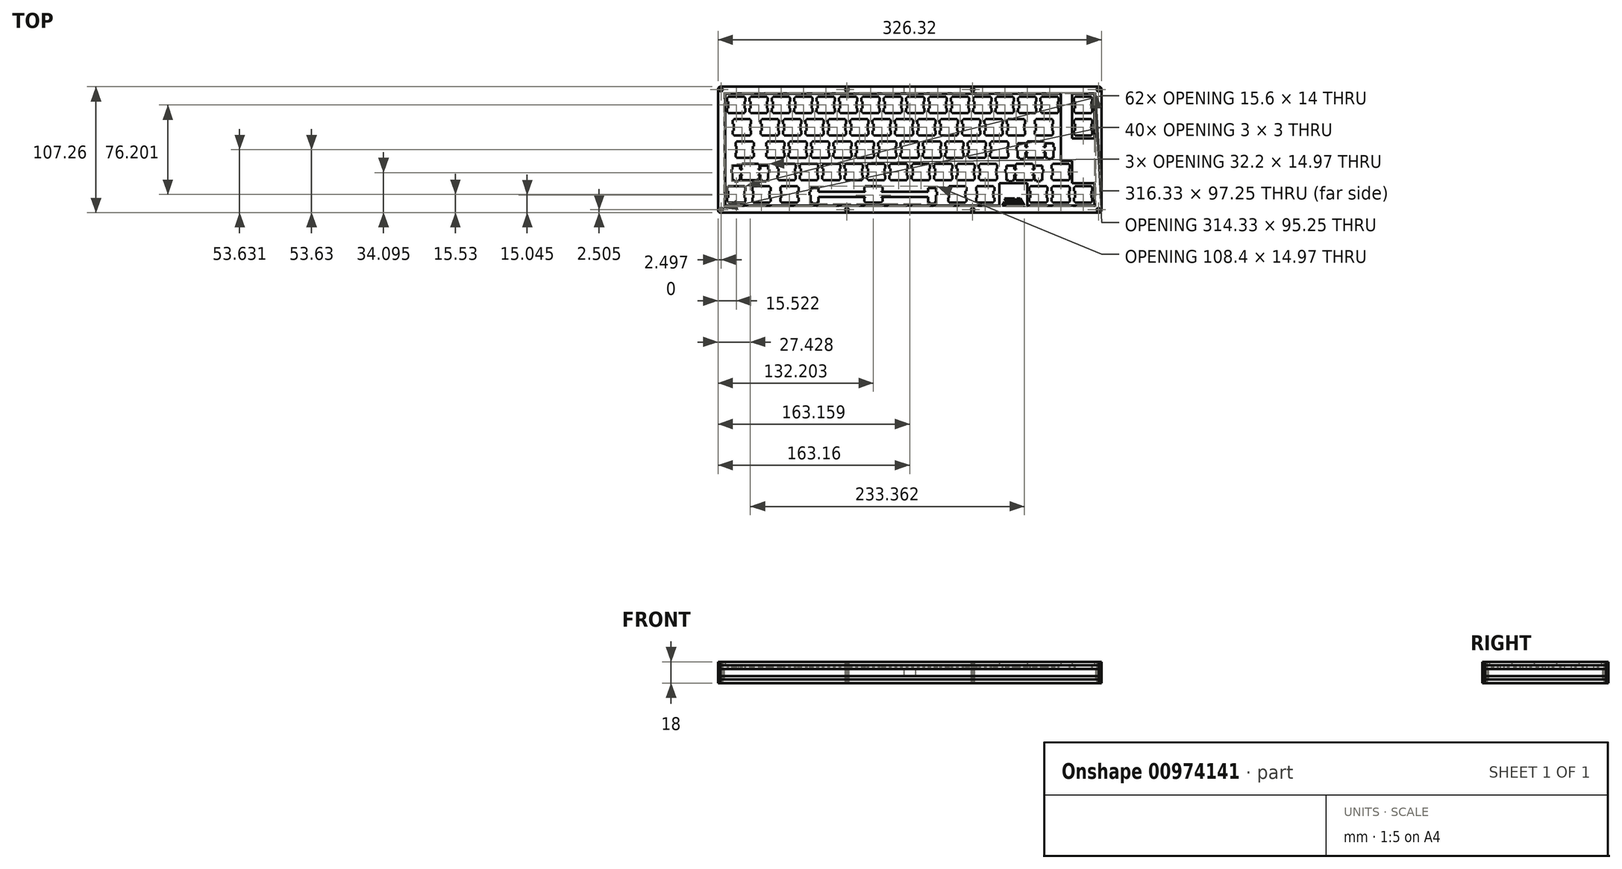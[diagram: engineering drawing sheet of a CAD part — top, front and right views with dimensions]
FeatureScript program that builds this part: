
annotation { "Feature Type Name" : "Feature", "Feature Type Description" : "" }
export const myFeature = defineFeature(function(context is Context, id is Id, definition is map)
    precondition{}
    {
        {
            assignVariable(context, id + "F0", {"name" : "Thickness", "anyValue" : 3});
        }
        {
            var Q0;
            Q0=qCreatedBy(makeId("Top.planeOp"),FACE);
            var sketch = newSketch(context, id + "F1", { "sketchPlane" : qUnion([Q0])});
            skLineSegment(sketch, "E0", {"start": v(161.16, 53.62) * mm, "end": v(161.32, 53.62) * mm});
            skLineSegment(sketch, "E1", {"start": v(161.32, 53.62) * mm, "end": v(161.48, 53.6) * mm});
            skLineSegment(sketch, "E2", {"start": v(161.48, 53.6) * mm, "end": v(161.63, 53.57) * mm});
            skLineSegment(sketch, "E3", {"start": v(161.63, 53.57) * mm, "end": v(161.78, 53.53) * mm});
            skLineSegment(sketch, "E4", {"start": v(161.78, 53.53) * mm, "end": v(161.93, 53.47) * mm});
            skLineSegment(sketch, "E5", {"start": v(161.93, 53.47) * mm, "end": v(162.07, 53.4) * mm});
            skLineSegment(sketch, "E6", {"start": v(162.07, 53.4) * mm, "end": v(162.2, 53.33) * mm});
            skLineSegment(sketch, "E7", {"start": v(162.2, 53.33) * mm, "end": v(162.34, 53.24) * mm});
            skLineSegment(sketch, "E8", {"start": v(162.34, 53.24) * mm, "end": v(162.46, 53.15) * mm});
            skLineSegment(sketch, "E9", {"start": v(162.46, 53.15) * mm, "end": v(162.58, 53.04) * mm});
            skLineSegment(sketch, "E10", {"start": v(162.58, 53.04) * mm, "end": v(162.68, 52.92) * mm});
            skLineSegment(sketch, "E11", {"start": v(162.68, 52.92) * mm, "end": v(162.78, 52.8) * mm});
            skLineSegment(sketch, "E12", {"start": v(162.78, 52.8) * mm, "end": v(162.87, 52.67) * mm});
            skLineSegment(sketch, "E13", {"start": v(162.87, 52.67) * mm, "end": v(162.94, 52.53) * mm});
            skLineSegment(sketch, "E14", {"start": v(162.94, 52.53) * mm, "end": v(163, 52.4) * mm});
            skLineSegment(sketch, "E15", {"start": v(163, 52.4) * mm, "end": v(163.06, 52.24) * mm});
            skLineSegment(sketch, "E16", {"start": v(163.06, 52.24) * mm, "end": v(163.1, 52.1) * mm});
            skLineSegment(sketch, "E17", {"start": v(163.1, 52.1) * mm, "end": v(163.14, 51.94) * mm});
            skLineSegment(sketch, "E18", {"start": v(163.14, 51.94) * mm, "end": v(163.16, 51.78) * mm});
            skLineSegment(sketch, "E19", {"start": v(163.16, 51.78) * mm, "end": v(163.16, 51.62) * mm});
            skLineSegment(sketch, "E20", {"start": v(163.16, 51.62) * mm, "end": v(163.16, -51.62) * mm});
            skLineSegment(sketch, "E21", {"start": v(163.16, -51.62) * mm, "end": v(163.16, -51.78) * mm});
            skLineSegment(sketch, "E22", {"start": v(163.16, -51.78) * mm, "end": v(163.14, -51.94) * mm});
            skLineSegment(sketch, "E23", {"start": v(163.14, -51.94) * mm, "end": v(163.1, -52.1) * mm});
            skLineSegment(sketch, "E24", {"start": v(163.1, -52.1) * mm, "end": v(163.06, -52.25) * mm});
            skLineSegment(sketch, "E25", {"start": v(163.06, -52.25) * mm, "end": v(163, -52.4) * mm});
            skLineSegment(sketch, "E26", {"start": v(163, -52.4) * mm, "end": v(162.94, -52.53) * mm});
            skLineSegment(sketch, "E27", {"start": v(162.94, -52.53) * mm, "end": v(162.87, -52.67) * mm});
            skLineSegment(sketch, "E28", {"start": v(162.87, -52.67) * mm, "end": v(162.78, -52.8) * mm});
            skLineSegment(sketch, "E29", {"start": v(162.78, -52.8) * mm, "end": v(162.68, -52.92) * mm});
            skLineSegment(sketch, "E30", {"start": v(162.68, -52.92) * mm, "end": v(162.58, -53.04) * mm});
            skLineSegment(sketch, "E31", {"start": v(162.58, -53.04) * mm, "end": v(162.46, -53.15) * mm});
            skLineSegment(sketch, "E32", {"start": v(162.46, -53.15) * mm, "end": v(162.34, -53.24) * mm});
            skLineSegment(sketch, "E33", {"start": v(162.34, -53.24) * mm, "end": v(162.2, -53.33) * mm});
            skLineSegment(sketch, "E34", {"start": v(162.2, -53.33) * mm, "end": v(162.07, -53.4) * mm});
            skLineSegment(sketch, "E35", {"start": v(162.07, -53.4) * mm, "end": v(161.93, -53.47) * mm});
            skLineSegment(sketch, "E36", {"start": v(161.93, -53.47) * mm, "end": v(161.78, -53.53) * mm});
            skLineSegment(sketch, "E37", {"start": v(161.78, -53.53) * mm, "end": v(161.63, -53.57) * mm});
            skLineSegment(sketch, "E38", {"start": v(161.63, -53.57) * mm, "end": v(161.48, -53.6) * mm});
            skLineSegment(sketch, "E39", {"start": v(161.48, -53.6) * mm, "end": v(161.32, -53.62) * mm});
            skLineSegment(sketch, "E40", {"start": v(161.32, -53.62) * mm, "end": v(161.16, -53.63) * mm});
            skLineSegment(sketch, "E41", {"start": v(161.16, -53.63) * mm, "end": v(-161.16, -53.63) * mm});
            skLineSegment(sketch, "E42", {"start": v(-161.16, -53.63) * mm, "end": v(-161.32, -53.62) * mm});
            skLineSegment(sketch, "E43", {"start": v(-161.32, -53.62) * mm, "end": v(-161.48, -53.6) * mm});
            skLineSegment(sketch, "E44", {"start": v(-161.48, -53.6) * mm, "end": v(-161.63, -53.57) * mm});
            skLineSegment(sketch, "E45", {"start": v(-161.63, -53.57) * mm, "end": v(-161.78, -53.53) * mm});
            skLineSegment(sketch, "E46", {"start": v(-161.78, -53.53) * mm, "end": v(-161.93, -53.47) * mm});
            skLineSegment(sketch, "E47", {"start": v(-161.93, -53.47) * mm, "end": v(-162.07, -53.4) * mm});
            skLineSegment(sketch, "E48", {"start": v(-162.07, -53.4) * mm, "end": v(-162.2, -53.33) * mm});
            skLineSegment(sketch, "E49", {"start": v(-162.2, -53.33) * mm, "end": v(-162.34, -53.24) * mm});
            skLineSegment(sketch, "E50", {"start": v(-162.34, -53.24) * mm, "end": v(-162.46, -53.15) * mm});
            skLineSegment(sketch, "E51", {"start": v(-162.46, -53.15) * mm, "end": v(-162.58, -53.04) * mm});
            skLineSegment(sketch, "E52", {"start": v(-162.58, -53.04) * mm, "end": v(-162.68, -52.92) * mm});
            skLineSegment(sketch, "E53", {"start": v(-162.68, -52.92) * mm, "end": v(-162.78, -52.8) * mm});
            skLineSegment(sketch, "E54", {"start": v(-162.78, -52.8) * mm, "end": v(-162.87, -52.67) * mm});
            skLineSegment(sketch, "E55", {"start": v(-162.87, -52.67) * mm, "end": v(-162.95, -52.53) * mm});
            skLineSegment(sketch, "E56", {"start": v(-162.95, -52.53) * mm, "end": v(-163.01, -52.4) * mm});
            skLineSegment(sketch, "E57", {"start": v(-163.01, -52.4) * mm, "end": v(-163.07, -52.25) * mm});
            skLineSegment(sketch, "E58", {"start": v(-163.07, -52.25) * mm, "end": v(-163.1, -52.1) * mm});
            skLineSegment(sketch, "E59", {"start": v(-163.1, -52.1) * mm, "end": v(-163.14, -51.94) * mm});
            skLineSegment(sketch, "E60", {"start": v(-163.14, -51.94) * mm, "end": v(-163.16, -51.78) * mm});
            skLineSegment(sketch, "E61", {"start": v(-163.16, -51.78) * mm, "end": v(-163.16, -51.63) * mm});
            skLineSegment(sketch, "E62", {"start": v(-163.16, -51.63) * mm, "end": v(-163.16, 51.62) * mm});
            skLineSegment(sketch, "E63", {"start": v(-163.16, 51.62) * mm, "end": v(-163.16, 51.78) * mm});
            skLineSegment(sketch, "E64", {"start": v(-163.16, 51.78) * mm, "end": v(-163.14, 51.94) * mm});
            skLineSegment(sketch, "E65", {"start": v(-163.14, 51.94) * mm, "end": v(-163.1, 52.1) * mm});
            skLineSegment(sketch, "E66", {"start": v(-163.1, 52.1) * mm, "end": v(-163.07, 52.24) * mm});
            skLineSegment(sketch, "E67", {"start": v(-163.07, 52.24) * mm, "end": v(-163.01, 52.4) * mm});
            skLineSegment(sketch, "E68", {"start": v(-163.01, 52.4) * mm, "end": v(-162.95, 52.53) * mm});
            skLineSegment(sketch, "E69", {"start": v(-162.95, 52.53) * mm, "end": v(-162.87, 52.67) * mm});
            skLineSegment(sketch, "E70", {"start": v(-162.87, 52.67) * mm, "end": v(-162.78, 52.8) * mm});
            skLineSegment(sketch, "E71", {"start": v(-162.78, 52.8) * mm, "end": v(-162.68, 52.92) * mm});
            skLineSegment(sketch, "E72", {"start": v(-162.68, 52.92) * mm, "end": v(-162.58, 53.04) * mm});
            skLineSegment(sketch, "E73", {"start": v(-162.58, 53.04) * mm, "end": v(-162.46, 53.15) * mm});
            skLineSegment(sketch, "E74", {"start": v(-162.46, 53.15) * mm, "end": v(-162.34, 53.24) * mm});
            skLineSegment(sketch, "E75", {"start": v(-162.34, 53.24) * mm, "end": v(-162.2, 53.33) * mm});
            skLineSegment(sketch, "E76", {"start": v(-162.2, 53.33) * mm, "end": v(-162.07, 53.4) * mm});
            skLineSegment(sketch, "E77", {"start": v(-162.07, 53.4) * mm, "end": v(-161.93, 53.47) * mm});
            skLineSegment(sketch, "E78", {"start": v(-161.93, 53.47) * mm, "end": v(-161.78, 53.53) * mm});
            skLineSegment(sketch, "E79", {"start": v(-161.78, 53.53) * mm, "end": v(-161.63, 53.57) * mm});
            skLineSegment(sketch, "E80", {"start": v(-161.63, 53.57) * mm, "end": v(-161.48, 53.6) * mm});
            skLineSegment(sketch, "E81", {"start": v(-161.48, 53.6) * mm, "end": v(-161.32, 53.62) * mm});
            skLineSegment(sketch, "E82", {"start": v(-161.32, 53.62) * mm, "end": v(-161.16, 53.63) * mm});
            skLineSegment(sketch, "E83", {"start": v(-161.16, 53.63) * mm, "end": v(161.16, 53.62) * mm});
            skLineSegment(sketch, "E84", {"start": v(160.2, -49.7) * mm, "end": v(159.78, -49.91) * mm});
            skLineSegment(sketch, "E85", {"start": v(159.78, -49.91) * mm, "end": v(159.45, -50.24) * mm});
            skLineSegment(sketch, "E86", {"start": v(159.45, -50.24) * mm, "end": v(159.24, -50.66) * mm});
            skLineSegment(sketch, "E87", {"start": v(159.24, -50.66) * mm, "end": v(159.16, -51.13) * mm});
            skLineSegment(sketch, "E88", {"start": v(159.16, -51.13) * mm, "end": v(159.24, -51.59) * mm});
            skLineSegment(sketch, "E89", {"start": v(159.24, -51.59) * mm, "end": v(159.45, -52) * mm});
            skLineSegment(sketch, "E90", {"start": v(159.45, -52) * mm, "end": v(159.78, -52.34) * mm});
            skLineSegment(sketch, "E91", {"start": v(159.78, -52.34) * mm, "end": v(160.2, -52.55) * mm});
            skLineSegment(sketch, "E92", {"start": v(160.2, -52.55) * mm, "end": v(160.66, -52.63) * mm});
            skLineSegment(sketch, "E93", {"start": v(160.66, -52.63) * mm, "end": v(161.13, -52.55) * mm});
            skLineSegment(sketch, "E94", {"start": v(161.13, -52.55) * mm, "end": v(161.54, -52.34) * mm});
            skLineSegment(sketch, "E95", {"start": v(161.54, -52.34) * mm, "end": v(161.88, -52) * mm});
            skLineSegment(sketch, "E96", {"start": v(161.88, -52) * mm, "end": v(162.09, -51.59) * mm});
            skLineSegment(sketch, "E97", {"start": v(162.09, -51.59) * mm, "end": v(162.16, -51.13) * mm});
            skLineSegment(sketch, "E98", {"start": v(162.16, -51.13) * mm, "end": v(162.09, -50.66) * mm});
            skLineSegment(sketch, "E99", {"start": v(162.09, -50.66) * mm, "end": v(161.88, -50.24) * mm});
            skLineSegment(sketch, "E100", {"start": v(161.88, -50.24) * mm, "end": v(161.54, -49.91) * mm});
            skLineSegment(sketch, "E101", {"start": v(161.54, -49.91) * mm, "end": v(161.13, -49.7) * mm});
            skLineSegment(sketch, "E102", {"start": v(161.13, -49.7) * mm, "end": v(160.66, -49.63) * mm});
            skLineSegment(sketch, "E103", {"start": v(160.66, -49.63) * mm, "end": v(160.2, -49.7) * mm});
            skLineSegment(sketch, "E104", {"start": v(53.1, -49.7) * mm, "end": v(52.67, -49.91) * mm});
            skLineSegment(sketch, "E105", {"start": v(52.67, -49.91) * mm, "end": v(52.34, -50.24) * mm});
            skLineSegment(sketch, "E106", {"start": v(52.34, -50.24) * mm, "end": v(52.13, -50.66) * mm});
            skLineSegment(sketch, "E107", {"start": v(52.13, -50.66) * mm, "end": v(52.05, -51.13) * mm});
            skLineSegment(sketch, "E108", {"start": v(52.05, -51.13) * mm, "end": v(52.13, -51.59) * mm});
            skLineSegment(sketch, "E109", {"start": v(52.13, -51.59) * mm, "end": v(52.34, -52) * mm});
            skLineSegment(sketch, "E110", {"start": v(52.34, -52) * mm, "end": v(52.67, -52.34) * mm});
            skLineSegment(sketch, "E111", {"start": v(52.67, -52.34) * mm, "end": v(53.1, -52.55) * mm});
            skLineSegment(sketch, "E112", {"start": v(53.1, -52.55) * mm, "end": v(53.55, -52.63) * mm});
            skLineSegment(sketch, "E113", {"start": v(53.55, -52.63) * mm, "end": v(54.02, -52.55) * mm});
            skLineSegment(sketch, "E114", {"start": v(54.02, -52.55) * mm, "end": v(54.44, -52.34) * mm});
            skLineSegment(sketch, "E115", {"start": v(54.44, -52.34) * mm, "end": v(54.77, -52) * mm});
            skLineSegment(sketch, "E116", {"start": v(54.77, -52) * mm, "end": v(54.98, -51.59) * mm});
            skLineSegment(sketch, "E117", {"start": v(54.98, -51.59) * mm, "end": v(55.05, -51.13) * mm});
            skLineSegment(sketch, "E118", {"start": v(55.05, -51.13) * mm, "end": v(54.98, -50.66) * mm});
            skLineSegment(sketch, "E119", {"start": v(54.98, -50.66) * mm, "end": v(54.77, -50.24) * mm});
            skLineSegment(sketch, "E120", {"start": v(54.77, -50.24) * mm, "end": v(54.44, -49.91) * mm});
            skLineSegment(sketch, "E121", {"start": v(54.44, -49.91) * mm, "end": v(54.02, -49.7) * mm});
            skLineSegment(sketch, "E122", {"start": v(54.02, -49.7) * mm, "end": v(53.55, -49.63) * mm});
            skLineSegment(sketch, "E123", {"start": v(53.55, -49.63) * mm, "end": v(53.1, -49.7) * mm});
            skLineSegment(sketch, "E124", {"start": v(-54.02, -49.7) * mm, "end": v(-54.44, -49.91) * mm});
            skLineSegment(sketch, "E125", {"start": v(-54.44, -49.91) * mm, "end": v(-54.77, -50.24) * mm});
            skLineSegment(sketch, "E126", {"start": v(-54.77, -50.24) * mm, "end": v(-54.98, -50.66) * mm});
            skLineSegment(sketch, "E127", {"start": v(-54.98, -50.66) * mm, "end": v(-55.06, -51.13) * mm});
            skLineSegment(sketch, "E128", {"start": v(-55.06, -51.13) * mm, "end": v(-54.98, -51.59) * mm});
            skLineSegment(sketch, "E129", {"start": v(-54.98, -51.59) * mm, "end": v(-54.77, -52) * mm});
            skLineSegment(sketch, "E130", {"start": v(-54.77, -52) * mm, "end": v(-54.44, -52.34) * mm});
            skLineSegment(sketch, "E131", {"start": v(-54.44, -52.34) * mm, "end": v(-54.02, -52.55) * mm});
            skLineSegment(sketch, "E132", {"start": v(-54.02, -52.55) * mm, "end": v(-53.55, -52.63) * mm});
            skLineSegment(sketch, "E133", {"start": v(-53.55, -52.63) * mm, "end": v(-53.1, -52.55) * mm});
            skLineSegment(sketch, "E134", {"start": v(-53.1, -52.55) * mm, "end": v(-52.67, -52.34) * mm});
            skLineSegment(sketch, "E135", {"start": v(-52.67, -52.34) * mm, "end": v(-52.34, -52) * mm});
            skLineSegment(sketch, "E136", {"start": v(-52.34, -52) * mm, "end": v(-52.13, -51.59) * mm});
            skLineSegment(sketch, "E137", {"start": v(-52.13, -51.59) * mm, "end": v(-52.06, -51.13) * mm});
            skLineSegment(sketch, "E138", {"start": v(-52.06, -51.13) * mm, "end": v(-52.13, -50.66) * mm});
            skLineSegment(sketch, "E139", {"start": v(-52.13, -50.66) * mm, "end": v(-52.34, -50.24) * mm});
            skLineSegment(sketch, "E140", {"start": v(-52.34, -50.24) * mm, "end": v(-52.67, -49.91) * mm});
            skLineSegment(sketch, "E141", {"start": v(-52.67, -49.91) * mm, "end": v(-53.1, -49.7) * mm});
            skLineSegment(sketch, "E142", {"start": v(-53.1, -49.7) * mm, "end": v(-53.55, -49.63) * mm});
            skLineSegment(sketch, "E143", {"start": v(-53.55, -49.63) * mm, "end": v(-54.02, -49.7) * mm});
            skLineSegment(sketch, "E144", {"start": v(-161.13, -49.7) * mm, "end": v(-161.54, -49.91) * mm});
            skLineSegment(sketch, "E145", {"start": v(-161.54, -49.91) * mm, "end": v(-161.88, -50.24) * mm});
            skLineSegment(sketch, "E146", {"start": v(-161.88, -50.24) * mm, "end": v(-162.1, -50.66) * mm});
            skLineSegment(sketch, "E147", {"start": v(-162.1, -50.66) * mm, "end": v(-162.16, -51.13) * mm});
            skLineSegment(sketch, "E148", {"start": v(-162.16, -51.13) * mm, "end": v(-162.1, -51.59) * mm});
            skLineSegment(sketch, "E149", {"start": v(-162.1, -51.59) * mm, "end": v(-161.88, -52) * mm});
            skLineSegment(sketch, "E150", {"start": v(-161.88, -52) * mm, "end": v(-161.54, -52.34) * mm});
            skLineSegment(sketch, "E151", {"start": v(-161.54, -52.34) * mm, "end": v(-161.13, -52.55) * mm});
            skLineSegment(sketch, "E152", {"start": v(-161.13, -52.55) * mm, "end": v(-160.66, -52.63) * mm});
            skLineSegment(sketch, "E153", {"start": v(-160.66, -52.63) * mm, "end": v(-160.2, -52.55) * mm});
            skLineSegment(sketch, "E154", {"start": v(-160.2, -52.55) * mm, "end": v(-159.78, -52.34) * mm});
            skLineSegment(sketch, "E155", {"start": v(-159.78, -52.34) * mm, "end": v(-159.45, -52) * mm});
            skLineSegment(sketch, "E156", {"start": v(-159.45, -52) * mm, "end": v(-159.24, -51.59) * mm});
            skLineSegment(sketch, "E157", {"start": v(-159.24, -51.59) * mm, "end": v(-159.16, -51.13) * mm});
            skLineSegment(sketch, "E158", {"start": v(-159.16, -51.13) * mm, "end": v(-159.24, -50.66) * mm});
            skLineSegment(sketch, "E159", {"start": v(-159.24, -50.66) * mm, "end": v(-159.45, -50.24) * mm});
            skLineSegment(sketch, "E160", {"start": v(-159.45, -50.24) * mm, "end": v(-159.78, -49.91) * mm});
            skLineSegment(sketch, "E161", {"start": v(-159.78, -49.91) * mm, "end": v(-160.2, -49.7) * mm});
            skLineSegment(sketch, "E162", {"start": v(-160.2, -49.7) * mm, "end": v(-160.66, -49.63) * mm});
            skLineSegment(sketch, "E163", {"start": v(-160.66, -49.63) * mm, "end": v(-161.13, -49.7) * mm});
            skLineSegment(sketch, "E164", {"start": v(-54.02, 52.55) * mm, "end": v(-54.44, 52.34) * mm});
            skLineSegment(sketch, "E165", {"start": v(-54.44, 52.34) * mm, "end": v(-54.77, 52) * mm});
            skLineSegment(sketch, "E166", {"start": v(-54.77, 52) * mm, "end": v(-54.98, 51.59) * mm});
            skLineSegment(sketch, "E167", {"start": v(-54.98, 51.59) * mm, "end": v(-55.06, 51.12) * mm});
            skLineSegment(sketch, "E168", {"start": v(-55.06, 51.12) * mm, "end": v(-54.98, 50.66) * mm});
            skLineSegment(sketch, "E169", {"start": v(-54.98, 50.66) * mm, "end": v(-54.77, 50.24) * mm});
            skLineSegment(sketch, "E170", {"start": v(-54.77, 50.24) * mm, "end": v(-54.44, 49.91) * mm});
            skLineSegment(sketch, "E171", {"start": v(-54.44, 49.91) * mm, "end": v(-54.02, 49.7) * mm});
            skLineSegment(sketch, "E172", {"start": v(-54.02, 49.7) * mm, "end": v(-53.55, 49.62) * mm});
            skLineSegment(sketch, "E173", {"start": v(-53.55, 49.62) * mm, "end": v(-53.1, 49.7) * mm});
            skLineSegment(sketch, "E174", {"start": v(-53.1, 49.7) * mm, "end": v(-52.67, 49.91) * mm});
            skLineSegment(sketch, "E175", {"start": v(-52.67, 49.91) * mm, "end": v(-52.34, 50.24) * mm});
            skLineSegment(sketch, "E176", {"start": v(-52.34, 50.24) * mm, "end": v(-52.13, 50.66) * mm});
            skLineSegment(sketch, "E177", {"start": v(-52.13, 50.66) * mm, "end": v(-52.06, 51.12) * mm});
            skLineSegment(sketch, "E178", {"start": v(-52.06, 51.12) * mm, "end": v(-52.13, 51.59) * mm});
            skLineSegment(sketch, "E179", {"start": v(-52.13, 51.59) * mm, "end": v(-52.34, 52) * mm});
            skLineSegment(sketch, "E180", {"start": v(-52.34, 52) * mm, "end": v(-52.67, 52.34) * mm});
            skLineSegment(sketch, "E181", {"start": v(-52.67, 52.34) * mm, "end": v(-53.1, 52.55) * mm});
            skLineSegment(sketch, "E182", {"start": v(-53.1, 52.55) * mm, "end": v(-53.55, 52.62) * mm});
            skLineSegment(sketch, "E183", {"start": v(-53.55, 52.62) * mm, "end": v(-54.02, 52.55) * mm});
            skLineSegment(sketch, "E184", {"start": v(53.1, 52.55) * mm, "end": v(52.67, 52.34) * mm});
            skLineSegment(sketch, "E185", {"start": v(52.67, 52.34) * mm, "end": v(52.34, 52) * mm});
            skLineSegment(sketch, "E186", {"start": v(52.34, 52) * mm, "end": v(52.13, 51.59) * mm});
            skLineSegment(sketch, "E187", {"start": v(52.13, 51.59) * mm, "end": v(52.05, 51.12) * mm});
            skLineSegment(sketch, "E188", {"start": v(52.05, 51.12) * mm, "end": v(52.13, 50.66) * mm});
            skLineSegment(sketch, "E189", {"start": v(52.13, 50.66) * mm, "end": v(52.34, 50.24) * mm});
            skLineSegment(sketch, "E190", {"start": v(52.34, 50.24) * mm, "end": v(52.67, 49.91) * mm});
            skLineSegment(sketch, "E191", {"start": v(52.67, 49.91) * mm, "end": v(53.1, 49.7) * mm});
            skLineSegment(sketch, "E192", {"start": v(53.1, 49.7) * mm, "end": v(53.55, 49.62) * mm});
            skLineSegment(sketch, "E193", {"start": v(53.55, 49.62) * mm, "end": v(54.02, 49.7) * mm});
            skLineSegment(sketch, "E194", {"start": v(54.02, 49.7) * mm, "end": v(54.44, 49.91) * mm});
            skLineSegment(sketch, "E195", {"start": v(54.44, 49.91) * mm, "end": v(54.77, 50.24) * mm});
            skLineSegment(sketch, "E196", {"start": v(54.77, 50.24) * mm, "end": v(54.98, 50.66) * mm});
            skLineSegment(sketch, "E197", {"start": v(54.98, 50.66) * mm, "end": v(55.05, 51.12) * mm});
            skLineSegment(sketch, "E198", {"start": v(55.05, 51.12) * mm, "end": v(54.98, 51.59) * mm});
            skLineSegment(sketch, "E199", {"start": v(54.98, 51.59) * mm, "end": v(54.77, 52) * mm});
            skLineSegment(sketch, "E200", {"start": v(54.77, 52) * mm, "end": v(54.44, 52.34) * mm});
            skLineSegment(sketch, "E201", {"start": v(54.44, 52.34) * mm, "end": v(54.02, 52.55) * mm});
            skLineSegment(sketch, "E202", {"start": v(54.02, 52.55) * mm, "end": v(53.55, 52.62) * mm});
            skLineSegment(sketch, "E203", {"start": v(53.55, 52.62) * mm, "end": v(53.1, 52.55) * mm});
            skLineSegment(sketch, "E204", {"start": v(160.2, 52.55) * mm, "end": v(159.78, 52.34) * mm});
            skLineSegment(sketch, "E205", {"start": v(159.78, 52.34) * mm, "end": v(159.45, 52) * mm});
            skLineSegment(sketch, "E206", {"start": v(159.45, 52) * mm, "end": v(159.24, 51.59) * mm});
            skLineSegment(sketch, "E207", {"start": v(159.24, 51.59) * mm, "end": v(159.16, 51.12) * mm});
            skLineSegment(sketch, "E208", {"start": v(159.16, 51.12) * mm, "end": v(159.24, 50.66) * mm});
            skLineSegment(sketch, "E209", {"start": v(159.24, 50.66) * mm, "end": v(159.45, 50.24) * mm});
            skLineSegment(sketch, "E210", {"start": v(159.45, 50.24) * mm, "end": v(159.78, 49.91) * mm});
            skLineSegment(sketch, "E211", {"start": v(159.78, 49.91) * mm, "end": v(160.2, 49.7) * mm});
            skLineSegment(sketch, "E212", {"start": v(160.2, 49.7) * mm, "end": v(160.66, 49.62) * mm});
            skLineSegment(sketch, "E213", {"start": v(160.66, 49.62) * mm, "end": v(161.13, 49.7) * mm});
            skLineSegment(sketch, "E214", {"start": v(161.13, 49.7) * mm, "end": v(161.54, 49.91) * mm});
            skLineSegment(sketch, "E215", {"start": v(161.54, 49.91) * mm, "end": v(161.88, 50.24) * mm});
            skLineSegment(sketch, "E216", {"start": v(161.88, 50.24) * mm, "end": v(162.09, 50.66) * mm});
            skLineSegment(sketch, "E217", {"start": v(162.09, 50.66) * mm, "end": v(162.16, 51.12) * mm});
            skLineSegment(sketch, "E218", {"start": v(162.16, 51.12) * mm, "end": v(162.09, 51.59) * mm});
            skLineSegment(sketch, "E219", {"start": v(162.09, 51.59) * mm, "end": v(161.88, 52) * mm});
            skLineSegment(sketch, "E220", {"start": v(161.88, 52) * mm, "end": v(161.54, 52.34) * mm});
            skLineSegment(sketch, "E221", {"start": v(161.54, 52.34) * mm, "end": v(161.13, 52.55) * mm});
            skLineSegment(sketch, "E222", {"start": v(161.13, 52.55) * mm, "end": v(160.66, 52.62) * mm});
            skLineSegment(sketch, "E223", {"start": v(160.66, 52.62) * mm, "end": v(160.2, 52.55) * mm});
            skLineSegment(sketch, "E224", {"start": v(-161.13, 52.55) * mm, "end": v(-161.54, 52.34) * mm});
            skLineSegment(sketch, "E225", {"start": v(-161.54, 52.34) * mm, "end": v(-161.88, 52) * mm});
            skLineSegment(sketch, "E226", {"start": v(-161.88, 52) * mm, "end": v(-162.1, 51.59) * mm});
            skLineSegment(sketch, "E227", {"start": v(-162.1, 51.59) * mm, "end": v(-162.16, 51.12) * mm});
            skLineSegment(sketch, "E228", {"start": v(-162.16, 51.12) * mm, "end": v(-162.1, 50.66) * mm});
            skLineSegment(sketch, "E229", {"start": v(-162.1, 50.66) * mm, "end": v(-161.88, 50.24) * mm});
            skLineSegment(sketch, "E230", {"start": v(-161.88, 50.24) * mm, "end": v(-161.54, 49.91) * mm});
            skLineSegment(sketch, "E231", {"start": v(-161.54, 49.91) * mm, "end": v(-161.13, 49.7) * mm});
            skLineSegment(sketch, "E232", {"start": v(-161.13, 49.7) * mm, "end": v(-160.66, 49.62) * mm});
            skLineSegment(sketch, "E233", {"start": v(-160.66, 49.62) * mm, "end": v(-160.2, 49.7) * mm});
            skLineSegment(sketch, "E234", {"start": v(-160.2, 49.7) * mm, "end": v(-159.78, 49.91) * mm});
            skLineSegment(sketch, "E235", {"start": v(-159.78, 49.91) * mm, "end": v(-159.45, 50.24) * mm});
            skLineSegment(sketch, "E236", {"start": v(-159.45, 50.24) * mm, "end": v(-159.24, 50.66) * mm});
            skLineSegment(sketch, "E237", {"start": v(-159.24, 50.66) * mm, "end": v(-159.16, 51.12) * mm});
            skLineSegment(sketch, "E238", {"start": v(-159.16, 51.12) * mm, "end": v(-159.24, 51.59) * mm});
            skLineSegment(sketch, "E239", {"start": v(-159.24, 51.59) * mm, "end": v(-159.45, 52) * mm});
            skLineSegment(sketch, "E240", {"start": v(-159.45, 52) * mm, "end": v(-159.78, 52.34) * mm});
            skLineSegment(sketch, "E241", {"start": v(-159.78, 52.34) * mm, "end": v(-160.2, 52.55) * mm});
            skLineSegment(sketch, "E242", {"start": v(-160.2, 52.55) * mm, "end": v(-160.66, 52.62) * mm});
            skLineSegment(sketch, "E243", {"start": v(-160.66, 52.62) * mm, "end": v(-161.13, 52.55) * mm});
            skSolve(sketch);
        }
        {
            var Q0;
            Q0=makeQuery(id+"F1.imprint","IMPRINT",FACE,{"disambiguationData":[TD([[makeQuery(id+"F1.imprint","IMPRINT",EDGE,{"derivedFrom":sQuery(id+"F1.wireOp",EDGE,"E0")}),-1.0]])]});
            extrude(context, id + "F2", {"entities" : qUnion([Q0]), "depth" : (getVariable(context, 'Thickness')) * mm, "offsetDistance" : 25 * mm});
        }
        {
            var Q0;
            Q0=makeQuery(id+"F2.opExtrude","CAP_FACE",FACE,{"disambiguationData":[OSD([sQuery(id+"F1.wireOp",EDGE,"E0"),sQuery(id+"F1.wireOp",EDGE,"E1"),sQuery(id+"F1.wireOp",EDGE,"E2"),sQuery(id+"F1.wireOp",EDGE,"E3"),sQuery(id+"F1.wireOp",EDGE,"E4"),sQuery(id+"F1.wireOp",EDGE,"E5"),sQuery(id+"F1.wireOp",EDGE,"E6"),sQuery(id+"F1.wireOp",EDGE,"E7"),sQuery(id+"F1.wireOp",EDGE,"E8"),sQuery(id+"F1.wireOp",EDGE,"E9"),sQuery(id+"F1.wireOp",EDGE,"E10"),sQuery(id+"F1.wireOp",EDGE,"E11"),sQuery(id+"F1.wireOp",EDGE,"E12"),sQuery(id+"F1.wireOp",EDGE,"E13"),sQuery(id+"F1.wireOp",EDGE,"E14"),sQuery(id+"F1.wireOp",EDGE,"E15"),sQuery(id+"F1.wireOp",EDGE,"E16"),sQuery(id+"F1.wireOp",EDGE,"E17"),sQuery(id+"F1.wireOp",EDGE,"E18"),sQuery(id+"F1.wireOp",EDGE,"E19"),sQuery(id+"F1.wireOp",EDGE,"E20"),sQuery(id+"F1.wireOp",EDGE,"E21"),sQuery(id+"F1.wireOp",EDGE,"E22"),sQuery(id+"F1.wireOp",EDGE,"E23"),sQuery(id+"F1.wireOp",EDGE,"E24"),sQuery(id+"F1.wireOp",EDGE,"E25"),sQuery(id+"F1.wireOp",EDGE,"E26"),sQuery(id+"F1.wireOp",EDGE,"E27"),sQuery(id+"F1.wireOp",EDGE,"E28"),sQuery(id+"F1.wireOp",EDGE,"E29"),sQuery(id+"F1.wireOp",EDGE,"E30"),sQuery(id+"F1.wireOp",EDGE,"E31"),sQuery(id+"F1.wireOp",EDGE,"E32"),sQuery(id+"F1.wireOp",EDGE,"E33"),sQuery(id+"F1.wireOp",EDGE,"E34"),sQuery(id+"F1.wireOp",EDGE,"E35"),sQuery(id+"F1.wireOp",EDGE,"E36"),sQuery(id+"F1.wireOp",EDGE,"E37"),sQuery(id+"F1.wireOp",EDGE,"E38"),sQuery(id+"F1.wireOp",EDGE,"E39"),sQuery(id+"F1.wireOp",EDGE,"E40"),sQuery(id+"F1.wireOp",EDGE,"E41"),sQuery(id+"F1.wireOp",EDGE,"E42"),sQuery(id+"F1.wireOp",EDGE,"E43"),sQuery(id+"F1.wireOp",EDGE,"E44"),sQuery(id+"F1.wireOp",EDGE,"E45"),sQuery(id+"F1.wireOp",EDGE,"E46"),sQuery(id+"F1.wireOp",EDGE,"E47"),sQuery(id+"F1.wireOp",EDGE,"E48"),sQuery(id+"F1.wireOp",EDGE,"E49"),sQuery(id+"F1.wireOp",EDGE,"E50"),sQuery(id+"F1.wireOp",EDGE,"E51"),sQuery(id+"F1.wireOp",EDGE,"E52"),sQuery(id+"F1.wireOp",EDGE,"E53"),sQuery(id+"F1.wireOp",EDGE,"E54"),sQuery(id+"F1.wireOp",EDGE,"E55"),sQuery(id+"F1.wireOp",EDGE,"E56"),sQuery(id+"F1.wireOp",EDGE,"E57"),sQuery(id+"F1.wireOp",EDGE,"E58"),sQuery(id+"F1.wireOp",EDGE,"E59"),sQuery(id+"F1.wireOp",EDGE,"E60"),sQuery(id+"F1.wireOp",EDGE,"E61"),sQuery(id+"F1.wireOp",EDGE,"E62"),sQuery(id+"F1.wireOp",EDGE,"E63"),sQuery(id+"F1.wireOp",EDGE,"E64"),sQuery(id+"F1.wireOp",EDGE,"E65"),sQuery(id+"F1.wireOp",EDGE,"E66"),sQuery(id+"F1.wireOp",EDGE,"E67"),sQuery(id+"F1.wireOp",EDGE,"E68"),sQuery(id+"F1.wireOp",EDGE,"E69"),sQuery(id+"F1.wireOp",EDGE,"E70"),sQuery(id+"F1.wireOp",EDGE,"E71"),sQuery(id+"F1.wireOp",EDGE,"E72"),sQuery(id+"F1.wireOp",EDGE,"E73"),sQuery(id+"F1.wireOp",EDGE,"E74"),sQuery(id+"F1.wireOp",EDGE,"E75"),sQuery(id+"F1.wireOp",EDGE,"E76"),sQuery(id+"F1.wireOp",EDGE,"E77"),sQuery(id+"F1.wireOp",EDGE,"E78"),sQuery(id+"F1.wireOp",EDGE,"E79"),sQuery(id+"F1.wireOp",EDGE,"E80"),sQuery(id+"F1.wireOp",EDGE,"E81"),sQuery(id+"F1.wireOp",EDGE,"E82"),sQuery(id+"F1.wireOp",EDGE,"E83"),sQuery(id+"F1.wireOp",EDGE,"E84"),sQuery(id+"F1.wireOp",EDGE,"E85"),sQuery(id+"F1.wireOp",EDGE,"E86"),sQuery(id+"F1.wireOp",EDGE,"E87"),sQuery(id+"F1.wireOp",EDGE,"E88"),sQuery(id+"F1.wireOp",EDGE,"E89"),sQuery(id+"F1.wireOp",EDGE,"E90"),sQuery(id+"F1.wireOp",EDGE,"E91"),sQuery(id+"F1.wireOp",EDGE,"E92"),sQuery(id+"F1.wireOp",EDGE,"E93"),sQuery(id+"F1.wireOp",EDGE,"E94"),sQuery(id+"F1.wireOp",EDGE,"E95"),sQuery(id+"F1.wireOp",EDGE,"E96"),sQuery(id+"F1.wireOp",EDGE,"E97"),sQuery(id+"F1.wireOp",EDGE,"E98"),sQuery(id+"F1.wireOp",EDGE,"E99"),sQuery(id+"F1.wireOp",EDGE,"E100"),sQuery(id+"F1.wireOp",EDGE,"E101"),sQuery(id+"F1.wireOp",EDGE,"E102"),sQuery(id+"F1.wireOp",EDGE,"E103"),sQuery(id+"F1.wireOp",EDGE,"E104"),sQuery(id+"F1.wireOp",EDGE,"E105"),sQuery(id+"F1.wireOp",EDGE,"E106"),sQuery(id+"F1.wireOp",EDGE,"E107"),sQuery(id+"F1.wireOp",EDGE,"E108"),sQuery(id+"F1.wireOp",EDGE,"E109"),sQuery(id+"F1.wireOp",EDGE,"E110"),sQuery(id+"F1.wireOp",EDGE,"E111"),sQuery(id+"F1.wireOp",EDGE,"E112"),sQuery(id+"F1.wireOp",EDGE,"E113"),sQuery(id+"F1.wireOp",EDGE,"E114"),sQuery(id+"F1.wireOp",EDGE,"E115"),sQuery(id+"F1.wireOp",EDGE,"E116"),sQuery(id+"F1.wireOp",EDGE,"E117"),sQuery(id+"F1.wireOp",EDGE,"E118"),sQuery(id+"F1.wireOp",EDGE,"E119"),sQuery(id+"F1.wireOp",EDGE,"E120"),sQuery(id+"F1.wireOp",EDGE,"E121"),sQuery(id+"F1.wireOp",EDGE,"E122"),sQuery(id+"F1.wireOp",EDGE,"E123"),sQuery(id+"F1.wireOp",EDGE,"E124"),sQuery(id+"F1.wireOp",EDGE,"E125"),sQuery(id+"F1.wireOp",EDGE,"E126"),sQuery(id+"F1.wireOp",EDGE,"E127"),sQuery(id+"F1.wireOp",EDGE,"E128"),sQuery(id+"F1.wireOp",EDGE,"E129"),sQuery(id+"F1.wireOp",EDGE,"E130"),sQuery(id+"F1.wireOp",EDGE,"E131"),sQuery(id+"F1.wireOp",EDGE,"E132"),sQuery(id+"F1.wireOp",EDGE,"E133"),sQuery(id+"F1.wireOp",EDGE,"E134"),sQuery(id+"F1.wireOp",EDGE,"E135"),sQuery(id+"F1.wireOp",EDGE,"E136"),sQuery(id+"F1.wireOp",EDGE,"E137"),sQuery(id+"F1.wireOp",EDGE,"E138"),sQuery(id+"F1.wireOp",EDGE,"E139"),sQuery(id+"F1.wireOp",EDGE,"E140"),sQuery(id+"F1.wireOp",EDGE,"E141"),sQuery(id+"F1.wireOp",EDGE,"E142"),sQuery(id+"F1.wireOp",EDGE,"E143"),sQuery(id+"F1.wireOp",EDGE,"E144"),sQuery(id+"F1.wireOp",EDGE,"E145"),sQuery(id+"F1.wireOp",EDGE,"E146"),sQuery(id+"F1.wireOp",EDGE,"E147"),sQuery(id+"F1.wireOp",EDGE,"E148"),sQuery(id+"F1.wireOp",EDGE,"E149"),sQuery(id+"F1.wireOp",EDGE,"E150"),sQuery(id+"F1.wireOp",EDGE,"E151"),sQuery(id+"F1.wireOp",EDGE,"E152"),sQuery(id+"F1.wireOp",EDGE,"E153"),sQuery(id+"F1.wireOp",EDGE,"E154"),sQuery(id+"F1.wireOp",EDGE,"E155"),sQuery(id+"F1.wireOp",EDGE,"E156"),sQuery(id+"F1.wireOp",EDGE,"E157"),sQuery(id+"F1.wireOp",EDGE,"E158"),sQuery(id+"F1.wireOp",EDGE,"E159"),sQuery(id+"F1.wireOp",EDGE,"E160"),sQuery(id+"F1.wireOp",EDGE,"E161"),sQuery(id+"F1.wireOp",EDGE,"E162"),sQuery(id+"F1.wireOp",EDGE,"E163"),sQuery(id+"F1.wireOp",EDGE,"E164"),sQuery(id+"F1.wireOp",EDGE,"E165"),sQuery(id+"F1.wireOp",EDGE,"E166"),sQuery(id+"F1.wireOp",EDGE,"E167"),sQuery(id+"F1.wireOp",EDGE,"E168"),sQuery(id+"F1.wireOp",EDGE,"E169"),sQuery(id+"F1.wireOp",EDGE,"E170"),sQuery(id+"F1.wireOp",EDGE,"E171"),sQuery(id+"F1.wireOp",EDGE,"E172"),sQuery(id+"F1.wireOp",EDGE,"E173"),sQuery(id+"F1.wireOp",EDGE,"E174"),sQuery(id+"F1.wireOp",EDGE,"E175"),sQuery(id+"F1.wireOp",EDGE,"E176"),sQuery(id+"F1.wireOp",EDGE,"E177"),sQuery(id+"F1.wireOp",EDGE,"E178"),sQuery(id+"F1.wireOp",EDGE,"E179"),sQuery(id+"F1.wireOp",EDGE,"E180"),sQuery(id+"F1.wireOp",EDGE,"E181"),sQuery(id+"F1.wireOp",EDGE,"E182"),sQuery(id+"F1.wireOp",EDGE,"E183"),sQuery(id+"F1.wireOp",EDGE,"E184"),sQuery(id+"F1.wireOp",EDGE,"E185"),sQuery(id+"F1.wireOp",EDGE,"E186"),sQuery(id+"F1.wireOp",EDGE,"E187"),sQuery(id+"F1.wireOp",EDGE,"E188"),sQuery(id+"F1.wireOp",EDGE,"E189"),sQuery(id+"F1.wireOp",EDGE,"E190"),sQuery(id+"F1.wireOp",EDGE,"E191"),sQuery(id+"F1.wireOp",EDGE,"E192"),sQuery(id+"F1.wireOp",EDGE,"E193"),sQuery(id+"F1.wireOp",EDGE,"E194"),sQuery(id+"F1.wireOp",EDGE,"E195"),sQuery(id+"F1.wireOp",EDGE,"E196"),sQuery(id+"F1.wireOp",EDGE,"E197"),sQuery(id+"F1.wireOp",EDGE,"E198"),sQuery(id+"F1.wireOp",EDGE,"E199"),sQuery(id+"F1.wireOp",EDGE,"E200"),sQuery(id+"F1.wireOp",EDGE,"E201"),sQuery(id+"F1.wireOp",EDGE,"E202"),sQuery(id+"F1.wireOp",EDGE,"E203"),sQuery(id+"F1.wireOp",EDGE,"E204"),sQuery(id+"F1.wireOp",EDGE,"E205"),sQuery(id+"F1.wireOp",EDGE,"E206"),sQuery(id+"F1.wireOp",EDGE,"E207"),sQuery(id+"F1.wireOp",EDGE,"E208"),sQuery(id+"F1.wireOp",EDGE,"E209"),sQuery(id+"F1.wireOp",EDGE,"E210"),sQuery(id+"F1.wireOp",EDGE,"E211"),sQuery(id+"F1.wireOp",EDGE,"E212"),sQuery(id+"F1.wireOp",EDGE,"E213"),sQuery(id+"F1.wireOp",EDGE,"E214"),sQuery(id+"F1.wireOp",EDGE,"E215"),sQuery(id+"F1.wireOp",EDGE,"E216"),sQuery(id+"F1.wireOp",EDGE,"E217"),sQuery(id+"F1.wireOp",EDGE,"E218"),sQuery(id+"F1.wireOp",EDGE,"E219"),sQuery(id+"F1.wireOp",EDGE,"E220"),sQuery(id+"F1.wireOp",EDGE,"E221"),sQuery(id+"F1.wireOp",EDGE,"E222"),sQuery(id+"F1.wireOp",EDGE,"E223"),sQuery(id+"F1.wireOp",EDGE,"E224"),sQuery(id+"F1.wireOp",EDGE,"E225"),sQuery(id+"F1.wireOp",EDGE,"E226"),sQuery(id+"F1.wireOp",EDGE,"E227"),sQuery(id+"F1.wireOp",EDGE,"E228"),sQuery(id+"F1.wireOp",EDGE,"E229"),sQuery(id+"F1.wireOp",EDGE,"E230"),sQuery(id+"F1.wireOp",EDGE,"E231"),sQuery(id+"F1.wireOp",EDGE,"E232"),sQuery(id+"F1.wireOp",EDGE,"E233"),sQuery(id+"F1.wireOp",EDGE,"E234"),sQuery(id+"F1.wireOp",EDGE,"E235"),sQuery(id+"F1.wireOp",EDGE,"E236"),sQuery(id+"F1.wireOp",EDGE,"E237"),sQuery(id+"F1.wireOp",EDGE,"E238"),sQuery(id+"F1.wireOp",EDGE,"E239"),sQuery(id+"F1.wireOp",EDGE,"E240"),sQuery(id+"F1.wireOp",EDGE,"E241"),sQuery(id+"F1.wireOp",EDGE,"E242"),sQuery(id+"F1.wireOp",EDGE,"E243")])],"isStart":false});
            var sketch = newSketch(context, id + "F3", { "sketchPlane" : qUnion([Q0])});
            skLineSegment(sketch, "E244", {"start": v(161.16, 53.62) * mm, "end": v(161.32, 53.62) * mm});
            skLineSegment(sketch, "E245", {"start": v(161.32, 53.62) * mm, "end": v(161.48, 53.6) * mm});
            skLineSegment(sketch, "E246", {"start": v(161.48, 53.6) * mm, "end": v(161.63, 53.57) * mm});
            skLineSegment(sketch, "E247", {"start": v(161.63, 53.57) * mm, "end": v(161.78, 53.53) * mm});
            skLineSegment(sketch, "E248", {"start": v(161.78, 53.53) * mm, "end": v(161.93, 53.47) * mm});
            skLineSegment(sketch, "E249", {"start": v(161.93, 53.47) * mm, "end": v(162.07, 53.4) * mm});
            skLineSegment(sketch, "E250", {"start": v(162.07, 53.4) * mm, "end": v(162.2, 53.33) * mm});
            skLineSegment(sketch, "E251", {"start": v(162.2, 53.33) * mm, "end": v(162.34, 53.24) * mm});
            skLineSegment(sketch, "E252", {"start": v(162.34, 53.24) * mm, "end": v(162.46, 53.15) * mm});
            skLineSegment(sketch, "E253", {"start": v(162.46, 53.15) * mm, "end": v(162.58, 53.04) * mm});
            skLineSegment(sketch, "E254", {"start": v(162.58, 53.04) * mm, "end": v(162.68, 52.92) * mm});
            skLineSegment(sketch, "E255", {"start": v(162.68, 52.92) * mm, "end": v(162.78, 52.8) * mm});
            skLineSegment(sketch, "E256", {"start": v(162.78, 52.8) * mm, "end": v(162.87, 52.67) * mm});
            skLineSegment(sketch, "E257", {"start": v(162.87, 52.67) * mm, "end": v(162.94, 52.53) * mm});
            skLineSegment(sketch, "E258", {"start": v(162.94, 52.53) * mm, "end": v(163, 52.4) * mm});
            skLineSegment(sketch, "E259", {"start": v(163, 52.4) * mm, "end": v(163.06, 52.24) * mm});
            skLineSegment(sketch, "E260", {"start": v(163.06, 52.24) * mm, "end": v(163.1, 52.1) * mm});
            skLineSegment(sketch, "E261", {"start": v(163.1, 52.1) * mm, "end": v(163.14, 51.94) * mm});
            skLineSegment(sketch, "E262", {"start": v(163.14, 51.94) * mm, "end": v(163.16, 51.78) * mm});
            skLineSegment(sketch, "E263", {"start": v(163.16, 51.78) * mm, "end": v(163.16, 51.62) * mm});
            skLineSegment(sketch, "E264", {"start": v(163.16, 51.62) * mm, "end": v(163.16, -51.62) * mm});
            skLineSegment(sketch, "E265", {"start": v(163.16, -51.62) * mm, "end": v(163.16, -51.78) * mm});
            skLineSegment(sketch, "E266", {"start": v(163.16, -51.78) * mm, "end": v(163.14, -51.94) * mm});
            skLineSegment(sketch, "E267", {"start": v(163.14, -51.94) * mm, "end": v(163.1, -52.1) * mm});
            skLineSegment(sketch, "E268", {"start": v(163.1, -52.1) * mm, "end": v(163.06, -52.25) * mm});
            skLineSegment(sketch, "E269", {"start": v(163.06, -52.25) * mm, "end": v(163, -52.4) * mm});
            skLineSegment(sketch, "E270", {"start": v(163, -52.4) * mm, "end": v(162.94, -52.53) * mm});
            skLineSegment(sketch, "E271", {"start": v(162.94, -52.53) * mm, "end": v(162.87, -52.67) * mm});
            skLineSegment(sketch, "E272", {"start": v(162.87, -52.67) * mm, "end": v(162.78, -52.8) * mm});
            skLineSegment(sketch, "E273", {"start": v(162.78, -52.8) * mm, "end": v(162.68, -52.92) * mm});
            skLineSegment(sketch, "E274", {"start": v(162.68, -52.92) * mm, "end": v(162.58, -53.04) * mm});
            skLineSegment(sketch, "E275", {"start": v(162.58, -53.04) * mm, "end": v(162.46, -53.15) * mm});
            skLineSegment(sketch, "E276", {"start": v(162.46, -53.15) * mm, "end": v(162.34, -53.24) * mm});
            skLineSegment(sketch, "E277", {"start": v(162.34, -53.24) * mm, "end": v(162.2, -53.33) * mm});
            skLineSegment(sketch, "E278", {"start": v(162.2, -53.33) * mm, "end": v(162.07, -53.4) * mm});
            skLineSegment(sketch, "E279", {"start": v(162.07, -53.4) * mm, "end": v(161.93, -53.47) * mm});
            skLineSegment(sketch, "E280", {"start": v(161.93, -53.47) * mm, "end": v(161.78, -53.53) * mm});
            skLineSegment(sketch, "E281", {"start": v(161.78, -53.53) * mm, "end": v(161.63, -53.57) * mm});
            skLineSegment(sketch, "E282", {"start": v(161.63, -53.57) * mm, "end": v(161.48, -53.6) * mm});
            skLineSegment(sketch, "E283", {"start": v(161.48, -53.6) * mm, "end": v(161.32, -53.62) * mm});
            skLineSegment(sketch, "E284", {"start": v(161.32, -53.62) * mm, "end": v(161.16, -53.63) * mm});
            skLineSegment(sketch, "E285", {"start": v(161.16, -53.63) * mm, "end": v(-161.16, -53.63) * mm});
            skLineSegment(sketch, "E286", {"start": v(-161.16, -53.63) * mm, "end": v(-161.32, -53.62) * mm});
            skLineSegment(sketch, "E287", {"start": v(-161.32, -53.62) * mm, "end": v(-161.48, -53.6) * mm});
            skLineSegment(sketch, "E288", {"start": v(-161.48, -53.6) * mm, "end": v(-161.63, -53.57) * mm});
            skLineSegment(sketch, "E289", {"start": v(-161.63, -53.57) * mm, "end": v(-161.78, -53.53) * mm});
            skLineSegment(sketch, "E290", {"start": v(-161.78, -53.53) * mm, "end": v(-161.93, -53.47) * mm});
            skLineSegment(sketch, "E291", {"start": v(-161.93, -53.47) * mm, "end": v(-162.07, -53.4) * mm});
            skLineSegment(sketch, "E292", {"start": v(-162.07, -53.4) * mm, "end": v(-162.2, -53.33) * mm});
            skLineSegment(sketch, "E293", {"start": v(-162.2, -53.33) * mm, "end": v(-162.34, -53.24) * mm});
            skLineSegment(sketch, "E294", {"start": v(-162.34, -53.24) * mm, "end": v(-162.46, -53.15) * mm});
            skLineSegment(sketch, "E295", {"start": v(-162.46, -53.15) * mm, "end": v(-162.58, -53.04) * mm});
            skLineSegment(sketch, "E296", {"start": v(-162.58, -53.04) * mm, "end": v(-162.68, -52.92) * mm});
            skLineSegment(sketch, "E297", {"start": v(-162.68, -52.92) * mm, "end": v(-162.78, -52.8) * mm});
            skLineSegment(sketch, "E298", {"start": v(-162.78, -52.8) * mm, "end": v(-162.87, -52.67) * mm});
            skLineSegment(sketch, "E299", {"start": v(-162.87, -52.67) * mm, "end": v(-162.95, -52.53) * mm});
            skLineSegment(sketch, "E300", {"start": v(-162.95, -52.53) * mm, "end": v(-163.01, -52.4) * mm});
            skLineSegment(sketch, "E301", {"start": v(-163.01, -52.4) * mm, "end": v(-163.07, -52.25) * mm});
            skLineSegment(sketch, "E302", {"start": v(-163.07, -52.25) * mm, "end": v(-163.1, -52.1) * mm});
            skLineSegment(sketch, "E303", {"start": v(-163.1, -52.1) * mm, "end": v(-163.14, -51.94) * mm});
            skLineSegment(sketch, "E304", {"start": v(-163.14, -51.94) * mm, "end": v(-163.16, -51.78) * mm});
            skLineSegment(sketch, "E305", {"start": v(-163.16, -51.78) * mm, "end": v(-163.16, -51.63) * mm});
            skLineSegment(sketch, "E306", {"start": v(-163.16, -51.63) * mm, "end": v(-163.16, 51.62) * mm});
            skLineSegment(sketch, "E307", {"start": v(-163.16, 51.62) * mm, "end": v(-163.16, 51.78) * mm});
            skLineSegment(sketch, "E308", {"start": v(-163.16, 51.78) * mm, "end": v(-163.14, 51.94) * mm});
            skLineSegment(sketch, "E309", {"start": v(-163.14, 51.94) * mm, "end": v(-163.1, 52.1) * mm});
            skLineSegment(sketch, "E310", {"start": v(-163.1, 52.1) * mm, "end": v(-163.07, 52.24) * mm});
            skLineSegment(sketch, "E311", {"start": v(-163.07, 52.24) * mm, "end": v(-163.01, 52.4) * mm});
            skLineSegment(sketch, "E312", {"start": v(-163.01, 52.4) * mm, "end": v(-162.95, 52.53) * mm});
            skLineSegment(sketch, "E313", {"start": v(-162.95, 52.53) * mm, "end": v(-162.87, 52.67) * mm});
            skLineSegment(sketch, "E314", {"start": v(-162.87, 52.67) * mm, "end": v(-162.78, 52.8) * mm});
            skLineSegment(sketch, "E315", {"start": v(-162.78, 52.8) * mm, "end": v(-162.68, 52.92) * mm});
            skLineSegment(sketch, "E316", {"start": v(-162.68, 52.92) * mm, "end": v(-162.58, 53.04) * mm});
            skLineSegment(sketch, "E317", {"start": v(-162.58, 53.04) * mm, "end": v(-162.46, 53.15) * mm});
            skLineSegment(sketch, "E318", {"start": v(-162.46, 53.15) * mm, "end": v(-162.34, 53.24) * mm});
            skLineSegment(sketch, "E319", {"start": v(-162.34, 53.24) * mm, "end": v(-162.2, 53.33) * mm});
            skLineSegment(sketch, "E320", {"start": v(-162.2, 53.33) * mm, "end": v(-162.07, 53.4) * mm});
            skLineSegment(sketch, "E321", {"start": v(-162.07, 53.4) * mm, "end": v(-161.93, 53.47) * mm});
            skLineSegment(sketch, "E322", {"start": v(-161.93, 53.47) * mm, "end": v(-161.78, 53.53) * mm});
            skLineSegment(sketch, "E323", {"start": v(-161.78, 53.53) * mm, "end": v(-161.63, 53.57) * mm});
            skLineSegment(sketch, "E324", {"start": v(-161.63, 53.57) * mm, "end": v(-161.48, 53.6) * mm});
            skLineSegment(sketch, "E325", {"start": v(-161.48, 53.6) * mm, "end": v(-161.32, 53.62) * mm});
            skLineSegment(sketch, "E326", {"start": v(-161.32, 53.62) * mm, "end": v(-161.16, 53.63) * mm});
            skLineSegment(sketch, "E327", {"start": v(-161.16, 53.63) * mm, "end": v(161.16, 53.62) * mm});
            skLineSegment(sketch, "E328", {"start": v(160.2, -49.7) * mm, "end": v(159.78, -49.91) * mm});
            skLineSegment(sketch, "E329", {"start": v(159.78, -49.91) * mm, "end": v(159.45, -50.24) * mm});
            skLineSegment(sketch, "E330", {"start": v(159.45, -50.24) * mm, "end": v(159.24, -50.66) * mm});
            skLineSegment(sketch, "E331", {"start": v(159.24, -50.66) * mm, "end": v(159.16, -51.13) * mm});
            skLineSegment(sketch, "E332", {"start": v(159.16, -51.13) * mm, "end": v(159.24, -51.59) * mm});
            skLineSegment(sketch, "E333", {"start": v(159.24, -51.59) * mm, "end": v(159.45, -52) * mm});
            skLineSegment(sketch, "E334", {"start": v(159.45, -52) * mm, "end": v(159.78, -52.34) * mm});
            skLineSegment(sketch, "E335", {"start": v(159.78, -52.34) * mm, "end": v(160.2, -52.55) * mm});
            skLineSegment(sketch, "E336", {"start": v(160.2, -52.55) * mm, "end": v(160.66, -52.63) * mm});
            skLineSegment(sketch, "E337", {"start": v(160.66, -52.63) * mm, "end": v(161.13, -52.55) * mm});
            skLineSegment(sketch, "E338", {"start": v(161.13, -52.55) * mm, "end": v(161.54, -52.34) * mm});
            skLineSegment(sketch, "E339", {"start": v(161.54, -52.34) * mm, "end": v(161.88, -52) * mm});
            skLineSegment(sketch, "E340", {"start": v(161.88, -52) * mm, "end": v(162.09, -51.59) * mm});
            skLineSegment(sketch, "E341", {"start": v(162.09, -51.59) * mm, "end": v(162.16, -51.13) * mm});
            skLineSegment(sketch, "E342", {"start": v(162.16, -51.13) * mm, "end": v(162.09, -50.66) * mm});
            skLineSegment(sketch, "E343", {"start": v(162.09, -50.66) * mm, "end": v(161.88, -50.24) * mm});
            skLineSegment(sketch, "E344", {"start": v(161.88, -50.24) * mm, "end": v(161.54, -49.91) * mm});
            skLineSegment(sketch, "E345", {"start": v(161.54, -49.91) * mm, "end": v(161.13, -49.7) * mm});
            skLineSegment(sketch, "E346", {"start": v(161.13, -49.7) * mm, "end": v(160.66, -49.63) * mm});
            skLineSegment(sketch, "E347", {"start": v(160.66, -49.63) * mm, "end": v(160.2, -49.7) * mm});
            skLineSegment(sketch, "E348", {"start": v(53.1, -49.7) * mm, "end": v(52.67, -49.91) * mm});
            skLineSegment(sketch, "E349", {"start": v(52.67, -49.91) * mm, "end": v(52.34, -50.24) * mm});
            skLineSegment(sketch, "E350", {"start": v(52.34, -50.24) * mm, "end": v(52.13, -50.66) * mm});
            skLineSegment(sketch, "E351", {"start": v(52.13, -50.66) * mm, "end": v(52.05, -51.13) * mm});
            skLineSegment(sketch, "E352", {"start": v(52.05, -51.13) * mm, "end": v(52.13, -51.59) * mm});
            skLineSegment(sketch, "E353", {"start": v(52.13, -51.59) * mm, "end": v(52.34, -52) * mm});
            skLineSegment(sketch, "E354", {"start": v(52.34, -52) * mm, "end": v(52.67, -52.34) * mm});
            skLineSegment(sketch, "E355", {"start": v(52.67, -52.34) * mm, "end": v(53.1, -52.55) * mm});
            skLineSegment(sketch, "E356", {"start": v(53.1, -52.55) * mm, "end": v(53.55, -52.63) * mm});
            skLineSegment(sketch, "E357", {"start": v(53.55, -52.63) * mm, "end": v(54.02, -52.55) * mm});
            skLineSegment(sketch, "E358", {"start": v(54.02, -52.55) * mm, "end": v(54.44, -52.34) * mm});
            skLineSegment(sketch, "E359", {"start": v(54.44, -52.34) * mm, "end": v(54.77, -52) * mm});
            skLineSegment(sketch, "E360", {"start": v(54.77, -52) * mm, "end": v(54.98, -51.59) * mm});
            skLineSegment(sketch, "E361", {"start": v(54.98, -51.59) * mm, "end": v(55.05, -51.13) * mm});
            skLineSegment(sketch, "E362", {"start": v(55.05, -51.13) * mm, "end": v(54.98, -50.66) * mm});
            skLineSegment(sketch, "E363", {"start": v(54.98, -50.66) * mm, "end": v(54.77, -50.24) * mm});
            skLineSegment(sketch, "E364", {"start": v(54.77, -50.24) * mm, "end": v(54.44, -49.91) * mm});
            skLineSegment(sketch, "E365", {"start": v(54.44, -49.91) * mm, "end": v(54.02, -49.7) * mm});
            skLineSegment(sketch, "E366", {"start": v(54.02, -49.7) * mm, "end": v(53.55, -49.63) * mm});
            skLineSegment(sketch, "E367", {"start": v(53.55, -49.63) * mm, "end": v(53.1, -49.7) * mm});
            skLineSegment(sketch, "E368", {"start": v(-54.02, -49.7) * mm, "end": v(-54.44, -49.91) * mm});
            skLineSegment(sketch, "E369", {"start": v(-54.44, -49.91) * mm, "end": v(-54.77, -50.24) * mm});
            skLineSegment(sketch, "E370", {"start": v(-54.77, -50.24) * mm, "end": v(-54.98, -50.66) * mm});
            skLineSegment(sketch, "E371", {"start": v(-54.98, -50.66) * mm, "end": v(-55.06, -51.13) * mm});
            skLineSegment(sketch, "E372", {"start": v(-55.06, -51.13) * mm, "end": v(-54.98, -51.59) * mm});
            skLineSegment(sketch, "E373", {"start": v(-54.98, -51.59) * mm, "end": v(-54.77, -52) * mm});
            skLineSegment(sketch, "E374", {"start": v(-54.77, -52) * mm, "end": v(-54.44, -52.34) * mm});
            skLineSegment(sketch, "E375", {"start": v(-54.44, -52.34) * mm, "end": v(-54.02, -52.55) * mm});
            skLineSegment(sketch, "E376", {"start": v(-54.02, -52.55) * mm, "end": v(-53.55, -52.63) * mm});
            skLineSegment(sketch, "E377", {"start": v(-53.55, -52.63) * mm, "end": v(-53.1, -52.55) * mm});
            skLineSegment(sketch, "E378", {"start": v(-53.1, -52.55) * mm, "end": v(-52.67, -52.34) * mm});
            skLineSegment(sketch, "E379", {"start": v(-52.67, -52.34) * mm, "end": v(-52.34, -52) * mm});
            skLineSegment(sketch, "E380", {"start": v(-52.34, -52) * mm, "end": v(-52.13, -51.59) * mm});
            skLineSegment(sketch, "E381", {"start": v(-52.13, -51.59) * mm, "end": v(-52.06, -51.13) * mm});
            skLineSegment(sketch, "E382", {"start": v(-52.06, -51.13) * mm, "end": v(-52.13, -50.66) * mm});
            skLineSegment(sketch, "E383", {"start": v(-52.13, -50.66) * mm, "end": v(-52.34, -50.24) * mm});
            skLineSegment(sketch, "E384", {"start": v(-52.34, -50.24) * mm, "end": v(-52.67, -49.91) * mm});
            skLineSegment(sketch, "E385", {"start": v(-52.67, -49.91) * mm, "end": v(-53.1, -49.7) * mm});
            skLineSegment(sketch, "E386", {"start": v(-53.1, -49.7) * mm, "end": v(-53.55, -49.63) * mm});
            skLineSegment(sketch, "E387", {"start": v(-53.55, -49.63) * mm, "end": v(-54.02, -49.7) * mm});
            skLineSegment(sketch, "E388", {"start": v(-161.13, -49.7) * mm, "end": v(-161.54, -49.91) * mm});
            skLineSegment(sketch, "E389", {"start": v(-161.54, -49.91) * mm, "end": v(-161.88, -50.24) * mm});
            skLineSegment(sketch, "E390", {"start": v(-161.88, -50.24) * mm, "end": v(-162.1, -50.66) * mm});
            skLineSegment(sketch, "E391", {"start": v(-162.1, -50.66) * mm, "end": v(-162.16, -51.13) * mm});
            skLineSegment(sketch, "E392", {"start": v(-162.16, -51.13) * mm, "end": v(-162.1, -51.59) * mm});
            skLineSegment(sketch, "E393", {"start": v(-162.1, -51.59) * mm, "end": v(-161.88, -52) * mm});
            skLineSegment(sketch, "E394", {"start": v(-161.88, -52) * mm, "end": v(-161.54, -52.34) * mm});
            skLineSegment(sketch, "E395", {"start": v(-161.54, -52.34) * mm, "end": v(-161.13, -52.55) * mm});
            skLineSegment(sketch, "E396", {"start": v(-161.13, -52.55) * mm, "end": v(-160.66, -52.63) * mm});
            skLineSegment(sketch, "E397", {"start": v(-160.66, -52.63) * mm, "end": v(-160.2, -52.55) * mm});
            skLineSegment(sketch, "E398", {"start": v(-160.2, -52.55) * mm, "end": v(-159.78, -52.34) * mm});
            skLineSegment(sketch, "E399", {"start": v(-159.78, -52.34) * mm, "end": v(-159.45, -52) * mm});
            skLineSegment(sketch, "E400", {"start": v(-159.45, -52) * mm, "end": v(-159.24, -51.59) * mm});
            skLineSegment(sketch, "E401", {"start": v(-159.24, -51.59) * mm, "end": v(-159.16, -51.13) * mm});
            skLineSegment(sketch, "E402", {"start": v(-159.16, -51.13) * mm, "end": v(-159.24, -50.66) * mm});
            skLineSegment(sketch, "E403", {"start": v(-159.24, -50.66) * mm, "end": v(-159.45, -50.24) * mm});
            skLineSegment(sketch, "E404", {"start": v(-159.45, -50.24) * mm, "end": v(-159.78, -49.91) * mm});
            skLineSegment(sketch, "E405", {"start": v(-159.78, -49.91) * mm, "end": v(-160.2, -49.7) * mm});
            skLineSegment(sketch, "E406", {"start": v(-160.2, -49.7) * mm, "end": v(-160.66, -49.63) * mm});
            skLineSegment(sketch, "E407", {"start": v(-160.66, -49.63) * mm, "end": v(-161.13, -49.7) * mm});
            skLineSegment(sketch, "E408", {"start": v(-158.16, 48.62) * mm, "end": v(158.16, 48.62) * mm});
            skLineSegment(sketch, "E409", {"start": v(158.16, 48.62) * mm, "end": v(158.16, -48.62) * mm});
            skLineSegment(sketch, "E410", {"start": v(158.16, -48.62) * mm, "end": v(-158.16, -48.62) * mm});
            skLineSegment(sketch, "E411", {"start": v(-158.16, -48.62) * mm, "end": v(-158.16, 48.62) * mm});
            skLineSegment(sketch, "E412", {"start": v(-54.02, 52.55) * mm, "end": v(-54.44, 52.34) * mm});
            skLineSegment(sketch, "E413", {"start": v(-54.44, 52.34) * mm, "end": v(-54.77, 52) * mm});
            skLineSegment(sketch, "E414", {"start": v(-54.77, 52) * mm, "end": v(-54.98, 51.59) * mm});
            skLineSegment(sketch, "E415", {"start": v(-54.98, 51.59) * mm, "end": v(-55.06, 51.12) * mm});
            skLineSegment(sketch, "E416", {"start": v(-55.06, 51.12) * mm, "end": v(-54.98, 50.66) * mm});
            skLineSegment(sketch, "E417", {"start": v(-54.98, 50.66) * mm, "end": v(-54.77, 50.24) * mm});
            skLineSegment(sketch, "E418", {"start": v(-54.77, 50.24) * mm, "end": v(-54.44, 49.91) * mm});
            skLineSegment(sketch, "E419", {"start": v(-54.44, 49.91) * mm, "end": v(-54.02, 49.7) * mm});
            skLineSegment(sketch, "E420", {"start": v(-54.02, 49.7) * mm, "end": v(-53.55, 49.62) * mm});
            skLineSegment(sketch, "E421", {"start": v(-53.55, 49.62) * mm, "end": v(-53.1, 49.7) * mm});
            skLineSegment(sketch, "E422", {"start": v(-53.1, 49.7) * mm, "end": v(-52.67, 49.91) * mm});
            skLineSegment(sketch, "E423", {"start": v(-52.67, 49.91) * mm, "end": v(-52.34, 50.24) * mm});
            skLineSegment(sketch, "E424", {"start": v(-52.34, 50.24) * mm, "end": v(-52.13, 50.66) * mm});
            skLineSegment(sketch, "E425", {"start": v(-52.13, 50.66) * mm, "end": v(-52.06, 51.12) * mm});
            skLineSegment(sketch, "E426", {"start": v(-52.06, 51.12) * mm, "end": v(-52.13, 51.59) * mm});
            skLineSegment(sketch, "E427", {"start": v(-52.13, 51.59) * mm, "end": v(-52.34, 52) * mm});
            skLineSegment(sketch, "E428", {"start": v(-52.34, 52) * mm, "end": v(-52.67, 52.34) * mm});
            skLineSegment(sketch, "E429", {"start": v(-52.67, 52.34) * mm, "end": v(-53.1, 52.55) * mm});
            skLineSegment(sketch, "E430", {"start": v(-53.1, 52.55) * mm, "end": v(-53.55, 52.62) * mm});
            skLineSegment(sketch, "E431", {"start": v(-53.55, 52.62) * mm, "end": v(-54.02, 52.55) * mm});
            skLineSegment(sketch, "E432", {"start": v(53.1, 52.55) * mm, "end": v(52.67, 52.34) * mm});
            skLineSegment(sketch, "E433", {"start": v(52.67, 52.34) * mm, "end": v(52.34, 52) * mm});
            skLineSegment(sketch, "E434", {"start": v(52.34, 52) * mm, "end": v(52.13, 51.59) * mm});
            skLineSegment(sketch, "E435", {"start": v(52.13, 51.59) * mm, "end": v(52.05, 51.12) * mm});
            skLineSegment(sketch, "E436", {"start": v(52.05, 51.12) * mm, "end": v(52.13, 50.66) * mm});
            skLineSegment(sketch, "E437", {"start": v(52.13, 50.66) * mm, "end": v(52.34, 50.24) * mm});
            skLineSegment(sketch, "E438", {"start": v(52.34, 50.24) * mm, "end": v(52.67, 49.91) * mm});
            skLineSegment(sketch, "E439", {"start": v(52.67, 49.91) * mm, "end": v(53.1, 49.7) * mm});
            skLineSegment(sketch, "E440", {"start": v(53.1, 49.7) * mm, "end": v(53.55, 49.62) * mm});
            skLineSegment(sketch, "E441", {"start": v(53.55, 49.62) * mm, "end": v(54.02, 49.7) * mm});
            skLineSegment(sketch, "E442", {"start": v(54.02, 49.7) * mm, "end": v(54.44, 49.91) * mm});
            skLineSegment(sketch, "E443", {"start": v(54.44, 49.91) * mm, "end": v(54.77, 50.24) * mm});
            skLineSegment(sketch, "E444", {"start": v(54.77, 50.24) * mm, "end": v(54.98, 50.66) * mm});
            skLineSegment(sketch, "E445", {"start": v(54.98, 50.66) * mm, "end": v(55.05, 51.12) * mm});
            skLineSegment(sketch, "E446", {"start": v(55.05, 51.12) * mm, "end": v(54.98, 51.59) * mm});
            skLineSegment(sketch, "E447", {"start": v(54.98, 51.59) * mm, "end": v(54.77, 52) * mm});
            skLineSegment(sketch, "E448", {"start": v(54.77, 52) * mm, "end": v(54.44, 52.34) * mm});
            skLineSegment(sketch, "E449", {"start": v(54.44, 52.34) * mm, "end": v(54.02, 52.55) * mm});
            skLineSegment(sketch, "E450", {"start": v(54.02, 52.55) * mm, "end": v(53.55, 52.62) * mm});
            skLineSegment(sketch, "E451", {"start": v(53.55, 52.62) * mm, "end": v(53.1, 52.55) * mm});
            skLineSegment(sketch, "E452", {"start": v(160.2, 52.55) * mm, "end": v(159.78, 52.34) * mm});
            skLineSegment(sketch, "E453", {"start": v(159.78, 52.34) * mm, "end": v(159.45, 52) * mm});
            skLineSegment(sketch, "E454", {"start": v(159.45, 52) * mm, "end": v(159.24, 51.59) * mm});
            skLineSegment(sketch, "E455", {"start": v(159.24, 51.59) * mm, "end": v(159.16, 51.12) * mm});
            skLineSegment(sketch, "E456", {"start": v(159.16, 51.12) * mm, "end": v(159.24, 50.66) * mm});
            skLineSegment(sketch, "E457", {"start": v(159.24, 50.66) * mm, "end": v(159.45, 50.24) * mm});
            skLineSegment(sketch, "E458", {"start": v(159.45, 50.24) * mm, "end": v(159.78, 49.91) * mm});
            skLineSegment(sketch, "E459", {"start": v(159.78, 49.91) * mm, "end": v(160.2, 49.7) * mm});
            skLineSegment(sketch, "E460", {"start": v(160.2, 49.7) * mm, "end": v(160.66, 49.62) * mm});
            skLineSegment(sketch, "E461", {"start": v(160.66, 49.62) * mm, "end": v(161.13, 49.7) * mm});
            skLineSegment(sketch, "E462", {"start": v(161.13, 49.7) * mm, "end": v(161.54, 49.91) * mm});
            skLineSegment(sketch, "E463", {"start": v(161.54, 49.91) * mm, "end": v(161.88, 50.24) * mm});
            skLineSegment(sketch, "E464", {"start": v(161.88, 50.24) * mm, "end": v(162.09, 50.66) * mm});
            skLineSegment(sketch, "E465", {"start": v(162.09, 50.66) * mm, "end": v(162.16, 51.12) * mm});
            skLineSegment(sketch, "E466", {"start": v(162.16, 51.12) * mm, "end": v(162.09, 51.59) * mm});
            skLineSegment(sketch, "E467", {"start": v(162.09, 51.59) * mm, "end": v(161.88, 52) * mm});
            skLineSegment(sketch, "E468", {"start": v(161.88, 52) * mm, "end": v(161.54, 52.34) * mm});
            skLineSegment(sketch, "E469", {"start": v(161.54, 52.34) * mm, "end": v(161.13, 52.55) * mm});
            skLineSegment(sketch, "E470", {"start": v(161.13, 52.55) * mm, "end": v(160.66, 52.62) * mm});
            skLineSegment(sketch, "E471", {"start": v(160.66, 52.62) * mm, "end": v(160.2, 52.55) * mm});
            skLineSegment(sketch, "E472", {"start": v(-161.13, 52.55) * mm, "end": v(-161.54, 52.34) * mm});
            skLineSegment(sketch, "E473", {"start": v(-161.54, 52.34) * mm, "end": v(-161.88, 52) * mm});
            skLineSegment(sketch, "E474", {"start": v(-161.88, 52) * mm, "end": v(-162.1, 51.59) * mm});
            skLineSegment(sketch, "E475", {"start": v(-162.1, 51.59) * mm, "end": v(-162.16, 51.12) * mm});
            skLineSegment(sketch, "E476", {"start": v(-162.16, 51.12) * mm, "end": v(-162.1, 50.66) * mm});
            skLineSegment(sketch, "E477", {"start": v(-162.1, 50.66) * mm, "end": v(-161.88, 50.24) * mm});
            skLineSegment(sketch, "E478", {"start": v(-161.88, 50.24) * mm, "end": v(-161.54, 49.91) * mm});
            skLineSegment(sketch, "E479", {"start": v(-161.54, 49.91) * mm, "end": v(-161.13, 49.7) * mm});
            skLineSegment(sketch, "E480", {"start": v(-161.13, 49.7) * mm, "end": v(-160.66, 49.62) * mm});
            skLineSegment(sketch, "E481", {"start": v(-160.66, 49.62) * mm, "end": v(-160.2, 49.7) * mm});
            skLineSegment(sketch, "E482", {"start": v(-160.2, 49.7) * mm, "end": v(-159.78, 49.91) * mm});
            skLineSegment(sketch, "E483", {"start": v(-159.78, 49.91) * mm, "end": v(-159.45, 50.24) * mm});
            skLineSegment(sketch, "E484", {"start": v(-159.45, 50.24) * mm, "end": v(-159.24, 50.66) * mm});
            skLineSegment(sketch, "E485", {"start": v(-159.24, 50.66) * mm, "end": v(-159.16, 51.12) * mm});
            skLineSegment(sketch, "E486", {"start": v(-159.16, 51.12) * mm, "end": v(-159.24, 51.59) * mm});
            skLineSegment(sketch, "E487", {"start": v(-159.24, 51.59) * mm, "end": v(-159.45, 52) * mm});
            skLineSegment(sketch, "E488", {"start": v(-159.45, 52) * mm, "end": v(-159.78, 52.34) * mm});
            skLineSegment(sketch, "E489", {"start": v(-159.78, 52.34) * mm, "end": v(-160.2, 52.55) * mm});
            skLineSegment(sketch, "E490", {"start": v(-160.2, 52.55) * mm, "end": v(-160.66, 52.62) * mm});
            skLineSegment(sketch, "E491", {"start": v(-160.66, 52.62) * mm, "end": v(-161.13, 52.55) * mm});
            skSolve(sketch);
        }
        {
            var Q0;
            Q0 = qSketchRegion(id + "F3", true);
            extrude(context, id + "F4", {"entities" : qUnion([Q0]), "depth" : (getVariable(context, 'Thickness')) * mm, "offsetDistance" : 25 * mm});
        }
        {
            var Q0;
            Q0=makeQuery(id+"F4.opExtrude","CAP_FACE",FACE,{"disambiguationData":[OSD([sQuery(id+"F3.wireOp",EDGE,"E244"),sQuery(id+"F3.wireOp",EDGE,"E245"),sQuery(id+"F3.wireOp",EDGE,"E246"),sQuery(id+"F3.wireOp",EDGE,"E247"),sQuery(id+"F3.wireOp",EDGE,"E248"),sQuery(id+"F3.wireOp",EDGE,"E249"),sQuery(id+"F3.wireOp",EDGE,"E250"),sQuery(id+"F3.wireOp",EDGE,"E251"),sQuery(id+"F3.wireOp",EDGE,"E252"),sQuery(id+"F3.wireOp",EDGE,"E253"),sQuery(id+"F3.wireOp",EDGE,"E254"),sQuery(id+"F3.wireOp",EDGE,"E255"),sQuery(id+"F3.wireOp",EDGE,"E256"),sQuery(id+"F3.wireOp",EDGE,"E257"),sQuery(id+"F3.wireOp",EDGE,"E258"),sQuery(id+"F3.wireOp",EDGE,"E259"),sQuery(id+"F3.wireOp",EDGE,"E260"),sQuery(id+"F3.wireOp",EDGE,"E261"),sQuery(id+"F3.wireOp",EDGE,"E262"),sQuery(id+"F3.wireOp",EDGE,"E263"),sQuery(id+"F3.wireOp",EDGE,"E264"),sQuery(id+"F3.wireOp",EDGE,"E265"),sQuery(id+"F3.wireOp",EDGE,"E266"),sQuery(id+"F3.wireOp",EDGE,"E267"),sQuery(id+"F3.wireOp",EDGE,"E268"),sQuery(id+"F3.wireOp",EDGE,"E269"),sQuery(id+"F3.wireOp",EDGE,"E270"),sQuery(id+"F3.wireOp",EDGE,"E271"),sQuery(id+"F3.wireOp",EDGE,"E272"),sQuery(id+"F3.wireOp",EDGE,"E273"),sQuery(id+"F3.wireOp",EDGE,"E274"),sQuery(id+"F3.wireOp",EDGE,"E275"),sQuery(id+"F3.wireOp",EDGE,"E276"),sQuery(id+"F3.wireOp",EDGE,"E277"),sQuery(id+"F3.wireOp",EDGE,"E278"),sQuery(id+"F3.wireOp",EDGE,"E279"),sQuery(id+"F3.wireOp",EDGE,"E280"),sQuery(id+"F3.wireOp",EDGE,"E281"),sQuery(id+"F3.wireOp",EDGE,"E282"),sQuery(id+"F3.wireOp",EDGE,"E283"),sQuery(id+"F3.wireOp",EDGE,"E284"),sQuery(id+"F3.wireOp",EDGE,"E285"),sQuery(id+"F3.wireOp",EDGE,"E286"),sQuery(id+"F3.wireOp",EDGE,"E287"),sQuery(id+"F3.wireOp",EDGE,"E288"),sQuery(id+"F3.wireOp",EDGE,"E289"),sQuery(id+"F3.wireOp",EDGE,"E290"),sQuery(id+"F3.wireOp",EDGE,"E291"),sQuery(id+"F3.wireOp",EDGE,"E292"),sQuery(id+"F3.wireOp",EDGE,"E293"),sQuery(id+"F3.wireOp",EDGE,"E294"),sQuery(id+"F3.wireOp",EDGE,"E295"),sQuery(id+"F3.wireOp",EDGE,"E296"),sQuery(id+"F3.wireOp",EDGE,"E297"),sQuery(id+"F3.wireOp",EDGE,"E298"),sQuery(id+"F3.wireOp",EDGE,"E299"),sQuery(id+"F3.wireOp",EDGE,"E300"),sQuery(id+"F3.wireOp",EDGE,"E301"),sQuery(id+"F3.wireOp",EDGE,"E302"),sQuery(id+"F3.wireOp",EDGE,"E303"),sQuery(id+"F3.wireOp",EDGE,"E304"),sQuery(id+"F3.wireOp",EDGE,"E305"),sQuery(id+"F3.wireOp",EDGE,"E306"),sQuery(id+"F3.wireOp",EDGE,"E307"),sQuery(id+"F3.wireOp",EDGE,"E308"),sQuery(id+"F3.wireOp",EDGE,"E309"),sQuery(id+"F3.wireOp",EDGE,"E310"),sQuery(id+"F3.wireOp",EDGE,"E311"),sQuery(id+"F3.wireOp",EDGE,"E312"),sQuery(id+"F3.wireOp",EDGE,"E313"),sQuery(id+"F3.wireOp",EDGE,"E314"),sQuery(id+"F3.wireOp",EDGE,"E315"),sQuery(id+"F3.wireOp",EDGE,"E316"),sQuery(id+"F3.wireOp",EDGE,"E317"),sQuery(id+"F3.wireOp",EDGE,"E318"),sQuery(id+"F3.wireOp",EDGE,"E319"),sQuery(id+"F3.wireOp",EDGE,"E320"),sQuery(id+"F3.wireOp",EDGE,"E321"),sQuery(id+"F3.wireOp",EDGE,"E322"),sQuery(id+"F3.wireOp",EDGE,"E323"),sQuery(id+"F3.wireOp",EDGE,"E324"),sQuery(id+"F3.wireOp",EDGE,"E325"),sQuery(id+"F3.wireOp",EDGE,"E326"),sQuery(id+"F3.wireOp",EDGE,"E327"),sQuery(id+"F3.wireOp",EDGE,"E328"),sQuery(id+"F3.wireOp",EDGE,"E329"),sQuery(id+"F3.wireOp",EDGE,"E330"),sQuery(id+"F3.wireOp",EDGE,"E331"),sQuery(id+"F3.wireOp",EDGE,"E332"),sQuery(id+"F3.wireOp",EDGE,"E333"),sQuery(id+"F3.wireOp",EDGE,"E334"),sQuery(id+"F3.wireOp",EDGE,"E335"),sQuery(id+"F3.wireOp",EDGE,"E336"),sQuery(id+"F3.wireOp",EDGE,"E337"),sQuery(id+"F3.wireOp",EDGE,"E338"),sQuery(id+"F3.wireOp",EDGE,"E339"),sQuery(id+"F3.wireOp",EDGE,"E340"),sQuery(id+"F3.wireOp",EDGE,"E341"),sQuery(id+"F3.wireOp",EDGE,"E342"),sQuery(id+"F3.wireOp",EDGE,"E343"),sQuery(id+"F3.wireOp",EDGE,"E344"),sQuery(id+"F3.wireOp",EDGE,"E345"),sQuery(id+"F3.wireOp",EDGE,"E346"),sQuery(id+"F3.wireOp",EDGE,"E347"),sQuery(id+"F3.wireOp",EDGE,"E348"),sQuery(id+"F3.wireOp",EDGE,"E349"),sQuery(id+"F3.wireOp",EDGE,"E350"),sQuery(id+"F3.wireOp",EDGE,"E351"),sQuery(id+"F3.wireOp",EDGE,"E352"),sQuery(id+"F3.wireOp",EDGE,"E353"),sQuery(id+"F3.wireOp",EDGE,"E354"),sQuery(id+"F3.wireOp",EDGE,"E355"),sQuery(id+"F3.wireOp",EDGE,"E356"),sQuery(id+"F3.wireOp",EDGE,"E357"),sQuery(id+"F3.wireOp",EDGE,"E358"),sQuery(id+"F3.wireOp",EDGE,"E359"),sQuery(id+"F3.wireOp",EDGE,"E360"),sQuery(id+"F3.wireOp",EDGE,"E361"),sQuery(id+"F3.wireOp",EDGE,"E362"),sQuery(id+"F3.wireOp",EDGE,"E363"),sQuery(id+"F3.wireOp",EDGE,"E364"),sQuery(id+"F3.wireOp",EDGE,"E365"),sQuery(id+"F3.wireOp",EDGE,"E366"),sQuery(id+"F3.wireOp",EDGE,"E367"),sQuery(id+"F3.wireOp",EDGE,"E368"),sQuery(id+"F3.wireOp",EDGE,"E369"),sQuery(id+"F3.wireOp",EDGE,"E370"),sQuery(id+"F3.wireOp",EDGE,"E371"),sQuery(id+"F3.wireOp",EDGE,"E372"),sQuery(id+"F3.wireOp",EDGE,"E373"),sQuery(id+"F3.wireOp",EDGE,"E374"),sQuery(id+"F3.wireOp",EDGE,"E375"),sQuery(id+"F3.wireOp",EDGE,"E376"),sQuery(id+"F3.wireOp",EDGE,"E377"),sQuery(id+"F3.wireOp",EDGE,"E378"),sQuery(id+"F3.wireOp",EDGE,"E379"),sQuery(id+"F3.wireOp",EDGE,"E380"),sQuery(id+"F3.wireOp",EDGE,"E381"),sQuery(id+"F3.wireOp",EDGE,"E382"),sQuery(id+"F3.wireOp",EDGE,"E383"),sQuery(id+"F3.wireOp",EDGE,"E384"),sQuery(id+"F3.wireOp",EDGE,"E385"),sQuery(id+"F3.wireOp",EDGE,"E386"),sQuery(id+"F3.wireOp",EDGE,"E387"),sQuery(id+"F3.wireOp",EDGE,"E388"),sQuery(id+"F3.wireOp",EDGE,"E389"),sQuery(id+"F3.wireOp",EDGE,"E390"),sQuery(id+"F3.wireOp",EDGE,"E391"),sQuery(id+"F3.wireOp",EDGE,"E392"),sQuery(id+"F3.wireOp",EDGE,"E393"),sQuery(id+"F3.wireOp",EDGE,"E394"),sQuery(id+"F3.wireOp",EDGE,"E395"),sQuery(id+"F3.wireOp",EDGE,"E396"),sQuery(id+"F3.wireOp",EDGE,"E397"),sQuery(id+"F3.wireOp",EDGE,"E398"),sQuery(id+"F3.wireOp",EDGE,"E399"),sQuery(id+"F3.wireOp",EDGE,"E400"),sQuery(id+"F3.wireOp",EDGE,"E401"),sQuery(id+"F3.wireOp",EDGE,"E402"),sQuery(id+"F3.wireOp",EDGE,"E403"),sQuery(id+"F3.wireOp",EDGE,"E404"),sQuery(id+"F3.wireOp",EDGE,"E405"),sQuery(id+"F3.wireOp",EDGE,"E406"),sQuery(id+"F3.wireOp",EDGE,"E407"),sQuery(id+"F3.wireOp",EDGE,"E408"),sQuery(id+"F3.wireOp",EDGE,"E409"),sQuery(id+"F3.wireOp",EDGE,"E410"),sQuery(id+"F3.wireOp",EDGE,"E411"),sQuery(id+"F3.wireOp",EDGE,"E412"),sQuery(id+"F3.wireOp",EDGE,"E413"),sQuery(id+"F3.wireOp",EDGE,"E414"),sQuery(id+"F3.wireOp",EDGE,"E415"),sQuery(id+"F3.wireOp",EDGE,"E416"),sQuery(id+"F3.wireOp",EDGE,"E417"),sQuery(id+"F3.wireOp",EDGE,"E418"),sQuery(id+"F3.wireOp",EDGE,"E419"),sQuery(id+"F3.wireOp",EDGE,"E420"),sQuery(id+"F3.wireOp",EDGE,"E421"),sQuery(id+"F3.wireOp",EDGE,"E422"),sQuery(id+"F3.wireOp",EDGE,"E423"),sQuery(id+"F3.wireOp",EDGE,"E424"),sQuery(id+"F3.wireOp",EDGE,"E425"),sQuery(id+"F3.wireOp",EDGE,"E426"),sQuery(id+"F3.wireOp",EDGE,"E427"),sQuery(id+"F3.wireOp",EDGE,"E428"),sQuery(id+"F3.wireOp",EDGE,"E429"),sQuery(id+"F3.wireOp",EDGE,"E430"),sQuery(id+"F3.wireOp",EDGE,"E431"),sQuery(id+"F3.wireOp",EDGE,"E432"),sQuery(id+"F3.wireOp",EDGE,"E433"),sQuery(id+"F3.wireOp",EDGE,"E434"),sQuery(id+"F3.wireOp",EDGE,"E435"),sQuery(id+"F3.wireOp",EDGE,"E436"),sQuery(id+"F3.wireOp",EDGE,"E437"),sQuery(id+"F3.wireOp",EDGE,"E438"),sQuery(id+"F3.wireOp",EDGE,"E439"),sQuery(id+"F3.wireOp",EDGE,"E440"),sQuery(id+"F3.wireOp",EDGE,"E441"),sQuery(id+"F3.wireOp",EDGE,"E442"),sQuery(id+"F3.wireOp",EDGE,"E443"),sQuery(id+"F3.wireOp",EDGE,"E444"),sQuery(id+"F3.wireOp",EDGE,"E445"),sQuery(id+"F3.wireOp",EDGE,"E446"),sQuery(id+"F3.wireOp",EDGE,"E447"),sQuery(id+"F3.wireOp",EDGE,"E448"),sQuery(id+"F3.wireOp",EDGE,"E449"),sQuery(id+"F3.wireOp",EDGE,"E450"),sQuery(id+"F3.wireOp",EDGE,"E451"),sQuery(id+"F3.wireOp",EDGE,"E452"),sQuery(id+"F3.wireOp",EDGE,"E453"),sQuery(id+"F3.wireOp",EDGE,"E454"),sQuery(id+"F3.wireOp",EDGE,"E455"),sQuery(id+"F3.wireOp",EDGE,"E456"),sQuery(id+"F3.wireOp",EDGE,"E457"),sQuery(id+"F3.wireOp",EDGE,"E458"),sQuery(id+"F3.wireOp",EDGE,"E459"),sQuery(id+"F3.wireOp",EDGE,"E460"),sQuery(id+"F3.wireOp",EDGE,"E461"),sQuery(id+"F3.wireOp",EDGE,"E462"),sQuery(id+"F3.wireOp",EDGE,"E463"),sQuery(id+"F3.wireOp",EDGE,"E464"),sQuery(id+"F3.wireOp",EDGE,"E465"),sQuery(id+"F3.wireOp",EDGE,"E466"),sQuery(id+"F3.wireOp",EDGE,"E467"),sQuery(id+"F3.wireOp",EDGE,"E468"),sQuery(id+"F3.wireOp",EDGE,"E469"),sQuery(id+"F3.wireOp",EDGE,"E470"),sQuery(id+"F3.wireOp",EDGE,"E471"),sQuery(id+"F3.wireOp",EDGE,"E472"),sQuery(id+"F3.wireOp",EDGE,"E473"),sQuery(id+"F3.wireOp",EDGE,"E474"),sQuery(id+"F3.wireOp",EDGE,"E475"),sQuery(id+"F3.wireOp",EDGE,"E476"),sQuery(id+"F3.wireOp",EDGE,"E477"),sQuery(id+"F3.wireOp",EDGE,"E478"),sQuery(id+"F3.wireOp",EDGE,"E479"),sQuery(id+"F3.wireOp",EDGE,"E480"),sQuery(id+"F3.wireOp",EDGE,"E481"),sQuery(id+"F3.wireOp",EDGE,"E482"),sQuery(id+"F3.wireOp",EDGE,"E483"),sQuery(id+"F3.wireOp",EDGE,"E484"),sQuery(id+"F3.wireOp",EDGE,"E485"),sQuery(id+"F3.wireOp",EDGE,"E486"),sQuery(id+"F3.wireOp",EDGE,"E487"),sQuery(id+"F3.wireOp",EDGE,"E488"),sQuery(id+"F3.wireOp",EDGE,"E489"),sQuery(id+"F3.wireOp",EDGE,"E490"),sQuery(id+"F3.wireOp",EDGE,"E491")])],"isStart":false});
            var sketch = newSketch(context, id + "F5", { "sketchPlane" : qUnion([Q0])});
            skLineSegment(sketch, "E492", {"start": v(-5, 53.63) * mm, "end": v(-5, 48.62) * mm});
            skLineSegment(sketch, "E493", {"start": v(-5, 48.62) * mm, "end": v(-158.16, 48.62) * mm});
            skLineSegment(sketch, "E494", {"start": v(-158.16, 48.62) * mm, "end": v(-158.16, -48.62) * mm});
            skLineSegment(sketch, "E495", {"start": v(-158.16, -48.62) * mm, "end": v(158.16, -48.62) * mm});
            skLineSegment(sketch, "E496", {"start": v(158.16, -48.62) * mm, "end": v(158.16, 48.62) * mm});
            skLineSegment(sketch, "E497", {"start": v(158.16, 48.62) * mm, "end": v(5, 48.62) * mm});
            skLineSegment(sketch, "E498", {"start": v(5, 48.62) * mm, "end": v(5, 53.62) * mm});
            skLineSegment(sketch, "E499", {"start": v(5, 53.62) * mm, "end": v(161.16, 53.62) * mm});
            skLineSegment(sketch, "E500", {"start": v(161.16, 53.62) * mm, "end": v(161.32, 53.62) * mm});
            skLineSegment(sketch, "E501", {"start": v(161.32, 53.62) * mm, "end": v(161.48, 53.6) * mm});
            skLineSegment(sketch, "E502", {"start": v(161.48, 53.6) * mm, "end": v(161.63, 53.57) * mm});
            skLineSegment(sketch, "E503", {"start": v(161.63, 53.57) * mm, "end": v(161.78, 53.53) * mm});
            skLineSegment(sketch, "E504", {"start": v(161.78, 53.53) * mm, "end": v(161.93, 53.47) * mm});
            skLineSegment(sketch, "E505", {"start": v(161.93, 53.47) * mm, "end": v(162.07, 53.4) * mm});
            skLineSegment(sketch, "E506", {"start": v(162.07, 53.4) * mm, "end": v(162.2, 53.33) * mm});
            skLineSegment(sketch, "E507", {"start": v(162.2, 53.33) * mm, "end": v(162.34, 53.24) * mm});
            skLineSegment(sketch, "E508", {"start": v(162.34, 53.24) * mm, "end": v(162.46, 53.15) * mm});
            skLineSegment(sketch, "E509", {"start": v(162.46, 53.15) * mm, "end": v(162.58, 53.04) * mm});
            skLineSegment(sketch, "E510", {"start": v(162.58, 53.04) * mm, "end": v(162.68, 52.92) * mm});
            skLineSegment(sketch, "E511", {"start": v(162.68, 52.92) * mm, "end": v(162.78, 52.8) * mm});
            skLineSegment(sketch, "E512", {"start": v(162.78, 52.8) * mm, "end": v(162.87, 52.67) * mm});
            skLineSegment(sketch, "E513", {"start": v(162.87, 52.67) * mm, "end": v(162.94, 52.53) * mm});
            skLineSegment(sketch, "E514", {"start": v(162.94, 52.53) * mm, "end": v(163, 52.4) * mm});
            skLineSegment(sketch, "E515", {"start": v(163, 52.4) * mm, "end": v(163.06, 52.24) * mm});
            skLineSegment(sketch, "E516", {"start": v(163.06, 52.24) * mm, "end": v(163.1, 52.1) * mm});
            skLineSegment(sketch, "E517", {"start": v(163.1, 52.1) * mm, "end": v(163.14, 51.94) * mm});
            skLineSegment(sketch, "E518", {"start": v(163.14, 51.94) * mm, "end": v(163.16, 51.78) * mm});
            skLineSegment(sketch, "E519", {"start": v(163.16, 51.78) * mm, "end": v(163.16, 51.62) * mm});
            skLineSegment(sketch, "E520", {"start": v(163.16, 51.62) * mm, "end": v(163.16, -51.62) * mm});
            skLineSegment(sketch, "E521", {"start": v(163.16, -51.62) * mm, "end": v(163.16, -51.78) * mm});
            skLineSegment(sketch, "E522", {"start": v(163.16, -51.78) * mm, "end": v(163.14, -51.94) * mm});
            skLineSegment(sketch, "E523", {"start": v(163.14, -51.94) * mm, "end": v(163.1, -52.1) * mm});
            skLineSegment(sketch, "E524", {"start": v(163.1, -52.1) * mm, "end": v(163.06, -52.25) * mm});
            skLineSegment(sketch, "E525", {"start": v(163.06, -52.25) * mm, "end": v(163, -52.4) * mm});
            skLineSegment(sketch, "E526", {"start": v(163, -52.4) * mm, "end": v(162.94, -52.53) * mm});
            skLineSegment(sketch, "E527", {"start": v(162.94, -52.53) * mm, "end": v(162.87, -52.67) * mm});
            skLineSegment(sketch, "E528", {"start": v(162.87, -52.67) * mm, "end": v(162.78, -52.8) * mm});
            skLineSegment(sketch, "E529", {"start": v(162.78, -52.8) * mm, "end": v(162.68, -52.92) * mm});
            skLineSegment(sketch, "E530", {"start": v(162.68, -52.92) * mm, "end": v(162.58, -53.04) * mm});
            skLineSegment(sketch, "E531", {"start": v(162.58, -53.04) * mm, "end": v(162.46, -53.15) * mm});
            skLineSegment(sketch, "E532", {"start": v(162.46, -53.15) * mm, "end": v(162.34, -53.24) * mm});
            skLineSegment(sketch, "E533", {"start": v(162.34, -53.24) * mm, "end": v(162.2, -53.33) * mm});
            skLineSegment(sketch, "E534", {"start": v(162.2, -53.33) * mm, "end": v(162.07, -53.4) * mm});
            skLineSegment(sketch, "E535", {"start": v(162.07, -53.4) * mm, "end": v(161.93, -53.47) * mm});
            skLineSegment(sketch, "E536", {"start": v(161.93, -53.47) * mm, "end": v(161.78, -53.53) * mm});
            skLineSegment(sketch, "E537", {"start": v(161.78, -53.53) * mm, "end": v(161.63, -53.57) * mm});
            skLineSegment(sketch, "E538", {"start": v(161.63, -53.57) * mm, "end": v(161.48, -53.6) * mm});
            skLineSegment(sketch, "E539", {"start": v(161.48, -53.6) * mm, "end": v(161.32, -53.62) * mm});
            skLineSegment(sketch, "E540", {"start": v(161.32, -53.62) * mm, "end": v(161.16, -53.63) * mm});
            skLineSegment(sketch, "E541", {"start": v(161.16, -53.63) * mm, "end": v(-161.16, -53.63) * mm});
            skLineSegment(sketch, "E542", {"start": v(-161.16, -53.63) * mm, "end": v(-161.32, -53.62) * mm});
            skLineSegment(sketch, "E543", {"start": v(-161.32, -53.62) * mm, "end": v(-161.48, -53.6) * mm});
            skLineSegment(sketch, "E544", {"start": v(-161.48, -53.6) * mm, "end": v(-161.63, -53.57) * mm});
            skLineSegment(sketch, "E545", {"start": v(-161.63, -53.57) * mm, "end": v(-161.78, -53.53) * mm});
            skLineSegment(sketch, "E546", {"start": v(-161.78, -53.53) * mm, "end": v(-161.93, -53.47) * mm});
            skLineSegment(sketch, "E547", {"start": v(-161.93, -53.47) * mm, "end": v(-162.07, -53.4) * mm});
            skLineSegment(sketch, "E548", {"start": v(-162.07, -53.4) * mm, "end": v(-162.2, -53.33) * mm});
            skLineSegment(sketch, "E549", {"start": v(-162.2, -53.33) * mm, "end": v(-162.34, -53.24) * mm});
            skLineSegment(sketch, "E550", {"start": v(-162.34, -53.24) * mm, "end": v(-162.46, -53.15) * mm});
            skLineSegment(sketch, "E551", {"start": v(-162.46, -53.15) * mm, "end": v(-162.58, -53.04) * mm});
            skLineSegment(sketch, "E552", {"start": v(-162.58, -53.04) * mm, "end": v(-162.68, -52.92) * mm});
            skLineSegment(sketch, "E553", {"start": v(-162.68, -52.92) * mm, "end": v(-162.78, -52.8) * mm});
            skLineSegment(sketch, "E554", {"start": v(-162.78, -52.8) * mm, "end": v(-162.87, -52.67) * mm});
            skLineSegment(sketch, "E555", {"start": v(-162.87, -52.67) * mm, "end": v(-162.95, -52.53) * mm});
            skLineSegment(sketch, "E556", {"start": v(-162.95, -52.53) * mm, "end": v(-163.01, -52.4) * mm});
            skLineSegment(sketch, "E557", {"start": v(-163.01, -52.4) * mm, "end": v(-163.07, -52.25) * mm});
            skLineSegment(sketch, "E558", {"start": v(-163.07, -52.25) * mm, "end": v(-163.1, -52.1) * mm});
            skLineSegment(sketch, "E559", {"start": v(-163.1, -52.1) * mm, "end": v(-163.14, -51.94) * mm});
            skLineSegment(sketch, "E560", {"start": v(-163.14, -51.94) * mm, "end": v(-163.16, -51.78) * mm});
            skLineSegment(sketch, "E561", {"start": v(-163.16, -51.78) * mm, "end": v(-163.16, -51.63) * mm});
            skLineSegment(sketch, "E562", {"start": v(-163.16, -51.63) * mm, "end": v(-163.16, 51.62) * mm});
            skLineSegment(sketch, "E563", {"start": v(-163.16, 51.62) * mm, "end": v(-163.16, 51.78) * mm});
            skLineSegment(sketch, "E564", {"start": v(-163.16, 51.78) * mm, "end": v(-163.14, 51.94) * mm});
            skLineSegment(sketch, "E565", {"start": v(-163.14, 51.94) * mm, "end": v(-163.1, 52.1) * mm});
            skLineSegment(sketch, "E566", {"start": v(-163.1, 52.1) * mm, "end": v(-163.07, 52.24) * mm});
            skLineSegment(sketch, "E567", {"start": v(-163.07, 52.24) * mm, "end": v(-163.01, 52.4) * mm});
            skLineSegment(sketch, "E568", {"start": v(-163.01, 52.4) * mm, "end": v(-162.95, 52.53) * mm});
            skLineSegment(sketch, "E569", {"start": v(-162.95, 52.53) * mm, "end": v(-162.87, 52.67) * mm});
            skLineSegment(sketch, "E570", {"start": v(-162.87, 52.67) * mm, "end": v(-162.78, 52.8) * mm});
            skLineSegment(sketch, "E571", {"start": v(-162.78, 52.8) * mm, "end": v(-162.68, 52.92) * mm});
            skLineSegment(sketch, "E572", {"start": v(-162.68, 52.92) * mm, "end": v(-162.58, 53.04) * mm});
            skLineSegment(sketch, "E573", {"start": v(-162.58, 53.04) * mm, "end": v(-162.46, 53.15) * mm});
            skLineSegment(sketch, "E574", {"start": v(-162.46, 53.15) * mm, "end": v(-162.34, 53.24) * mm});
            skLineSegment(sketch, "E575", {"start": v(-162.34, 53.24) * mm, "end": v(-162.2, 53.33) * mm});
            skLineSegment(sketch, "E576", {"start": v(-162.2, 53.33) * mm, "end": v(-162.07, 53.4) * mm});
            skLineSegment(sketch, "E577", {"start": v(-162.07, 53.4) * mm, "end": v(-161.93, 53.47) * mm});
            skLineSegment(sketch, "E578", {"start": v(-161.93, 53.47) * mm, "end": v(-161.78, 53.53) * mm});
            skLineSegment(sketch, "E579", {"start": v(-161.78, 53.53) * mm, "end": v(-161.63, 53.57) * mm});
            skLineSegment(sketch, "E580", {"start": v(-161.63, 53.57) * mm, "end": v(-161.48, 53.6) * mm});
            skLineSegment(sketch, "E581", {"start": v(-161.48, 53.6) * mm, "end": v(-161.32, 53.62) * mm});
            skLineSegment(sketch, "E582", {"start": v(-161.32, 53.62) * mm, "end": v(-161.16, 53.63) * mm});
            skLineSegment(sketch, "E583", {"start": v(-161.16, 53.63) * mm, "end": v(-5, 53.63) * mm});
            skLineSegment(sketch, "E584", {"start": v(160.2, -49.7) * mm, "end": v(159.78, -49.91) * mm});
            skLineSegment(sketch, "E585", {"start": v(159.78, -49.91) * mm, "end": v(159.45, -50.24) * mm});
            skLineSegment(sketch, "E586", {"start": v(159.45, -50.24) * mm, "end": v(159.24, -50.66) * mm});
            skLineSegment(sketch, "E587", {"start": v(159.24, -50.66) * mm, "end": v(159.16, -51.13) * mm});
            skLineSegment(sketch, "E588", {"start": v(159.16, -51.13) * mm, "end": v(159.24, -51.59) * mm});
            skLineSegment(sketch, "E589", {"start": v(159.24, -51.59) * mm, "end": v(159.45, -52) * mm});
            skLineSegment(sketch, "E590", {"start": v(159.45, -52) * mm, "end": v(159.78, -52.34) * mm});
            skLineSegment(sketch, "E591", {"start": v(159.78, -52.34) * mm, "end": v(160.2, -52.55) * mm});
            skLineSegment(sketch, "E592", {"start": v(160.2, -52.55) * mm, "end": v(160.66, -52.63) * mm});
            skLineSegment(sketch, "E593", {"start": v(160.66, -52.63) * mm, "end": v(161.13, -52.55) * mm});
            skLineSegment(sketch, "E594", {"start": v(161.13, -52.55) * mm, "end": v(161.54, -52.34) * mm});
            skLineSegment(sketch, "E595", {"start": v(161.54, -52.34) * mm, "end": v(161.88, -52) * mm});
            skLineSegment(sketch, "E596", {"start": v(161.88, -52) * mm, "end": v(162.09, -51.59) * mm});
            skLineSegment(sketch, "E597", {"start": v(162.09, -51.59) * mm, "end": v(162.16, -51.13) * mm});
            skLineSegment(sketch, "E598", {"start": v(162.16, -51.13) * mm, "end": v(162.09, -50.66) * mm});
            skLineSegment(sketch, "E599", {"start": v(162.09, -50.66) * mm, "end": v(161.88, -50.24) * mm});
            skLineSegment(sketch, "E600", {"start": v(161.88, -50.24) * mm, "end": v(161.54, -49.91) * mm});
            skLineSegment(sketch, "E601", {"start": v(161.54, -49.91) * mm, "end": v(161.13, -49.7) * mm});
            skLineSegment(sketch, "E602", {"start": v(161.13, -49.7) * mm, "end": v(160.66, -49.63) * mm});
            skLineSegment(sketch, "E603", {"start": v(160.66, -49.63) * mm, "end": v(160.2, -49.7) * mm});
            skLineSegment(sketch, "E604", {"start": v(53.1, -49.7) * mm, "end": v(52.67, -49.91) * mm});
            skLineSegment(sketch, "E605", {"start": v(52.67, -49.91) * mm, "end": v(52.34, -50.24) * mm});
            skLineSegment(sketch, "E606", {"start": v(52.34, -50.24) * mm, "end": v(52.13, -50.66) * mm});
            skLineSegment(sketch, "E607", {"start": v(52.13, -50.66) * mm, "end": v(52.05, -51.13) * mm});
            skLineSegment(sketch, "E608", {"start": v(52.05, -51.13) * mm, "end": v(52.13, -51.59) * mm});
            skLineSegment(sketch, "E609", {"start": v(52.13, -51.59) * mm, "end": v(52.34, -52) * mm});
            skLineSegment(sketch, "E610", {"start": v(52.34, -52) * mm, "end": v(52.67, -52.34) * mm});
            skLineSegment(sketch, "E611", {"start": v(52.67, -52.34) * mm, "end": v(53.1, -52.55) * mm});
            skLineSegment(sketch, "E612", {"start": v(53.1, -52.55) * mm, "end": v(53.55, -52.63) * mm});
            skLineSegment(sketch, "E613", {"start": v(53.55, -52.63) * mm, "end": v(54.02, -52.55) * mm});
            skLineSegment(sketch, "E614", {"start": v(54.02, -52.55) * mm, "end": v(54.44, -52.34) * mm});
            skLineSegment(sketch, "E615", {"start": v(54.44, -52.34) * mm, "end": v(54.77, -52) * mm});
            skLineSegment(sketch, "E616", {"start": v(54.77, -52) * mm, "end": v(54.98, -51.59) * mm});
            skLineSegment(sketch, "E617", {"start": v(54.98, -51.59) * mm, "end": v(55.05, -51.13) * mm});
            skLineSegment(sketch, "E618", {"start": v(55.05, -51.13) * mm, "end": v(54.98, -50.66) * mm});
            skLineSegment(sketch, "E619", {"start": v(54.98, -50.66) * mm, "end": v(54.77, -50.24) * mm});
            skLineSegment(sketch, "E620", {"start": v(54.77, -50.24) * mm, "end": v(54.44, -49.91) * mm});
            skLineSegment(sketch, "E621", {"start": v(54.44, -49.91) * mm, "end": v(54.02, -49.7) * mm});
            skLineSegment(sketch, "E622", {"start": v(54.02, -49.7) * mm, "end": v(53.55, -49.63) * mm});
            skLineSegment(sketch, "E623", {"start": v(53.55, -49.63) * mm, "end": v(53.1, -49.7) * mm});
            skLineSegment(sketch, "E624", {"start": v(-54.02, -49.7) * mm, "end": v(-54.44, -49.91) * mm});
            skLineSegment(sketch, "E625", {"start": v(-54.44, -49.91) * mm, "end": v(-54.77, -50.24) * mm});
            skLineSegment(sketch, "E626", {"start": v(-54.77, -50.24) * mm, "end": v(-54.98, -50.66) * mm});
            skLineSegment(sketch, "E627", {"start": v(-54.98, -50.66) * mm, "end": v(-55.06, -51.13) * mm});
            skLineSegment(sketch, "E628", {"start": v(-55.06, -51.13) * mm, "end": v(-54.98, -51.59) * mm});
            skLineSegment(sketch, "E629", {"start": v(-54.98, -51.59) * mm, "end": v(-54.77, -52) * mm});
            skLineSegment(sketch, "E630", {"start": v(-54.77, -52) * mm, "end": v(-54.44, -52.34) * mm});
            skLineSegment(sketch, "E631", {"start": v(-54.44, -52.34) * mm, "end": v(-54.02, -52.55) * mm});
            skLineSegment(sketch, "E632", {"start": v(-54.02, -52.55) * mm, "end": v(-53.55, -52.63) * mm});
            skLineSegment(sketch, "E633", {"start": v(-53.55, -52.63) * mm, "end": v(-53.1, -52.55) * mm});
            skLineSegment(sketch, "E634", {"start": v(-53.1, -52.55) * mm, "end": v(-52.67, -52.34) * mm});
            skLineSegment(sketch, "E635", {"start": v(-52.67, -52.34) * mm, "end": v(-52.34, -52) * mm});
            skLineSegment(sketch, "E636", {"start": v(-52.34, -52) * mm, "end": v(-52.13, -51.59) * mm});
            skLineSegment(sketch, "E637", {"start": v(-52.13, -51.59) * mm, "end": v(-52.06, -51.13) * mm});
            skLineSegment(sketch, "E638", {"start": v(-52.06, -51.13) * mm, "end": v(-52.13, -50.66) * mm});
            skLineSegment(sketch, "E639", {"start": v(-52.13, -50.66) * mm, "end": v(-52.34, -50.24) * mm});
            skLineSegment(sketch, "E640", {"start": v(-52.34, -50.24) * mm, "end": v(-52.67, -49.91) * mm});
            skLineSegment(sketch, "E641", {"start": v(-52.67, -49.91) * mm, "end": v(-53.1, -49.7) * mm});
            skLineSegment(sketch, "E642", {"start": v(-53.1, -49.7) * mm, "end": v(-53.55, -49.63) * mm});
            skLineSegment(sketch, "E643", {"start": v(-53.55, -49.63) * mm, "end": v(-54.02, -49.7) * mm});
            skLineSegment(sketch, "E644", {"start": v(-161.13, -49.7) * mm, "end": v(-161.54, -49.91) * mm});
            skLineSegment(sketch, "E645", {"start": v(-161.54, -49.91) * mm, "end": v(-161.88, -50.24) * mm});
            skLineSegment(sketch, "E646", {"start": v(-161.88, -50.24) * mm, "end": v(-162.1, -50.66) * mm});
            skLineSegment(sketch, "E647", {"start": v(-162.1, -50.66) * mm, "end": v(-162.16, -51.13) * mm});
            skLineSegment(sketch, "E648", {"start": v(-162.16, -51.13) * mm, "end": v(-162.1, -51.59) * mm});
            skLineSegment(sketch, "E649", {"start": v(-162.1, -51.59) * mm, "end": v(-161.88, -52) * mm});
            skLineSegment(sketch, "E650", {"start": v(-161.88, -52) * mm, "end": v(-161.54, -52.34) * mm});
            skLineSegment(sketch, "E651", {"start": v(-161.54, -52.34) * mm, "end": v(-161.13, -52.55) * mm});
            skLineSegment(sketch, "E652", {"start": v(-161.13, -52.55) * mm, "end": v(-160.66, -52.63) * mm});
            skLineSegment(sketch, "E653", {"start": v(-160.66, -52.63) * mm, "end": v(-160.2, -52.55) * mm});
            skLineSegment(sketch, "E654", {"start": v(-160.2, -52.55) * mm, "end": v(-159.78, -52.34) * mm});
            skLineSegment(sketch, "E655", {"start": v(-159.78, -52.34) * mm, "end": v(-159.45, -52) * mm});
            skLineSegment(sketch, "E656", {"start": v(-159.45, -52) * mm, "end": v(-159.24, -51.59) * mm});
            skLineSegment(sketch, "E657", {"start": v(-159.24, -51.59) * mm, "end": v(-159.16, -51.13) * mm});
            skLineSegment(sketch, "E658", {"start": v(-159.16, -51.13) * mm, "end": v(-159.24, -50.66) * mm});
            skLineSegment(sketch, "E659", {"start": v(-159.24, -50.66) * mm, "end": v(-159.45, -50.24) * mm});
            skLineSegment(sketch, "E660", {"start": v(-159.45, -50.24) * mm, "end": v(-159.78, -49.91) * mm});
            skLineSegment(sketch, "E661", {"start": v(-159.78, -49.91) * mm, "end": v(-160.2, -49.7) * mm});
            skLineSegment(sketch, "E662", {"start": v(-160.2, -49.7) * mm, "end": v(-160.66, -49.63) * mm});
            skLineSegment(sketch, "E663", {"start": v(-160.66, -49.63) * mm, "end": v(-161.13, -49.7) * mm});
            skLineSegment(sketch, "E664", {"start": v(-54.02, 52.55) * mm, "end": v(-54.44, 52.34) * mm});
            skLineSegment(sketch, "E665", {"start": v(-54.44, 52.34) * mm, "end": v(-54.77, 52) * mm});
            skLineSegment(sketch, "E666", {"start": v(-54.77, 52) * mm, "end": v(-54.98, 51.59) * mm});
            skLineSegment(sketch, "E667", {"start": v(-54.98, 51.59) * mm, "end": v(-55.06, 51.12) * mm});
            skLineSegment(sketch, "E668", {"start": v(-55.06, 51.12) * mm, "end": v(-54.98, 50.66) * mm});
            skLineSegment(sketch, "E669", {"start": v(-54.98, 50.66) * mm, "end": v(-54.77, 50.24) * mm});
            skLineSegment(sketch, "E670", {"start": v(-54.77, 50.24) * mm, "end": v(-54.44, 49.91) * mm});
            skLineSegment(sketch, "E671", {"start": v(-54.44, 49.91) * mm, "end": v(-54.02, 49.7) * mm});
            skLineSegment(sketch, "E672", {"start": v(-54.02, 49.7) * mm, "end": v(-53.55, 49.62) * mm});
            skLineSegment(sketch, "E673", {"start": v(-53.55, 49.62) * mm, "end": v(-53.1, 49.7) * mm});
            skLineSegment(sketch, "E674", {"start": v(-53.1, 49.7) * mm, "end": v(-52.67, 49.91) * mm});
            skLineSegment(sketch, "E675", {"start": v(-52.67, 49.91) * mm, "end": v(-52.34, 50.24) * mm});
            skLineSegment(sketch, "E676", {"start": v(-52.34, 50.24) * mm, "end": v(-52.13, 50.66) * mm});
            skLineSegment(sketch, "E677", {"start": v(-52.13, 50.66) * mm, "end": v(-52.06, 51.12) * mm});
            skLineSegment(sketch, "E678", {"start": v(-52.06, 51.12) * mm, "end": v(-52.13, 51.59) * mm});
            skLineSegment(sketch, "E679", {"start": v(-52.13, 51.59) * mm, "end": v(-52.34, 52) * mm});
            skLineSegment(sketch, "E680", {"start": v(-52.34, 52) * mm, "end": v(-52.67, 52.34) * mm});
            skLineSegment(sketch, "E681", {"start": v(-52.67, 52.34) * mm, "end": v(-53.1, 52.55) * mm});
            skLineSegment(sketch, "E682", {"start": v(-53.1, 52.55) * mm, "end": v(-53.55, 52.62) * mm});
            skLineSegment(sketch, "E683", {"start": v(-53.55, 52.62) * mm, "end": v(-54.02, 52.55) * mm});
            skLineSegment(sketch, "E684", {"start": v(53.1, 52.55) * mm, "end": v(52.67, 52.34) * mm});
            skLineSegment(sketch, "E685", {"start": v(52.67, 52.34) * mm, "end": v(52.34, 52) * mm});
            skLineSegment(sketch, "E686", {"start": v(52.34, 52) * mm, "end": v(52.13, 51.59) * mm});
            skLineSegment(sketch, "E687", {"start": v(52.13, 51.59) * mm, "end": v(52.05, 51.12) * mm});
            skLineSegment(sketch, "E688", {"start": v(52.05, 51.12) * mm, "end": v(52.13, 50.66) * mm});
            skLineSegment(sketch, "E689", {"start": v(52.13, 50.66) * mm, "end": v(52.34, 50.24) * mm});
            skLineSegment(sketch, "E690", {"start": v(52.34, 50.24) * mm, "end": v(52.67, 49.91) * mm});
            skLineSegment(sketch, "E691", {"start": v(52.67, 49.91) * mm, "end": v(53.1, 49.7) * mm});
            skLineSegment(sketch, "E692", {"start": v(53.1, 49.7) * mm, "end": v(53.55, 49.62) * mm});
            skLineSegment(sketch, "E693", {"start": v(53.55, 49.62) * mm, "end": v(54.02, 49.7) * mm});
            skLineSegment(sketch, "E694", {"start": v(54.02, 49.7) * mm, "end": v(54.44, 49.91) * mm});
            skLineSegment(sketch, "E695", {"start": v(54.44, 49.91) * mm, "end": v(54.77, 50.24) * mm});
            skLineSegment(sketch, "E696", {"start": v(54.77, 50.24) * mm, "end": v(54.98, 50.66) * mm});
            skLineSegment(sketch, "E697", {"start": v(54.98, 50.66) * mm, "end": v(55.05, 51.12) * mm});
            skLineSegment(sketch, "E698", {"start": v(55.05, 51.12) * mm, "end": v(54.98, 51.59) * mm});
            skLineSegment(sketch, "E699", {"start": v(54.98, 51.59) * mm, "end": v(54.77, 52) * mm});
            skLineSegment(sketch, "E700", {"start": v(54.77, 52) * mm, "end": v(54.44, 52.34) * mm});
            skLineSegment(sketch, "E701", {"start": v(54.44, 52.34) * mm, "end": v(54.02, 52.55) * mm});
            skLineSegment(sketch, "E702", {"start": v(54.02, 52.55) * mm, "end": v(53.55, 52.62) * mm});
            skLineSegment(sketch, "E703", {"start": v(53.55, 52.62) * mm, "end": v(53.1, 52.55) * mm});
            skLineSegment(sketch, "E704", {"start": v(160.2, 52.55) * mm, "end": v(159.78, 52.34) * mm});
            skLineSegment(sketch, "E705", {"start": v(159.78, 52.34) * mm, "end": v(159.45, 52) * mm});
            skLineSegment(sketch, "E706", {"start": v(159.45, 52) * mm, "end": v(159.24, 51.59) * mm});
            skLineSegment(sketch, "E707", {"start": v(159.24, 51.59) * mm, "end": v(159.16, 51.12) * mm});
            skLineSegment(sketch, "E708", {"start": v(159.16, 51.12) * mm, "end": v(159.24, 50.66) * mm});
            skLineSegment(sketch, "E709", {"start": v(159.24, 50.66) * mm, "end": v(159.45, 50.24) * mm});
            skLineSegment(sketch, "E710", {"start": v(159.45, 50.24) * mm, "end": v(159.78, 49.91) * mm});
            skLineSegment(sketch, "E711", {"start": v(159.78, 49.91) * mm, "end": v(160.2, 49.7) * mm});
            skLineSegment(sketch, "E712", {"start": v(160.2, 49.7) * mm, "end": v(160.66, 49.62) * mm});
            skLineSegment(sketch, "E713", {"start": v(160.66, 49.62) * mm, "end": v(161.13, 49.7) * mm});
            skLineSegment(sketch, "E714", {"start": v(161.13, 49.7) * mm, "end": v(161.54, 49.91) * mm});
            skLineSegment(sketch, "E715", {"start": v(161.54, 49.91) * mm, "end": v(161.88, 50.24) * mm});
            skLineSegment(sketch, "E716", {"start": v(161.88, 50.24) * mm, "end": v(162.09, 50.66) * mm});
            skLineSegment(sketch, "E717", {"start": v(162.09, 50.66) * mm, "end": v(162.16, 51.12) * mm});
            skLineSegment(sketch, "E718", {"start": v(162.16, 51.12) * mm, "end": v(162.09, 51.59) * mm});
            skLineSegment(sketch, "E719", {"start": v(162.09, 51.59) * mm, "end": v(161.88, 52) * mm});
            skLineSegment(sketch, "E720", {"start": v(161.88, 52) * mm, "end": v(161.54, 52.34) * mm});
            skLineSegment(sketch, "E721", {"start": v(161.54, 52.34) * mm, "end": v(161.13, 52.55) * mm});
            skLineSegment(sketch, "E722", {"start": v(161.13, 52.55) * mm, "end": v(160.66, 52.62) * mm});
            skLineSegment(sketch, "E723", {"start": v(160.66, 52.62) * mm, "end": v(160.2, 52.55) * mm});
            skLineSegment(sketch, "E724", {"start": v(-161.13, 52.55) * mm, "end": v(-161.54, 52.34) * mm});
            skLineSegment(sketch, "E725", {"start": v(-161.54, 52.34) * mm, "end": v(-161.88, 52) * mm});
            skLineSegment(sketch, "E726", {"start": v(-161.88, 52) * mm, "end": v(-162.1, 51.59) * mm});
            skLineSegment(sketch, "E727", {"start": v(-162.1, 51.59) * mm, "end": v(-162.16, 51.12) * mm});
            skLineSegment(sketch, "E728", {"start": v(-162.16, 51.12) * mm, "end": v(-162.1, 50.66) * mm});
            skLineSegment(sketch, "E729", {"start": v(-162.1, 50.66) * mm, "end": v(-161.88, 50.24) * mm});
            skLineSegment(sketch, "E730", {"start": v(-161.88, 50.24) * mm, "end": v(-161.54, 49.91) * mm});
            skLineSegment(sketch, "E731", {"start": v(-161.54, 49.91) * mm, "end": v(-161.13, 49.7) * mm});
            skLineSegment(sketch, "E732", {"start": v(-161.13, 49.7) * mm, "end": v(-160.66, 49.62) * mm});
            skLineSegment(sketch, "E733", {"start": v(-160.66, 49.62) * mm, "end": v(-160.2, 49.7) * mm});
            skLineSegment(sketch, "E734", {"start": v(-160.2, 49.7) * mm, "end": v(-159.78, 49.91) * mm});
            skLineSegment(sketch, "E735", {"start": v(-159.78, 49.91) * mm, "end": v(-159.45, 50.24) * mm});
            skLineSegment(sketch, "E736", {"start": v(-159.45, 50.24) * mm, "end": v(-159.24, 50.66) * mm});
            skLineSegment(sketch, "E737", {"start": v(-159.24, 50.66) * mm, "end": v(-159.16, 51.12) * mm});
            skLineSegment(sketch, "E738", {"start": v(-159.16, 51.12) * mm, "end": v(-159.24, 51.59) * mm});
            skLineSegment(sketch, "E739", {"start": v(-159.24, 51.59) * mm, "end": v(-159.45, 52) * mm});
            skLineSegment(sketch, "E740", {"start": v(-159.45, 52) * mm, "end": v(-159.78, 52.34) * mm});
            skLineSegment(sketch, "E741", {"start": v(-159.78, 52.34) * mm, "end": v(-160.2, 52.55) * mm});
            skLineSegment(sketch, "E742", {"start": v(-160.2, 52.55) * mm, "end": v(-160.66, 52.62) * mm});
            skLineSegment(sketch, "E743", {"start": v(-160.66, 52.62) * mm, "end": v(-161.13, 52.55) * mm});
            skSolve(sketch);
        }
        {
            var Q0;
            Q0 = qSketchRegion(id + "F5", true);
            extrude(context, id + "F6", {"entities" : qUnion([Q0]), "depth" : 6 * mm, "offsetDistance" : 25 * mm});
        }
        {
            var Q0;
            Q0=makeQuery(id+"F6.opExtrude","CAP_FACE",FACE,{"disambiguationData":[OSD([sQuery(id+"F5.wireOp",EDGE,"E492"),sQuery(id+"F5.wireOp",EDGE,"E493"),sQuery(id+"F5.wireOp",EDGE,"E494"),sQuery(id+"F5.wireOp",EDGE,"E495"),sQuery(id+"F5.wireOp",EDGE,"E496"),sQuery(id+"F5.wireOp",EDGE,"E497"),sQuery(id+"F5.wireOp",EDGE,"E498"),sQuery(id+"F5.wireOp",EDGE,"E499"),sQuery(id+"F5.wireOp",EDGE,"E500"),sQuery(id+"F5.wireOp",EDGE,"E501"),sQuery(id+"F5.wireOp",EDGE,"E502"),sQuery(id+"F5.wireOp",EDGE,"E503"),sQuery(id+"F5.wireOp",EDGE,"E504"),sQuery(id+"F5.wireOp",EDGE,"E505"),sQuery(id+"F5.wireOp",EDGE,"E506"),sQuery(id+"F5.wireOp",EDGE,"E507"),sQuery(id+"F5.wireOp",EDGE,"E508"),sQuery(id+"F5.wireOp",EDGE,"E509"),sQuery(id+"F5.wireOp",EDGE,"E510"),sQuery(id+"F5.wireOp",EDGE,"E511"),sQuery(id+"F5.wireOp",EDGE,"E512"),sQuery(id+"F5.wireOp",EDGE,"E513"),sQuery(id+"F5.wireOp",EDGE,"E514"),sQuery(id+"F5.wireOp",EDGE,"E515"),sQuery(id+"F5.wireOp",EDGE,"E516"),sQuery(id+"F5.wireOp",EDGE,"E517"),sQuery(id+"F5.wireOp",EDGE,"E518"),sQuery(id+"F5.wireOp",EDGE,"E519"),sQuery(id+"F5.wireOp",EDGE,"E520"),sQuery(id+"F5.wireOp",EDGE,"E521"),sQuery(id+"F5.wireOp",EDGE,"E522"),sQuery(id+"F5.wireOp",EDGE,"E523"),sQuery(id+"F5.wireOp",EDGE,"E524"),sQuery(id+"F5.wireOp",EDGE,"E525"),sQuery(id+"F5.wireOp",EDGE,"E526"),sQuery(id+"F5.wireOp",EDGE,"E527"),sQuery(id+"F5.wireOp",EDGE,"E528"),sQuery(id+"F5.wireOp",EDGE,"E529"),sQuery(id+"F5.wireOp",EDGE,"E530"),sQuery(id+"F5.wireOp",EDGE,"E531"),sQuery(id+"F5.wireOp",EDGE,"E532"),sQuery(id+"F5.wireOp",EDGE,"E533"),sQuery(id+"F5.wireOp",EDGE,"E534"),sQuery(id+"F5.wireOp",EDGE,"E535"),sQuery(id+"F5.wireOp",EDGE,"E536"),sQuery(id+"F5.wireOp",EDGE,"E537"),sQuery(id+"F5.wireOp",EDGE,"E538"),sQuery(id+"F5.wireOp",EDGE,"E539"),sQuery(id+"F5.wireOp",EDGE,"E540"),sQuery(id+"F5.wireOp",EDGE,"E541"),sQuery(id+"F5.wireOp",EDGE,"E542"),sQuery(id+"F5.wireOp",EDGE,"E543"),sQuery(id+"F5.wireOp",EDGE,"E544"),sQuery(id+"F5.wireOp",EDGE,"E545"),sQuery(id+"F5.wireOp",EDGE,"E546"),sQuery(id+"F5.wireOp",EDGE,"E547"),sQuery(id+"F5.wireOp",EDGE,"E548"),sQuery(id+"F5.wireOp",EDGE,"E549"),sQuery(id+"F5.wireOp",EDGE,"E550"),sQuery(id+"F5.wireOp",EDGE,"E551"),sQuery(id+"F5.wireOp",EDGE,"E552"),sQuery(id+"F5.wireOp",EDGE,"E553"),sQuery(id+"F5.wireOp",EDGE,"E554"),sQuery(id+"F5.wireOp",EDGE,"E555"),sQuery(id+"F5.wireOp",EDGE,"E556"),sQuery(id+"F5.wireOp",EDGE,"E557"),sQuery(id+"F5.wireOp",EDGE,"E558"),sQuery(id+"F5.wireOp",EDGE,"E559"),sQuery(id+"F5.wireOp",EDGE,"E560"),sQuery(id+"F5.wireOp",EDGE,"E561"),sQuery(id+"F5.wireOp",EDGE,"E562"),sQuery(id+"F5.wireOp",EDGE,"E563"),sQuery(id+"F5.wireOp",EDGE,"E564"),sQuery(id+"F5.wireOp",EDGE,"E565"),sQuery(id+"F5.wireOp",EDGE,"E566"),sQuery(id+"F5.wireOp",EDGE,"E567"),sQuery(id+"F5.wireOp",EDGE,"E568"),sQuery(id+"F5.wireOp",EDGE,"E569"),sQuery(id+"F5.wireOp",EDGE,"E570"),sQuery(id+"F5.wireOp",EDGE,"E571"),sQuery(id+"F5.wireOp",EDGE,"E572"),sQuery(id+"F5.wireOp",EDGE,"E573"),sQuery(id+"F5.wireOp",EDGE,"E574"),sQuery(id+"F5.wireOp",EDGE,"E575"),sQuery(id+"F5.wireOp",EDGE,"E576"),sQuery(id+"F5.wireOp",EDGE,"E577"),sQuery(id+"F5.wireOp",EDGE,"E578"),sQuery(id+"F5.wireOp",EDGE,"E579"),sQuery(id+"F5.wireOp",EDGE,"E580"),sQuery(id+"F5.wireOp",EDGE,"E581"),sQuery(id+"F5.wireOp",EDGE,"E582"),sQuery(id+"F5.wireOp",EDGE,"E583"),sQuery(id+"F5.wireOp",EDGE,"E584"),sQuery(id+"F5.wireOp",EDGE,"E585"),sQuery(id+"F5.wireOp",EDGE,"E586"),sQuery(id+"F5.wireOp",EDGE,"E587"),sQuery(id+"F5.wireOp",EDGE,"E588"),sQuery(id+"F5.wireOp",EDGE,"E589"),sQuery(id+"F5.wireOp",EDGE,"E590"),sQuery(id+"F5.wireOp",EDGE,"E591"),sQuery(id+"F5.wireOp",EDGE,"E592"),sQuery(id+"F5.wireOp",EDGE,"E593"),sQuery(id+"F5.wireOp",EDGE,"E594"),sQuery(id+"F5.wireOp",EDGE,"E595"),sQuery(id+"F5.wireOp",EDGE,"E596"),sQuery(id+"F5.wireOp",EDGE,"E597"),sQuery(id+"F5.wireOp",EDGE,"E598"),sQuery(id+"F5.wireOp",EDGE,"E599"),sQuery(id+"F5.wireOp",EDGE,"E600"),sQuery(id+"F5.wireOp",EDGE,"E601"),sQuery(id+"F5.wireOp",EDGE,"E602"),sQuery(id+"F5.wireOp",EDGE,"E603"),sQuery(id+"F5.wireOp",EDGE,"E604"),sQuery(id+"F5.wireOp",EDGE,"E605"),sQuery(id+"F5.wireOp",EDGE,"E606"),sQuery(id+"F5.wireOp",EDGE,"E607"),sQuery(id+"F5.wireOp",EDGE,"E608"),sQuery(id+"F5.wireOp",EDGE,"E609"),sQuery(id+"F5.wireOp",EDGE,"E610"),sQuery(id+"F5.wireOp",EDGE,"E611"),sQuery(id+"F5.wireOp",EDGE,"E612"),sQuery(id+"F5.wireOp",EDGE,"E613"),sQuery(id+"F5.wireOp",EDGE,"E614"),sQuery(id+"F5.wireOp",EDGE,"E615"),sQuery(id+"F5.wireOp",EDGE,"E616"),sQuery(id+"F5.wireOp",EDGE,"E617"),sQuery(id+"F5.wireOp",EDGE,"E618"),sQuery(id+"F5.wireOp",EDGE,"E619"),sQuery(id+"F5.wireOp",EDGE,"E620"),sQuery(id+"F5.wireOp",EDGE,"E621"),sQuery(id+"F5.wireOp",EDGE,"E622"),sQuery(id+"F5.wireOp",EDGE,"E623"),sQuery(id+"F5.wireOp",EDGE,"E624"),sQuery(id+"F5.wireOp",EDGE,"E625"),sQuery(id+"F5.wireOp",EDGE,"E626"),sQuery(id+"F5.wireOp",EDGE,"E627"),sQuery(id+"F5.wireOp",EDGE,"E628"),sQuery(id+"F5.wireOp",EDGE,"E629"),sQuery(id+"F5.wireOp",EDGE,"E630"),sQuery(id+"F5.wireOp",EDGE,"E631"),sQuery(id+"F5.wireOp",EDGE,"E632"),sQuery(id+"F5.wireOp",EDGE,"E633"),sQuery(id+"F5.wireOp",EDGE,"E634"),sQuery(id+"F5.wireOp",EDGE,"E635"),sQuery(id+"F5.wireOp",EDGE,"E636"),sQuery(id+"F5.wireOp",EDGE,"E637"),sQuery(id+"F5.wireOp",EDGE,"E638"),sQuery(id+"F5.wireOp",EDGE,"E639"),sQuery(id+"F5.wireOp",EDGE,"E640"),sQuery(id+"F5.wireOp",EDGE,"E641"),sQuery(id+"F5.wireOp",EDGE,"E642"),sQuery(id+"F5.wireOp",EDGE,"E643"),sQuery(id+"F5.wireOp",EDGE,"E644"),sQuery(id+"F5.wireOp",EDGE,"E645"),sQuery(id+"F5.wireOp",EDGE,"E646"),sQuery(id+"F5.wireOp",EDGE,"E647"),sQuery(id+"F5.wireOp",EDGE,"E648"),sQuery(id+"F5.wireOp",EDGE,"E649"),sQuery(id+"F5.wireOp",EDGE,"E650"),sQuery(id+"F5.wireOp",EDGE,"E651"),sQuery(id+"F5.wireOp",EDGE,"E652"),sQuery(id+"F5.wireOp",EDGE,"E653"),sQuery(id+"F5.wireOp",EDGE,"E654"),sQuery(id+"F5.wireOp",EDGE,"E655"),sQuery(id+"F5.wireOp",EDGE,"E656"),sQuery(id+"F5.wireOp",EDGE,"E657"),sQuery(id+"F5.wireOp",EDGE,"E658"),sQuery(id+"F5.wireOp",EDGE,"E659"),sQuery(id+"F5.wireOp",EDGE,"E660"),sQuery(id+"F5.wireOp",EDGE,"E661"),sQuery(id+"F5.wireOp",EDGE,"E662"),sQuery(id+"F5.wireOp",EDGE,"E663"),sQuery(id+"F5.wireOp",EDGE,"E664"),sQuery(id+"F5.wireOp",EDGE,"E665"),sQuery(id+"F5.wireOp",EDGE,"E666"),sQuery(id+"F5.wireOp",EDGE,"E667"),sQuery(id+"F5.wireOp",EDGE,"E668"),sQuery(id+"F5.wireOp",EDGE,"E669"),sQuery(id+"F5.wireOp",EDGE,"E670"),sQuery(id+"F5.wireOp",EDGE,"E671"),sQuery(id+"F5.wireOp",EDGE,"E672"),sQuery(id+"F5.wireOp",EDGE,"E673"),sQuery(id+"F5.wireOp",EDGE,"E674"),sQuery(id+"F5.wireOp",EDGE,"E675"),sQuery(id+"F5.wireOp",EDGE,"E676"),sQuery(id+"F5.wireOp",EDGE,"E677"),sQuery(id+"F5.wireOp",EDGE,"E678"),sQuery(id+"F5.wireOp",EDGE,"E679"),sQuery(id+"F5.wireOp",EDGE,"E680"),sQuery(id+"F5.wireOp",EDGE,"E681"),sQuery(id+"F5.wireOp",EDGE,"E682"),sQuery(id+"F5.wireOp",EDGE,"E683"),sQuery(id+"F5.wireOp",EDGE,"E684"),sQuery(id+"F5.wireOp",EDGE,"E685"),sQuery(id+"F5.wireOp",EDGE,"E686"),sQuery(id+"F5.wireOp",EDGE,"E687"),sQuery(id+"F5.wireOp",EDGE,"E688"),sQuery(id+"F5.wireOp",EDGE,"E689"),sQuery(id+"F5.wireOp",EDGE,"E690"),sQuery(id+"F5.wireOp",EDGE,"E691"),sQuery(id+"F5.wireOp",EDGE,"E692"),sQuery(id+"F5.wireOp",EDGE,"E693"),sQuery(id+"F5.wireOp",EDGE,"E694"),sQuery(id+"F5.wireOp",EDGE,"E695"),sQuery(id+"F5.wireOp",EDGE,"E696"),sQuery(id+"F5.wireOp",EDGE,"E697"),sQuery(id+"F5.wireOp",EDGE,"E698"),sQuery(id+"F5.wireOp",EDGE,"E699"),sQuery(id+"F5.wireOp",EDGE,"E700"),sQuery(id+"F5.wireOp",EDGE,"E701"),sQuery(id+"F5.wireOp",EDGE,"E702"),sQuery(id+"F5.wireOp",EDGE,"E703"),sQuery(id+"F5.wireOp",EDGE,"E704"),sQuery(id+"F5.wireOp",EDGE,"E705"),sQuery(id+"F5.wireOp",EDGE,"E706"),sQuery(id+"F5.wireOp",EDGE,"E707"),sQuery(id+"F5.wireOp",EDGE,"E708"),sQuery(id+"F5.wireOp",EDGE,"E709"),sQuery(id+"F5.wireOp",EDGE,"E710"),sQuery(id+"F5.wireOp",EDGE,"E711"),sQuery(id+"F5.wireOp",EDGE,"E712"),sQuery(id+"F5.wireOp",EDGE,"E713"),sQuery(id+"F5.wireOp",EDGE,"E714"),sQuery(id+"F5.wireOp",EDGE,"E715"),sQuery(id+"F5.wireOp",EDGE,"E716"),sQuery(id+"F5.wireOp",EDGE,"E717"),sQuery(id+"F5.wireOp",EDGE,"E718"),sQuery(id+"F5.wireOp",EDGE,"E719"),sQuery(id+"F5.wireOp",EDGE,"E720"),sQuery(id+"F5.wireOp",EDGE,"E721"),sQuery(id+"F5.wireOp",EDGE,"E722"),sQuery(id+"F5.wireOp",EDGE,"E723"),sQuery(id+"F5.wireOp",EDGE,"E724"),sQuery(id+"F5.wireOp",EDGE,"E725"),sQuery(id+"F5.wireOp",EDGE,"E726"),sQuery(id+"F5.wireOp",EDGE,"E727"),sQuery(id+"F5.wireOp",EDGE,"E728"),sQuery(id+"F5.wireOp",EDGE,"E729"),sQuery(id+"F5.wireOp",EDGE,"E730"),sQuery(id+"F5.wireOp",EDGE,"E731"),sQuery(id+"F5.wireOp",EDGE,"E732"),sQuery(id+"F5.wireOp",EDGE,"E733"),sQuery(id+"F5.wireOp",EDGE,"E734"),sQuery(id+"F5.wireOp",EDGE,"E735"),sQuery(id+"F5.wireOp",EDGE,"E736"),sQuery(id+"F5.wireOp",EDGE,"E737"),sQuery(id+"F5.wireOp",EDGE,"E738"),sQuery(id+"F5.wireOp",EDGE,"E739"),sQuery(id+"F5.wireOp",EDGE,"E740"),sQuery(id+"F5.wireOp",EDGE,"E741"),sQuery(id+"F5.wireOp",EDGE,"E742"),sQuery(id+"F5.wireOp",EDGE,"E743")])],"isStart":false});
            var sketch = newSketch(context, id + "F7", { "sketchPlane" : qUnion([Q0])});
            skLineSegment(sketch, "E744", {"start": v(161.16, 53.62) * mm, "end": v(161.32, 53.62) * mm});
            skLineSegment(sketch, "E745", {"start": v(161.32, 53.62) * mm, "end": v(161.48, 53.6) * mm});
            skLineSegment(sketch, "E746", {"start": v(161.48, 53.6) * mm, "end": v(161.63, 53.57) * mm});
            skLineSegment(sketch, "E747", {"start": v(161.63, 53.57) * mm, "end": v(161.78, 53.53) * mm});
            skLineSegment(sketch, "E748", {"start": v(161.78, 53.53) * mm, "end": v(161.93, 53.47) * mm});
            skLineSegment(sketch, "E749", {"start": v(161.93, 53.47) * mm, "end": v(162.07, 53.4) * mm});
            skLineSegment(sketch, "E750", {"start": v(162.07, 53.4) * mm, "end": v(162.2, 53.33) * mm});
            skLineSegment(sketch, "E751", {"start": v(162.2, 53.33) * mm, "end": v(162.34, 53.24) * mm});
            skLineSegment(sketch, "E752", {"start": v(162.34, 53.24) * mm, "end": v(162.46, 53.15) * mm});
            skLineSegment(sketch, "E753", {"start": v(162.46, 53.15) * mm, "end": v(162.58, 53.04) * mm});
            skLineSegment(sketch, "E754", {"start": v(162.58, 53.04) * mm, "end": v(162.68, 52.92) * mm});
            skLineSegment(sketch, "E755", {"start": v(162.68, 52.92) * mm, "end": v(162.78, 52.8) * mm});
            skLineSegment(sketch, "E756", {"start": v(162.78, 52.8) * mm, "end": v(162.87, 52.67) * mm});
            skLineSegment(sketch, "E757", {"start": v(162.87, 52.67) * mm, "end": v(162.94, 52.53) * mm});
            skLineSegment(sketch, "E758", {"start": v(162.94, 52.53) * mm, "end": v(163, 52.4) * mm});
            skLineSegment(sketch, "E759", {"start": v(163, 52.4) * mm, "end": v(163.06, 52.24) * mm});
            skLineSegment(sketch, "E760", {"start": v(163.06, 52.24) * mm, "end": v(163.1, 52.1) * mm});
            skLineSegment(sketch, "E761", {"start": v(163.1, 52.1) * mm, "end": v(163.14, 51.94) * mm});
            skLineSegment(sketch, "E762", {"start": v(163.14, 51.94) * mm, "end": v(163.16, 51.78) * mm});
            skLineSegment(sketch, "E763", {"start": v(163.16, 51.78) * mm, "end": v(163.16, 51.62) * mm});
            skLineSegment(sketch, "E764", {"start": v(163.16, 51.62) * mm, "end": v(163.16, -51.62) * mm});
            skLineSegment(sketch, "E765", {"start": v(163.16, -51.62) * mm, "end": v(163.16, -51.78) * mm});
            skLineSegment(sketch, "E766", {"start": v(163.16, -51.78) * mm, "end": v(163.14, -51.94) * mm});
            skLineSegment(sketch, "E767", {"start": v(163.14, -51.94) * mm, "end": v(163.1, -52.1) * mm});
            skLineSegment(sketch, "E768", {"start": v(163.1, -52.1) * mm, "end": v(163.06, -52.25) * mm});
            skLineSegment(sketch, "E769", {"start": v(163.06, -52.25) * mm, "end": v(163, -52.4) * mm});
            skLineSegment(sketch, "E770", {"start": v(163, -52.4) * mm, "end": v(162.94, -52.53) * mm});
            skLineSegment(sketch, "E771", {"start": v(162.94, -52.53) * mm, "end": v(162.87, -52.67) * mm});
            skLineSegment(sketch, "E772", {"start": v(162.87, -52.67) * mm, "end": v(162.78, -52.8) * mm});
            skLineSegment(sketch, "E773", {"start": v(162.78, -52.8) * mm, "end": v(162.68, -52.92) * mm});
            skLineSegment(sketch, "E774", {"start": v(162.68, -52.92) * mm, "end": v(162.58, -53.04) * mm});
            skLineSegment(sketch, "E775", {"start": v(162.58, -53.04) * mm, "end": v(162.46, -53.15) * mm});
            skLineSegment(sketch, "E776", {"start": v(162.46, -53.15) * mm, "end": v(162.34, -53.24) * mm});
            skLineSegment(sketch, "E777", {"start": v(162.34, -53.24) * mm, "end": v(162.2, -53.33) * mm});
            skLineSegment(sketch, "E778", {"start": v(162.2, -53.33) * mm, "end": v(162.07, -53.4) * mm});
            skLineSegment(sketch, "E779", {"start": v(162.07, -53.4) * mm, "end": v(161.93, -53.47) * mm});
            skLineSegment(sketch, "E780", {"start": v(161.93, -53.47) * mm, "end": v(161.78, -53.53) * mm});
            skLineSegment(sketch, "E781", {"start": v(161.78, -53.53) * mm, "end": v(161.63, -53.57) * mm});
            skLineSegment(sketch, "E782", {"start": v(161.63, -53.57) * mm, "end": v(161.48, -53.6) * mm});
            skLineSegment(sketch, "E783", {"start": v(161.48, -53.6) * mm, "end": v(161.32, -53.62) * mm});
            skLineSegment(sketch, "E784", {"start": v(161.32, -53.62) * mm, "end": v(161.16, -53.63) * mm});
            skLineSegment(sketch, "E785", {"start": v(161.16, -53.63) * mm, "end": v(-161.16, -53.63) * mm});
            skLineSegment(sketch, "E786", {"start": v(-161.16, -53.63) * mm, "end": v(-161.32, -53.62) * mm});
            skLineSegment(sketch, "E787", {"start": v(-161.32, -53.62) * mm, "end": v(-161.48, -53.6) * mm});
            skLineSegment(sketch, "E788", {"start": v(-161.48, -53.6) * mm, "end": v(-161.63, -53.57) * mm});
            skLineSegment(sketch, "E789", {"start": v(-161.63, -53.57) * mm, "end": v(-161.78, -53.53) * mm});
            skLineSegment(sketch, "E790", {"start": v(-161.78, -53.53) * mm, "end": v(-161.93, -53.47) * mm});
            skLineSegment(sketch, "E791", {"start": v(-161.93, -53.47) * mm, "end": v(-162.07, -53.4) * mm});
            skLineSegment(sketch, "E792", {"start": v(-162.07, -53.4) * mm, "end": v(-162.2, -53.33) * mm});
            skLineSegment(sketch, "E793", {"start": v(-162.2, -53.33) * mm, "end": v(-162.34, -53.24) * mm});
            skLineSegment(sketch, "E794", {"start": v(-162.34, -53.24) * mm, "end": v(-162.46, -53.15) * mm});
            skLineSegment(sketch, "E795", {"start": v(-162.46, -53.15) * mm, "end": v(-162.58, -53.04) * mm});
            skLineSegment(sketch, "E796", {"start": v(-162.58, -53.04) * mm, "end": v(-162.68, -52.92) * mm});
            skLineSegment(sketch, "E797", {"start": v(-162.68, -52.92) * mm, "end": v(-162.78, -52.8) * mm});
            skLineSegment(sketch, "E798", {"start": v(-162.78, -52.8) * mm, "end": v(-162.87, -52.67) * mm});
            skLineSegment(sketch, "E799", {"start": v(-162.87, -52.67) * mm, "end": v(-162.95, -52.53) * mm});
            skLineSegment(sketch, "E800", {"start": v(-162.95, -52.53) * mm, "end": v(-163.01, -52.4) * mm});
            skLineSegment(sketch, "E801", {"start": v(-163.01, -52.4) * mm, "end": v(-163.07, -52.25) * mm});
            skLineSegment(sketch, "E802", {"start": v(-163.07, -52.25) * mm, "end": v(-163.1, -52.1) * mm});
            skLineSegment(sketch, "E803", {"start": v(-163.1, -52.1) * mm, "end": v(-163.14, -51.94) * mm});
            skLineSegment(sketch, "E804", {"start": v(-163.14, -51.94) * mm, "end": v(-163.16, -51.78) * mm});
            skLineSegment(sketch, "E805", {"start": v(-163.16, -51.78) * mm, "end": v(-163.16, -51.63) * mm});
            skLineSegment(sketch, "E806", {"start": v(-163.16, -51.63) * mm, "end": v(-163.16, 51.62) * mm});
            skLineSegment(sketch, "E807", {"start": v(-163.16, 51.62) * mm, "end": v(-163.16, 51.78) * mm});
            skLineSegment(sketch, "E808", {"start": v(-163.16, 51.78) * mm, "end": v(-163.14, 51.94) * mm});
            skLineSegment(sketch, "E809", {"start": v(-163.14, 51.94) * mm, "end": v(-163.1, 52.1) * mm});
            skLineSegment(sketch, "E810", {"start": v(-163.1, 52.1) * mm, "end": v(-163.07, 52.24) * mm});
            skLineSegment(sketch, "E811", {"start": v(-163.07, 52.24) * mm, "end": v(-163.01, 52.4) * mm});
            skLineSegment(sketch, "E812", {"start": v(-163.01, 52.4) * mm, "end": v(-162.95, 52.53) * mm});
            skLineSegment(sketch, "E813", {"start": v(-162.95, 52.53) * mm, "end": v(-162.87, 52.67) * mm});
            skLineSegment(sketch, "E814", {"start": v(-162.87, 52.67) * mm, "end": v(-162.78, 52.8) * mm});
            skLineSegment(sketch, "E815", {"start": v(-162.78, 52.8) * mm, "end": v(-162.68, 52.92) * mm});
            skLineSegment(sketch, "E816", {"start": v(-162.68, 52.92) * mm, "end": v(-162.58, 53.04) * mm});
            skLineSegment(sketch, "E817", {"start": v(-162.58, 53.04) * mm, "end": v(-162.46, 53.15) * mm});
            skLineSegment(sketch, "E818", {"start": v(-162.46, 53.15) * mm, "end": v(-162.34, 53.24) * mm});
            skLineSegment(sketch, "E819", {"start": v(-162.34, 53.24) * mm, "end": v(-162.2, 53.33) * mm});
            skLineSegment(sketch, "E820", {"start": v(-162.2, 53.33) * mm, "end": v(-162.07, 53.4) * mm});
            skLineSegment(sketch, "E821", {"start": v(-162.07, 53.4) * mm, "end": v(-161.93, 53.47) * mm});
            skLineSegment(sketch, "E822", {"start": v(-161.93, 53.47) * mm, "end": v(-161.78, 53.53) * mm});
            skLineSegment(sketch, "E823", {"start": v(-161.78, 53.53) * mm, "end": v(-161.63, 53.57) * mm});
            skLineSegment(sketch, "E824", {"start": v(-161.63, 53.57) * mm, "end": v(-161.48, 53.6) * mm});
            skLineSegment(sketch, "E825", {"start": v(-161.48, 53.6) * mm, "end": v(-161.32, 53.62) * mm});
            skLineSegment(sketch, "E826", {"start": v(-161.32, 53.62) * mm, "end": v(-161.16, 53.63) * mm});
            skLineSegment(sketch, "E827", {"start": v(-161.16, 53.63) * mm, "end": v(161.16, 53.62) * mm});
            skLineSegment(sketch, "E828", {"start": v(160.2, -49.7) * mm, "end": v(159.78, -49.91) * mm});
            skLineSegment(sketch, "E829", {"start": v(159.78, -49.91) * mm, "end": v(159.45, -50.24) * mm});
            skLineSegment(sketch, "E830", {"start": v(159.45, -50.24) * mm, "end": v(159.24, -50.66) * mm});
            skLineSegment(sketch, "E831", {"start": v(159.24, -50.66) * mm, "end": v(159.16, -51.13) * mm});
            skLineSegment(sketch, "E832", {"start": v(159.16, -51.13) * mm, "end": v(159.24, -51.59) * mm});
            skLineSegment(sketch, "E833", {"start": v(159.24, -51.59) * mm, "end": v(159.45, -52) * mm});
            skLineSegment(sketch, "E834", {"start": v(159.45, -52) * mm, "end": v(159.78, -52.34) * mm});
            skLineSegment(sketch, "E835", {"start": v(159.78, -52.34) * mm, "end": v(160.2, -52.55) * mm});
            skLineSegment(sketch, "E836", {"start": v(160.2, -52.55) * mm, "end": v(160.66, -52.63) * mm});
            skLineSegment(sketch, "E837", {"start": v(160.66, -52.63) * mm, "end": v(161.13, -52.55) * mm});
            skLineSegment(sketch, "E838", {"start": v(161.13, -52.55) * mm, "end": v(161.54, -52.34) * mm});
            skLineSegment(sketch, "E839", {"start": v(161.54, -52.34) * mm, "end": v(161.88, -52) * mm});
            skLineSegment(sketch, "E840", {"start": v(161.88, -52) * mm, "end": v(162.09, -51.59) * mm});
            skLineSegment(sketch, "E841", {"start": v(162.09, -51.59) * mm, "end": v(162.16, -51.13) * mm});
            skLineSegment(sketch, "E842", {"start": v(162.16, -51.13) * mm, "end": v(162.09, -50.66) * mm});
            skLineSegment(sketch, "E843", {"start": v(162.09, -50.66) * mm, "end": v(161.88, -50.24) * mm});
            skLineSegment(sketch, "E844", {"start": v(161.88, -50.24) * mm, "end": v(161.54, -49.91) * mm});
            skLineSegment(sketch, "E845", {"start": v(161.54, -49.91) * mm, "end": v(161.13, -49.7) * mm});
            skLineSegment(sketch, "E846", {"start": v(161.13, -49.7) * mm, "end": v(160.66, -49.63) * mm});
            skLineSegment(sketch, "E847", {"start": v(160.66, -49.63) * mm, "end": v(160.2, -49.7) * mm});
            skLineSegment(sketch, "E848", {"start": v(53.1, -49.7) * mm, "end": v(52.67, -49.91) * mm});
            skLineSegment(sketch, "E849", {"start": v(52.67, -49.91) * mm, "end": v(52.34, -50.24) * mm});
            skLineSegment(sketch, "E850", {"start": v(52.34, -50.24) * mm, "end": v(52.13, -50.66) * mm});
            skLineSegment(sketch, "E851", {"start": v(52.13, -50.66) * mm, "end": v(52.05, -51.13) * mm});
            skLineSegment(sketch, "E852", {"start": v(52.05, -51.13) * mm, "end": v(52.13, -51.59) * mm});
            skLineSegment(sketch, "E853", {"start": v(52.13, -51.59) * mm, "end": v(52.34, -52) * mm});
            skLineSegment(sketch, "E854", {"start": v(52.34, -52) * mm, "end": v(52.67, -52.34) * mm});
            skLineSegment(sketch, "E855", {"start": v(52.67, -52.34) * mm, "end": v(53.1, -52.55) * mm});
            skLineSegment(sketch, "E856", {"start": v(53.1, -52.55) * mm, "end": v(53.55, -52.63) * mm});
            skLineSegment(sketch, "E857", {"start": v(53.55, -52.63) * mm, "end": v(54.02, -52.55) * mm});
            skLineSegment(sketch, "E858", {"start": v(54.02, -52.55) * mm, "end": v(54.44, -52.34) * mm});
            skLineSegment(sketch, "E859", {"start": v(54.44, -52.34) * mm, "end": v(54.77, -52) * mm});
            skLineSegment(sketch, "E860", {"start": v(54.77, -52) * mm, "end": v(54.98, -51.59) * mm});
            skLineSegment(sketch, "E861", {"start": v(54.98, -51.59) * mm, "end": v(55.05, -51.13) * mm});
            skLineSegment(sketch, "E862", {"start": v(55.05, -51.13) * mm, "end": v(54.98, -50.66) * mm});
            skLineSegment(sketch, "E863", {"start": v(54.98, -50.66) * mm, "end": v(54.77, -50.24) * mm});
            skLineSegment(sketch, "E864", {"start": v(54.77, -50.24) * mm, "end": v(54.44, -49.91) * mm});
            skLineSegment(sketch, "E865", {"start": v(54.44, -49.91) * mm, "end": v(54.02, -49.7) * mm});
            skLineSegment(sketch, "E866", {"start": v(54.02, -49.7) * mm, "end": v(53.55, -49.63) * mm});
            skLineSegment(sketch, "E867", {"start": v(53.55, -49.63) * mm, "end": v(53.1, -49.7) * mm});
            skLineSegment(sketch, "E868", {"start": v(-54.02, -49.7) * mm, "end": v(-54.44, -49.91) * mm});
            skLineSegment(sketch, "E869", {"start": v(-54.44, -49.91) * mm, "end": v(-54.77, -50.24) * mm});
            skLineSegment(sketch, "E870", {"start": v(-54.77, -50.24) * mm, "end": v(-54.98, -50.66) * mm});
            skLineSegment(sketch, "E871", {"start": v(-54.98, -50.66) * mm, "end": v(-55.06, -51.13) * mm});
            skLineSegment(sketch, "E872", {"start": v(-55.06, -51.13) * mm, "end": v(-54.98, -51.59) * mm});
            skLineSegment(sketch, "E873", {"start": v(-54.98, -51.59) * mm, "end": v(-54.77, -52) * mm});
            skLineSegment(sketch, "E874", {"start": v(-54.77, -52) * mm, "end": v(-54.44, -52.34) * mm});
            skLineSegment(sketch, "E875", {"start": v(-54.44, -52.34) * mm, "end": v(-54.02, -52.55) * mm});
            skLineSegment(sketch, "E876", {"start": v(-54.02, -52.55) * mm, "end": v(-53.55, -52.63) * mm});
            skLineSegment(sketch, "E877", {"start": v(-53.55, -52.63) * mm, "end": v(-53.1, -52.55) * mm});
            skLineSegment(sketch, "E878", {"start": v(-53.1, -52.55) * mm, "end": v(-52.67, -52.34) * mm});
            skLineSegment(sketch, "E879", {"start": v(-52.67, -52.34) * mm, "end": v(-52.34, -52) * mm});
            skLineSegment(sketch, "E880", {"start": v(-52.34, -52) * mm, "end": v(-52.13, -51.59) * mm});
            skLineSegment(sketch, "E881", {"start": v(-52.13, -51.59) * mm, "end": v(-52.06, -51.13) * mm});
            skLineSegment(sketch, "E882", {"start": v(-52.06, -51.13) * mm, "end": v(-52.13, -50.66) * mm});
            skLineSegment(sketch, "E883", {"start": v(-52.13, -50.66) * mm, "end": v(-52.34, -50.24) * mm});
            skLineSegment(sketch, "E884", {"start": v(-52.34, -50.24) * mm, "end": v(-52.67, -49.91) * mm});
            skLineSegment(sketch, "E885", {"start": v(-52.67, -49.91) * mm, "end": v(-53.1, -49.7) * mm});
            skLineSegment(sketch, "E886", {"start": v(-53.1, -49.7) * mm, "end": v(-53.55, -49.63) * mm});
            skLineSegment(sketch, "E887", {"start": v(-53.55, -49.63) * mm, "end": v(-54.02, -49.7) * mm});
            skLineSegment(sketch, "E888", {"start": v(-161.13, -49.7) * mm, "end": v(-161.54, -49.91) * mm});
            skLineSegment(sketch, "E889", {"start": v(-161.54, -49.91) * mm, "end": v(-161.88, -50.24) * mm});
            skLineSegment(sketch, "E890", {"start": v(-161.88, -50.24) * mm, "end": v(-162.1, -50.66) * mm});
            skLineSegment(sketch, "E891", {"start": v(-162.1, -50.66) * mm, "end": v(-162.16, -51.13) * mm});
            skLineSegment(sketch, "E892", {"start": v(-162.16, -51.13) * mm, "end": v(-162.1, -51.59) * mm});
            skLineSegment(sketch, "E893", {"start": v(-162.1, -51.59) * mm, "end": v(-161.88, -52) * mm});
            skLineSegment(sketch, "E894", {"start": v(-161.88, -52) * mm, "end": v(-161.54, -52.34) * mm});
            skLineSegment(sketch, "E895", {"start": v(-161.54, -52.34) * mm, "end": v(-161.13, -52.55) * mm});
            skLineSegment(sketch, "E896", {"start": v(-161.13, -52.55) * mm, "end": v(-160.66, -52.63) * mm});
            skLineSegment(sketch, "E897", {"start": v(-160.66, -52.63) * mm, "end": v(-160.2, -52.55) * mm});
            skLineSegment(sketch, "E898", {"start": v(-160.2, -52.55) * mm, "end": v(-159.78, -52.34) * mm});
            skLineSegment(sketch, "E899", {"start": v(-159.78, -52.34) * mm, "end": v(-159.45, -52) * mm});
            skLineSegment(sketch, "E900", {"start": v(-159.45, -52) * mm, "end": v(-159.24, -51.59) * mm});
            skLineSegment(sketch, "E901", {"start": v(-159.24, -51.59) * mm, "end": v(-159.16, -51.13) * mm});
            skLineSegment(sketch, "E902", {"start": v(-159.16, -51.13) * mm, "end": v(-159.24, -50.66) * mm});
            skLineSegment(sketch, "E903", {"start": v(-159.24, -50.66) * mm, "end": v(-159.45, -50.24) * mm});
            skLineSegment(sketch, "E904", {"start": v(-159.45, -50.24) * mm, "end": v(-159.78, -49.91) * mm});
            skLineSegment(sketch, "E905", {"start": v(-159.78, -49.91) * mm, "end": v(-160.2, -49.7) * mm});
            skLineSegment(sketch, "E906", {"start": v(-160.2, -49.7) * mm, "end": v(-160.66, -49.63) * mm});
            skLineSegment(sketch, "E907", {"start": v(-160.66, -49.63) * mm, "end": v(-161.13, -49.7) * mm});
            skLineSegment(sketch, "E908", {"start": v(-37.96, -31.1) * mm, "end": v(-37.96, -32.1) * mm});
            skLineSegment(sketch, "E909", {"start": v(-37.96, -32.1) * mm, "end": v(-38.76, -32.1) * mm});
            skLineSegment(sketch, "E910", {"start": v(-38.76, -32.1) * mm, "end": v(-38.76, -35.2) * mm});
            skLineSegment(sketch, "E911", {"start": v(-38.76, -35.2) * mm, "end": v(-37.96, -35.2) * mm});
            skLineSegment(sketch, "E912", {"start": v(-37.96, -35.2) * mm, "end": v(-37.96, -35.8) * mm});
            skLineSegment(sketch, "E913", {"start": v(-37.96, -35.8) * mm, "end": v(-77.58, -35.8) * mm});
            skLineSegment(sketch, "E914", {"start": v(-77.58, -35.8) * mm, "end": v(-77.58, -32.57) * mm});
            skLineSegment(sketch, "E915", {"start": v(-77.58, -32.57) * mm, "end": v(-84.33, -32.57) * mm});
            skLineSegment(sketch, "E916", {"start": v(-84.33, -32.57) * mm, "end": v(-84.33, -35.8) * mm});
            skLineSegment(sketch, "E917", {"start": v(-84.33, -35.8) * mm, "end": v(-85.16, -35.8) * mm});
            skLineSegment(sketch, "E918", {"start": v(-85.16, -35.8) * mm, "end": v(-85.16, -38.6) * mm});
            skLineSegment(sketch, "E919", {"start": v(-85.16, -38.6) * mm, "end": v(-84.33, -38.6) * mm});
            skLineSegment(sketch, "E920", {"start": v(-84.33, -38.6) * mm, "end": v(-84.33, -44.87) * mm});
            skLineSegment(sketch, "E921", {"start": v(-84.33, -44.87) * mm, "end": v(-82.6, -44.87) * mm});
            skLineSegment(sketch, "E922", {"start": v(-82.6, -44.87) * mm, "end": v(-82.6, -46.07) * mm});
            skLineSegment(sketch, "E923", {"start": v(-82.6, -46.07) * mm, "end": v(-79.3, -46.07) * mm});
            skLineSegment(sketch, "E924", {"start": v(-79.3, -46.07) * mm, "end": v(-79.3, -44.87) * mm});
            skLineSegment(sketch, "E925", {"start": v(-79.3, -44.87) * mm, "end": v(-77.58, -44.87) * mm});
            skLineSegment(sketch, "E926", {"start": v(-77.58, -44.87) * mm, "end": v(-77.58, -40.4) * mm});
            skLineSegment(sketch, "E927", {"start": v(-77.58, -40.4) * mm, "end": v(-37.96, -40.4) * mm});
            skLineSegment(sketch, "E928", {"start": v(-37.96, -40.4) * mm, "end": v(-37.96, -41) * mm});
            skLineSegment(sketch, "E929", {"start": v(-37.96, -41) * mm, "end": v(-38.76, -41) * mm});
            skLineSegment(sketch, "E930", {"start": v(-38.76, -41) * mm, "end": v(-38.76, -44.1) * mm});
            skLineSegment(sketch, "E931", {"start": v(-38.76, -44.1) * mm, "end": v(-37.96, -44.1) * mm});
            skLineSegment(sketch, "E932", {"start": v(-37.96, -44.1) * mm, "end": v(-37.96, -45.1) * mm});
            skLineSegment(sketch, "E933", {"start": v(-37.96, -45.1) * mm, "end": v(-23.96, -45.1) * mm});
            skLineSegment(sketch, "E934", {"start": v(-23.96, -45.1) * mm, "end": v(-23.96, -44.1) * mm});
            skLineSegment(sketch, "E935", {"start": v(-23.96, -44.1) * mm, "end": v(-23.16, -44.1) * mm});
            skLineSegment(sketch, "E936", {"start": v(-23.16, -44.1) * mm, "end": v(-23.16, -41) * mm});
            skLineSegment(sketch, "E937", {"start": v(-23.16, -41) * mm, "end": v(-23.96, -41) * mm});
            skLineSegment(sketch, "E938", {"start": v(-23.96, -41) * mm, "end": v(-23.96, -40.4) * mm});
            skLineSegment(sketch, "E939", {"start": v(-23.96, -40.4) * mm, "end": v(15.67, -40.4) * mm});
            skLineSegment(sketch, "E940", {"start": v(15.67, -40.4) * mm, "end": v(15.67, -44.87) * mm});
            skLineSegment(sketch, "E941", {"start": v(15.67, -44.87) * mm, "end": v(17.4, -44.87) * mm});
            skLineSegment(sketch, "E942", {"start": v(17.4, -44.87) * mm, "end": v(17.4, -46.07) * mm});
            skLineSegment(sketch, "E943", {"start": v(17.4, -46.07) * mm, "end": v(20.7, -46.07) * mm});
            skLineSegment(sketch, "E944", {"start": v(20.7, -46.07) * mm, "end": v(20.7, -44.87) * mm});
            skLineSegment(sketch, "E945", {"start": v(20.7, -44.87) * mm, "end": v(22.42, -44.87) * mm});
            skLineSegment(sketch, "E946", {"start": v(22.42, -44.87) * mm, "end": v(22.42, -38.6) * mm});
            skLineSegment(sketch, "E947", {"start": v(22.42, -38.6) * mm, "end": v(23.24, -38.6) * mm});
            skLineSegment(sketch, "E948", {"start": v(23.24, -38.6) * mm, "end": v(23.24, -35.8) * mm});
            skLineSegment(sketch, "E949", {"start": v(23.24, -35.8) * mm, "end": v(22.42, -35.8) * mm});
            skLineSegment(sketch, "E950", {"start": v(22.42, -35.8) * mm, "end": v(22.42, -32.57) * mm});
            skLineSegment(sketch, "E951", {"start": v(22.42, -32.57) * mm, "end": v(15.67, -32.57) * mm});
            skLineSegment(sketch, "E952", {"start": v(15.67, -32.57) * mm, "end": v(15.67, -35.8) * mm});
            skLineSegment(sketch, "E953", {"start": v(15.67, -35.8) * mm, "end": v(-23.96, -35.8) * mm});
            skLineSegment(sketch, "E954", {"start": v(-23.96, -35.8) * mm, "end": v(-23.96, -35.2) * mm});
            skLineSegment(sketch, "E955", {"start": v(-23.96, -35.2) * mm, "end": v(-23.16, -35.2) * mm});
            skLineSegment(sketch, "E956", {"start": v(-23.16, -35.2) * mm, "end": v(-23.16, -32.1) * mm});
            skLineSegment(sketch, "E957", {"start": v(-23.16, -32.1) * mm, "end": v(-23.96, -32.1) * mm});
            skLineSegment(sketch, "E958", {"start": v(-23.96, -32.1) * mm, "end": v(-23.96, -31.1) * mm});
            skLineSegment(sketch, "E959", {"start": v(-23.96, -31.1) * mm, "end": v(-37.96, -31.1) * mm});
            skLineSegment(sketch, "E960", {"start": v(-154.64, -31.1) * mm, "end": v(-154.64, -32.1) * mm});
            skLineSegment(sketch, "E961", {"start": v(-154.64, -32.1) * mm, "end": v(-155.44, -32.1) * mm});
            skLineSegment(sketch, "E962", {"start": v(-155.44, -32.1) * mm, "end": v(-155.44, -35.2) * mm});
            skLineSegment(sketch, "E963", {"start": v(-155.44, -35.2) * mm, "end": v(-154.64, -35.2) * mm});
            skLineSegment(sketch, "E964", {"start": v(-154.64, -35.2) * mm, "end": v(-154.64, -41) * mm});
            skLineSegment(sketch, "E965", {"start": v(-154.64, -41) * mm, "end": v(-155.44, -41) * mm});
            skLineSegment(sketch, "E966", {"start": v(-155.44, -41) * mm, "end": v(-155.44, -44.1) * mm});
            skLineSegment(sketch, "E967", {"start": v(-155.44, -44.1) * mm, "end": v(-154.64, -44.1) * mm});
            skLineSegment(sketch, "E968", {"start": v(-154.64, -44.1) * mm, "end": v(-154.64, -45.1) * mm});
            skLineSegment(sketch, "E969", {"start": v(-154.64, -45.1) * mm, "end": v(-140.64, -45.1) * mm});
            skLineSegment(sketch, "E970", {"start": v(-140.64, -45.1) * mm, "end": v(-140.64, -44.1) * mm});
            skLineSegment(sketch, "E971", {"start": v(-140.64, -44.1) * mm, "end": v(-139.84, -44.1) * mm});
            skLineSegment(sketch, "E972", {"start": v(-139.84, -44.1) * mm, "end": v(-139.84, -41) * mm});
            skLineSegment(sketch, "E973", {"start": v(-139.84, -41) * mm, "end": v(-140.64, -41) * mm});
            skLineSegment(sketch, "E974", {"start": v(-140.64, -41) * mm, "end": v(-140.64, -35.2) * mm});
            skLineSegment(sketch, "E975", {"start": v(-140.64, -35.2) * mm, "end": v(-139.84, -35.2) * mm});
            skLineSegment(sketch, "E976", {"start": v(-139.84, -35.2) * mm, "end": v(-139.84, -32.1) * mm});
            skLineSegment(sketch, "E977", {"start": v(-139.84, -32.1) * mm, "end": v(-140.64, -32.1) * mm});
            skLineSegment(sketch, "E978", {"start": v(-140.64, -32.1) * mm, "end": v(-140.64, -31.1) * mm});
            skLineSegment(sketch, "E979", {"start": v(-140.64, -31.1) * mm, "end": v(-154.64, -31.1) * mm});
            skLineSegment(sketch, "E980", {"start": v(-133.2, -31.1) * mm, "end": v(-133.2, -32.1) * mm});
            skLineSegment(sketch, "E981", {"start": v(-133.2, -32.1) * mm, "end": v(-134, -32.1) * mm});
            skLineSegment(sketch, "E982", {"start": v(-134, -32.1) * mm, "end": v(-134, -35.2) * mm});
            skLineSegment(sketch, "E983", {"start": v(-134, -35.2) * mm, "end": v(-133.2, -35.2) * mm});
            skLineSegment(sketch, "E984", {"start": v(-133.2, -35.2) * mm, "end": v(-133.2, -41) * mm});
            skLineSegment(sketch, "E985", {"start": v(-133.2, -41) * mm, "end": v(-134, -41) * mm});
            skLineSegment(sketch, "E986", {"start": v(-134, -41) * mm, "end": v(-134, -44.1) * mm});
            skLineSegment(sketch, "E987", {"start": v(-134, -44.1) * mm, "end": v(-133.2, -44.1) * mm});
            skLineSegment(sketch, "E988", {"start": v(-133.2, -44.1) * mm, "end": v(-133.2, -45.1) * mm});
            skLineSegment(sketch, "E989", {"start": v(-133.2, -45.1) * mm, "end": v(-119.2, -45.1) * mm});
            skLineSegment(sketch, "E990", {"start": v(-119.2, -45.1) * mm, "end": v(-119.2, -44.1) * mm});
            skLineSegment(sketch, "E991", {"start": v(-119.2, -44.1) * mm, "end": v(-118.4, -44.1) * mm});
            skLineSegment(sketch, "E992", {"start": v(-118.4, -44.1) * mm, "end": v(-118.4, -41) * mm});
            skLineSegment(sketch, "E993", {"start": v(-118.4, -41) * mm, "end": v(-119.2, -41) * mm});
            skLineSegment(sketch, "E994", {"start": v(-119.2, -41) * mm, "end": v(-119.2, -35.2) * mm});
            skLineSegment(sketch, "E995", {"start": v(-119.2, -35.2) * mm, "end": v(-118.4, -35.2) * mm});
            skLineSegment(sketch, "E996", {"start": v(-118.4, -35.2) * mm, "end": v(-118.4, -32.1) * mm});
            skLineSegment(sketch, "E997", {"start": v(-118.4, -32.1) * mm, "end": v(-119.2, -32.1) * mm});
            skLineSegment(sketch, "E998", {"start": v(-119.2, -32.1) * mm, "end": v(-119.2, -31.1) * mm});
            skLineSegment(sketch, "E999", {"start": v(-119.2, -31.1) * mm, "end": v(-133.2, -31.1) * mm});
            skLineSegment(sketch, "E1000", {"start": v(-109.4, -31.1) * mm, "end": v(-109.4, -32.1) * mm});
            skLineSegment(sketch, "E1001", {"start": v(-109.4, -32.1) * mm, "end": v(-110.2, -32.1) * mm});
            skLineSegment(sketch, "E1002", {"start": v(-110.2, -32.1) * mm, "end": v(-110.2, -35.2) * mm});
            skLineSegment(sketch, "E1003", {"start": v(-110.2, -35.2) * mm, "end": v(-109.4, -35.2) * mm});
            skLineSegment(sketch, "E1004", {"start": v(-109.4, -35.2) * mm, "end": v(-109.4, -41) * mm});
            skLineSegment(sketch, "E1005", {"start": v(-109.4, -41) * mm, "end": v(-110.2, -41) * mm});
            skLineSegment(sketch, "E1006", {"start": v(-110.2, -41) * mm, "end": v(-110.2, -44.1) * mm});
            skLineSegment(sketch, "E1007", {"start": v(-110.2, -44.1) * mm, "end": v(-109.4, -44.1) * mm});
            skLineSegment(sketch, "E1008", {"start": v(-109.4, -44.1) * mm, "end": v(-109.4, -45.1) * mm});
            skLineSegment(sketch, "E1009", {"start": v(-109.4, -45.1) * mm, "end": v(-95.4, -45.1) * mm});
            skLineSegment(sketch, "E1010", {"start": v(-95.4, -45.1) * mm, "end": v(-95.4, -44.1) * mm});
            skLineSegment(sketch, "E1011", {"start": v(-95.4, -44.1) * mm, "end": v(-94.6, -44.1) * mm});
            skLineSegment(sketch, "E1012", {"start": v(-94.6, -44.1) * mm, "end": v(-94.6, -41) * mm});
            skLineSegment(sketch, "E1013", {"start": v(-94.6, -41) * mm, "end": v(-95.4, -41) * mm});
            skLineSegment(sketch, "E1014", {"start": v(-95.4, -41) * mm, "end": v(-95.4, -35.2) * mm});
            skLineSegment(sketch, "E1015", {"start": v(-95.4, -35.2) * mm, "end": v(-94.6, -35.2) * mm});
            skLineSegment(sketch, "E1016", {"start": v(-94.6, -35.2) * mm, "end": v(-94.6, -32.1) * mm});
            skLineSegment(sketch, "E1017", {"start": v(-94.6, -32.1) * mm, "end": v(-95.4, -32.1) * mm});
            skLineSegment(sketch, "E1018", {"start": v(-95.4, -32.1) * mm, "end": v(-95.4, -31.1) * mm});
            skLineSegment(sketch, "E1019", {"start": v(-95.4, -31.1) * mm, "end": v(-109.4, -31.1) * mm});
            skLineSegment(sketch, "E1020", {"start": v(33.48, -31.1) * mm, "end": v(33.48, -32.1) * mm});
            skLineSegment(sketch, "E1021", {"start": v(33.48, -32.1) * mm, "end": v(32.68, -32.1) * mm});
            skLineSegment(sketch, "E1022", {"start": v(32.68, -32.1) * mm, "end": v(32.68, -35.2) * mm});
            skLineSegment(sketch, "E1023", {"start": v(32.68, -35.2) * mm, "end": v(33.48, -35.2) * mm});
            skLineSegment(sketch, "E1024", {"start": v(33.48, -35.2) * mm, "end": v(33.48, -41) * mm});
            skLineSegment(sketch, "E1025", {"start": v(33.48, -41) * mm, "end": v(32.68, -41) * mm});
            skLineSegment(sketch, "E1026", {"start": v(32.68, -41) * mm, "end": v(32.68, -44.1) * mm});
            skLineSegment(sketch, "E1027", {"start": v(32.68, -44.1) * mm, "end": v(33.48, -44.1) * mm});
            skLineSegment(sketch, "E1028", {"start": v(33.48, -44.1) * mm, "end": v(33.48, -45.1) * mm});
            skLineSegment(sketch, "E1029", {"start": v(33.48, -45.1) * mm, "end": v(47.48, -45.1) * mm});
            skLineSegment(sketch, "E1030", {"start": v(47.48, -45.1) * mm, "end": v(47.48, -44.1) * mm});
            skLineSegment(sketch, "E1031", {"start": v(47.48, -44.1) * mm, "end": v(48.28, -44.1) * mm});
            skLineSegment(sketch, "E1032", {"start": v(48.28, -44.1) * mm, "end": v(48.28, -41) * mm});
            skLineSegment(sketch, "E1033", {"start": v(48.28, -41) * mm, "end": v(47.48, -41) * mm});
            skLineSegment(sketch, "E1034", {"start": v(47.48, -41) * mm, "end": v(47.48, -35.2) * mm});
            skLineSegment(sketch, "E1035", {"start": v(47.48, -35.2) * mm, "end": v(48.28, -35.2) * mm});
            skLineSegment(sketch, "E1036", {"start": v(48.28, -35.2) * mm, "end": v(48.28, -32.1) * mm});
            skLineSegment(sketch, "E1037", {"start": v(48.28, -32.1) * mm, "end": v(47.48, -32.1) * mm});
            skLineSegment(sketch, "E1038", {"start": v(47.48, -32.1) * mm, "end": v(47.48, -31.1) * mm});
            skLineSegment(sketch, "E1039", {"start": v(47.48, -31.1) * mm, "end": v(33.48, -31.1) * mm});
            skLineSegment(sketch, "E1040", {"start": v(57.3, -31.1) * mm, "end": v(57.3, -32.1) * mm});
            skLineSegment(sketch, "E1041", {"start": v(57.3, -32.1) * mm, "end": v(56.5, -32.1) * mm});
            skLineSegment(sketch, "E1042", {"start": v(56.5, -32.1) * mm, "end": v(56.5, -35.2) * mm});
            skLineSegment(sketch, "E1043", {"start": v(56.5, -35.2) * mm, "end": v(57.3, -35.2) * mm});
            skLineSegment(sketch, "E1044", {"start": v(57.3, -35.2) * mm, "end": v(57.3, -41) * mm});
            skLineSegment(sketch, "E1045", {"start": v(57.3, -41) * mm, "end": v(56.5, -41) * mm});
            skLineSegment(sketch, "E1046", {"start": v(56.5, -41) * mm, "end": v(56.5, -44.1) * mm});
            skLineSegment(sketch, "E1047", {"start": v(56.5, -44.1) * mm, "end": v(57.3, -44.1) * mm});
            skLineSegment(sketch, "E1048", {"start": v(57.3, -44.1) * mm, "end": v(57.3, -45.1) * mm});
            skLineSegment(sketch, "E1049", {"start": v(57.3, -45.1) * mm, "end": v(71.3, -45.1) * mm});
            skLineSegment(sketch, "E1050", {"start": v(71.3, -45.1) * mm, "end": v(71.3, -44.1) * mm});
            skLineSegment(sketch, "E1051", {"start": v(71.3, -44.1) * mm, "end": v(72.1, -44.1) * mm});
            skLineSegment(sketch, "E1052", {"start": v(72.1, -44.1) * mm, "end": v(72.1, -41) * mm});
            skLineSegment(sketch, "E1053", {"start": v(72.1, -41) * mm, "end": v(71.3, -41) * mm});
            skLineSegment(sketch, "E1054", {"start": v(71.3, -41) * mm, "end": v(71.3, -35.2) * mm});
            skLineSegment(sketch, "E1055", {"start": v(71.3, -35.2) * mm, "end": v(72.1, -35.2) * mm});
            skLineSegment(sketch, "E1056", {"start": v(72.1, -35.2) * mm, "end": v(72.1, -32.1) * mm});
            skLineSegment(sketch, "E1057", {"start": v(72.1, -32.1) * mm, "end": v(71.3, -32.1) * mm});
            skLineSegment(sketch, "E1058", {"start": v(71.3, -32.1) * mm, "end": v(71.3, -31.1) * mm});
            skLineSegment(sketch, "E1059", {"start": v(71.3, -31.1) * mm, "end": v(57.3, -31.1) * mm});
            skLineSegment(sketch, "E1060", {"start": v(102.54, -31.1) * mm, "end": v(102.54, -32.1) * mm});
            skLineSegment(sketch, "E1061", {"start": v(102.54, -32.1) * mm, "end": v(101.74, -32.1) * mm});
            skLineSegment(sketch, "E1062", {"start": v(101.74, -32.1) * mm, "end": v(101.74, -35.2) * mm});
            skLineSegment(sketch, "E1063", {"start": v(101.74, -35.2) * mm, "end": v(102.54, -35.2) * mm});
            skLineSegment(sketch, "E1064", {"start": v(102.54, -35.2) * mm, "end": v(102.54, -41) * mm});
            skLineSegment(sketch, "E1065", {"start": v(102.54, -41) * mm, "end": v(101.74, -41) * mm});
            skLineSegment(sketch, "E1066", {"start": v(101.74, -41) * mm, "end": v(101.74, -44.1) * mm});
            skLineSegment(sketch, "E1067", {"start": v(101.74, -44.1) * mm, "end": v(102.54, -44.1) * mm});
            skLineSegment(sketch, "E1068", {"start": v(102.54, -44.1) * mm, "end": v(102.54, -45.1) * mm});
            skLineSegment(sketch, "E1069", {"start": v(102.54, -45.1) * mm, "end": v(116.54, -45.1) * mm});
            skLineSegment(sketch, "E1070", {"start": v(116.54, -45.1) * mm, "end": v(116.54, -44.1) * mm});
            skLineSegment(sketch, "E1071", {"start": v(116.54, -44.1) * mm, "end": v(117.34, -44.1) * mm});
            skLineSegment(sketch, "E1072", {"start": v(117.34, -44.1) * mm, "end": v(117.34, -41) * mm});
            skLineSegment(sketch, "E1073", {"start": v(117.34, -41) * mm, "end": v(116.54, -41) * mm});
            skLineSegment(sketch, "E1074", {"start": v(116.54, -41) * mm, "end": v(116.54, -35.2) * mm});
            skLineSegment(sketch, "E1075", {"start": v(116.54, -35.2) * mm, "end": v(117.34, -35.2) * mm});
            skLineSegment(sketch, "E1076", {"start": v(117.34, -35.2) * mm, "end": v(117.34, -32.1) * mm});
            skLineSegment(sketch, "E1077", {"start": v(117.34, -32.1) * mm, "end": v(116.54, -32.1) * mm});
            skLineSegment(sketch, "E1078", {"start": v(116.54, -32.1) * mm, "end": v(116.54, -31.1) * mm});
            skLineSegment(sketch, "E1079", {"start": v(116.54, -31.1) * mm, "end": v(102.54, -31.1) * mm});
            skLineSegment(sketch, "E1080", {"start": v(121.59, -31.1) * mm, "end": v(121.59, -32.1) * mm});
            skLineSegment(sketch, "E1081", {"start": v(121.59, -32.1) * mm, "end": v(120.79, -32.1) * mm});
            skLineSegment(sketch, "E1082", {"start": v(120.79, -32.1) * mm, "end": v(120.79, -35.2) * mm});
            skLineSegment(sketch, "E1083", {"start": v(120.79, -35.2) * mm, "end": v(121.59, -35.2) * mm});
            skLineSegment(sketch, "E1084", {"start": v(121.59, -35.2) * mm, "end": v(121.59, -41) * mm});
            skLineSegment(sketch, "E1085", {"start": v(121.59, -41) * mm, "end": v(120.79, -41) * mm});
            skLineSegment(sketch, "E1086", {"start": v(120.79, -41) * mm, "end": v(120.79, -44.1) * mm});
            skLineSegment(sketch, "E1087", {"start": v(120.79, -44.1) * mm, "end": v(121.59, -44.1) * mm});
            skLineSegment(sketch, "E1088", {"start": v(121.59, -44.1) * mm, "end": v(121.59, -45.1) * mm});
            skLineSegment(sketch, "E1089", {"start": v(121.59, -45.1) * mm, "end": v(135.59, -45.1) * mm});
            skLineSegment(sketch, "E1090", {"start": v(135.59, -45.1) * mm, "end": v(135.59, -44.1) * mm});
            skLineSegment(sketch, "E1091", {"start": v(135.59, -44.1) * mm, "end": v(136.39, -44.1) * mm});
            skLineSegment(sketch, "E1092", {"start": v(136.39, -44.1) * mm, "end": v(136.39, -41) * mm});
            skLineSegment(sketch, "E1093", {"start": v(136.39, -41) * mm, "end": v(135.59, -41) * mm});
            skLineSegment(sketch, "E1094", {"start": v(135.59, -41) * mm, "end": v(135.59, -35.2) * mm});
            skLineSegment(sketch, "E1095", {"start": v(135.59, -35.2) * mm, "end": v(136.39, -35.2) * mm});
            skLineSegment(sketch, "E1096", {"start": v(136.39, -35.2) * mm, "end": v(136.39, -32.1) * mm});
            skLineSegment(sketch, "E1097", {"start": v(136.39, -32.1) * mm, "end": v(135.59, -32.1) * mm});
            skLineSegment(sketch, "E1098", {"start": v(135.59, -32.1) * mm, "end": v(135.59, -31.1) * mm});
            skLineSegment(sketch, "E1099", {"start": v(135.59, -31.1) * mm, "end": v(121.59, -31.1) * mm});
            skLineSegment(sketch, "E1100", {"start": v(140.64, -31.1) * mm, "end": v(140.64, -32.1) * mm});
            skLineSegment(sketch, "E1101", {"start": v(140.64, -32.1) * mm, "end": v(139.84, -32.1) * mm});
            skLineSegment(sketch, "E1102", {"start": v(139.84, -32.1) * mm, "end": v(139.84, -35.2) * mm});
            skLineSegment(sketch, "E1103", {"start": v(139.84, -35.2) * mm, "end": v(140.64, -35.2) * mm});
            skLineSegment(sketch, "E1104", {"start": v(140.64, -35.2) * mm, "end": v(140.64, -41) * mm});
            skLineSegment(sketch, "E1105", {"start": v(140.64, -41) * mm, "end": v(139.84, -41) * mm});
            skLineSegment(sketch, "E1106", {"start": v(139.84, -41) * mm, "end": v(139.84, -44.1) * mm});
            skLineSegment(sketch, "E1107", {"start": v(139.84, -44.1) * mm, "end": v(140.64, -44.1) * mm});
            skLineSegment(sketch, "E1108", {"start": v(140.64, -44.1) * mm, "end": v(140.64, -45.1) * mm});
            skLineSegment(sketch, "E1109", {"start": v(140.64, -45.1) * mm, "end": v(154.64, -45.1) * mm});
            skLineSegment(sketch, "E1110", {"start": v(154.64, -45.1) * mm, "end": v(154.64, -44.1) * mm});
            skLineSegment(sketch, "E1111", {"start": v(154.64, -44.1) * mm, "end": v(155.44, -44.1) * mm});
            skLineSegment(sketch, "E1112", {"start": v(155.44, -44.1) * mm, "end": v(155.44, -41) * mm});
            skLineSegment(sketch, "E1113", {"start": v(155.44, -41) * mm, "end": v(154.64, -41) * mm});
            skLineSegment(sketch, "E1114", {"start": v(154.64, -41) * mm, "end": v(154.64, -35.2) * mm});
            skLineSegment(sketch, "E1115", {"start": v(154.64, -35.2) * mm, "end": v(155.44, -35.2) * mm});
            skLineSegment(sketch, "E1116", {"start": v(155.44, -35.2) * mm, "end": v(155.44, -32.1) * mm});
            skLineSegment(sketch, "E1117", {"start": v(155.44, -32.1) * mm, "end": v(154.64, -32.1) * mm});
            skLineSegment(sketch, "E1118", {"start": v(154.64, -32.1) * mm, "end": v(154.64, -31.1) * mm});
            skLineSegment(sketch, "E1119", {"start": v(154.64, -31.1) * mm, "end": v(140.64, -31.1) * mm});
            skLineSegment(sketch, "E1120", {"start": v(-142.73, -12.05) * mm, "end": v(-142.73, -13.05) * mm});
            skLineSegment(sketch, "E1121", {"start": v(-142.73, -13.05) * mm, "end": v(-143.53, -13.05) * mm});
            skLineSegment(sketch, "E1122", {"start": v(-143.53, -13.05) * mm, "end": v(-143.53, -16.15) * mm});
            skLineSegment(sketch, "E1123", {"start": v(-143.53, -16.15) * mm, "end": v(-142.73, -16.15) * mm});
            skLineSegment(sketch, "E1124", {"start": v(-142.73, -16.15) * mm, "end": v(-142.73, -16.75) * mm});
            skLineSegment(sketch, "E1125", {"start": v(-142.73, -16.75) * mm, "end": v(-144.26, -16.75) * mm});
            skLineSegment(sketch, "E1126", {"start": v(-144.26, -16.75) * mm, "end": v(-144.26, -13.52) * mm});
            skLineSegment(sketch, "E1127", {"start": v(-144.26, -13.52) * mm, "end": v(-151, -13.52) * mm});
            skLineSegment(sketch, "E1128", {"start": v(-151, -13.52) * mm, "end": v(-151, -16.75) * mm});
            skLineSegment(sketch, "E1129", {"start": v(-151, -16.75) * mm, "end": v(-151.83, -16.75) * mm});
            skLineSegment(sketch, "E1130", {"start": v(-151.83, -16.75) * mm, "end": v(-151.83, -19.55) * mm});
            skLineSegment(sketch, "E1131", {"start": v(-151.83, -19.55) * mm, "end": v(-151, -19.55) * mm});
            skLineSegment(sketch, "E1132", {"start": v(-151, -19.55) * mm, "end": v(-151, -25.82) * mm});
            skLineSegment(sketch, "E1133", {"start": v(-151, -25.82) * mm, "end": v(-149.28, -25.82) * mm});
            skLineSegment(sketch, "E1134", {"start": v(-149.28, -25.82) * mm, "end": v(-149.28, -27.02) * mm});
            skLineSegment(sketch, "E1135", {"start": v(-149.28, -27.02) * mm, "end": v(-145.98, -27.02) * mm});
            skLineSegment(sketch, "E1136", {"start": v(-145.98, -27.02) * mm, "end": v(-145.98, -25.82) * mm});
            skLineSegment(sketch, "E1137", {"start": v(-145.98, -25.82) * mm, "end": v(-144.26, -25.82) * mm});
            skLineSegment(sketch, "E1138", {"start": v(-144.26, -25.82) * mm, "end": v(-144.26, -21.35) * mm});
            skLineSegment(sketch, "E1139", {"start": v(-144.26, -21.35) * mm, "end": v(-142.73, -21.35) * mm});
            skLineSegment(sketch, "E1140", {"start": v(-142.73, -21.35) * mm, "end": v(-142.73, -21.95) * mm});
            skLineSegment(sketch, "E1141", {"start": v(-142.73, -21.95) * mm, "end": v(-143.53, -21.95) * mm});
            skLineSegment(sketch, "E1142", {"start": v(-143.53, -21.95) * mm, "end": v(-143.53, -25.05) * mm});
            skLineSegment(sketch, "E1143", {"start": v(-143.53, -25.05) * mm, "end": v(-142.73, -25.05) * mm});
            skLineSegment(sketch, "E1144", {"start": v(-142.73, -25.05) * mm, "end": v(-142.73, -26.05) * mm});
            skLineSegment(sketch, "E1145", {"start": v(-142.73, -26.05) * mm, "end": v(-128.73, -26.05) * mm});
            skLineSegment(sketch, "E1146", {"start": v(-128.73, -26.05) * mm, "end": v(-128.73, -25.05) * mm});
            skLineSegment(sketch, "E1147", {"start": v(-128.73, -25.05) * mm, "end": v(-127.93, -25.05) * mm});
            skLineSegment(sketch, "E1148", {"start": v(-127.93, -25.05) * mm, "end": v(-127.93, -21.95) * mm});
            skLineSegment(sketch, "E1149", {"start": v(-127.93, -21.95) * mm, "end": v(-128.73, -21.95) * mm});
            skLineSegment(sketch, "E1150", {"start": v(-128.73, -21.95) * mm, "end": v(-128.73, -21.35) * mm});
            skLineSegment(sketch, "E1151", {"start": v(-128.73, -21.35) * mm, "end": v(-127.2, -21.35) * mm});
            skLineSegment(sketch, "E1152", {"start": v(-127.2, -21.35) * mm, "end": v(-127.2, -25.82) * mm});
            skLineSegment(sketch, "E1153", {"start": v(-127.2, -25.82) * mm, "end": v(-125.48, -25.82) * mm});
            skLineSegment(sketch, "E1154", {"start": v(-125.48, -25.82) * mm, "end": v(-125.48, -27.02) * mm});
            skLineSegment(sketch, "E1155", {"start": v(-125.48, -27.02) * mm, "end": v(-122.18, -27.02) * mm});
            skLineSegment(sketch, "E1156", {"start": v(-122.18, -27.02) * mm, "end": v(-122.18, -25.82) * mm});
            skLineSegment(sketch, "E1157", {"start": v(-122.18, -25.82) * mm, "end": v(-120.46, -25.82) * mm});
            skLineSegment(sketch, "E1158", {"start": v(-120.46, -25.82) * mm, "end": v(-120.46, -19.55) * mm});
            skLineSegment(sketch, "E1159", {"start": v(-120.46, -19.55) * mm, "end": v(-119.63, -19.55) * mm});
            skLineSegment(sketch, "E1160", {"start": v(-119.63, -19.55) * mm, "end": v(-119.63, -16.75) * mm});
            skLineSegment(sketch, "E1161", {"start": v(-119.63, -16.75) * mm, "end": v(-120.46, -16.75) * mm});
            skLineSegment(sketch, "E1162", {"start": v(-120.46, -16.75) * mm, "end": v(-120.46, -13.52) * mm});
            skLineSegment(sketch, "E1163", {"start": v(-120.46, -13.52) * mm, "end": v(-127.2, -13.52) * mm});
            skLineSegment(sketch, "E1164", {"start": v(-127.2, -13.52) * mm, "end": v(-127.2, -16.75) * mm});
            skLineSegment(sketch, "E1165", {"start": v(-127.2, -16.75) * mm, "end": v(-128.73, -16.75) * mm});
            skLineSegment(sketch, "E1166", {"start": v(-128.73, -16.75) * mm, "end": v(-128.73, -16.15) * mm});
            skLineSegment(sketch, "E1167", {"start": v(-128.73, -16.15) * mm, "end": v(-127.93, -16.15) * mm});
            skLineSegment(sketch, "E1168", {"start": v(-127.93, -16.15) * mm, "end": v(-127.93, -13.05) * mm});
            skLineSegment(sketch, "E1169", {"start": v(-127.93, -13.05) * mm, "end": v(-128.73, -13.05) * mm});
            skLineSegment(sketch, "E1170", {"start": v(-128.73, -13.05) * mm, "end": v(-128.73, -12.05) * mm});
            skLineSegment(sketch, "E1171", {"start": v(-128.73, -12.05) * mm, "end": v(-142.73, -12.05) * mm});
            skLineSegment(sketch, "E1172", {"start": v(90.63, -12.05) * mm, "end": v(90.63, -13.05) * mm});
            skLineSegment(sketch, "E1173", {"start": v(90.63, -13.05) * mm, "end": v(89.83, -13.05) * mm});
            skLineSegment(sketch, "E1174", {"start": v(89.83, -13.05) * mm, "end": v(89.83, -16.15) * mm});
            skLineSegment(sketch, "E1175", {"start": v(89.83, -16.15) * mm, "end": v(90.63, -16.15) * mm});
            skLineSegment(sketch, "E1176", {"start": v(90.63, -16.15) * mm, "end": v(90.63, -16.75) * mm});
            skLineSegment(sketch, "E1177", {"start": v(90.63, -16.75) * mm, "end": v(89.1, -16.75) * mm});
            skLineSegment(sketch, "E1178", {"start": v(89.1, -16.75) * mm, "end": v(89.1, -13.52) * mm});
            skLineSegment(sketch, "E1179", {"start": v(89.1, -13.52) * mm, "end": v(82.36, -13.52) * mm});
            skLineSegment(sketch, "E1180", {"start": v(82.36, -13.52) * mm, "end": v(82.36, -16.75) * mm});
            skLineSegment(sketch, "E1181", {"start": v(82.36, -16.75) * mm, "end": v(81.53, -16.75) * mm});
            skLineSegment(sketch, "E1182", {"start": v(81.53, -16.75) * mm, "end": v(81.53, -19.55) * mm});
            skLineSegment(sketch, "E1183", {"start": v(81.53, -19.55) * mm, "end": v(82.36, -19.55) * mm});
            skLineSegment(sketch, "E1184", {"start": v(82.36, -19.55) * mm, "end": v(82.36, -25.82) * mm});
            skLineSegment(sketch, "E1185", {"start": v(82.36, -25.82) * mm, "end": v(84.08, -25.82) * mm});
            skLineSegment(sketch, "E1186", {"start": v(84.08, -25.82) * mm, "end": v(84.08, -27.02) * mm});
            skLineSegment(sketch, "E1187", {"start": v(84.08, -27.02) * mm, "end": v(87.38, -27.02) * mm});
            skLineSegment(sketch, "E1188", {"start": v(87.38, -27.02) * mm, "end": v(87.38, -25.82) * mm});
            skLineSegment(sketch, "E1189", {"start": v(87.38, -25.82) * mm, "end": v(89.1, -25.82) * mm});
            skLineSegment(sketch, "E1190", {"start": v(89.1, -25.82) * mm, "end": v(89.1, -21.35) * mm});
            skLineSegment(sketch, "E1191", {"start": v(89.1, -21.35) * mm, "end": v(90.63, -21.35) * mm});
            skLineSegment(sketch, "E1192", {"start": v(90.63, -21.35) * mm, "end": v(90.63, -21.95) * mm});
            skLineSegment(sketch, "E1193", {"start": v(90.63, -21.95) * mm, "end": v(89.83, -21.95) * mm});
            skLineSegment(sketch, "E1194", {"start": v(89.83, -21.95) * mm, "end": v(89.83, -25.05) * mm});
            skLineSegment(sketch, "E1195", {"start": v(89.83, -25.05) * mm, "end": v(90.63, -25.05) * mm});
            skLineSegment(sketch, "E1196", {"start": v(90.63, -25.05) * mm, "end": v(90.63, -26.05) * mm});
            skLineSegment(sketch, "E1197", {"start": v(90.63, -26.05) * mm, "end": v(104.63, -26.05) * mm});
            skLineSegment(sketch, "E1198", {"start": v(104.63, -26.05) * mm, "end": v(104.63, -25.05) * mm});
            skLineSegment(sketch, "E1199", {"start": v(104.63, -25.05) * mm, "end": v(105.43, -25.05) * mm});
            skLineSegment(sketch, "E1200", {"start": v(105.43, -25.05) * mm, "end": v(105.43, -21.95) * mm});
            skLineSegment(sketch, "E1201", {"start": v(105.43, -21.95) * mm, "end": v(104.63, -21.95) * mm});
            skLineSegment(sketch, "E1202", {"start": v(104.63, -21.95) * mm, "end": v(104.63, -21.35) * mm});
            skLineSegment(sketch, "E1203", {"start": v(104.63, -21.35) * mm, "end": v(106.16, -21.35) * mm});
            skLineSegment(sketch, "E1204", {"start": v(106.16, -21.35) * mm, "end": v(106.16, -25.82) * mm});
            skLineSegment(sketch, "E1205", {"start": v(106.16, -25.82) * mm, "end": v(107.88, -25.82) * mm});
            skLineSegment(sketch, "E1206", {"start": v(107.88, -25.82) * mm, "end": v(107.88, -27.02) * mm});
            skLineSegment(sketch, "E1207", {"start": v(107.88, -27.02) * mm, "end": v(111.18, -27.02) * mm});
            skLineSegment(sketch, "E1208", {"start": v(111.18, -27.02) * mm, "end": v(111.18, -25.82) * mm});
            skLineSegment(sketch, "E1209", {"start": v(111.18, -25.82) * mm, "end": v(112.9, -25.82) * mm});
            skLineSegment(sketch, "E1210", {"start": v(112.9, -25.82) * mm, "end": v(112.9, -19.55) * mm});
            skLineSegment(sketch, "E1211", {"start": v(112.9, -19.55) * mm, "end": v(113.73, -19.55) * mm});
            skLineSegment(sketch, "E1212", {"start": v(113.73, -19.55) * mm, "end": v(113.73, -16.75) * mm});
            skLineSegment(sketch, "E1213", {"start": v(113.73, -16.75) * mm, "end": v(112.9, -16.75) * mm});
            skLineSegment(sketch, "E1214", {"start": v(112.9, -16.75) * mm, "end": v(112.9, -13.52) * mm});
            skLineSegment(sketch, "E1215", {"start": v(112.9, -13.52) * mm, "end": v(106.16, -13.52) * mm});
            skLineSegment(sketch, "E1216", {"start": v(106.16, -13.52) * mm, "end": v(106.16, -16.75) * mm});
            skLineSegment(sketch, "E1217", {"start": v(106.16, -16.75) * mm, "end": v(104.63, -16.75) * mm});
            skLineSegment(sketch, "E1218", {"start": v(104.63, -16.75) * mm, "end": v(104.63, -16.15) * mm});
            skLineSegment(sketch, "E1219", {"start": v(104.63, -16.15) * mm, "end": v(105.43, -16.15) * mm});
            skLineSegment(sketch, "E1220", {"start": v(105.43, -16.15) * mm, "end": v(105.43, -13.05) * mm});
            skLineSegment(sketch, "E1221", {"start": v(105.43, -13.05) * mm, "end": v(104.63, -13.05) * mm});
            skLineSegment(sketch, "E1222", {"start": v(104.63, -13.05) * mm, "end": v(104.63, -12.05) * mm});
            skLineSegment(sketch, "E1223", {"start": v(104.63, -12.05) * mm, "end": v(90.63, -12.05) * mm});
            skLineSegment(sketch, "E1224", {"start": v(-111.78, -12.05) * mm, "end": v(-111.78, -13.05) * mm});
            skLineSegment(sketch, "E1225", {"start": v(-111.78, -13.05) * mm, "end": v(-112.58, -13.05) * mm});
            skLineSegment(sketch, "E1226", {"start": v(-112.58, -13.05) * mm, "end": v(-112.58, -16.15) * mm});
            skLineSegment(sketch, "E1227", {"start": v(-112.58, -16.15) * mm, "end": v(-111.78, -16.15) * mm});
            skLineSegment(sketch, "E1228", {"start": v(-111.78, -16.15) * mm, "end": v(-111.78, -21.95) * mm});
            skLineSegment(sketch, "E1229", {"start": v(-111.78, -21.95) * mm, "end": v(-112.58, -21.95) * mm});
            skLineSegment(sketch, "E1230", {"start": v(-112.58, -21.95) * mm, "end": v(-112.58, -25.05) * mm});
            skLineSegment(sketch, "E1231", {"start": v(-112.58, -25.05) * mm, "end": v(-111.78, -25.05) * mm});
            skLineSegment(sketch, "E1232", {"start": v(-111.78, -25.05) * mm, "end": v(-111.78, -26.05) * mm});
            skLineSegment(sketch, "E1233", {"start": v(-111.78, -26.05) * mm, "end": v(-97.78, -26.05) * mm});
            skLineSegment(sketch, "E1234", {"start": v(-97.78, -26.05) * mm, "end": v(-97.78, -25.05) * mm});
            skLineSegment(sketch, "E1235", {"start": v(-97.78, -25.05) * mm, "end": v(-96.97, -25.05) * mm});
            skLineSegment(sketch, "E1236", {"start": v(-96.97, -25.05) * mm, "end": v(-96.97, -21.95) * mm});
            skLineSegment(sketch, "E1237", {"start": v(-96.97, -21.95) * mm, "end": v(-97.78, -21.95) * mm});
            skLineSegment(sketch, "E1238", {"start": v(-97.78, -21.95) * mm, "end": v(-97.78, -16.15) * mm});
            skLineSegment(sketch, "E1239", {"start": v(-97.78, -16.15) * mm, "end": v(-96.97, -16.15) * mm});
            skLineSegment(sketch, "E1240", {"start": v(-96.97, -16.15) * mm, "end": v(-96.97, -13.05) * mm});
            skLineSegment(sketch, "E1241", {"start": v(-96.97, -13.05) * mm, "end": v(-97.78, -13.05) * mm});
            skLineSegment(sketch, "E1242", {"start": v(-97.78, -13.05) * mm, "end": v(-97.78, -12.05) * mm});
            skLineSegment(sketch, "E1243", {"start": v(-97.78, -12.05) * mm, "end": v(-111.78, -12.05) * mm});
            skLineSegment(sketch, "E1244", {"start": v(-92.73, -12.05) * mm, "end": v(-92.73, -13.05) * mm});
            skLineSegment(sketch, "E1245", {"start": v(-92.73, -13.05) * mm, "end": v(-93.53, -13.05) * mm});
            skLineSegment(sketch, "E1246", {"start": v(-93.53, -13.05) * mm, "end": v(-93.53, -16.15) * mm});
            skLineSegment(sketch, "E1247", {"start": v(-93.53, -16.15) * mm, "end": v(-92.73, -16.15) * mm});
            skLineSegment(sketch, "E1248", {"start": v(-92.73, -16.15) * mm, "end": v(-92.73, -21.95) * mm});
            skLineSegment(sketch, "E1249", {"start": v(-92.73, -21.95) * mm, "end": v(-93.53, -21.95) * mm});
            skLineSegment(sketch, "E1250", {"start": v(-93.53, -21.95) * mm, "end": v(-93.53, -25.05) * mm});
            skLineSegment(sketch, "E1251", {"start": v(-93.53, -25.05) * mm, "end": v(-92.73, -25.05) * mm});
            skLineSegment(sketch, "E1252", {"start": v(-92.73, -25.05) * mm, "end": v(-92.73, -26.05) * mm});
            skLineSegment(sketch, "E1253", {"start": v(-92.73, -26.05) * mm, "end": v(-78.73, -26.05) * mm});
            skLineSegment(sketch, "E1254", {"start": v(-78.73, -26.05) * mm, "end": v(-78.73, -25.05) * mm});
            skLineSegment(sketch, "E1255", {"start": v(-78.73, -25.05) * mm, "end": v(-77.92, -25.05) * mm});
            skLineSegment(sketch, "E1256", {"start": v(-77.92, -25.05) * mm, "end": v(-77.92, -21.95) * mm});
            skLineSegment(sketch, "E1257", {"start": v(-77.92, -21.95) * mm, "end": v(-78.73, -21.95) * mm});
            skLineSegment(sketch, "E1258", {"start": v(-78.73, -21.95) * mm, "end": v(-78.73, -16.15) * mm});
            skLineSegment(sketch, "E1259", {"start": v(-78.73, -16.15) * mm, "end": v(-77.92, -16.15) * mm});
            skLineSegment(sketch, "E1260", {"start": v(-77.92, -16.15) * mm, "end": v(-77.92, -13.05) * mm});
            skLineSegment(sketch, "E1261", {"start": v(-77.92, -13.05) * mm, "end": v(-78.73, -13.05) * mm});
            skLineSegment(sketch, "E1262", {"start": v(-78.73, -13.05) * mm, "end": v(-78.73, -12.05) * mm});
            skLineSegment(sketch, "E1263", {"start": v(-78.73, -12.05) * mm, "end": v(-92.73, -12.05) * mm});
            skLineSegment(sketch, "E1264", {"start": v(-73.68, -12.05) * mm, "end": v(-73.68, -13.05) * mm});
            skLineSegment(sketch, "E1265", {"start": v(-73.68, -13.05) * mm, "end": v(-74.48, -13.05) * mm});
            skLineSegment(sketch, "E1266", {"start": v(-74.48, -13.05) * mm, "end": v(-74.48, -16.15) * mm});
            skLineSegment(sketch, "E1267", {"start": v(-74.48, -16.15) * mm, "end": v(-73.68, -16.15) * mm});
            skLineSegment(sketch, "E1268", {"start": v(-73.68, -16.15) * mm, "end": v(-73.68, -21.95) * mm});
            skLineSegment(sketch, "E1269", {"start": v(-73.68, -21.95) * mm, "end": v(-74.48, -21.95) * mm});
            skLineSegment(sketch, "E1270", {"start": v(-74.48, -21.95) * mm, "end": v(-74.48, -25.05) * mm});
            skLineSegment(sketch, "E1271", {"start": v(-74.48, -25.05) * mm, "end": v(-73.68, -25.05) * mm});
            skLineSegment(sketch, "E1272", {"start": v(-73.68, -25.05) * mm, "end": v(-73.68, -26.05) * mm});
            skLineSegment(sketch, "E1273", {"start": v(-73.68, -26.05) * mm, "end": v(-59.68, -26.05) * mm});
            skLineSegment(sketch, "E1274", {"start": v(-59.68, -26.05) * mm, "end": v(-59.68, -25.05) * mm});
            skLineSegment(sketch, "E1275", {"start": v(-59.68, -25.05) * mm, "end": v(-58.88, -25.05) * mm});
            skLineSegment(sketch, "E1276", {"start": v(-58.88, -25.05) * mm, "end": v(-58.88, -21.95) * mm});
            skLineSegment(sketch, "E1277", {"start": v(-58.88, -21.95) * mm, "end": v(-59.68, -21.95) * mm});
            skLineSegment(sketch, "E1278", {"start": v(-59.68, -21.95) * mm, "end": v(-59.68, -16.15) * mm});
            skLineSegment(sketch, "E1279", {"start": v(-59.68, -16.15) * mm, "end": v(-58.88, -16.15) * mm});
            skLineSegment(sketch, "E1280", {"start": v(-58.88, -16.15) * mm, "end": v(-58.88, -13.05) * mm});
            skLineSegment(sketch, "E1281", {"start": v(-58.88, -13.05) * mm, "end": v(-59.68, -13.05) * mm});
            skLineSegment(sketch, "E1282", {"start": v(-59.68, -13.05) * mm, "end": v(-59.68, -12.05) * mm});
            skLineSegment(sketch, "E1283", {"start": v(-59.68, -12.05) * mm, "end": v(-73.68, -12.05) * mm});
            skLineSegment(sketch, "E1284", {"start": v(-54.63, -12.05) * mm, "end": v(-54.63, -13.05) * mm});
            skLineSegment(sketch, "E1285", {"start": v(-54.63, -13.05) * mm, "end": v(-55.43, -13.05) * mm});
            skLineSegment(sketch, "E1286", {"start": v(-55.43, -13.05) * mm, "end": v(-55.43, -16.15) * mm});
            skLineSegment(sketch, "E1287", {"start": v(-55.43, -16.15) * mm, "end": v(-54.63, -16.15) * mm});
            skLineSegment(sketch, "E1288", {"start": v(-54.63, -16.15) * mm, "end": v(-54.63, -21.95) * mm});
            skLineSegment(sketch, "E1289", {"start": v(-54.63, -21.95) * mm, "end": v(-55.43, -21.95) * mm});
            skLineSegment(sketch, "E1290", {"start": v(-55.43, -21.95) * mm, "end": v(-55.43, -25.05) * mm});
            skLineSegment(sketch, "E1291", {"start": v(-55.43, -25.05) * mm, "end": v(-54.63, -25.05) * mm});
            skLineSegment(sketch, "E1292", {"start": v(-54.63, -25.05) * mm, "end": v(-54.63, -26.05) * mm});
            skLineSegment(sketch, "E1293", {"start": v(-54.63, -26.05) * mm, "end": v(-40.63, -26.05) * mm});
            skLineSegment(sketch, "E1294", {"start": v(-40.63, -26.05) * mm, "end": v(-40.63, -25.05) * mm});
            skLineSegment(sketch, "E1295", {"start": v(-40.63, -25.05) * mm, "end": v(-39.83, -25.05) * mm});
            skLineSegment(sketch, "E1296", {"start": v(-39.83, -25.05) * mm, "end": v(-39.83, -21.95) * mm});
            skLineSegment(sketch, "E1297", {"start": v(-39.83, -21.95) * mm, "end": v(-40.63, -21.95) * mm});
            skLineSegment(sketch, "E1298", {"start": v(-40.63, -21.95) * mm, "end": v(-40.63, -16.15) * mm});
            skLineSegment(sketch, "E1299", {"start": v(-40.63, -16.15) * mm, "end": v(-39.83, -16.15) * mm});
            skLineSegment(sketch, "E1300", {"start": v(-39.83, -16.15) * mm, "end": v(-39.83, -13.05) * mm});
            skLineSegment(sketch, "E1301", {"start": v(-39.83, -13.05) * mm, "end": v(-40.63, -13.05) * mm});
            skLineSegment(sketch, "E1302", {"start": v(-40.63, -13.05) * mm, "end": v(-40.63, -12.05) * mm});
            skLineSegment(sketch, "E1303", {"start": v(-40.63, -12.05) * mm, "end": v(-54.63, -12.05) * mm});
            skLineSegment(sketch, "E1304", {"start": v(-35.58, -12.05) * mm, "end": v(-35.58, -13.05) * mm});
            skLineSegment(sketch, "E1305", {"start": v(-35.58, -13.05) * mm, "end": v(-36.38, -13.05) * mm});
            skLineSegment(sketch, "E1306", {"start": v(-36.38, -13.05) * mm, "end": v(-36.38, -16.15) * mm});
            skLineSegment(sketch, "E1307", {"start": v(-36.38, -16.15) * mm, "end": v(-35.58, -16.15) * mm});
            skLineSegment(sketch, "E1308", {"start": v(-35.58, -16.15) * mm, "end": v(-35.58, -21.95) * mm});
            skLineSegment(sketch, "E1309", {"start": v(-35.58, -21.95) * mm, "end": v(-36.38, -21.95) * mm});
            skLineSegment(sketch, "E1310", {"start": v(-36.38, -21.95) * mm, "end": v(-36.38, -25.05) * mm});
            skLineSegment(sketch, "E1311", {"start": v(-36.38, -25.05) * mm, "end": v(-35.58, -25.05) * mm});
            skLineSegment(sketch, "E1312", {"start": v(-35.58, -25.05) * mm, "end": v(-35.58, -26.05) * mm});
            skLineSegment(sketch, "E1313", {"start": v(-35.58, -26.05) * mm, "end": v(-21.58, -26.05) * mm});
            skLineSegment(sketch, "E1314", {"start": v(-21.58, -26.05) * mm, "end": v(-21.58, -25.05) * mm});
            skLineSegment(sketch, "E1315", {"start": v(-21.58, -25.05) * mm, "end": v(-20.78, -25.05) * mm});
            skLineSegment(sketch, "E1316", {"start": v(-20.78, -25.05) * mm, "end": v(-20.78, -21.95) * mm});
            skLineSegment(sketch, "E1317", {"start": v(-20.78, -21.95) * mm, "end": v(-21.58, -21.95) * mm});
            skLineSegment(sketch, "E1318", {"start": v(-21.58, -21.95) * mm, "end": v(-21.58, -16.15) * mm});
            skLineSegment(sketch, "E1319", {"start": v(-21.58, -16.15) * mm, "end": v(-20.78, -16.15) * mm});
            skLineSegment(sketch, "E1320", {"start": v(-20.78, -16.15) * mm, "end": v(-20.78, -13.05) * mm});
            skLineSegment(sketch, "E1321", {"start": v(-20.78, -13.05) * mm, "end": v(-21.58, -13.05) * mm});
            skLineSegment(sketch, "E1322", {"start": v(-21.58, -13.05) * mm, "end": v(-21.58, -12.05) * mm});
            skLineSegment(sketch, "E1323", {"start": v(-21.58, -12.05) * mm, "end": v(-35.58, -12.05) * mm});
            skLineSegment(sketch, "E1324", {"start": v(-16.53, -12.05) * mm, "end": v(-16.53, -13.05) * mm});
            skLineSegment(sketch, "E1325", {"start": v(-16.53, -13.05) * mm, "end": v(-17.33, -13.05) * mm});
            skLineSegment(sketch, "E1326", {"start": v(-17.33, -13.05) * mm, "end": v(-17.33, -16.15) * mm});
            skLineSegment(sketch, "E1327", {"start": v(-17.33, -16.15) * mm, "end": v(-16.53, -16.15) * mm});
            skLineSegment(sketch, "E1328", {"start": v(-16.53, -16.15) * mm, "end": v(-16.53, -21.95) * mm});
            skLineSegment(sketch, "E1329", {"start": v(-16.53, -21.95) * mm, "end": v(-17.33, -21.95) * mm});
            skLineSegment(sketch, "E1330", {"start": v(-17.33, -21.95) * mm, "end": v(-17.33, -25.05) * mm});
            skLineSegment(sketch, "E1331", {"start": v(-17.33, -25.05) * mm, "end": v(-16.53, -25.05) * mm});
            skLineSegment(sketch, "E1332", {"start": v(-16.53, -25.05) * mm, "end": v(-16.53, -26.05) * mm});
            skLineSegment(sketch, "E1333", {"start": v(-16.53, -26.05) * mm, "end": v(-2.53, -26.05) * mm});
            skLineSegment(sketch, "E1334", {"start": v(-2.53, -26.05) * mm, "end": v(-2.53, -25.05) * mm});
            skLineSegment(sketch, "E1335", {"start": v(-2.53, -25.05) * mm, "end": v(-1.73, -25.05) * mm});
            skLineSegment(sketch, "E1336", {"start": v(-1.73, -25.05) * mm, "end": v(-1.73, -21.95) * mm});
            skLineSegment(sketch, "E1337", {"start": v(-1.73, -21.95) * mm, "end": v(-2.53, -21.95) * mm});
            skLineSegment(sketch, "E1338", {"start": v(-2.53, -21.95) * mm, "end": v(-2.53, -16.15) * mm});
            skLineSegment(sketch, "E1339", {"start": v(-2.53, -16.15) * mm, "end": v(-1.73, -16.15) * mm});
            skLineSegment(sketch, "E1340", {"start": v(-1.73, -16.15) * mm, "end": v(-1.73, -13.05) * mm});
            skLineSegment(sketch, "E1341", {"start": v(-1.73, -13.05) * mm, "end": v(-2.53, -13.05) * mm});
            skLineSegment(sketch, "E1342", {"start": v(-2.53, -13.05) * mm, "end": v(-2.53, -12.05) * mm});
            skLineSegment(sketch, "E1343", {"start": v(-2.53, -12.05) * mm, "end": v(-16.53, -12.05) * mm});
            skLineSegment(sketch, "E1344", {"start": v(2.52, -12.05) * mm, "end": v(2.52, -13.05) * mm});
            skLineSegment(sketch, "E1345", {"start": v(2.52, -13.05) * mm, "end": v(1.72, -13.05) * mm});
            skLineSegment(sketch, "E1346", {"start": v(1.72, -13.05) * mm, "end": v(1.72, -16.15) * mm});
            skLineSegment(sketch, "E1347", {"start": v(1.72, -16.15) * mm, "end": v(2.52, -16.15) * mm});
            skLineSegment(sketch, "E1348", {"start": v(2.52, -16.15) * mm, "end": v(2.52, -21.95) * mm});
            skLineSegment(sketch, "E1349", {"start": v(2.52, -21.95) * mm, "end": v(1.72, -21.95) * mm});
            skLineSegment(sketch, "E1350", {"start": v(1.72, -21.95) * mm, "end": v(1.72, -25.05) * mm});
            skLineSegment(sketch, "E1351", {"start": v(1.72, -25.05) * mm, "end": v(2.52, -25.05) * mm});
            skLineSegment(sketch, "E1352", {"start": v(2.52, -25.05) * mm, "end": v(2.52, -26.05) * mm});
            skLineSegment(sketch, "E1353", {"start": v(2.52, -26.05) * mm, "end": v(16.52, -26.05) * mm});
            skLineSegment(sketch, "E1354", {"start": v(16.52, -26.05) * mm, "end": v(16.52, -25.05) * mm});
            skLineSegment(sketch, "E1355", {"start": v(16.52, -25.05) * mm, "end": v(17.32, -25.05) * mm});
            skLineSegment(sketch, "E1356", {"start": v(17.32, -25.05) * mm, "end": v(17.32, -21.95) * mm});
            skLineSegment(sketch, "E1357", {"start": v(17.32, -21.95) * mm, "end": v(16.52, -21.95) * mm});
            skLineSegment(sketch, "E1358", {"start": v(16.52, -21.95) * mm, "end": v(16.52, -16.15) * mm});
            skLineSegment(sketch, "E1359", {"start": v(16.52, -16.15) * mm, "end": v(17.32, -16.15) * mm});
            skLineSegment(sketch, "E1360", {"start": v(17.32, -16.15) * mm, "end": v(17.32, -13.05) * mm});
            skLineSegment(sketch, "E1361", {"start": v(17.32, -13.05) * mm, "end": v(16.52, -13.05) * mm});
            skLineSegment(sketch, "E1362", {"start": v(16.52, -13.05) * mm, "end": v(16.52, -12.05) * mm});
            skLineSegment(sketch, "E1363", {"start": v(16.52, -12.05) * mm, "end": v(2.52, -12.05) * mm});
            skLineSegment(sketch, "E1364", {"start": v(21.57, -12.05) * mm, "end": v(21.57, -13.05) * mm});
            skLineSegment(sketch, "E1365", {"start": v(21.57, -13.05) * mm, "end": v(20.77, -13.05) * mm});
            skLineSegment(sketch, "E1366", {"start": v(20.77, -13.05) * mm, "end": v(20.77, -16.15) * mm});
            skLineSegment(sketch, "E1367", {"start": v(20.77, -16.15) * mm, "end": v(21.57, -16.15) * mm});
            skLineSegment(sketch, "E1368", {"start": v(21.57, -16.15) * mm, "end": v(21.57, -21.95) * mm});
            skLineSegment(sketch, "E1369", {"start": v(21.57, -21.95) * mm, "end": v(20.77, -21.95) * mm});
            skLineSegment(sketch, "E1370", {"start": v(20.77, -21.95) * mm, "end": v(20.77, -25.05) * mm});
            skLineSegment(sketch, "E1371", {"start": v(20.77, -25.05) * mm, "end": v(21.57, -25.05) * mm});
            skLineSegment(sketch, "E1372", {"start": v(21.57, -25.05) * mm, "end": v(21.57, -26.05) * mm});
            skLineSegment(sketch, "E1373", {"start": v(21.57, -26.05) * mm, "end": v(35.57, -26.05) * mm});
            skLineSegment(sketch, "E1374", {"start": v(35.57, -26.05) * mm, "end": v(35.57, -25.05) * mm});
            skLineSegment(sketch, "E1375", {"start": v(35.57, -25.05) * mm, "end": v(36.37, -25.05) * mm});
            skLineSegment(sketch, "E1376", {"start": v(36.37, -25.05) * mm, "end": v(36.37, -21.95) * mm});
            skLineSegment(sketch, "E1377", {"start": v(36.37, -21.95) * mm, "end": v(35.57, -21.95) * mm});
            skLineSegment(sketch, "E1378", {"start": v(35.57, -21.95) * mm, "end": v(35.57, -16.15) * mm});
            skLineSegment(sketch, "E1379", {"start": v(35.57, -16.15) * mm, "end": v(36.37, -16.15) * mm});
            skLineSegment(sketch, "E1380", {"start": v(36.37, -16.15) * mm, "end": v(36.37, -13.05) * mm});
            skLineSegment(sketch, "E1381", {"start": v(36.37, -13.05) * mm, "end": v(35.57, -13.05) * mm});
            skLineSegment(sketch, "E1382", {"start": v(35.57, -13.05) * mm, "end": v(35.57, -12.05) * mm});
            skLineSegment(sketch, "E1383", {"start": v(35.57, -12.05) * mm, "end": v(21.57, -12.05) * mm});
            skLineSegment(sketch, "E1384", {"start": v(40.62, -12.05) * mm, "end": v(40.62, -13.05) * mm});
            skLineSegment(sketch, "E1385", {"start": v(40.62, -13.05) * mm, "end": v(39.82, -13.05) * mm});
            skLineSegment(sketch, "E1386", {"start": v(39.82, -13.05) * mm, "end": v(39.82, -16.15) * mm});
            skLineSegment(sketch, "E1387", {"start": v(39.82, -16.15) * mm, "end": v(40.62, -16.15) * mm});
            skLineSegment(sketch, "E1388", {"start": v(40.62, -16.15) * mm, "end": v(40.62, -21.95) * mm});
            skLineSegment(sketch, "E1389", {"start": v(40.62, -21.95) * mm, "end": v(39.82, -21.95) * mm});
            skLineSegment(sketch, "E1390", {"start": v(39.82, -21.95) * mm, "end": v(39.82, -25.05) * mm});
            skLineSegment(sketch, "E1391", {"start": v(39.82, -25.05) * mm, "end": v(40.62, -25.05) * mm});
            skLineSegment(sketch, "E1392", {"start": v(40.62, -25.05) * mm, "end": v(40.62, -26.05) * mm});
            skLineSegment(sketch, "E1393", {"start": v(40.62, -26.05) * mm, "end": v(54.62, -26.05) * mm});
            skLineSegment(sketch, "E1394", {"start": v(54.62, -26.05) * mm, "end": v(54.62, -25.05) * mm});
            skLineSegment(sketch, "E1395", {"start": v(54.62, -25.05) * mm, "end": v(55.42, -25.05) * mm});
            skLineSegment(sketch, "E1396", {"start": v(55.42, -25.05) * mm, "end": v(55.42, -21.95) * mm});
            skLineSegment(sketch, "E1397", {"start": v(55.42, -21.95) * mm, "end": v(54.62, -21.95) * mm});
            skLineSegment(sketch, "E1398", {"start": v(54.62, -21.95) * mm, "end": v(54.62, -16.15) * mm});
            skLineSegment(sketch, "E1399", {"start": v(54.62, -16.15) * mm, "end": v(55.42, -16.15) * mm});
            skLineSegment(sketch, "E1400", {"start": v(55.42, -16.15) * mm, "end": v(55.42, -13.05) * mm});
            skLineSegment(sketch, "E1401", {"start": v(55.42, -13.05) * mm, "end": v(54.62, -13.05) * mm});
            skLineSegment(sketch, "E1402", {"start": v(54.62, -13.05) * mm, "end": v(54.62, -12.05) * mm});
            skLineSegment(sketch, "E1403", {"start": v(54.62, -12.05) * mm, "end": v(40.62, -12.05) * mm});
            skLineSegment(sketch, "E1404", {"start": v(59.67, -12.05) * mm, "end": v(59.67, -13.05) * mm});
            skLineSegment(sketch, "E1405", {"start": v(59.67, -13.05) * mm, "end": v(58.87, -13.05) * mm});
            skLineSegment(sketch, "E1406", {"start": v(58.87, -13.05) * mm, "end": v(58.87, -16.15) * mm});
            skLineSegment(sketch, "E1407", {"start": v(58.87, -16.15) * mm, "end": v(59.67, -16.15) * mm});
            skLineSegment(sketch, "E1408", {"start": v(59.67, -16.15) * mm, "end": v(59.67, -21.95) * mm});
            skLineSegment(sketch, "E1409", {"start": v(59.67, -21.95) * mm, "end": v(58.87, -21.95) * mm});
            skLineSegment(sketch, "E1410", {"start": v(58.87, -21.95) * mm, "end": v(58.87, -25.05) * mm});
            skLineSegment(sketch, "E1411", {"start": v(58.87, -25.05) * mm, "end": v(59.67, -25.05) * mm});
            skLineSegment(sketch, "E1412", {"start": v(59.67, -25.05) * mm, "end": v(59.67, -26.05) * mm});
            skLineSegment(sketch, "E1413", {"start": v(59.67, -26.05) * mm, "end": v(73.67, -26.05) * mm});
            skLineSegment(sketch, "E1414", {"start": v(73.67, -26.05) * mm, "end": v(73.67, -25.05) * mm});
            skLineSegment(sketch, "E1415", {"start": v(73.67, -25.05) * mm, "end": v(74.47, -25.05) * mm});
            skLineSegment(sketch, "E1416", {"start": v(74.47, -25.05) * mm, "end": v(74.47, -21.95) * mm});
            skLineSegment(sketch, "E1417", {"start": v(74.47, -21.95) * mm, "end": v(73.67, -21.95) * mm});
            skLineSegment(sketch, "E1418", {"start": v(73.67, -21.95) * mm, "end": v(73.67, -16.15) * mm});
            skLineSegment(sketch, "E1419", {"start": v(73.67, -16.15) * mm, "end": v(74.47, -16.15) * mm});
            skLineSegment(sketch, "E1420", {"start": v(74.47, -16.15) * mm, "end": v(74.47, -13.05) * mm});
            skLineSegment(sketch, "E1421", {"start": v(74.47, -13.05) * mm, "end": v(73.67, -13.05) * mm});
            skLineSegment(sketch, "E1422", {"start": v(73.67, -13.05) * mm, "end": v(73.67, -12.05) * mm});
            skLineSegment(sketch, "E1423", {"start": v(73.67, -12.05) * mm, "end": v(59.67, -12.05) * mm});
            skLineSegment(sketch, "E1424", {"start": v(121.59, -12.05) * mm, "end": v(121.59, -13.05) * mm});
            skLineSegment(sketch, "E1425", {"start": v(121.59, -13.05) * mm, "end": v(120.79, -13.05) * mm});
            skLineSegment(sketch, "E1426", {"start": v(120.79, -13.05) * mm, "end": v(120.79, -16.15) * mm});
            skLineSegment(sketch, "E1427", {"start": v(120.79, -16.15) * mm, "end": v(121.59, -16.15) * mm});
            skLineSegment(sketch, "E1428", {"start": v(121.59, -16.15) * mm, "end": v(121.59, -21.95) * mm});
            skLineSegment(sketch, "E1429", {"start": v(121.59, -21.95) * mm, "end": v(120.79, -21.95) * mm});
            skLineSegment(sketch, "E1430", {"start": v(120.79, -21.95) * mm, "end": v(120.79, -25.05) * mm});
            skLineSegment(sketch, "E1431", {"start": v(120.79, -25.05) * mm, "end": v(121.59, -25.05) * mm});
            skLineSegment(sketch, "E1432", {"start": v(121.59, -25.05) * mm, "end": v(121.59, -26.05) * mm});
            skLineSegment(sketch, "E1433", {"start": v(121.59, -26.05) * mm, "end": v(135.59, -26.05) * mm});
            skLineSegment(sketch, "E1434", {"start": v(135.59, -26.05) * mm, "end": v(135.59, -25.05) * mm});
            skLineSegment(sketch, "E1435", {"start": v(135.59, -25.05) * mm, "end": v(136.39, -25.05) * mm});
            skLineSegment(sketch, "E1436", {"start": v(136.39, -25.05) * mm, "end": v(136.39, -21.95) * mm});
            skLineSegment(sketch, "E1437", {"start": v(136.39, -21.95) * mm, "end": v(135.59, -21.95) * mm});
            skLineSegment(sketch, "E1438", {"start": v(135.59, -21.95) * mm, "end": v(135.59, -16.15) * mm});
            skLineSegment(sketch, "E1439", {"start": v(135.59, -16.15) * mm, "end": v(136.39, -16.15) * mm});
            skLineSegment(sketch, "E1440", {"start": v(136.39, -16.15) * mm, "end": v(136.39, -13.05) * mm});
            skLineSegment(sketch, "E1441", {"start": v(136.39, -13.05) * mm, "end": v(135.59, -13.05) * mm});
            skLineSegment(sketch, "E1442", {"start": v(135.59, -13.05) * mm, "end": v(135.59, -12.05) * mm});
            skLineSegment(sketch, "E1443", {"start": v(135.59, -12.05) * mm, "end": v(121.59, -12.05) * mm});
            skLineSegment(sketch, "E1444", {"start": v(100.16, 7) * mm, "end": v(100.16, 6) * mm});
            skLineSegment(sketch, "E1445", {"start": v(100.16, 6) * mm, "end": v(99.36, 6) * mm});
            skLineSegment(sketch, "E1446", {"start": v(99.36, 6) * mm, "end": v(99.36, 2.9) * mm});
            skLineSegment(sketch, "E1447", {"start": v(99.36, 2.9) * mm, "end": v(100.16, 2.9) * mm});
            skLineSegment(sketch, "E1448", {"start": v(100.16, 2.9) * mm, "end": v(100.16, 2.3) * mm});
            skLineSegment(sketch, "E1449", {"start": v(100.16, 2.3) * mm, "end": v(98.63, 2.3) * mm});
            skLineSegment(sketch, "E1450", {"start": v(98.63, 2.3) * mm, "end": v(98.63, 5.53) * mm});
            skLineSegment(sketch, "E1451", {"start": v(98.63, 5.53) * mm, "end": v(91.88, 5.53) * mm});
            skLineSegment(sketch, "E1452", {"start": v(91.88, 5.53) * mm, "end": v(91.88, 2.3) * mm});
            skLineSegment(sketch, "E1453", {"start": v(91.88, 2.3) * mm, "end": v(91.06, 2.3) * mm});
            skLineSegment(sketch, "E1454", {"start": v(91.06, 2.3) * mm, "end": v(91.06, -0.5) * mm});
            skLineSegment(sketch, "E1455", {"start": v(91.06, -0.5) * mm, "end": v(91.88, -0.5) * mm});
            skLineSegment(sketch, "E1456", {"start": v(91.88, -0.5) * mm, "end": v(91.88, -6.77) * mm});
            skLineSegment(sketch, "E1457", {"start": v(91.88, -6.77) * mm, "end": v(93.6, -6.77) * mm});
            skLineSegment(sketch, "E1458", {"start": v(93.6, -6.77) * mm, "end": v(93.6, -7.97) * mm});
            skLineSegment(sketch, "E1459", {"start": v(93.6, -7.97) * mm, "end": v(96.9, -7.97) * mm});
            skLineSegment(sketch, "E1460", {"start": v(96.9, -7.97) * mm, "end": v(96.9, -6.77) * mm});
            skLineSegment(sketch, "E1461", {"start": v(96.9, -6.77) * mm, "end": v(98.63, -6.77) * mm});
            skLineSegment(sketch, "E1462", {"start": v(98.63, -6.77) * mm, "end": v(98.63, -2.3) * mm});
            skLineSegment(sketch, "E1463", {"start": v(98.63, -2.3) * mm, "end": v(100.16, -2.3) * mm});
            skLineSegment(sketch, "E1464", {"start": v(100.16, -2.3) * mm, "end": v(100.16, -2.9) * mm});
            skLineSegment(sketch, "E1465", {"start": v(100.16, -2.9) * mm, "end": v(99.36, -2.9) * mm});
            skLineSegment(sketch, "E1466", {"start": v(99.36, -2.9) * mm, "end": v(99.36, -6) * mm});
            skLineSegment(sketch, "E1467", {"start": v(99.36, -6) * mm, "end": v(100.16, -6) * mm});
            skLineSegment(sketch, "E1468", {"start": v(100.16, -6) * mm, "end": v(100.16, -7) * mm});
            skLineSegment(sketch, "E1469", {"start": v(100.16, -7) * mm, "end": v(114.16, -7) * mm});
            skLineSegment(sketch, "E1470", {"start": v(114.16, -7) * mm, "end": v(114.16, -6) * mm});
            skLineSegment(sketch, "E1471", {"start": v(114.16, -6) * mm, "end": v(114.95, -6) * mm});
            skLineSegment(sketch, "E1472", {"start": v(114.95, -6) * mm, "end": v(114.95, -2.9) * mm});
            skLineSegment(sketch, "E1473", {"start": v(114.95, -2.9) * mm, "end": v(114.16, -2.9) * mm});
            skLineSegment(sketch, "E1474", {"start": v(114.16, -2.9) * mm, "end": v(114.16, -2.3) * mm});
            skLineSegment(sketch, "E1475", {"start": v(114.16, -2.3) * mm, "end": v(115.68, -2.3) * mm});
            skLineSegment(sketch, "E1476", {"start": v(115.68, -2.3) * mm, "end": v(115.68, -6.77) * mm});
            skLineSegment(sketch, "E1477", {"start": v(115.68, -6.77) * mm, "end": v(117.4, -6.77) * mm});
            skLineSegment(sketch, "E1478", {"start": v(117.4, -6.77) * mm, "end": v(117.4, -7.97) * mm});
            skLineSegment(sketch, "E1479", {"start": v(117.4, -7.97) * mm, "end": v(120.7, -7.97) * mm});
            skLineSegment(sketch, "E1480", {"start": v(120.7, -7.97) * mm, "end": v(120.7, -6.77) * mm});
            skLineSegment(sketch, "E1481", {"start": v(120.7, -6.77) * mm, "end": v(122.43, -6.77) * mm});
            skLineSegment(sketch, "E1482", {"start": v(122.43, -6.77) * mm, "end": v(122.43, -0.5) * mm});
            skLineSegment(sketch, "E1483", {"start": v(122.43, -0.5) * mm, "end": v(123.26, -0.5) * mm});
            skLineSegment(sketch, "E1484", {"start": v(123.26, -0.5) * mm, "end": v(123.26, 2.3) * mm});
            skLineSegment(sketch, "E1485", {"start": v(123.26, 2.3) * mm, "end": v(122.43, 2.3) * mm});
            skLineSegment(sketch, "E1486", {"start": v(122.43, 2.3) * mm, "end": v(122.43, 5.53) * mm});
            skLineSegment(sketch, "E1487", {"start": v(122.43, 5.53) * mm, "end": v(115.68, 5.53) * mm});
            skLineSegment(sketch, "E1488", {"start": v(115.68, 5.53) * mm, "end": v(115.68, 2.3) * mm});
            skLineSegment(sketch, "E1489", {"start": v(115.68, 2.3) * mm, "end": v(114.16, 2.3) * mm});
            skLineSegment(sketch, "E1490", {"start": v(114.16, 2.3) * mm, "end": v(114.16, 2.9) * mm});
            skLineSegment(sketch, "E1491", {"start": v(114.16, 2.9) * mm, "end": v(114.95, 2.9) * mm});
            skLineSegment(sketch, "E1492", {"start": v(114.95, 2.9) * mm, "end": v(114.95, 6) * mm});
            skLineSegment(sketch, "E1493", {"start": v(114.95, 6) * mm, "end": v(114.16, 6) * mm});
            skLineSegment(sketch, "E1494", {"start": v(114.16, 6) * mm, "end": v(114.16, 7) * mm});
            skLineSegment(sketch, "E1495", {"start": v(114.16, 7) * mm, "end": v(100.16, 7) * mm});
            skLineSegment(sketch, "E1496", {"start": v(-147.5, 7) * mm, "end": v(-147.5, 6) * mm});
            skLineSegment(sketch, "E1497", {"start": v(-147.5, 6) * mm, "end": v(-148.3, 6) * mm});
            skLineSegment(sketch, "E1498", {"start": v(-148.3, 6) * mm, "end": v(-148.3, 2.9) * mm});
            skLineSegment(sketch, "E1499", {"start": v(-148.3, 2.9) * mm, "end": v(-147.5, 2.9) * mm});
            skLineSegment(sketch, "E1500", {"start": v(-147.5, 2.9) * mm, "end": v(-147.5, -2.9) * mm});
            skLineSegment(sketch, "E1501", {"start": v(-147.5, -2.9) * mm, "end": v(-148.3, -2.9) * mm});
            skLineSegment(sketch, "E1502", {"start": v(-148.3, -2.9) * mm, "end": v(-148.3, -6) * mm});
            skLineSegment(sketch, "E1503", {"start": v(-148.3, -6) * mm, "end": v(-147.5, -6) * mm});
            skLineSegment(sketch, "E1504", {"start": v(-147.5, -6) * mm, "end": v(-147.5, -7) * mm});
            skLineSegment(sketch, "E1505", {"start": v(-147.5, -7) * mm, "end": v(-133.5, -7) * mm});
            skLineSegment(sketch, "E1506", {"start": v(-133.5, -7) * mm, "end": v(-133.5, -6) * mm});
            skLineSegment(sketch, "E1507", {"start": v(-133.5, -6) * mm, "end": v(-132.7, -6) * mm});
            skLineSegment(sketch, "E1508", {"start": v(-132.7, -6) * mm, "end": v(-132.7, -2.9) * mm});
            skLineSegment(sketch, "E1509", {"start": v(-132.7, -2.9) * mm, "end": v(-133.5, -2.9) * mm});
            skLineSegment(sketch, "E1510", {"start": v(-133.5, -2.9) * mm, "end": v(-133.5, 2.9) * mm});
            skLineSegment(sketch, "E1511", {"start": v(-133.5, 2.9) * mm, "end": v(-132.7, 2.9) * mm});
            skLineSegment(sketch, "E1512", {"start": v(-132.7, 2.9) * mm, "end": v(-132.7, 6) * mm});
            skLineSegment(sketch, "E1513", {"start": v(-132.7, 6) * mm, "end": v(-133.5, 6) * mm});
            skLineSegment(sketch, "E1514", {"start": v(-133.5, 6) * mm, "end": v(-133.5, 7) * mm});
            skLineSegment(sketch, "E1515", {"start": v(-133.5, 7) * mm, "end": v(-147.5, 7) * mm});
            skLineSegment(sketch, "E1516", {"start": v(-121.3, 7) * mm, "end": v(-121.3, 6) * mm});
            skLineSegment(sketch, "E1517", {"start": v(-121.3, 6) * mm, "end": v(-122.1, 6) * mm});
            skLineSegment(sketch, "E1518", {"start": v(-122.1, 6) * mm, "end": v(-122.1, 2.9) * mm});
            skLineSegment(sketch, "E1519", {"start": v(-122.1, 2.9) * mm, "end": v(-121.3, 2.9) * mm});
            skLineSegment(sketch, "E1520", {"start": v(-121.3, 2.9) * mm, "end": v(-121.3, -2.9) * mm});
            skLineSegment(sketch, "E1521", {"start": v(-121.3, -2.9) * mm, "end": v(-122.1, -2.9) * mm});
            skLineSegment(sketch, "E1522", {"start": v(-122.1, -2.9) * mm, "end": v(-122.1, -6) * mm});
            skLineSegment(sketch, "E1523", {"start": v(-122.1, -6) * mm, "end": v(-121.3, -6) * mm});
            skLineSegment(sketch, "E1524", {"start": v(-121.3, -6) * mm, "end": v(-121.3, -7) * mm});
            skLineSegment(sketch, "E1525", {"start": v(-121.3, -7) * mm, "end": v(-107.3, -7) * mm});
            skLineSegment(sketch, "E1526", {"start": v(-107.3, -7) * mm, "end": v(-107.3, -6) * mm});
            skLineSegment(sketch, "E1527", {"start": v(-107.3, -6) * mm, "end": v(-106.5, -6) * mm});
            skLineSegment(sketch, "E1528", {"start": v(-106.5, -6) * mm, "end": v(-106.5, -2.9) * mm});
            skLineSegment(sketch, "E1529", {"start": v(-106.5, -2.9) * mm, "end": v(-107.3, -2.9) * mm});
            skLineSegment(sketch, "E1530", {"start": v(-107.3, -2.9) * mm, "end": v(-107.3, 2.9) * mm});
            skLineSegment(sketch, "E1531", {"start": v(-107.3, 2.9) * mm, "end": v(-106.5, 2.9) * mm});
            skLineSegment(sketch, "E1532", {"start": v(-106.5, 2.9) * mm, "end": v(-106.5, 6) * mm});
            skLineSegment(sketch, "E1533", {"start": v(-106.5, 6) * mm, "end": v(-107.3, 6) * mm});
            skLineSegment(sketch, "E1534", {"start": v(-107.3, 6) * mm, "end": v(-107.3, 7) * mm});
            skLineSegment(sketch, "E1535", {"start": v(-107.3, 7) * mm, "end": v(-121.3, 7) * mm});
            skLineSegment(sketch, "E1536", {"start": v(-102.25, 7) * mm, "end": v(-102.25, 6) * mm});
            skLineSegment(sketch, "E1537", {"start": v(-102.25, 6) * mm, "end": v(-103.05, 6) * mm});
            skLineSegment(sketch, "E1538", {"start": v(-103.05, 6) * mm, "end": v(-103.05, 2.9) * mm});
            skLineSegment(sketch, "E1539", {"start": v(-103.05, 2.9) * mm, "end": v(-102.25, 2.9) * mm});
            skLineSegment(sketch, "E1540", {"start": v(-102.25, 2.9) * mm, "end": v(-102.25, -2.9) * mm});
            skLineSegment(sketch, "E1541", {"start": v(-102.25, -2.9) * mm, "end": v(-103.05, -2.9) * mm});
            skLineSegment(sketch, "E1542", {"start": v(-103.05, -2.9) * mm, "end": v(-103.05, -6) * mm});
            skLineSegment(sketch, "E1543", {"start": v(-103.05, -6) * mm, "end": v(-102.25, -6) * mm});
            skLineSegment(sketch, "E1544", {"start": v(-102.25, -6) * mm, "end": v(-102.25, -7) * mm});
            skLineSegment(sketch, "E1545", {"start": v(-102.25, -7) * mm, "end": v(-88.25, -7) * mm});
            skLineSegment(sketch, "E1546", {"start": v(-88.25, -7) * mm, "end": v(-88.25, -6) * mm});
            skLineSegment(sketch, "E1547", {"start": v(-88.25, -6) * mm, "end": v(-87.45, -6) * mm});
            skLineSegment(sketch, "E1548", {"start": v(-87.45, -6) * mm, "end": v(-87.45, -2.9) * mm});
            skLineSegment(sketch, "E1549", {"start": v(-87.45, -2.9) * mm, "end": v(-88.25, -2.9) * mm});
            skLineSegment(sketch, "E1550", {"start": v(-88.25, -2.9) * mm, "end": v(-88.25, 2.9) * mm});
            skLineSegment(sketch, "E1551", {"start": v(-88.25, 2.9) * mm, "end": v(-87.45, 2.9) * mm});
            skLineSegment(sketch, "E1552", {"start": v(-87.45, 2.9) * mm, "end": v(-87.45, 6) * mm});
            skLineSegment(sketch, "E1553", {"start": v(-87.45, 6) * mm, "end": v(-88.25, 6) * mm});
            skLineSegment(sketch, "E1554", {"start": v(-88.25, 6) * mm, "end": v(-88.25, 7) * mm});
            skLineSegment(sketch, "E1555", {"start": v(-88.25, 7) * mm, "end": v(-102.25, 7) * mm});
            skLineSegment(sketch, "E1556", {"start": v(-83.2, 7) * mm, "end": v(-83.2, 6) * mm});
            skLineSegment(sketch, "E1557", {"start": v(-83.2, 6) * mm, "end": v(-84, 6) * mm});
            skLineSegment(sketch, "E1558", {"start": v(-84, 6) * mm, "end": v(-84, 2.9) * mm});
            skLineSegment(sketch, "E1559", {"start": v(-84, 2.9) * mm, "end": v(-83.2, 2.9) * mm});
            skLineSegment(sketch, "E1560", {"start": v(-83.2, 2.9) * mm, "end": v(-83.2, -2.9) * mm});
            skLineSegment(sketch, "E1561", {"start": v(-83.2, -2.9) * mm, "end": v(-84, -2.9) * mm});
            skLineSegment(sketch, "E1562", {"start": v(-84, -2.9) * mm, "end": v(-84, -6) * mm});
            skLineSegment(sketch, "E1563", {"start": v(-84, -6) * mm, "end": v(-83.2, -6) * mm});
            skLineSegment(sketch, "E1564", {"start": v(-83.2, -6) * mm, "end": v(-83.2, -7) * mm});
            skLineSegment(sketch, "E1565", {"start": v(-83.2, -7) * mm, "end": v(-69.2, -7) * mm});
            skLineSegment(sketch, "E1566", {"start": v(-69.2, -7) * mm, "end": v(-69.2, -6) * mm});
            skLineSegment(sketch, "E1567", {"start": v(-69.2, -6) * mm, "end": v(-68.4, -6) * mm});
            skLineSegment(sketch, "E1568", {"start": v(-68.4, -6) * mm, "end": v(-68.4, -2.9) * mm});
            skLineSegment(sketch, "E1569", {"start": v(-68.4, -2.9) * mm, "end": v(-69.2, -2.9) * mm});
            skLineSegment(sketch, "E1570", {"start": v(-69.2, -2.9) * mm, "end": v(-69.2, 2.9) * mm});
            skLineSegment(sketch, "E1571", {"start": v(-69.2, 2.9) * mm, "end": v(-68.4, 2.9) * mm});
            skLineSegment(sketch, "E1572", {"start": v(-68.4, 2.9) * mm, "end": v(-68.4, 6) * mm});
            skLineSegment(sketch, "E1573", {"start": v(-68.4, 6) * mm, "end": v(-69.2, 6) * mm});
            skLineSegment(sketch, "E1574", {"start": v(-69.2, 6) * mm, "end": v(-69.2, 7) * mm});
            skLineSegment(sketch, "E1575", {"start": v(-69.2, 7) * mm, "end": v(-83.2, 7) * mm});
            skLineSegment(sketch, "E1576", {"start": v(-64.15, 7) * mm, "end": v(-64.15, 6) * mm});
            skLineSegment(sketch, "E1577", {"start": v(-64.15, 6) * mm, "end": v(-64.95, 6) * mm});
            skLineSegment(sketch, "E1578", {"start": v(-64.95, 6) * mm, "end": v(-64.95, 2.9) * mm});
            skLineSegment(sketch, "E1579", {"start": v(-64.95, 2.9) * mm, "end": v(-64.15, 2.9) * mm});
            skLineSegment(sketch, "E1580", {"start": v(-64.15, 2.9) * mm, "end": v(-64.15, -2.9) * mm});
            skLineSegment(sketch, "E1581", {"start": v(-64.15, -2.9) * mm, "end": v(-64.95, -2.9) * mm});
            skLineSegment(sketch, "E1582", {"start": v(-64.95, -2.9) * mm, "end": v(-64.95, -6) * mm});
            skLineSegment(sketch, "E1583", {"start": v(-64.95, -6) * mm, "end": v(-64.15, -6) * mm});
            skLineSegment(sketch, "E1584", {"start": v(-64.15, -6) * mm, "end": v(-64.15, -7) * mm});
            skLineSegment(sketch, "E1585", {"start": v(-64.15, -7) * mm, "end": v(-50.15, -7) * mm});
            skLineSegment(sketch, "E1586", {"start": v(-50.15, -7) * mm, "end": v(-50.15, -6) * mm});
            skLineSegment(sketch, "E1587", {"start": v(-50.15, -6) * mm, "end": v(-49.35, -6) * mm});
            skLineSegment(sketch, "E1588", {"start": v(-49.35, -6) * mm, "end": v(-49.35, -2.9) * mm});
            skLineSegment(sketch, "E1589", {"start": v(-49.35, -2.9) * mm, "end": v(-50.15, -2.9) * mm});
            skLineSegment(sketch, "E1590", {"start": v(-50.15, -2.9) * mm, "end": v(-50.15, 2.9) * mm});
            skLineSegment(sketch, "E1591", {"start": v(-50.15, 2.9) * mm, "end": v(-49.35, 2.9) * mm});
            skLineSegment(sketch, "E1592", {"start": v(-49.35, 2.9) * mm, "end": v(-49.35, 6) * mm});
            skLineSegment(sketch, "E1593", {"start": v(-49.35, 6) * mm, "end": v(-50.15, 6) * mm});
            skLineSegment(sketch, "E1594", {"start": v(-50.15, 6) * mm, "end": v(-50.15, 7) * mm});
            skLineSegment(sketch, "E1595", {"start": v(-50.15, 7) * mm, "end": v(-64.15, 7) * mm});
            skLineSegment(sketch, "E1596", {"start": v(-45.1, 7) * mm, "end": v(-45.1, 6) * mm});
            skLineSegment(sketch, "E1597", {"start": v(-45.1, 6) * mm, "end": v(-45.9, 6) * mm});
            skLineSegment(sketch, "E1598", {"start": v(-45.9, 6) * mm, "end": v(-45.9, 2.9) * mm});
            skLineSegment(sketch, "E1599", {"start": v(-45.9, 2.9) * mm, "end": v(-45.1, 2.9) * mm});
            skLineSegment(sketch, "E1600", {"start": v(-45.1, 2.9) * mm, "end": v(-45.1, -2.9) * mm});
            skLineSegment(sketch, "E1601", {"start": v(-45.1, -2.9) * mm, "end": v(-45.9, -2.9) * mm});
            skLineSegment(sketch, "E1602", {"start": v(-45.9, -2.9) * mm, "end": v(-45.9, -6) * mm});
            skLineSegment(sketch, "E1603", {"start": v(-45.9, -6) * mm, "end": v(-45.1, -6) * mm});
            skLineSegment(sketch, "E1604", {"start": v(-45.1, -6) * mm, "end": v(-45.1, -7) * mm});
            skLineSegment(sketch, "E1605", {"start": v(-45.1, -7) * mm, "end": v(-31.1, -7) * mm});
            skLineSegment(sketch, "E1606", {"start": v(-31.1, -7) * mm, "end": v(-31.1, -6) * mm});
            skLineSegment(sketch, "E1607", {"start": v(-31.1, -6) * mm, "end": v(-30.3, -6) * mm});
            skLineSegment(sketch, "E1608", {"start": v(-30.3, -6) * mm, "end": v(-30.3, -2.9) * mm});
            skLineSegment(sketch, "E1609", {"start": v(-30.3, -2.9) * mm, "end": v(-31.1, -2.9) * mm});
            skLineSegment(sketch, "E1610", {"start": v(-31.1, -2.9) * mm, "end": v(-31.1, 2.9) * mm});
            skLineSegment(sketch, "E1611", {"start": v(-31.1, 2.9) * mm, "end": v(-30.3, 2.9) * mm});
            skLineSegment(sketch, "E1612", {"start": v(-30.3, 2.9) * mm, "end": v(-30.3, 6) * mm});
            skLineSegment(sketch, "E1613", {"start": v(-30.3, 6) * mm, "end": v(-31.1, 6) * mm});
            skLineSegment(sketch, "E1614", {"start": v(-31.1, 6) * mm, "end": v(-31.1, 7) * mm});
            skLineSegment(sketch, "E1615", {"start": v(-31.1, 7) * mm, "end": v(-45.1, 7) * mm});
            skLineSegment(sketch, "E1616", {"start": v(-26.05, 7) * mm, "end": v(-26.05, 6) * mm});
            skLineSegment(sketch, "E1617", {"start": v(-26.05, 6) * mm, "end": v(-26.85, 6) * mm});
            skLineSegment(sketch, "E1618", {"start": v(-26.85, 6) * mm, "end": v(-26.85, 2.9) * mm});
            skLineSegment(sketch, "E1619", {"start": v(-26.85, 2.9) * mm, "end": v(-26.05, 2.9) * mm});
            skLineSegment(sketch, "E1620", {"start": v(-26.05, 2.9) * mm, "end": v(-26.05, -2.9) * mm});
            skLineSegment(sketch, "E1621", {"start": v(-26.05, -2.9) * mm, "end": v(-26.85, -2.9) * mm});
            skLineSegment(sketch, "E1622", {"start": v(-26.85, -2.9) * mm, "end": v(-26.85, -6) * mm});
            skLineSegment(sketch, "E1623", {"start": v(-26.85, -6) * mm, "end": v(-26.05, -6) * mm});
            skLineSegment(sketch, "E1624", {"start": v(-26.05, -6) * mm, "end": v(-26.05, -7) * mm});
            skLineSegment(sketch, "E1625", {"start": v(-26.05, -7) * mm, "end": v(-12.05, -7) * mm});
            skLineSegment(sketch, "E1626", {"start": v(-12.05, -7) * mm, "end": v(-12.05, -6) * mm});
            skLineSegment(sketch, "E1627", {"start": v(-12.05, -6) * mm, "end": v(-11.25, -6) * mm});
            skLineSegment(sketch, "E1628", {"start": v(-11.25, -6) * mm, "end": v(-11.25, -2.9) * mm});
            skLineSegment(sketch, "E1629", {"start": v(-11.25, -2.9) * mm, "end": v(-12.05, -2.9) * mm});
            skLineSegment(sketch, "E1630", {"start": v(-12.05, -2.9) * mm, "end": v(-12.05, 2.9) * mm});
            skLineSegment(sketch, "E1631", {"start": v(-12.05, 2.9) * mm, "end": v(-11.25, 2.9) * mm});
            skLineSegment(sketch, "E1632", {"start": v(-11.25, 2.9) * mm, "end": v(-11.25, 6) * mm});
            skLineSegment(sketch, "E1633", {"start": v(-11.25, 6) * mm, "end": v(-12.05, 6) * mm});
            skLineSegment(sketch, "E1634", {"start": v(-12.05, 6) * mm, "end": v(-12.05, 7) * mm});
            skLineSegment(sketch, "E1635", {"start": v(-12.05, 7) * mm, "end": v(-26.05, 7) * mm});
            skLineSegment(sketch, "E1636", {"start": v(-7, 7) * mm, "end": v(-7, 6) * mm});
            skLineSegment(sketch, "E1637", {"start": v(-7, 6) * mm, "end": v(-7.8, 6) * mm});
            skLineSegment(sketch, "E1638", {"start": v(-7.8, 6) * mm, "end": v(-7.8, 2.9) * mm});
            skLineSegment(sketch, "E1639", {"start": v(-7.8, 2.9) * mm, "end": v(-7, 2.9) * mm});
            skLineSegment(sketch, "E1640", {"start": v(-7, 2.9) * mm, "end": v(-7, -2.9) * mm});
            skLineSegment(sketch, "E1641", {"start": v(-7, -2.9) * mm, "end": v(-7.8, -2.9) * mm});
            skLineSegment(sketch, "E1642", {"start": v(-7.8, -2.9) * mm, "end": v(-7.8, -6) * mm});
            skLineSegment(sketch, "E1643", {"start": v(-7.8, -6) * mm, "end": v(-7, -6) * mm});
            skLineSegment(sketch, "E1644", {"start": v(-7, -6) * mm, "end": v(-7, -7) * mm});
            skLineSegment(sketch, "E1645", {"start": v(-7, -7) * mm, "end": v(7, -7) * mm});
            skLineSegment(sketch, "E1646", {"start": v(7, -7) * mm, "end": v(7, -6) * mm});
            skLineSegment(sketch, "E1647", {"start": v(7, -6) * mm, "end": v(7.8, -6) * mm});
            skLineSegment(sketch, "E1648", {"start": v(7.8, -6) * mm, "end": v(7.8, -2.9) * mm});
            skLineSegment(sketch, "E1649", {"start": v(7.8, -2.9) * mm, "end": v(7, -2.9) * mm});
            skLineSegment(sketch, "E1650", {"start": v(7, -2.9) * mm, "end": v(7, 2.9) * mm});
            skLineSegment(sketch, "E1651", {"start": v(7, 2.9) * mm, "end": v(7.8, 2.9) * mm});
            skLineSegment(sketch, "E1652", {"start": v(7.8, 2.9) * mm, "end": v(7.8, 6) * mm});
            skLineSegment(sketch, "E1653", {"start": v(7.8, 6) * mm, "end": v(7, 6) * mm});
            skLineSegment(sketch, "E1654", {"start": v(7, 6) * mm, "end": v(7, 7) * mm});
            skLineSegment(sketch, "E1655", {"start": v(7, 7) * mm, "end": v(-7, 7) * mm});
            skLineSegment(sketch, "E1656", {"start": v(12.05, 7) * mm, "end": v(12.05, 6) * mm});
            skLineSegment(sketch, "E1657", {"start": v(12.05, 6) * mm, "end": v(11.25, 6) * mm});
            skLineSegment(sketch, "E1658", {"start": v(11.25, 6) * mm, "end": v(11.25, 2.9) * mm});
            skLineSegment(sketch, "E1659", {"start": v(11.25, 2.9) * mm, "end": v(12.05, 2.9) * mm});
            skLineSegment(sketch, "E1660", {"start": v(12.05, 2.9) * mm, "end": v(12.05, -2.9) * mm});
            skLineSegment(sketch, "E1661", {"start": v(12.05, -2.9) * mm, "end": v(11.25, -2.9) * mm});
            skLineSegment(sketch, "E1662", {"start": v(11.25, -2.9) * mm, "end": v(11.25, -6) * mm});
            skLineSegment(sketch, "E1663", {"start": v(11.25, -6) * mm, "end": v(12.05, -6) * mm});
            skLineSegment(sketch, "E1664", {"start": v(12.05, -6) * mm, "end": v(12.05, -7) * mm});
            skLineSegment(sketch, "E1665", {"start": v(12.05, -7) * mm, "end": v(26.05, -7) * mm});
            skLineSegment(sketch, "E1666", {"start": v(26.05, -7) * mm, "end": v(26.05, -6) * mm});
            skLineSegment(sketch, "E1667", {"start": v(26.05, -6) * mm, "end": v(26.85, -6) * mm});
            skLineSegment(sketch, "E1668", {"start": v(26.85, -6) * mm, "end": v(26.85, -2.9) * mm});
            skLineSegment(sketch, "E1669", {"start": v(26.85, -2.9) * mm, "end": v(26.05, -2.9) * mm});
            skLineSegment(sketch, "E1670", {"start": v(26.05, -2.9) * mm, "end": v(26.05, 2.9) * mm});
            skLineSegment(sketch, "E1671", {"start": v(26.05, 2.9) * mm, "end": v(26.85, 2.9) * mm});
            skLineSegment(sketch, "E1672", {"start": v(26.85, 2.9) * mm, "end": v(26.85, 6) * mm});
            skLineSegment(sketch, "E1673", {"start": v(26.85, 6) * mm, "end": v(26.05, 6) * mm});
            skLineSegment(sketch, "E1674", {"start": v(26.05, 6) * mm, "end": v(26.05, 7) * mm});
            skLineSegment(sketch, "E1675", {"start": v(26.05, 7) * mm, "end": v(12.05, 7) * mm});
            skLineSegment(sketch, "E1676", {"start": v(31.1, 7) * mm, "end": v(31.1, 6) * mm});
            skLineSegment(sketch, "E1677", {"start": v(31.1, 6) * mm, "end": v(30.3, 6) * mm});
            skLineSegment(sketch, "E1678", {"start": v(30.3, 6) * mm, "end": v(30.3, 2.9) * mm});
            skLineSegment(sketch, "E1679", {"start": v(30.3, 2.9) * mm, "end": v(31.1, 2.9) * mm});
            skLineSegment(sketch, "E1680", {"start": v(31.1, 2.9) * mm, "end": v(31.1, -2.9) * mm});
            skLineSegment(sketch, "E1681", {"start": v(31.1, -2.9) * mm, "end": v(30.3, -2.9) * mm});
            skLineSegment(sketch, "E1682", {"start": v(30.3, -2.9) * mm, "end": v(30.3, -6) * mm});
            skLineSegment(sketch, "E1683", {"start": v(30.3, -6) * mm, "end": v(31.1, -6) * mm});
            skLineSegment(sketch, "E1684", {"start": v(31.1, -6) * mm, "end": v(31.1, -7) * mm});
            skLineSegment(sketch, "E1685", {"start": v(31.1, -7) * mm, "end": v(45.1, -7) * mm});
            skLineSegment(sketch, "E1686", {"start": v(45.1, -7) * mm, "end": v(45.1, -6) * mm});
            skLineSegment(sketch, "E1687", {"start": v(45.1, -6) * mm, "end": v(45.9, -6) * mm});
            skLineSegment(sketch, "E1688", {"start": v(45.9, -6) * mm, "end": v(45.9, -2.9) * mm});
            skLineSegment(sketch, "E1689", {"start": v(45.9, -2.9) * mm, "end": v(45.1, -2.9) * mm});
            skLineSegment(sketch, "E1690", {"start": v(45.1, -2.9) * mm, "end": v(45.1, 2.9) * mm});
            skLineSegment(sketch, "E1691", {"start": v(45.1, 2.9) * mm, "end": v(45.9, 2.9) * mm});
            skLineSegment(sketch, "E1692", {"start": v(45.9, 2.9) * mm, "end": v(45.9, 6) * mm});
            skLineSegment(sketch, "E1693", {"start": v(45.9, 6) * mm, "end": v(45.1, 6) * mm});
            skLineSegment(sketch, "E1694", {"start": v(45.1, 6) * mm, "end": v(45.1, 7) * mm});
            skLineSegment(sketch, "E1695", {"start": v(45.1, 7) * mm, "end": v(31.1, 7) * mm});
            skLineSegment(sketch, "E1696", {"start": v(50.15, 7) * mm, "end": v(50.15, 6) * mm});
            skLineSegment(sketch, "E1697", {"start": v(50.15, 6) * mm, "end": v(49.35, 6) * mm});
            skLineSegment(sketch, "E1698", {"start": v(49.35, 6) * mm, "end": v(49.35, 2.9) * mm});
            skLineSegment(sketch, "E1699", {"start": v(49.35, 2.9) * mm, "end": v(50.15, 2.9) * mm});
            skLineSegment(sketch, "E1700", {"start": v(50.15, 2.9) * mm, "end": v(50.15, -2.9) * mm});
            skLineSegment(sketch, "E1701", {"start": v(50.15, -2.9) * mm, "end": v(49.35, -2.9) * mm});
            skLineSegment(sketch, "E1702", {"start": v(49.35, -2.9) * mm, "end": v(49.35, -6) * mm});
            skLineSegment(sketch, "E1703", {"start": v(49.35, -6) * mm, "end": v(50.15, -6) * mm});
            skLineSegment(sketch, "E1704", {"start": v(50.15, -6) * mm, "end": v(50.15, -7) * mm});
            skLineSegment(sketch, "E1705", {"start": v(50.15, -7) * mm, "end": v(64.15, -7) * mm});
            skLineSegment(sketch, "E1706", {"start": v(64.15, -7) * mm, "end": v(64.15, -6) * mm});
            skLineSegment(sketch, "E1707", {"start": v(64.15, -6) * mm, "end": v(64.95, -6) * mm});
            skLineSegment(sketch, "E1708", {"start": v(64.95, -6) * mm, "end": v(64.95, -2.9) * mm});
            skLineSegment(sketch, "E1709", {"start": v(64.95, -2.9) * mm, "end": v(64.15, -2.9) * mm});
            skLineSegment(sketch, "E1710", {"start": v(64.15, -2.9) * mm, "end": v(64.15, 2.9) * mm});
            skLineSegment(sketch, "E1711", {"start": v(64.15, 2.9) * mm, "end": v(64.95, 2.9) * mm});
            skLineSegment(sketch, "E1712", {"start": v(64.95, 2.9) * mm, "end": v(64.95, 6) * mm});
            skLineSegment(sketch, "E1713", {"start": v(64.95, 6) * mm, "end": v(64.15, 6) * mm});
            skLineSegment(sketch, "E1714", {"start": v(64.15, 6) * mm, "end": v(64.15, 7) * mm});
            skLineSegment(sketch, "E1715", {"start": v(64.15, 7) * mm, "end": v(50.15, 7) * mm});
            skLineSegment(sketch, "E1716", {"start": v(69.2, 7) * mm, "end": v(69.2, 6) * mm});
            skLineSegment(sketch, "E1717", {"start": v(69.2, 6) * mm, "end": v(68.4, 6) * mm});
            skLineSegment(sketch, "E1718", {"start": v(68.4, 6) * mm, "end": v(68.4, 2.9) * mm});
            skLineSegment(sketch, "E1719", {"start": v(68.4, 2.9) * mm, "end": v(69.2, 2.9) * mm});
            skLineSegment(sketch, "E1720", {"start": v(69.2, 2.9) * mm, "end": v(69.2, -2.9) * mm});
            skLineSegment(sketch, "E1721", {"start": v(69.2, -2.9) * mm, "end": v(68.4, -2.9) * mm});
            skLineSegment(sketch, "E1722", {"start": v(68.4, -2.9) * mm, "end": v(68.4, -6) * mm});
            skLineSegment(sketch, "E1723", {"start": v(68.4, -6) * mm, "end": v(69.2, -6) * mm});
            skLineSegment(sketch, "E1724", {"start": v(69.2, -6) * mm, "end": v(69.2, -7) * mm});
            skLineSegment(sketch, "E1725", {"start": v(69.2, -7) * mm, "end": v(83.2, -7) * mm});
            skLineSegment(sketch, "E1726", {"start": v(83.2, -7) * mm, "end": v(83.2, -6) * mm});
            skLineSegment(sketch, "E1727", {"start": v(83.2, -6) * mm, "end": v(84, -6) * mm});
            skLineSegment(sketch, "E1728", {"start": v(84, -6) * mm, "end": v(84, -2.9) * mm});
            skLineSegment(sketch, "E1729", {"start": v(84, -2.9) * mm, "end": v(83.2, -2.9) * mm});
            skLineSegment(sketch, "E1730", {"start": v(83.2, -2.9) * mm, "end": v(83.2, 2.9) * mm});
            skLineSegment(sketch, "E1731", {"start": v(83.2, 2.9) * mm, "end": v(84, 2.9) * mm});
            skLineSegment(sketch, "E1732", {"start": v(84, 2.9) * mm, "end": v(84, 6) * mm});
            skLineSegment(sketch, "E1733", {"start": v(84, 6) * mm, "end": v(83.2, 6) * mm});
            skLineSegment(sketch, "E1734", {"start": v(83.2, 6) * mm, "end": v(83.2, 7) * mm});
            skLineSegment(sketch, "E1735", {"start": v(83.2, 7) * mm, "end": v(69.2, 7) * mm});
            skLineSegment(sketch, "E1736", {"start": v(-149.88, 26.05) * mm, "end": v(-149.88, 25.05) * mm});
            skLineSegment(sketch, "E1737", {"start": v(-149.88, 25.05) * mm, "end": v(-150.68, 25.05) * mm});
            skLineSegment(sketch, "E1738", {"start": v(-150.68, 25.05) * mm, "end": v(-150.68, 21.95) * mm});
            skLineSegment(sketch, "E1739", {"start": v(-150.68, 21.95) * mm, "end": v(-149.88, 21.95) * mm});
            skLineSegment(sketch, "E1740", {"start": v(-149.88, 21.95) * mm, "end": v(-149.88, 16.15) * mm});
            skLineSegment(sketch, "E1741", {"start": v(-149.88, 16.15) * mm, "end": v(-150.68, 16.15) * mm});
            skLineSegment(sketch, "E1742", {"start": v(-150.68, 16.15) * mm, "end": v(-150.68, 13.05) * mm});
            skLineSegment(sketch, "E1743", {"start": v(-150.68, 13.05) * mm, "end": v(-149.88, 13.05) * mm});
            skLineSegment(sketch, "E1744", {"start": v(-149.88, 13.05) * mm, "end": v(-149.88, 12.05) * mm});
            skLineSegment(sketch, "E1745", {"start": v(-149.88, 12.05) * mm, "end": v(-135.88, 12.05) * mm});
            skLineSegment(sketch, "E1746", {"start": v(-135.88, 12.05) * mm, "end": v(-135.88, 13.05) * mm});
            skLineSegment(sketch, "E1747", {"start": v(-135.88, 13.05) * mm, "end": v(-135.08, 13.05) * mm});
            skLineSegment(sketch, "E1748", {"start": v(-135.08, 13.05) * mm, "end": v(-135.08, 16.15) * mm});
            skLineSegment(sketch, "E1749", {"start": v(-135.08, 16.15) * mm, "end": v(-135.88, 16.15) * mm});
            skLineSegment(sketch, "E1750", {"start": v(-135.88, 16.15) * mm, "end": v(-135.88, 21.95) * mm});
            skLineSegment(sketch, "E1751", {"start": v(-135.88, 21.95) * mm, "end": v(-135.08, 21.95) * mm});
            skLineSegment(sketch, "E1752", {"start": v(-135.08, 21.95) * mm, "end": v(-135.08, 25.05) * mm});
            skLineSegment(sketch, "E1753", {"start": v(-135.08, 25.05) * mm, "end": v(-135.88, 25.05) * mm});
            skLineSegment(sketch, "E1754", {"start": v(-135.88, 25.05) * mm, "end": v(-135.88, 26.05) * mm});
            skLineSegment(sketch, "E1755", {"start": v(-135.88, 26.05) * mm, "end": v(-149.88, 26.05) * mm});
            skLineSegment(sketch, "E1756", {"start": v(-126.06, 26.05) * mm, "end": v(-126.06, 25.05) * mm});
            skLineSegment(sketch, "E1757", {"start": v(-126.06, 25.05) * mm, "end": v(-126.86, 25.05) * mm});
            skLineSegment(sketch, "E1758", {"start": v(-126.86, 25.05) * mm, "end": v(-126.86, 21.95) * mm});
            skLineSegment(sketch, "E1759", {"start": v(-126.86, 21.95) * mm, "end": v(-126.06, 21.95) * mm});
            skLineSegment(sketch, "E1760", {"start": v(-126.06, 21.95) * mm, "end": v(-126.06, 16.15) * mm});
            skLineSegment(sketch, "E1761", {"start": v(-126.06, 16.15) * mm, "end": v(-126.86, 16.15) * mm});
            skLineSegment(sketch, "E1762", {"start": v(-126.86, 16.15) * mm, "end": v(-126.86, 13.05) * mm});
            skLineSegment(sketch, "E1763", {"start": v(-126.86, 13.05) * mm, "end": v(-126.06, 13.05) * mm});
            skLineSegment(sketch, "E1764", {"start": v(-126.06, 13.05) * mm, "end": v(-126.06, 12.05) * mm});
            skLineSegment(sketch, "E1765", {"start": v(-126.06, 12.05) * mm, "end": v(-112.06, 12.05) * mm});
            skLineSegment(sketch, "E1766", {"start": v(-112.06, 12.05) * mm, "end": v(-112.06, 13.05) * mm});
            skLineSegment(sketch, "E1767", {"start": v(-112.06, 13.05) * mm, "end": v(-111.26, 13.05) * mm});
            skLineSegment(sketch, "E1768", {"start": v(-111.26, 13.05) * mm, "end": v(-111.26, 16.15) * mm});
            skLineSegment(sketch, "E1769", {"start": v(-111.26, 16.15) * mm, "end": v(-112.06, 16.15) * mm});
            skLineSegment(sketch, "E1770", {"start": v(-112.06, 16.15) * mm, "end": v(-112.06, 21.95) * mm});
            skLineSegment(sketch, "E1771", {"start": v(-112.06, 21.95) * mm, "end": v(-111.26, 21.95) * mm});
            skLineSegment(sketch, "E1772", {"start": v(-111.26, 21.95) * mm, "end": v(-111.26, 25.05) * mm});
            skLineSegment(sketch, "E1773", {"start": v(-111.26, 25.05) * mm, "end": v(-112.06, 25.05) * mm});
            skLineSegment(sketch, "E1774", {"start": v(-112.06, 25.05) * mm, "end": v(-112.06, 26.05) * mm});
            skLineSegment(sketch, "E1775", {"start": v(-112.06, 26.05) * mm, "end": v(-126.06, 26.05) * mm});
            skLineSegment(sketch, "E1776", {"start": v(-107.01, 26.05) * mm, "end": v(-107.01, 25.05) * mm});
            skLineSegment(sketch, "E1777", {"start": v(-107.01, 25.05) * mm, "end": v(-107.81, 25.05) * mm});
            skLineSegment(sketch, "E1778", {"start": v(-107.81, 25.05) * mm, "end": v(-107.81, 21.95) * mm});
            skLineSegment(sketch, "E1779", {"start": v(-107.81, 21.95) * mm, "end": v(-107.01, 21.95) * mm});
            skLineSegment(sketch, "E1780", {"start": v(-107.01, 21.95) * mm, "end": v(-107.01, 16.15) * mm});
            skLineSegment(sketch, "E1781", {"start": v(-107.01, 16.15) * mm, "end": v(-107.81, 16.15) * mm});
            skLineSegment(sketch, "E1782", {"start": v(-107.81, 16.15) * mm, "end": v(-107.81, 13.05) * mm});
            skLineSegment(sketch, "E1783", {"start": v(-107.81, 13.05) * mm, "end": v(-107.01, 13.05) * mm});
            skLineSegment(sketch, "E1784", {"start": v(-107.01, 13.05) * mm, "end": v(-107.01, 12.05) * mm});
            skLineSegment(sketch, "E1785", {"start": v(-107.01, 12.05) * mm, "end": v(-93.01, 12.05) * mm});
            skLineSegment(sketch, "E1786", {"start": v(-93.01, 12.05) * mm, "end": v(-93.01, 13.05) * mm});
            skLineSegment(sketch, "E1787", {"start": v(-93.01, 13.05) * mm, "end": v(-92.21, 13.05) * mm});
            skLineSegment(sketch, "E1788", {"start": v(-92.21, 13.05) * mm, "end": v(-92.21, 16.15) * mm});
            skLineSegment(sketch, "E1789", {"start": v(-92.21, 16.15) * mm, "end": v(-93.01, 16.15) * mm});
            skLineSegment(sketch, "E1790", {"start": v(-93.01, 16.15) * mm, "end": v(-93.01, 21.95) * mm});
            skLineSegment(sketch, "E1791", {"start": v(-93.01, 21.95) * mm, "end": v(-92.21, 21.95) * mm});
            skLineSegment(sketch, "E1792", {"start": v(-92.21, 21.95) * mm, "end": v(-92.21, 25.05) * mm});
            skLineSegment(sketch, "E1793", {"start": v(-92.21, 25.05) * mm, "end": v(-93.01, 25.05) * mm});
            skLineSegment(sketch, "E1794", {"start": v(-93.01, 25.05) * mm, "end": v(-93.01, 26.05) * mm});
            skLineSegment(sketch, "E1795", {"start": v(-93.01, 26.05) * mm, "end": v(-107.01, 26.05) * mm});
            skLineSegment(sketch, "E1796", {"start": v(-87.96, 26.05) * mm, "end": v(-87.96, 25.05) * mm});
            skLineSegment(sketch, "E1797", {"start": v(-87.96, 25.05) * mm, "end": v(-88.76, 25.05) * mm});
            skLineSegment(sketch, "E1798", {"start": v(-88.76, 25.05) * mm, "end": v(-88.76, 21.95) * mm});
            skLineSegment(sketch, "E1799", {"start": v(-88.76, 21.95) * mm, "end": v(-87.96, 21.95) * mm});
            skLineSegment(sketch, "E1800", {"start": v(-87.96, 21.95) * mm, "end": v(-87.96, 16.15) * mm});
            skLineSegment(sketch, "E1801", {"start": v(-87.96, 16.15) * mm, "end": v(-88.76, 16.15) * mm});
            skLineSegment(sketch, "E1802", {"start": v(-88.76, 16.15) * mm, "end": v(-88.76, 13.05) * mm});
            skLineSegment(sketch, "E1803", {"start": v(-88.76, 13.05) * mm, "end": v(-87.96, 13.05) * mm});
            skLineSegment(sketch, "E1804", {"start": v(-87.96, 13.05) * mm, "end": v(-87.96, 12.05) * mm});
            skLineSegment(sketch, "E1805", {"start": v(-87.96, 12.05) * mm, "end": v(-73.96, 12.05) * mm});
            skLineSegment(sketch, "E1806", {"start": v(-73.96, 12.05) * mm, "end": v(-73.96, 13.05) * mm});
            skLineSegment(sketch, "E1807", {"start": v(-73.96, 13.05) * mm, "end": v(-73.16, 13.05) * mm});
            skLineSegment(sketch, "E1808", {"start": v(-73.16, 13.05) * mm, "end": v(-73.16, 16.15) * mm});
            skLineSegment(sketch, "E1809", {"start": v(-73.16, 16.15) * mm, "end": v(-73.96, 16.15) * mm});
            skLineSegment(sketch, "E1810", {"start": v(-73.96, 16.15) * mm, "end": v(-73.96, 21.95) * mm});
            skLineSegment(sketch, "E1811", {"start": v(-73.96, 21.95) * mm, "end": v(-73.16, 21.95) * mm});
            skLineSegment(sketch, "E1812", {"start": v(-73.16, 21.95) * mm, "end": v(-73.16, 25.05) * mm});
            skLineSegment(sketch, "E1813", {"start": v(-73.16, 25.05) * mm, "end": v(-73.96, 25.05) * mm});
            skLineSegment(sketch, "E1814", {"start": v(-73.96, 25.05) * mm, "end": v(-73.96, 26.05) * mm});
            skLineSegment(sketch, "E1815", {"start": v(-73.96, 26.05) * mm, "end": v(-87.96, 26.05) * mm});
            skLineSegment(sketch, "E1816", {"start": v(-68.91, 26.05) * mm, "end": v(-68.91, 25.05) * mm});
            skLineSegment(sketch, "E1817", {"start": v(-68.91, 25.05) * mm, "end": v(-69.71, 25.05) * mm});
            skLineSegment(sketch, "E1818", {"start": v(-69.71, 25.05) * mm, "end": v(-69.71, 21.95) * mm});
            skLineSegment(sketch, "E1819", {"start": v(-69.71, 21.95) * mm, "end": v(-68.91, 21.95) * mm});
            skLineSegment(sketch, "E1820", {"start": v(-68.91, 21.95) * mm, "end": v(-68.91, 16.15) * mm});
            skLineSegment(sketch, "E1821", {"start": v(-68.91, 16.15) * mm, "end": v(-69.71, 16.15) * mm});
            skLineSegment(sketch, "E1822", {"start": v(-69.71, 16.15) * mm, "end": v(-69.71, 13.05) * mm});
            skLineSegment(sketch, "E1823", {"start": v(-69.71, 13.05) * mm, "end": v(-68.91, 13.05) * mm});
            skLineSegment(sketch, "E1824", {"start": v(-68.91, 13.05) * mm, "end": v(-68.91, 12.05) * mm});
            skLineSegment(sketch, "E1825", {"start": v(-68.91, 12.05) * mm, "end": v(-54.91, 12.05) * mm});
            skLineSegment(sketch, "E1826", {"start": v(-54.91, 12.05) * mm, "end": v(-54.91, 13.05) * mm});
            skLineSegment(sketch, "E1827", {"start": v(-54.91, 13.05) * mm, "end": v(-54.11, 13.05) * mm});
            skLineSegment(sketch, "E1828", {"start": v(-54.11, 13.05) * mm, "end": v(-54.11, 16.15) * mm});
            skLineSegment(sketch, "E1829", {"start": v(-54.11, 16.15) * mm, "end": v(-54.91, 16.15) * mm});
            skLineSegment(sketch, "E1830", {"start": v(-54.91, 16.15) * mm, "end": v(-54.91, 21.95) * mm});
            skLineSegment(sketch, "E1831", {"start": v(-54.91, 21.95) * mm, "end": v(-54.11, 21.95) * mm});
            skLineSegment(sketch, "E1832", {"start": v(-54.11, 21.95) * mm, "end": v(-54.11, 25.05) * mm});
            skLineSegment(sketch, "E1833", {"start": v(-54.11, 25.05) * mm, "end": v(-54.91, 25.05) * mm});
            skLineSegment(sketch, "E1834", {"start": v(-54.91, 25.05) * mm, "end": v(-54.91, 26.05) * mm});
            skLineSegment(sketch, "E1835", {"start": v(-54.91, 26.05) * mm, "end": v(-68.91, 26.05) * mm});
            skLineSegment(sketch, "E1836", {"start": v(-49.86, 26.05) * mm, "end": v(-49.86, 25.05) * mm});
            skLineSegment(sketch, "E1837", {"start": v(-49.86, 25.05) * mm, "end": v(-50.66, 25.05) * mm});
            skLineSegment(sketch, "E1838", {"start": v(-50.66, 25.05) * mm, "end": v(-50.66, 21.95) * mm});
            skLineSegment(sketch, "E1839", {"start": v(-50.66, 21.95) * mm, "end": v(-49.86, 21.95) * mm});
            skLineSegment(sketch, "E1840", {"start": v(-49.86, 21.95) * mm, "end": v(-49.86, 16.15) * mm});
            skLineSegment(sketch, "E1841", {"start": v(-49.86, 16.15) * mm, "end": v(-50.66, 16.15) * mm});
            skLineSegment(sketch, "E1842", {"start": v(-50.66, 16.15) * mm, "end": v(-50.66, 13.05) * mm});
            skLineSegment(sketch, "E1843", {"start": v(-50.66, 13.05) * mm, "end": v(-49.86, 13.05) * mm});
            skLineSegment(sketch, "E1844", {"start": v(-49.86, 13.05) * mm, "end": v(-49.86, 12.05) * mm});
            skLineSegment(sketch, "E1845", {"start": v(-49.86, 12.05) * mm, "end": v(-35.86, 12.05) * mm});
            skLineSegment(sketch, "E1846", {"start": v(-35.86, 12.05) * mm, "end": v(-35.86, 13.05) * mm});
            skLineSegment(sketch, "E1847", {"start": v(-35.86, 13.05) * mm, "end": v(-35.06, 13.05) * mm});
            skLineSegment(sketch, "E1848", {"start": v(-35.06, 13.05) * mm, "end": v(-35.06, 16.15) * mm});
            skLineSegment(sketch, "E1849", {"start": v(-35.06, 16.15) * mm, "end": v(-35.86, 16.15) * mm});
            skLineSegment(sketch, "E1850", {"start": v(-35.86, 16.15) * mm, "end": v(-35.86, 21.95) * mm});
            skLineSegment(sketch, "E1851", {"start": v(-35.86, 21.95) * mm, "end": v(-35.06, 21.95) * mm});
            skLineSegment(sketch, "E1852", {"start": v(-35.06, 21.95) * mm, "end": v(-35.06, 25.05) * mm});
            skLineSegment(sketch, "E1853", {"start": v(-35.06, 25.05) * mm, "end": v(-35.86, 25.05) * mm});
            skLineSegment(sketch, "E1854", {"start": v(-35.86, 25.05) * mm, "end": v(-35.86, 26.05) * mm});
            skLineSegment(sketch, "E1855", {"start": v(-35.86, 26.05) * mm, "end": v(-49.86, 26.05) * mm});
            skLineSegment(sketch, "E1856", {"start": v(-30.81, 26.05) * mm, "end": v(-30.81, 25.05) * mm});
            skLineSegment(sketch, "E1857", {"start": v(-30.81, 25.05) * mm, "end": v(-31.61, 25.05) * mm});
            skLineSegment(sketch, "E1858", {"start": v(-31.61, 25.05) * mm, "end": v(-31.61, 21.95) * mm});
            skLineSegment(sketch, "E1859", {"start": v(-31.61, 21.95) * mm, "end": v(-30.81, 21.95) * mm});
            skLineSegment(sketch, "E1860", {"start": v(-30.81, 21.95) * mm, "end": v(-30.81, 16.15) * mm});
            skLineSegment(sketch, "E1861", {"start": v(-30.81, 16.15) * mm, "end": v(-31.61, 16.15) * mm});
            skLineSegment(sketch, "E1862", {"start": v(-31.61, 16.15) * mm, "end": v(-31.61, 13.05) * mm});
            skLineSegment(sketch, "E1863", {"start": v(-31.61, 13.05) * mm, "end": v(-30.81, 13.05) * mm});
            skLineSegment(sketch, "E1864", {"start": v(-30.81, 13.05) * mm, "end": v(-30.81, 12.05) * mm});
            skLineSegment(sketch, "E1865", {"start": v(-30.81, 12.05) * mm, "end": v(-16.81, 12.05) * mm});
            skLineSegment(sketch, "E1866", {"start": v(-16.81, 12.05) * mm, "end": v(-16.81, 13.05) * mm});
            skLineSegment(sketch, "E1867", {"start": v(-16.81, 13.05) * mm, "end": v(-16.01, 13.05) * mm});
            skLineSegment(sketch, "E1868", {"start": v(-16.01, 13.05) * mm, "end": v(-16.01, 16.15) * mm});
            skLineSegment(sketch, "E1869", {"start": v(-16.01, 16.15) * mm, "end": v(-16.81, 16.15) * mm});
            skLineSegment(sketch, "E1870", {"start": v(-16.81, 16.15) * mm, "end": v(-16.81, 21.95) * mm});
            skLineSegment(sketch, "E1871", {"start": v(-16.81, 21.95) * mm, "end": v(-16.01, 21.95) * mm});
            skLineSegment(sketch, "E1872", {"start": v(-16.01, 21.95) * mm, "end": v(-16.01, 25.05) * mm});
            skLineSegment(sketch, "E1873", {"start": v(-16.01, 25.05) * mm, "end": v(-16.81, 25.05) * mm});
            skLineSegment(sketch, "E1874", {"start": v(-16.81, 25.05) * mm, "end": v(-16.81, 26.05) * mm});
            skLineSegment(sketch, "E1875", {"start": v(-16.81, 26.05) * mm, "end": v(-30.81, 26.05) * mm});
            skLineSegment(sketch, "E1876", {"start": v(-11.76, 26.05) * mm, "end": v(-11.76, 25.05) * mm});
            skLineSegment(sketch, "E1877", {"start": v(-11.76, 25.05) * mm, "end": v(-12.56, 25.05) * mm});
            skLineSegment(sketch, "E1878", {"start": v(-12.56, 25.05) * mm, "end": v(-12.56, 21.95) * mm});
            skLineSegment(sketch, "E1879", {"start": v(-12.56, 21.95) * mm, "end": v(-11.76, 21.95) * mm});
            skLineSegment(sketch, "E1880", {"start": v(-11.76, 21.95) * mm, "end": v(-11.76, 16.15) * mm});
            skLineSegment(sketch, "E1881", {"start": v(-11.76, 16.15) * mm, "end": v(-12.56, 16.15) * mm});
            skLineSegment(sketch, "E1882", {"start": v(-12.56, 16.15) * mm, "end": v(-12.56, 13.05) * mm});
            skLineSegment(sketch, "E1883", {"start": v(-12.56, 13.05) * mm, "end": v(-11.76, 13.05) * mm});
            skLineSegment(sketch, "E1884", {"start": v(-11.76, 13.05) * mm, "end": v(-11.76, 12.05) * mm});
            skLineSegment(sketch, "E1885", {"start": v(-11.76, 12.05) * mm, "end": v(2.24, 12.05) * mm});
            skLineSegment(sketch, "E1886", {"start": v(2.24, 12.05) * mm, "end": v(2.24, 13.05) * mm});
            skLineSegment(sketch, "E1887", {"start": v(2.24, 13.05) * mm, "end": v(3.04, 13.05) * mm});
            skLineSegment(sketch, "E1888", {"start": v(3.04, 13.05) * mm, "end": v(3.04, 16.15) * mm});
            skLineSegment(sketch, "E1889", {"start": v(3.04, 16.15) * mm, "end": v(2.24, 16.15) * mm});
            skLineSegment(sketch, "E1890", {"start": v(2.24, 16.15) * mm, "end": v(2.24, 21.95) * mm});
            skLineSegment(sketch, "E1891", {"start": v(2.24, 21.95) * mm, "end": v(3.04, 21.95) * mm});
            skLineSegment(sketch, "E1892", {"start": v(3.04, 21.95) * mm, "end": v(3.04, 25.05) * mm});
            skLineSegment(sketch, "E1893", {"start": v(3.04, 25.05) * mm, "end": v(2.24, 25.05) * mm});
            skLineSegment(sketch, "E1894", {"start": v(2.24, 25.05) * mm, "end": v(2.24, 26.05) * mm});
            skLineSegment(sketch, "E1895", {"start": v(2.24, 26.05) * mm, "end": v(-11.76, 26.05) * mm});
            skLineSegment(sketch, "E1896", {"start": v(7.29, 26.05) * mm, "end": v(7.29, 25.05) * mm});
            skLineSegment(sketch, "E1897", {"start": v(7.29, 25.05) * mm, "end": v(6.49, 25.05) * mm});
            skLineSegment(sketch, "E1898", {"start": v(6.49, 25.05) * mm, "end": v(6.49, 21.95) * mm});
            skLineSegment(sketch, "E1899", {"start": v(6.49, 21.95) * mm, "end": v(7.29, 21.95) * mm});
            skLineSegment(sketch, "E1900", {"start": v(7.29, 21.95) * mm, "end": v(7.29, 16.15) * mm});
            skLineSegment(sketch, "E1901", {"start": v(7.29, 16.15) * mm, "end": v(6.49, 16.15) * mm});
            skLineSegment(sketch, "E1902", {"start": v(6.49, 16.15) * mm, "end": v(6.49, 13.05) * mm});
            skLineSegment(sketch, "E1903", {"start": v(6.49, 13.05) * mm, "end": v(7.29, 13.05) * mm});
            skLineSegment(sketch, "E1904", {"start": v(7.29, 13.05) * mm, "end": v(7.29, 12.05) * mm});
            skLineSegment(sketch, "E1905", {"start": v(7.29, 12.05) * mm, "end": v(21.29, 12.05) * mm});
            skLineSegment(sketch, "E1906", {"start": v(21.29, 12.05) * mm, "end": v(21.29, 13.05) * mm});
            skLineSegment(sketch, "E1907", {"start": v(21.29, 13.05) * mm, "end": v(22.09, 13.05) * mm});
            skLineSegment(sketch, "E1908", {"start": v(22.09, 13.05) * mm, "end": v(22.09, 16.15) * mm});
            skLineSegment(sketch, "E1909", {"start": v(22.09, 16.15) * mm, "end": v(21.29, 16.15) * mm});
            skLineSegment(sketch, "E1910", {"start": v(21.29, 16.15) * mm, "end": v(21.29, 21.95) * mm});
            skLineSegment(sketch, "E1911", {"start": v(21.29, 21.95) * mm, "end": v(22.09, 21.95) * mm});
            skLineSegment(sketch, "E1912", {"start": v(22.09, 21.95) * mm, "end": v(22.09, 25.05) * mm});
            skLineSegment(sketch, "E1913", {"start": v(22.09, 25.05) * mm, "end": v(21.29, 25.05) * mm});
            skLineSegment(sketch, "E1914", {"start": v(21.29, 25.05) * mm, "end": v(21.29, 26.05) * mm});
            skLineSegment(sketch, "E1915", {"start": v(21.29, 26.05) * mm, "end": v(7.29, 26.05) * mm});
            skLineSegment(sketch, "E1916", {"start": v(26.34, 26.05) * mm, "end": v(26.34, 25.05) * mm});
            skLineSegment(sketch, "E1917", {"start": v(26.34, 25.05) * mm, "end": v(25.54, 25.05) * mm});
            skLineSegment(sketch, "E1918", {"start": v(25.54, 25.05) * mm, "end": v(25.54, 21.95) * mm});
            skLineSegment(sketch, "E1919", {"start": v(25.54, 21.95) * mm, "end": v(26.34, 21.95) * mm});
            skLineSegment(sketch, "E1920", {"start": v(26.34, 21.95) * mm, "end": v(26.34, 16.15) * mm});
            skLineSegment(sketch, "E1921", {"start": v(26.34, 16.15) * mm, "end": v(25.54, 16.15) * mm});
            skLineSegment(sketch, "E1922", {"start": v(25.54, 16.15) * mm, "end": v(25.54, 13.05) * mm});
            skLineSegment(sketch, "E1923", {"start": v(25.54, 13.05) * mm, "end": v(26.34, 13.05) * mm});
            skLineSegment(sketch, "E1924", {"start": v(26.34, 13.05) * mm, "end": v(26.34, 12.05) * mm});
            skLineSegment(sketch, "E1925", {"start": v(26.34, 12.05) * mm, "end": v(40.34, 12.05) * mm});
            skLineSegment(sketch, "E1926", {"start": v(40.34, 12.05) * mm, "end": v(40.34, 13.05) * mm});
            skLineSegment(sketch, "E1927", {"start": v(40.34, 13.05) * mm, "end": v(41.14, 13.05) * mm});
            skLineSegment(sketch, "E1928", {"start": v(41.14, 13.05) * mm, "end": v(41.14, 16.15) * mm});
            skLineSegment(sketch, "E1929", {"start": v(41.14, 16.15) * mm, "end": v(40.34, 16.15) * mm});
            skLineSegment(sketch, "E1930", {"start": v(40.34, 16.15) * mm, "end": v(40.34, 21.95) * mm});
            skLineSegment(sketch, "E1931", {"start": v(40.34, 21.95) * mm, "end": v(41.14, 21.95) * mm});
            skLineSegment(sketch, "E1932", {"start": v(41.14, 21.95) * mm, "end": v(41.14, 25.05) * mm});
            skLineSegment(sketch, "E1933", {"start": v(41.14, 25.05) * mm, "end": v(40.34, 25.05) * mm});
            skLineSegment(sketch, "E1934", {"start": v(40.34, 25.05) * mm, "end": v(40.34, 26.05) * mm});
            skLineSegment(sketch, "E1935", {"start": v(40.34, 26.05) * mm, "end": v(26.34, 26.05) * mm});
            skLineSegment(sketch, "E1936", {"start": v(45.39, 26.05) * mm, "end": v(45.39, 25.05) * mm});
            skLineSegment(sketch, "E1937", {"start": v(45.39, 25.05) * mm, "end": v(44.59, 25.05) * mm});
            skLineSegment(sketch, "E1938", {"start": v(44.59, 25.05) * mm, "end": v(44.59, 21.95) * mm});
            skLineSegment(sketch, "E1939", {"start": v(44.59, 21.95) * mm, "end": v(45.39, 21.95) * mm});
            skLineSegment(sketch, "E1940", {"start": v(45.39, 21.95) * mm, "end": v(45.39, 16.15) * mm});
            skLineSegment(sketch, "E1941", {"start": v(45.39, 16.15) * mm, "end": v(44.59, 16.15) * mm});
            skLineSegment(sketch, "E1942", {"start": v(44.59, 16.15) * mm, "end": v(44.59, 13.05) * mm});
            skLineSegment(sketch, "E1943", {"start": v(44.59, 13.05) * mm, "end": v(45.39, 13.05) * mm});
            skLineSegment(sketch, "E1944", {"start": v(45.39, 13.05) * mm, "end": v(45.39, 12.05) * mm});
            skLineSegment(sketch, "E1945", {"start": v(45.39, 12.05) * mm, "end": v(59.39, 12.05) * mm});
            skLineSegment(sketch, "E1946", {"start": v(59.39, 12.05) * mm, "end": v(59.39, 13.05) * mm});
            skLineSegment(sketch, "E1947", {"start": v(59.39, 13.05) * mm, "end": v(60.19, 13.05) * mm});
            skLineSegment(sketch, "E1948", {"start": v(60.19, 13.05) * mm, "end": v(60.19, 16.15) * mm});
            skLineSegment(sketch, "E1949", {"start": v(60.19, 16.15) * mm, "end": v(59.39, 16.15) * mm});
            skLineSegment(sketch, "E1950", {"start": v(59.39, 16.15) * mm, "end": v(59.39, 21.95) * mm});
            skLineSegment(sketch, "E1951", {"start": v(59.39, 21.95) * mm, "end": v(60.19, 21.95) * mm});
            skLineSegment(sketch, "E1952", {"start": v(60.19, 21.95) * mm, "end": v(60.19, 25.05) * mm});
            skLineSegment(sketch, "E1953", {"start": v(60.19, 25.05) * mm, "end": v(59.39, 25.05) * mm});
            skLineSegment(sketch, "E1954", {"start": v(59.39, 25.05) * mm, "end": v(59.39, 26.05) * mm});
            skLineSegment(sketch, "E1955", {"start": v(59.39, 26.05) * mm, "end": v(45.39, 26.05) * mm});
            skLineSegment(sketch, "E1956", {"start": v(64.44, 26.05) * mm, "end": v(64.44, 25.05) * mm});
            skLineSegment(sketch, "E1957", {"start": v(64.44, 25.05) * mm, "end": v(63.64, 25.05) * mm});
            skLineSegment(sketch, "E1958", {"start": v(63.64, 25.05) * mm, "end": v(63.64, 21.95) * mm});
            skLineSegment(sketch, "E1959", {"start": v(63.64, 21.95) * mm, "end": v(64.44, 21.95) * mm});
            skLineSegment(sketch, "E1960", {"start": v(64.44, 21.95) * mm, "end": v(64.44, 16.15) * mm});
            skLineSegment(sketch, "E1961", {"start": v(64.44, 16.15) * mm, "end": v(63.64, 16.15) * mm});
            skLineSegment(sketch, "E1962", {"start": v(63.64, 16.15) * mm, "end": v(63.64, 13.05) * mm});
            skLineSegment(sketch, "E1963", {"start": v(63.64, 13.05) * mm, "end": v(64.44, 13.05) * mm});
            skLineSegment(sketch, "E1964", {"start": v(64.44, 13.05) * mm, "end": v(64.44, 12.05) * mm});
            skLineSegment(sketch, "E1965", {"start": v(64.44, 12.05) * mm, "end": v(78.44, 12.05) * mm});
            skLineSegment(sketch, "E1966", {"start": v(78.44, 12.05) * mm, "end": v(78.44, 13.05) * mm});
            skLineSegment(sketch, "E1967", {"start": v(78.44, 13.05) * mm, "end": v(79.24, 13.05) * mm});
            skLineSegment(sketch, "E1968", {"start": v(79.24, 13.05) * mm, "end": v(79.24, 16.15) * mm});
            skLineSegment(sketch, "E1969", {"start": v(79.24, 16.15) * mm, "end": v(78.44, 16.15) * mm});
            skLineSegment(sketch, "E1970", {"start": v(78.44, 16.15) * mm, "end": v(78.44, 21.95) * mm});
            skLineSegment(sketch, "E1971", {"start": v(78.44, 21.95) * mm, "end": v(79.24, 21.95) * mm});
            skLineSegment(sketch, "E1972", {"start": v(79.24, 21.95) * mm, "end": v(79.24, 25.05) * mm});
            skLineSegment(sketch, "E1973", {"start": v(79.24, 25.05) * mm, "end": v(78.44, 25.05) * mm});
            skLineSegment(sketch, "E1974", {"start": v(78.44, 25.05) * mm, "end": v(78.44, 26.05) * mm});
            skLineSegment(sketch, "E1975", {"start": v(78.44, 26.05) * mm, "end": v(64.44, 26.05) * mm});
            skLineSegment(sketch, "E1976", {"start": v(83.49, 26.05) * mm, "end": v(83.49, 25.05) * mm});
            skLineSegment(sketch, "E1977", {"start": v(83.49, 25.05) * mm, "end": v(82.69, 25.05) * mm});
            skLineSegment(sketch, "E1978", {"start": v(82.69, 25.05) * mm, "end": v(82.69, 21.95) * mm});
            skLineSegment(sketch, "E1979", {"start": v(82.69, 21.95) * mm, "end": v(83.49, 21.95) * mm});
            skLineSegment(sketch, "E1980", {"start": v(83.49, 21.95) * mm, "end": v(83.49, 16.15) * mm});
            skLineSegment(sketch, "E1981", {"start": v(83.49, 16.15) * mm, "end": v(82.69, 16.15) * mm});
            skLineSegment(sketch, "E1982", {"start": v(82.69, 16.15) * mm, "end": v(82.69, 13.05) * mm});
            skLineSegment(sketch, "E1983", {"start": v(82.69, 13.05) * mm, "end": v(83.49, 13.05) * mm});
            skLineSegment(sketch, "E1984", {"start": v(83.49, 13.05) * mm, "end": v(83.49, 12.05) * mm});
            skLineSegment(sketch, "E1985", {"start": v(83.49, 12.05) * mm, "end": v(97.49, 12.05) * mm});
            skLineSegment(sketch, "E1986", {"start": v(97.49, 12.05) * mm, "end": v(97.49, 13.05) * mm});
            skLineSegment(sketch, "E1987", {"start": v(97.49, 13.05) * mm, "end": v(98.29, 13.05) * mm});
            skLineSegment(sketch, "E1988", {"start": v(98.29, 13.05) * mm, "end": v(98.29, 16.15) * mm});
            skLineSegment(sketch, "E1989", {"start": v(98.29, 16.15) * mm, "end": v(97.49, 16.15) * mm});
            skLineSegment(sketch, "E1990", {"start": v(97.49, 16.15) * mm, "end": v(97.49, 21.95) * mm});
            skLineSegment(sketch, "E1991", {"start": v(97.49, 21.95) * mm, "end": v(98.29, 21.95) * mm});
            skLineSegment(sketch, "E1992", {"start": v(98.29, 21.95) * mm, "end": v(98.29, 25.05) * mm});
            skLineSegment(sketch, "E1993", {"start": v(98.29, 25.05) * mm, "end": v(97.49, 25.05) * mm});
            skLineSegment(sketch, "E1994", {"start": v(97.49, 25.05) * mm, "end": v(97.49, 26.05) * mm});
            skLineSegment(sketch, "E1995", {"start": v(97.49, 26.05) * mm, "end": v(83.49, 26.05) * mm});
            skLineSegment(sketch, "E1996", {"start": v(107.3, 26.05) * mm, "end": v(107.3, 25.05) * mm});
            skLineSegment(sketch, "E1997", {"start": v(107.3, 25.05) * mm, "end": v(106.5, 25.05) * mm});
            skLineSegment(sketch, "E1998", {"start": v(106.5, 25.05) * mm, "end": v(106.5, 21.95) * mm});
            skLineSegment(sketch, "E1999", {"start": v(106.5, 21.95) * mm, "end": v(107.3, 21.95) * mm});
            skLineSegment(sketch, "E2000", {"start": v(107.3, 21.95) * mm, "end": v(107.3, 16.15) * mm});
            skLineSegment(sketch, "E2001", {"start": v(107.3, 16.15) * mm, "end": v(106.5, 16.15) * mm});
            skLineSegment(sketch, "E2002", {"start": v(106.5, 16.15) * mm, "end": v(106.5, 13.05) * mm});
            skLineSegment(sketch, "E2003", {"start": v(106.5, 13.05) * mm, "end": v(107.3, 13.05) * mm});
            skLineSegment(sketch, "E2004", {"start": v(107.3, 13.05) * mm, "end": v(107.3, 12.05) * mm});
            skLineSegment(sketch, "E2005", {"start": v(107.3, 12.05) * mm, "end": v(121.3, 12.05) * mm});
            skLineSegment(sketch, "E2006", {"start": v(121.3, 12.05) * mm, "end": v(121.3, 13.05) * mm});
            skLineSegment(sketch, "E2007", {"start": v(121.3, 13.05) * mm, "end": v(122.1, 13.05) * mm});
            skLineSegment(sketch, "E2008", {"start": v(122.1, 13.05) * mm, "end": v(122.1, 16.15) * mm});
            skLineSegment(sketch, "E2009", {"start": v(122.1, 16.15) * mm, "end": v(121.3, 16.15) * mm});
            skLineSegment(sketch, "E2010", {"start": v(121.3, 16.15) * mm, "end": v(121.3, 21.95) * mm});
            skLineSegment(sketch, "E2011", {"start": v(121.3, 21.95) * mm, "end": v(122.1, 21.95) * mm});
            skLineSegment(sketch, "E2012", {"start": v(122.1, 21.95) * mm, "end": v(122.1, 25.05) * mm});
            skLineSegment(sketch, "E2013", {"start": v(122.1, 25.05) * mm, "end": v(121.3, 25.05) * mm});
            skLineSegment(sketch, "E2014", {"start": v(121.3, 25.05) * mm, "end": v(121.3, 26.05) * mm});
            skLineSegment(sketch, "E2015", {"start": v(121.3, 26.05) * mm, "end": v(107.3, 26.05) * mm});
            skLineSegment(sketch, "E2016", {"start": v(140.64, 26.05) * mm, "end": v(140.64, 25.05) * mm});
            skLineSegment(sketch, "E2017", {"start": v(140.64, 25.05) * mm, "end": v(139.84, 25.05) * mm});
            skLineSegment(sketch, "E2018", {"start": v(139.84, 25.05) * mm, "end": v(139.84, 21.95) * mm});
            skLineSegment(sketch, "E2019", {"start": v(139.84, 21.95) * mm, "end": v(140.64, 21.95) * mm});
            skLineSegment(sketch, "E2020", {"start": v(140.64, 21.95) * mm, "end": v(140.64, 16.15) * mm});
            skLineSegment(sketch, "E2021", {"start": v(140.64, 16.15) * mm, "end": v(139.84, 16.15) * mm});
            skLineSegment(sketch, "E2022", {"start": v(139.84, 16.15) * mm, "end": v(139.84, 13.05) * mm});
            skLineSegment(sketch, "E2023", {"start": v(139.84, 13.05) * mm, "end": v(140.64, 13.05) * mm});
            skLineSegment(sketch, "E2024", {"start": v(140.64, 13.05) * mm, "end": v(140.64, 12.05) * mm});
            skLineSegment(sketch, "E2025", {"start": v(140.64, 12.05) * mm, "end": v(154.64, 12.05) * mm});
            skLineSegment(sketch, "E2026", {"start": v(154.64, 12.05) * mm, "end": v(154.64, 13.05) * mm});
            skLineSegment(sketch, "E2027", {"start": v(154.64, 13.05) * mm, "end": v(155.44, 13.05) * mm});
            skLineSegment(sketch, "E2028", {"start": v(155.44, 13.05) * mm, "end": v(155.44, 16.15) * mm});
            skLineSegment(sketch, "E2029", {"start": v(155.44, 16.15) * mm, "end": v(154.64, 16.15) * mm});
            skLineSegment(sketch, "E2030", {"start": v(154.64, 16.15) * mm, "end": v(154.64, 21.95) * mm});
            skLineSegment(sketch, "E2031", {"start": v(154.64, 21.95) * mm, "end": v(155.44, 21.95) * mm});
            skLineSegment(sketch, "E2032", {"start": v(155.44, 21.95) * mm, "end": v(155.44, 25.05) * mm});
            skLineSegment(sketch, "E2033", {"start": v(155.44, 25.05) * mm, "end": v(154.64, 25.05) * mm});
            skLineSegment(sketch, "E2034", {"start": v(154.64, 25.05) * mm, "end": v(154.64, 26.05) * mm});
            skLineSegment(sketch, "E2035", {"start": v(154.64, 26.05) * mm, "end": v(140.64, 26.05) * mm});
            skLineSegment(sketch, "E2036", {"start": v(-154.64, 45.1) * mm, "end": v(-154.64, 44.1) * mm});
            skLineSegment(sketch, "E2037", {"start": v(-154.64, 44.1) * mm, "end": v(-155.44, 44.1) * mm});
            skLineSegment(sketch, "E2038", {"start": v(-155.44, 44.1) * mm, "end": v(-155.44, 41) * mm});
            skLineSegment(sketch, "E2039", {"start": v(-155.44, 41) * mm, "end": v(-154.64, 41) * mm});
            skLineSegment(sketch, "E2040", {"start": v(-154.64, 41) * mm, "end": v(-154.64, 35.2) * mm});
            skLineSegment(sketch, "E2041", {"start": v(-154.64, 35.2) * mm, "end": v(-155.44, 35.2) * mm});
            skLineSegment(sketch, "E2042", {"start": v(-155.44, 35.2) * mm, "end": v(-155.44, 32.1) * mm});
            skLineSegment(sketch, "E2043", {"start": v(-155.44, 32.1) * mm, "end": v(-154.64, 32.1) * mm});
            skLineSegment(sketch, "E2044", {"start": v(-154.64, 32.1) * mm, "end": v(-154.64, 31.1) * mm});
            skLineSegment(sketch, "E2045", {"start": v(-154.64, 31.1) * mm, "end": v(-140.64, 31.1) * mm});
            skLineSegment(sketch, "E2046", {"start": v(-140.64, 31.1) * mm, "end": v(-140.64, 32.1) * mm});
            skLineSegment(sketch, "E2047", {"start": v(-140.64, 32.1) * mm, "end": v(-139.84, 32.1) * mm});
            skLineSegment(sketch, "E2048", {"start": v(-139.84, 32.1) * mm, "end": v(-139.84, 35.2) * mm});
            skLineSegment(sketch, "E2049", {"start": v(-139.84, 35.2) * mm, "end": v(-140.64, 35.2) * mm});
            skLineSegment(sketch, "E2050", {"start": v(-140.64, 35.2) * mm, "end": v(-140.64, 41) * mm});
            skLineSegment(sketch, "E2051", {"start": v(-140.64, 41) * mm, "end": v(-139.84, 41) * mm});
            skLineSegment(sketch, "E2052", {"start": v(-139.84, 41) * mm, "end": v(-139.84, 44.1) * mm});
            skLineSegment(sketch, "E2053", {"start": v(-139.84, 44.1) * mm, "end": v(-140.64, 44.1) * mm});
            skLineSegment(sketch, "E2054", {"start": v(-140.64, 44.1) * mm, "end": v(-140.64, 45.1) * mm});
            skLineSegment(sketch, "E2055", {"start": v(-140.64, 45.1) * mm, "end": v(-154.64, 45.1) * mm});
            skLineSegment(sketch, "E2056", {"start": v(-135.59, 45.1) * mm, "end": v(-135.59, 44.1) * mm});
            skLineSegment(sketch, "E2057", {"start": v(-135.59, 44.1) * mm, "end": v(-136.39, 44.1) * mm});
            skLineSegment(sketch, "E2058", {"start": v(-136.39, 44.1) * mm, "end": v(-136.39, 41) * mm});
            skLineSegment(sketch, "E2059", {"start": v(-136.39, 41) * mm, "end": v(-135.59, 41) * mm});
            skLineSegment(sketch, "E2060", {"start": v(-135.59, 41) * mm, "end": v(-135.59, 35.2) * mm});
            skLineSegment(sketch, "E2061", {"start": v(-135.59, 35.2) * mm, "end": v(-136.39, 35.2) * mm});
            skLineSegment(sketch, "E2062", {"start": v(-136.39, 35.2) * mm, "end": v(-136.39, 32.1) * mm});
            skLineSegment(sketch, "E2063", {"start": v(-136.39, 32.1) * mm, "end": v(-135.59, 32.1) * mm});
            skLineSegment(sketch, "E2064", {"start": v(-135.59, 32.1) * mm, "end": v(-135.59, 31.1) * mm});
            skLineSegment(sketch, "E2065", {"start": v(-135.59, 31.1) * mm, "end": v(-121.59, 31.1) * mm});
            skLineSegment(sketch, "E2066", {"start": v(-121.59, 31.1) * mm, "end": v(-121.59, 32.1) * mm});
            skLineSegment(sketch, "E2067", {"start": v(-121.59, 32.1) * mm, "end": v(-120.79, 32.1) * mm});
            skLineSegment(sketch, "E2068", {"start": v(-120.79, 32.1) * mm, "end": v(-120.79, 35.2) * mm});
            skLineSegment(sketch, "E2069", {"start": v(-120.79, 35.2) * mm, "end": v(-121.59, 35.2) * mm});
            skLineSegment(sketch, "E2070", {"start": v(-121.59, 35.2) * mm, "end": v(-121.59, 41) * mm});
            skLineSegment(sketch, "E2071", {"start": v(-121.59, 41) * mm, "end": v(-120.79, 41) * mm});
            skLineSegment(sketch, "E2072", {"start": v(-120.79, 41) * mm, "end": v(-120.79, 44.1) * mm});
            skLineSegment(sketch, "E2073", {"start": v(-120.79, 44.1) * mm, "end": v(-121.59, 44.1) * mm});
            skLineSegment(sketch, "E2074", {"start": v(-121.59, 44.1) * mm, "end": v(-121.59, 45.1) * mm});
            skLineSegment(sketch, "E2075", {"start": v(-121.59, 45.1) * mm, "end": v(-135.59, 45.1) * mm});
            skLineSegment(sketch, "E2076", {"start": v(-116.54, 45.1) * mm, "end": v(-116.54, 44.1) * mm});
            skLineSegment(sketch, "E2077", {"start": v(-116.54, 44.1) * mm, "end": v(-117.34, 44.1) * mm});
            skLineSegment(sketch, "E2078", {"start": v(-117.34, 44.1) * mm, "end": v(-117.34, 41) * mm});
            skLineSegment(sketch, "E2079", {"start": v(-117.34, 41) * mm, "end": v(-116.54, 41) * mm});
            skLineSegment(sketch, "E2080", {"start": v(-116.54, 41) * mm, "end": v(-116.54, 35.2) * mm});
            skLineSegment(sketch, "E2081", {"start": v(-116.54, 35.2) * mm, "end": v(-117.34, 35.2) * mm});
            skLineSegment(sketch, "E2082", {"start": v(-117.34, 35.2) * mm, "end": v(-117.34, 32.1) * mm});
            skLineSegment(sketch, "E2083", {"start": v(-117.34, 32.1) * mm, "end": v(-116.54, 32.1) * mm});
            skLineSegment(sketch, "E2084", {"start": v(-116.54, 32.1) * mm, "end": v(-116.54, 31.1) * mm});
            skLineSegment(sketch, "E2085", {"start": v(-116.54, 31.1) * mm, "end": v(-102.54, 31.1) * mm});
            skLineSegment(sketch, "E2086", {"start": v(-102.54, 31.1) * mm, "end": v(-102.54, 32.1) * mm});
            skLineSegment(sketch, "E2087", {"start": v(-102.54, 32.1) * mm, "end": v(-101.74, 32.1) * mm});
            skLineSegment(sketch, "E2088", {"start": v(-101.74, 32.1) * mm, "end": v(-101.74, 35.2) * mm});
            skLineSegment(sketch, "E2089", {"start": v(-101.74, 35.2) * mm, "end": v(-102.54, 35.2) * mm});
            skLineSegment(sketch, "E2090", {"start": v(-102.54, 35.2) * mm, "end": v(-102.54, 41) * mm});
            skLineSegment(sketch, "E2091", {"start": v(-102.54, 41) * mm, "end": v(-101.74, 41) * mm});
            skLineSegment(sketch, "E2092", {"start": v(-101.74, 41) * mm, "end": v(-101.74, 44.1) * mm});
            skLineSegment(sketch, "E2093", {"start": v(-101.74, 44.1) * mm, "end": v(-102.54, 44.1) * mm});
            skLineSegment(sketch, "E2094", {"start": v(-102.54, 44.1) * mm, "end": v(-102.54, 45.1) * mm});
            skLineSegment(sketch, "E2095", {"start": v(-102.54, 45.1) * mm, "end": v(-116.54, 45.1) * mm});
            skLineSegment(sketch, "E2096", {"start": v(-97.49, 45.1) * mm, "end": v(-97.49, 44.1) * mm});
            skLineSegment(sketch, "E2097", {"start": v(-97.49, 44.1) * mm, "end": v(-98.29, 44.1) * mm});
            skLineSegment(sketch, "E2098", {"start": v(-98.29, 44.1) * mm, "end": v(-98.29, 41) * mm});
            skLineSegment(sketch, "E2099", {"start": v(-98.29, 41) * mm, "end": v(-97.49, 41) * mm});
            skLineSegment(sketch, "E2100", {"start": v(-97.49, 41) * mm, "end": v(-97.49, 35.2) * mm});
            skLineSegment(sketch, "E2101", {"start": v(-97.49, 35.2) * mm, "end": v(-98.29, 35.2) * mm});
            skLineSegment(sketch, "E2102", {"start": v(-98.29, 35.2) * mm, "end": v(-98.29, 32.1) * mm});
            skLineSegment(sketch, "E2103", {"start": v(-98.29, 32.1) * mm, "end": v(-97.49, 32.1) * mm});
            skLineSegment(sketch, "E2104", {"start": v(-97.49, 32.1) * mm, "end": v(-97.49, 31.1) * mm});
            skLineSegment(sketch, "E2105", {"start": v(-97.49, 31.1) * mm, "end": v(-83.49, 31.1) * mm});
            skLineSegment(sketch, "E2106", {"start": v(-83.49, 31.1) * mm, "end": v(-83.49, 32.1) * mm});
            skLineSegment(sketch, "E2107", {"start": v(-83.49, 32.1) * mm, "end": v(-82.69, 32.1) * mm});
            skLineSegment(sketch, "E2108", {"start": v(-82.69, 32.1) * mm, "end": v(-82.69, 35.2) * mm});
            skLineSegment(sketch, "E2109", {"start": v(-82.69, 35.2) * mm, "end": v(-83.49, 35.2) * mm});
            skLineSegment(sketch, "E2110", {"start": v(-83.49, 35.2) * mm, "end": v(-83.49, 41) * mm});
            skLineSegment(sketch, "E2111", {"start": v(-83.49, 41) * mm, "end": v(-82.69, 41) * mm});
            skLineSegment(sketch, "E2112", {"start": v(-82.69, 41) * mm, "end": v(-82.69, 44.1) * mm});
            skLineSegment(sketch, "E2113", {"start": v(-82.69, 44.1) * mm, "end": v(-83.49, 44.1) * mm});
            skLineSegment(sketch, "E2114", {"start": v(-83.49, 44.1) * mm, "end": v(-83.49, 45.1) * mm});
            skLineSegment(sketch, "E2115", {"start": v(-83.49, 45.1) * mm, "end": v(-97.49, 45.1) * mm});
            skLineSegment(sketch, "E2116", {"start": v(-78.44, 45.1) * mm, "end": v(-78.44, 44.1) * mm});
            skLineSegment(sketch, "E2117", {"start": v(-78.44, 44.1) * mm, "end": v(-79.24, 44.1) * mm});
            skLineSegment(sketch, "E2118", {"start": v(-79.24, 44.1) * mm, "end": v(-79.24, 41) * mm});
            skLineSegment(sketch, "E2119", {"start": v(-79.24, 41) * mm, "end": v(-78.44, 41) * mm});
            skLineSegment(sketch, "E2120", {"start": v(-78.44, 41) * mm, "end": v(-78.44, 35.2) * mm});
            skLineSegment(sketch, "E2121", {"start": v(-78.44, 35.2) * mm, "end": v(-79.24, 35.2) * mm});
            skLineSegment(sketch, "E2122", {"start": v(-79.24, 35.2) * mm, "end": v(-79.24, 32.1) * mm});
            skLineSegment(sketch, "E2123", {"start": v(-79.24, 32.1) * mm, "end": v(-78.44, 32.1) * mm});
            skLineSegment(sketch, "E2124", {"start": v(-78.44, 32.1) * mm, "end": v(-78.44, 31.1) * mm});
            skLineSegment(sketch, "E2125", {"start": v(-78.44, 31.1) * mm, "end": v(-64.44, 31.1) * mm});
            skLineSegment(sketch, "E2126", {"start": v(-64.44, 31.1) * mm, "end": v(-64.44, 32.1) * mm});
            skLineSegment(sketch, "E2127", {"start": v(-64.44, 32.1) * mm, "end": v(-63.64, 32.1) * mm});
            skLineSegment(sketch, "E2128", {"start": v(-63.64, 32.1) * mm, "end": v(-63.64, 35.2) * mm});
            skLineSegment(sketch, "E2129", {"start": v(-63.64, 35.2) * mm, "end": v(-64.44, 35.2) * mm});
            skLineSegment(sketch, "E2130", {"start": v(-64.44, 35.2) * mm, "end": v(-64.44, 41) * mm});
            skLineSegment(sketch, "E2131", {"start": v(-64.44, 41) * mm, "end": v(-63.64, 41) * mm});
            skLineSegment(sketch, "E2132", {"start": v(-63.64, 41) * mm, "end": v(-63.64, 44.1) * mm});
            skLineSegment(sketch, "E2133", {"start": v(-63.64, 44.1) * mm, "end": v(-64.44, 44.1) * mm});
            skLineSegment(sketch, "E2134", {"start": v(-64.44, 44.1) * mm, "end": v(-64.44, 45.1) * mm});
            skLineSegment(sketch, "E2135", {"start": v(-64.44, 45.1) * mm, "end": v(-78.44, 45.1) * mm});
            skLineSegment(sketch, "E2136", {"start": v(-59.39, 45.1) * mm, "end": v(-59.39, 44.1) * mm});
            skLineSegment(sketch, "E2137", {"start": v(-59.39, 44.1) * mm, "end": v(-60.19, 44.1) * mm});
            skLineSegment(sketch, "E2138", {"start": v(-60.19, 44.1) * mm, "end": v(-60.19, 41) * mm});
            skLineSegment(sketch, "E2139", {"start": v(-60.19, 41) * mm, "end": v(-59.39, 41) * mm});
            skLineSegment(sketch, "E2140", {"start": v(-59.39, 41) * mm, "end": v(-59.39, 35.2) * mm});
            skLineSegment(sketch, "E2141", {"start": v(-59.39, 35.2) * mm, "end": v(-60.19, 35.2) * mm});
            skLineSegment(sketch, "E2142", {"start": v(-60.19, 35.2) * mm, "end": v(-60.19, 32.1) * mm});
            skLineSegment(sketch, "E2143", {"start": v(-60.19, 32.1) * mm, "end": v(-59.39, 32.1) * mm});
            skLineSegment(sketch, "E2144", {"start": v(-59.39, 32.1) * mm, "end": v(-59.39, 31.1) * mm});
            skLineSegment(sketch, "E2145", {"start": v(-59.39, 31.1) * mm, "end": v(-45.39, 31.1) * mm});
            skLineSegment(sketch, "E2146", {"start": v(-45.39, 31.1) * mm, "end": v(-45.39, 32.1) * mm});
            skLineSegment(sketch, "E2147", {"start": v(-45.39, 32.1) * mm, "end": v(-44.59, 32.1) * mm});
            skLineSegment(sketch, "E2148", {"start": v(-44.59, 32.1) * mm, "end": v(-44.59, 35.2) * mm});
            skLineSegment(sketch, "E2149", {"start": v(-44.59, 35.2) * mm, "end": v(-45.39, 35.2) * mm});
            skLineSegment(sketch, "E2150", {"start": v(-45.39, 35.2) * mm, "end": v(-45.39, 41) * mm});
            skLineSegment(sketch, "E2151", {"start": v(-45.39, 41) * mm, "end": v(-44.59, 41) * mm});
            skLineSegment(sketch, "E2152", {"start": v(-44.59, 41) * mm, "end": v(-44.59, 44.1) * mm});
            skLineSegment(sketch, "E2153", {"start": v(-44.59, 44.1) * mm, "end": v(-45.39, 44.1) * mm});
            skLineSegment(sketch, "E2154", {"start": v(-45.39, 44.1) * mm, "end": v(-45.39, 45.1) * mm});
            skLineSegment(sketch, "E2155", {"start": v(-45.39, 45.1) * mm, "end": v(-59.39, 45.1) * mm});
            skLineSegment(sketch, "E2156", {"start": v(-40.34, 45.1) * mm, "end": v(-40.34, 44.1) * mm});
            skLineSegment(sketch, "E2157", {"start": v(-40.34, 44.1) * mm, "end": v(-41.14, 44.1) * mm});
            skLineSegment(sketch, "E2158", {"start": v(-41.14, 44.1) * mm, "end": v(-41.14, 41) * mm});
            skLineSegment(sketch, "E2159", {"start": v(-41.14, 41) * mm, "end": v(-40.34, 41) * mm});
            skLineSegment(sketch, "E2160", {"start": v(-40.34, 41) * mm, "end": v(-40.34, 35.2) * mm});
            skLineSegment(sketch, "E2161", {"start": v(-40.34, 35.2) * mm, "end": v(-41.14, 35.2) * mm});
            skLineSegment(sketch, "E2162", {"start": v(-41.14, 35.2) * mm, "end": v(-41.14, 32.1) * mm});
            skLineSegment(sketch, "E2163", {"start": v(-41.14, 32.1) * mm, "end": v(-40.34, 32.1) * mm});
            skLineSegment(sketch, "E2164", {"start": v(-40.34, 32.1) * mm, "end": v(-40.34, 31.1) * mm});
            skLineSegment(sketch, "E2165", {"start": v(-40.34, 31.1) * mm, "end": v(-26.34, 31.1) * mm});
            skLineSegment(sketch, "E2166", {"start": v(-26.34, 31.1) * mm, "end": v(-26.34, 32.1) * mm});
            skLineSegment(sketch, "E2167", {"start": v(-26.34, 32.1) * mm, "end": v(-25.54, 32.1) * mm});
            skLineSegment(sketch, "E2168", {"start": v(-25.54, 32.1) * mm, "end": v(-25.54, 35.2) * mm});
            skLineSegment(sketch, "E2169", {"start": v(-25.54, 35.2) * mm, "end": v(-26.34, 35.2) * mm});
            skLineSegment(sketch, "E2170", {"start": v(-26.34, 35.2) * mm, "end": v(-26.34, 41) * mm});
            skLineSegment(sketch, "E2171", {"start": v(-26.34, 41) * mm, "end": v(-25.54, 41) * mm});
            skLineSegment(sketch, "E2172", {"start": v(-25.54, 41) * mm, "end": v(-25.54, 44.1) * mm});
            skLineSegment(sketch, "E2173", {"start": v(-25.54, 44.1) * mm, "end": v(-26.34, 44.1) * mm});
            skLineSegment(sketch, "E2174", {"start": v(-26.34, 44.1) * mm, "end": v(-26.34, 45.1) * mm});
            skLineSegment(sketch, "E2175", {"start": v(-26.34, 45.1) * mm, "end": v(-40.34, 45.1) * mm});
            skLineSegment(sketch, "E2176", {"start": v(-21.29, 45.1) * mm, "end": v(-21.29, 44.1) * mm});
            skLineSegment(sketch, "E2177", {"start": v(-21.29, 44.1) * mm, "end": v(-22.09, 44.1) * mm});
            skLineSegment(sketch, "E2178", {"start": v(-22.09, 44.1) * mm, "end": v(-22.09, 41) * mm});
            skLineSegment(sketch, "E2179", {"start": v(-22.09, 41) * mm, "end": v(-21.29, 41) * mm});
            skLineSegment(sketch, "E2180", {"start": v(-21.29, 41) * mm, "end": v(-21.29, 35.2) * mm});
            skLineSegment(sketch, "E2181", {"start": v(-21.29, 35.2) * mm, "end": v(-22.09, 35.2) * mm});
            skLineSegment(sketch, "E2182", {"start": v(-22.09, 35.2) * mm, "end": v(-22.09, 32.1) * mm});
            skLineSegment(sketch, "E2183", {"start": v(-22.09, 32.1) * mm, "end": v(-21.29, 32.1) * mm});
            skLineSegment(sketch, "E2184", {"start": v(-21.29, 32.1) * mm, "end": v(-21.29, 31.1) * mm});
            skLineSegment(sketch, "E2185", {"start": v(-21.29, 31.1) * mm, "end": v(-7.29, 31.1) * mm});
            skLineSegment(sketch, "E2186", {"start": v(-7.29, 31.1) * mm, "end": v(-7.29, 32.1) * mm});
            skLineSegment(sketch, "E2187", {"start": v(-7.29, 32.1) * mm, "end": v(-6.49, 32.1) * mm});
            skLineSegment(sketch, "E2188", {"start": v(-6.49, 32.1) * mm, "end": v(-6.49, 35.2) * mm});
            skLineSegment(sketch, "E2189", {"start": v(-6.49, 35.2) * mm, "end": v(-7.29, 35.2) * mm});
            skLineSegment(sketch, "E2190", {"start": v(-7.29, 35.2) * mm, "end": v(-7.29, 41) * mm});
            skLineSegment(sketch, "E2191", {"start": v(-7.29, 41) * mm, "end": v(-6.49, 41) * mm});
            skLineSegment(sketch, "E2192", {"start": v(-6.49, 41) * mm, "end": v(-6.49, 44.1) * mm});
            skLineSegment(sketch, "E2193", {"start": v(-6.49, 44.1) * mm, "end": v(-7.29, 44.1) * mm});
            skLineSegment(sketch, "E2194", {"start": v(-7.29, 44.1) * mm, "end": v(-7.29, 45.1) * mm});
            skLineSegment(sketch, "E2195", {"start": v(-7.29, 45.1) * mm, "end": v(-21.29, 45.1) * mm});
            skLineSegment(sketch, "E2196", {"start": v(-2.24, 45.1) * mm, "end": v(-2.24, 44.1) * mm});
            skLineSegment(sketch, "E2197", {"start": v(-2.24, 44.1) * mm, "end": v(-3.04, 44.1) * mm});
            skLineSegment(sketch, "E2198", {"start": v(-3.04, 44.1) * mm, "end": v(-3.04, 41) * mm});
            skLineSegment(sketch, "E2199", {"start": v(-3.04, 41) * mm, "end": v(-2.24, 41) * mm});
            skLineSegment(sketch, "E2200", {"start": v(-2.24, 41) * mm, "end": v(-2.24, 35.2) * mm});
            skLineSegment(sketch, "E2201", {"start": v(-2.24, 35.2) * mm, "end": v(-3.04, 35.2) * mm});
            skLineSegment(sketch, "E2202", {"start": v(-3.04, 35.2) * mm, "end": v(-3.04, 32.1) * mm});
            skLineSegment(sketch, "E2203", {"start": v(-3.04, 32.1) * mm, "end": v(-2.24, 32.1) * mm});
            skLineSegment(sketch, "E2204", {"start": v(-2.24, 32.1) * mm, "end": v(-2.24, 31.1) * mm});
            skLineSegment(sketch, "E2205", {"start": v(-2.24, 31.1) * mm, "end": v(11.76, 31.1) * mm});
            skLineSegment(sketch, "E2206", {"start": v(11.76, 31.1) * mm, "end": v(11.76, 32.1) * mm});
            skLineSegment(sketch, "E2207", {"start": v(11.76, 32.1) * mm, "end": v(12.56, 32.1) * mm});
            skLineSegment(sketch, "E2208", {"start": v(12.56, 32.1) * mm, "end": v(12.56, 35.2) * mm});
            skLineSegment(sketch, "E2209", {"start": v(12.56, 35.2) * mm, "end": v(11.76, 35.2) * mm});
            skLineSegment(sketch, "E2210", {"start": v(11.76, 35.2) * mm, "end": v(11.76, 41) * mm});
            skLineSegment(sketch, "E2211", {"start": v(11.76, 41) * mm, "end": v(12.56, 41) * mm});
            skLineSegment(sketch, "E2212", {"start": v(12.56, 41) * mm, "end": v(12.56, 44.1) * mm});
            skLineSegment(sketch, "E2213", {"start": v(12.56, 44.1) * mm, "end": v(11.76, 44.1) * mm});
            skLineSegment(sketch, "E2214", {"start": v(11.76, 44.1) * mm, "end": v(11.76, 45.1) * mm});
            skLineSegment(sketch, "E2215", {"start": v(11.76, 45.1) * mm, "end": v(-2.24, 45.1) * mm});
            skLineSegment(sketch, "E2216", {"start": v(16.81, 45.1) * mm, "end": v(16.81, 44.1) * mm});
            skLineSegment(sketch, "E2217", {"start": v(16.81, 44.1) * mm, "end": v(16.01, 44.1) * mm});
            skLineSegment(sketch, "E2218", {"start": v(16.01, 44.1) * mm, "end": v(16.01, 41) * mm});
            skLineSegment(sketch, "E2219", {"start": v(16.01, 41) * mm, "end": v(16.81, 41) * mm});
            skLineSegment(sketch, "E2220", {"start": v(16.81, 41) * mm, "end": v(16.81, 35.2) * mm});
            skLineSegment(sketch, "E2221", {"start": v(16.81, 35.2) * mm, "end": v(16.01, 35.2) * mm});
            skLineSegment(sketch, "E2222", {"start": v(16.01, 35.2) * mm, "end": v(16.01, 32.1) * mm});
            skLineSegment(sketch, "E2223", {"start": v(16.01, 32.1) * mm, "end": v(16.81, 32.1) * mm});
            skLineSegment(sketch, "E2224", {"start": v(16.81, 32.1) * mm, "end": v(16.81, 31.1) * mm});
            skLineSegment(sketch, "E2225", {"start": v(16.81, 31.1) * mm, "end": v(30.81, 31.1) * mm});
            skLineSegment(sketch, "E2226", {"start": v(30.81, 31.1) * mm, "end": v(30.81, 32.1) * mm});
            skLineSegment(sketch, "E2227", {"start": v(30.81, 32.1) * mm, "end": v(31.61, 32.1) * mm});
            skLineSegment(sketch, "E2228", {"start": v(31.61, 32.1) * mm, "end": v(31.61, 35.2) * mm});
            skLineSegment(sketch, "E2229", {"start": v(31.61, 35.2) * mm, "end": v(30.81, 35.2) * mm});
            skLineSegment(sketch, "E2230", {"start": v(30.81, 35.2) * mm, "end": v(30.81, 41) * mm});
            skLineSegment(sketch, "E2231", {"start": v(30.81, 41) * mm, "end": v(31.61, 41) * mm});
            skLineSegment(sketch, "E2232", {"start": v(31.61, 41) * mm, "end": v(31.61, 44.1) * mm});
            skLineSegment(sketch, "E2233", {"start": v(31.61, 44.1) * mm, "end": v(30.81, 44.1) * mm});
            skLineSegment(sketch, "E2234", {"start": v(30.81, 44.1) * mm, "end": v(30.81, 45.1) * mm});
            skLineSegment(sketch, "E2235", {"start": v(30.81, 45.1) * mm, "end": v(16.81, 45.1) * mm});
            skLineSegment(sketch, "E2236", {"start": v(35.86, 45.1) * mm, "end": v(35.86, 44.1) * mm});
            skLineSegment(sketch, "E2237", {"start": v(35.86, 44.1) * mm, "end": v(35.06, 44.1) * mm});
            skLineSegment(sketch, "E2238", {"start": v(35.06, 44.1) * mm, "end": v(35.06, 41) * mm});
            skLineSegment(sketch, "E2239", {"start": v(35.06, 41) * mm, "end": v(35.86, 41) * mm});
            skLineSegment(sketch, "E2240", {"start": v(35.86, 41) * mm, "end": v(35.86, 35.2) * mm});
            skLineSegment(sketch, "E2241", {"start": v(35.86, 35.2) * mm, "end": v(35.06, 35.2) * mm});
            skLineSegment(sketch, "E2242", {"start": v(35.06, 35.2) * mm, "end": v(35.06, 32.1) * mm});
            skLineSegment(sketch, "E2243", {"start": v(35.06, 32.1) * mm, "end": v(35.86, 32.1) * mm});
            skLineSegment(sketch, "E2244", {"start": v(35.86, 32.1) * mm, "end": v(35.86, 31.1) * mm});
            skLineSegment(sketch, "E2245", {"start": v(35.86, 31.1) * mm, "end": v(49.86, 31.1) * mm});
            skLineSegment(sketch, "E2246", {"start": v(49.86, 31.1) * mm, "end": v(49.86, 32.1) * mm});
            skLineSegment(sketch, "E2247", {"start": v(49.86, 32.1) * mm, "end": v(50.66, 32.1) * mm});
            skLineSegment(sketch, "E2248", {"start": v(50.66, 32.1) * mm, "end": v(50.66, 35.2) * mm});
            skLineSegment(sketch, "E2249", {"start": v(50.66, 35.2) * mm, "end": v(49.86, 35.2) * mm});
            skLineSegment(sketch, "E2250", {"start": v(49.86, 35.2) * mm, "end": v(49.86, 41) * mm});
            skLineSegment(sketch, "E2251", {"start": v(49.86, 41) * mm, "end": v(50.66, 41) * mm});
            skLineSegment(sketch, "E2252", {"start": v(50.66, 41) * mm, "end": v(50.66, 44.1) * mm});
            skLineSegment(sketch, "E2253", {"start": v(50.66, 44.1) * mm, "end": v(49.86, 44.1) * mm});
            skLineSegment(sketch, "E2254", {"start": v(49.86, 44.1) * mm, "end": v(49.86, 45.1) * mm});
            skLineSegment(sketch, "E2255", {"start": v(49.86, 45.1) * mm, "end": v(35.86, 45.1) * mm});
            skLineSegment(sketch, "E2256", {"start": v(54.91, 45.1) * mm, "end": v(54.91, 44.1) * mm});
            skLineSegment(sketch, "E2257", {"start": v(54.91, 44.1) * mm, "end": v(54.11, 44.1) * mm});
            skLineSegment(sketch, "E2258", {"start": v(54.11, 44.1) * mm, "end": v(54.11, 41) * mm});
            skLineSegment(sketch, "E2259", {"start": v(54.11, 41) * mm, "end": v(54.91, 41) * mm});
            skLineSegment(sketch, "E2260", {"start": v(54.91, 41) * mm, "end": v(54.91, 35.2) * mm});
            skLineSegment(sketch, "E2261", {"start": v(54.91, 35.2) * mm, "end": v(54.11, 35.2) * mm});
            skLineSegment(sketch, "E2262", {"start": v(54.11, 35.2) * mm, "end": v(54.11, 32.1) * mm});
            skLineSegment(sketch, "E2263", {"start": v(54.11, 32.1) * mm, "end": v(54.91, 32.1) * mm});
            skLineSegment(sketch, "E2264", {"start": v(54.91, 32.1) * mm, "end": v(54.91, 31.1) * mm});
            skLineSegment(sketch, "E2265", {"start": v(54.91, 31.1) * mm, "end": v(68.91, 31.1) * mm});
            skLineSegment(sketch, "E2266", {"start": v(68.91, 31.1) * mm, "end": v(68.91, 32.1) * mm});
            skLineSegment(sketch, "E2267", {"start": v(68.91, 32.1) * mm, "end": v(69.71, 32.1) * mm});
            skLineSegment(sketch, "E2268", {"start": v(69.71, 32.1) * mm, "end": v(69.71, 35.2) * mm});
            skLineSegment(sketch, "E2269", {"start": v(69.71, 35.2) * mm, "end": v(68.91, 35.2) * mm});
            skLineSegment(sketch, "E2270", {"start": v(68.91, 35.2) * mm, "end": v(68.91, 41) * mm});
            skLineSegment(sketch, "E2271", {"start": v(68.91, 41) * mm, "end": v(69.71, 41) * mm});
            skLineSegment(sketch, "E2272", {"start": v(69.71, 41) * mm, "end": v(69.71, 44.1) * mm});
            skLineSegment(sketch, "E2273", {"start": v(69.71, 44.1) * mm, "end": v(68.91, 44.1) * mm});
            skLineSegment(sketch, "E2274", {"start": v(68.91, 44.1) * mm, "end": v(68.91, 45.1) * mm});
            skLineSegment(sketch, "E2275", {"start": v(68.91, 45.1) * mm, "end": v(54.91, 45.1) * mm});
            skLineSegment(sketch, "E2276", {"start": v(73.96, 45.1) * mm, "end": v(73.96, 44.1) * mm});
            skLineSegment(sketch, "E2277", {"start": v(73.96, 44.1) * mm, "end": v(73.16, 44.1) * mm});
            skLineSegment(sketch, "E2278", {"start": v(73.16, 44.1) * mm, "end": v(73.16, 41) * mm});
            skLineSegment(sketch, "E2279", {"start": v(73.16, 41) * mm, "end": v(73.96, 41) * mm});
            skLineSegment(sketch, "E2280", {"start": v(73.96, 41) * mm, "end": v(73.96, 35.2) * mm});
            skLineSegment(sketch, "E2281", {"start": v(73.96, 35.2) * mm, "end": v(73.16, 35.2) * mm});
            skLineSegment(sketch, "E2282", {"start": v(73.16, 35.2) * mm, "end": v(73.16, 32.1) * mm});
            skLineSegment(sketch, "E2283", {"start": v(73.16, 32.1) * mm, "end": v(73.96, 32.1) * mm});
            skLineSegment(sketch, "E2284", {"start": v(73.96, 32.1) * mm, "end": v(73.96, 31.1) * mm});
            skLineSegment(sketch, "E2285", {"start": v(73.96, 31.1) * mm, "end": v(87.96, 31.1) * mm});
            skLineSegment(sketch, "E2286", {"start": v(87.96, 31.1) * mm, "end": v(87.96, 32.1) * mm});
            skLineSegment(sketch, "E2287", {"start": v(87.96, 32.1) * mm, "end": v(88.76, 32.1) * mm});
            skLineSegment(sketch, "E2288", {"start": v(88.76, 32.1) * mm, "end": v(88.76, 35.2) * mm});
            skLineSegment(sketch, "E2289", {"start": v(88.76, 35.2) * mm, "end": v(87.96, 35.2) * mm});
            skLineSegment(sketch, "E2290", {"start": v(87.96, 35.2) * mm, "end": v(87.96, 41) * mm});
            skLineSegment(sketch, "E2291", {"start": v(87.96, 41) * mm, "end": v(88.76, 41) * mm});
            skLineSegment(sketch, "E2292", {"start": v(88.76, 41) * mm, "end": v(88.76, 44.1) * mm});
            skLineSegment(sketch, "E2293", {"start": v(88.76, 44.1) * mm, "end": v(87.96, 44.1) * mm});
            skLineSegment(sketch, "E2294", {"start": v(87.96, 44.1) * mm, "end": v(87.96, 45.1) * mm});
            skLineSegment(sketch, "E2295", {"start": v(87.96, 45.1) * mm, "end": v(73.96, 45.1) * mm});
            skLineSegment(sketch, "E2296", {"start": v(93.01, 45.1) * mm, "end": v(93.01, 44.1) * mm});
            skLineSegment(sketch, "E2297", {"start": v(93.01, 44.1) * mm, "end": v(92.21, 44.1) * mm});
            skLineSegment(sketch, "E2298", {"start": v(92.21, 44.1) * mm, "end": v(92.21, 41) * mm});
            skLineSegment(sketch, "E2299", {"start": v(92.21, 41) * mm, "end": v(93.01, 41) * mm});
            skLineSegment(sketch, "E2300", {"start": v(93.01, 41) * mm, "end": v(93.01, 35.2) * mm});
            skLineSegment(sketch, "E2301", {"start": v(93.01, 35.2) * mm, "end": v(92.21, 35.2) * mm});
            skLineSegment(sketch, "E2302", {"start": v(92.21, 35.2) * mm, "end": v(92.21, 32.1) * mm});
            skLineSegment(sketch, "E2303", {"start": v(92.21, 32.1) * mm, "end": v(93.01, 32.1) * mm});
            skLineSegment(sketch, "E2304", {"start": v(93.01, 32.1) * mm, "end": v(93.01, 31.1) * mm});
            skLineSegment(sketch, "E2305", {"start": v(93.01, 31.1) * mm, "end": v(107.01, 31.1) * mm});
            skLineSegment(sketch, "E2306", {"start": v(107.01, 31.1) * mm, "end": v(107.01, 32.1) * mm});
            skLineSegment(sketch, "E2307", {"start": v(107.01, 32.1) * mm, "end": v(107.81, 32.1) * mm});
            skLineSegment(sketch, "E2308", {"start": v(107.81, 32.1) * mm, "end": v(107.81, 35.2) * mm});
            skLineSegment(sketch, "E2309", {"start": v(107.81, 35.2) * mm, "end": v(107.01, 35.2) * mm});
            skLineSegment(sketch, "E2310", {"start": v(107.01, 35.2) * mm, "end": v(107.01, 41) * mm});
            skLineSegment(sketch, "E2311", {"start": v(107.01, 41) * mm, "end": v(107.81, 41) * mm});
            skLineSegment(sketch, "E2312", {"start": v(107.81, 41) * mm, "end": v(107.81, 44.1) * mm});
            skLineSegment(sketch, "E2313", {"start": v(107.81, 44.1) * mm, "end": v(107.01, 44.1) * mm});
            skLineSegment(sketch, "E2314", {"start": v(107.01, 44.1) * mm, "end": v(107.01, 45.1) * mm});
            skLineSegment(sketch, "E2315", {"start": v(107.01, 45.1) * mm, "end": v(93.01, 45.1) * mm});
            skLineSegment(sketch, "E2316", {"start": v(112.06, 45.1) * mm, "end": v(112.06, 44.1) * mm});
            skLineSegment(sketch, "E2317", {"start": v(112.06, 44.1) * mm, "end": v(111.26, 44.1) * mm});
            skLineSegment(sketch, "E2318", {"start": v(111.26, 44.1) * mm, "end": v(111.26, 41) * mm});
            skLineSegment(sketch, "E2319", {"start": v(111.26, 41) * mm, "end": v(112.06, 41) * mm});
            skLineSegment(sketch, "E2320", {"start": v(112.06, 41) * mm, "end": v(112.06, 35.2) * mm});
            skLineSegment(sketch, "E2321", {"start": v(112.06, 35.2) * mm, "end": v(111.26, 35.2) * mm});
            skLineSegment(sketch, "E2322", {"start": v(111.26, 35.2) * mm, "end": v(111.26, 32.1) * mm});
            skLineSegment(sketch, "E2323", {"start": v(111.26, 32.1) * mm, "end": v(112.06, 32.1) * mm});
            skLineSegment(sketch, "E2324", {"start": v(112.06, 32.1) * mm, "end": v(112.06, 31.1) * mm});
            skLineSegment(sketch, "E2325", {"start": v(112.06, 31.1) * mm, "end": v(126.06, 31.1) * mm});
            skLineSegment(sketch, "E2326", {"start": v(126.06, 31.1) * mm, "end": v(126.06, 32.1) * mm});
            skLineSegment(sketch, "E2327", {"start": v(126.06, 32.1) * mm, "end": v(126.86, 32.1) * mm});
            skLineSegment(sketch, "E2328", {"start": v(126.86, 32.1) * mm, "end": v(126.86, 35.2) * mm});
            skLineSegment(sketch, "E2329", {"start": v(126.86, 35.2) * mm, "end": v(126.06, 35.2) * mm});
            skLineSegment(sketch, "E2330", {"start": v(126.06, 35.2) * mm, "end": v(126.06, 41) * mm});
            skLineSegment(sketch, "E2331", {"start": v(126.06, 41) * mm, "end": v(126.86, 41) * mm});
            skLineSegment(sketch, "E2332", {"start": v(126.86, 41) * mm, "end": v(126.86, 44.1) * mm});
            skLineSegment(sketch, "E2333", {"start": v(126.86, 44.1) * mm, "end": v(126.06, 44.1) * mm});
            skLineSegment(sketch, "E2334", {"start": v(126.06, 44.1) * mm, "end": v(126.06, 45.1) * mm});
            skLineSegment(sketch, "E2335", {"start": v(126.06, 45.1) * mm, "end": v(112.06, 45.1) * mm});
            skLineSegment(sketch, "E2336", {"start": v(140.64, 45.1) * mm, "end": v(140.64, 44.1) * mm});
            skLineSegment(sketch, "E2337", {"start": v(140.64, 44.1) * mm, "end": v(139.84, 44.1) * mm});
            skLineSegment(sketch, "E2338", {"start": v(139.84, 44.1) * mm, "end": v(139.84, 41) * mm});
            skLineSegment(sketch, "E2339", {"start": v(139.84, 41) * mm, "end": v(140.64, 41) * mm});
            skLineSegment(sketch, "E2340", {"start": v(140.64, 41) * mm, "end": v(140.64, 35.2) * mm});
            skLineSegment(sketch, "E2341", {"start": v(140.64, 35.2) * mm, "end": v(139.84, 35.2) * mm});
            skLineSegment(sketch, "E2342", {"start": v(139.84, 35.2) * mm, "end": v(139.84, 32.1) * mm});
            skLineSegment(sketch, "E2343", {"start": v(139.84, 32.1) * mm, "end": v(140.64, 32.1) * mm});
            skLineSegment(sketch, "E2344", {"start": v(140.64, 32.1) * mm, "end": v(140.64, 31.1) * mm});
            skLineSegment(sketch, "E2345", {"start": v(140.64, 31.1) * mm, "end": v(154.64, 31.1) * mm});
            skLineSegment(sketch, "E2346", {"start": v(154.64, 31.1) * mm, "end": v(154.64, 32.1) * mm});
            skLineSegment(sketch, "E2347", {"start": v(154.64, 32.1) * mm, "end": v(155.44, 32.1) * mm});
            skLineSegment(sketch, "E2348", {"start": v(155.44, 32.1) * mm, "end": v(155.44, 35.2) * mm});
            skLineSegment(sketch, "E2349", {"start": v(155.44, 35.2) * mm, "end": v(154.64, 35.2) * mm});
            skLineSegment(sketch, "E2350", {"start": v(154.64, 35.2) * mm, "end": v(154.64, 41) * mm});
            skLineSegment(sketch, "E2351", {"start": v(154.64, 41) * mm, "end": v(155.44, 41) * mm});
            skLineSegment(sketch, "E2352", {"start": v(155.44, 41) * mm, "end": v(155.44, 44.1) * mm});
            skLineSegment(sketch, "E2353", {"start": v(155.44, 44.1) * mm, "end": v(154.64, 44.1) * mm});
            skLineSegment(sketch, "E2354", {"start": v(154.64, 44.1) * mm, "end": v(154.64, 45.1) * mm});
            skLineSegment(sketch, "E2355", {"start": v(154.64, 45.1) * mm, "end": v(140.64, 45.1) * mm});
            skLineSegment(sketch, "E2356", {"start": v(-54.02, 52.55) * mm, "end": v(-54.44, 52.34) * mm});
            skLineSegment(sketch, "E2357", {"start": v(-54.44, 52.34) * mm, "end": v(-54.77, 52) * mm});
            skLineSegment(sketch, "E2358", {"start": v(-54.77, 52) * mm, "end": v(-54.98, 51.59) * mm});
            skLineSegment(sketch, "E2359", {"start": v(-54.98, 51.59) * mm, "end": v(-55.06, 51.12) * mm});
            skLineSegment(sketch, "E2360", {"start": v(-55.06, 51.12) * mm, "end": v(-54.98, 50.66) * mm});
            skLineSegment(sketch, "E2361", {"start": v(-54.98, 50.66) * mm, "end": v(-54.77, 50.24) * mm});
            skLineSegment(sketch, "E2362", {"start": v(-54.77, 50.24) * mm, "end": v(-54.44, 49.91) * mm});
            skLineSegment(sketch, "E2363", {"start": v(-54.44, 49.91) * mm, "end": v(-54.02, 49.7) * mm});
            skLineSegment(sketch, "E2364", {"start": v(-54.02, 49.7) * mm, "end": v(-53.55, 49.62) * mm});
            skLineSegment(sketch, "E2365", {"start": v(-53.55, 49.62) * mm, "end": v(-53.1, 49.7) * mm});
            skLineSegment(sketch, "E2366", {"start": v(-53.1, 49.7) * mm, "end": v(-52.67, 49.91) * mm});
            skLineSegment(sketch, "E2367", {"start": v(-52.67, 49.91) * mm, "end": v(-52.34, 50.24) * mm});
            skLineSegment(sketch, "E2368", {"start": v(-52.34, 50.24) * mm, "end": v(-52.13, 50.66) * mm});
            skLineSegment(sketch, "E2369", {"start": v(-52.13, 50.66) * mm, "end": v(-52.06, 51.12) * mm});
            skLineSegment(sketch, "E2370", {"start": v(-52.06, 51.12) * mm, "end": v(-52.13, 51.59) * mm});
            skLineSegment(sketch, "E2371", {"start": v(-52.13, 51.59) * mm, "end": v(-52.34, 52) * mm});
            skLineSegment(sketch, "E2372", {"start": v(-52.34, 52) * mm, "end": v(-52.67, 52.34) * mm});
            skLineSegment(sketch, "E2373", {"start": v(-52.67, 52.34) * mm, "end": v(-53.1, 52.55) * mm});
            skLineSegment(sketch, "E2374", {"start": v(-53.1, 52.55) * mm, "end": v(-53.55, 52.62) * mm});
            skLineSegment(sketch, "E2375", {"start": v(-53.55, 52.62) * mm, "end": v(-54.02, 52.55) * mm});
            skLineSegment(sketch, "E2376", {"start": v(53.1, 52.55) * mm, "end": v(52.67, 52.34) * mm});
            skLineSegment(sketch, "E2377", {"start": v(52.67, 52.34) * mm, "end": v(52.34, 52) * mm});
            skLineSegment(sketch, "E2378", {"start": v(52.34, 52) * mm, "end": v(52.13, 51.59) * mm});
            skLineSegment(sketch, "E2379", {"start": v(52.13, 51.59) * mm, "end": v(52.05, 51.12) * mm});
            skLineSegment(sketch, "E2380", {"start": v(52.05, 51.12) * mm, "end": v(52.13, 50.66) * mm});
            skLineSegment(sketch, "E2381", {"start": v(52.13, 50.66) * mm, "end": v(52.34, 50.24) * mm});
            skLineSegment(sketch, "E2382", {"start": v(52.34, 50.24) * mm, "end": v(52.67, 49.91) * mm});
            skLineSegment(sketch, "E2383", {"start": v(52.67, 49.91) * mm, "end": v(53.1, 49.7) * mm});
            skLineSegment(sketch, "E2384", {"start": v(53.1, 49.7) * mm, "end": v(53.55, 49.62) * mm});
            skLineSegment(sketch, "E2385", {"start": v(53.55, 49.62) * mm, "end": v(54.02, 49.7) * mm});
            skLineSegment(sketch, "E2386", {"start": v(54.02, 49.7) * mm, "end": v(54.44, 49.91) * mm});
            skLineSegment(sketch, "E2387", {"start": v(54.44, 49.91) * mm, "end": v(54.77, 50.24) * mm});
            skLineSegment(sketch, "E2388", {"start": v(54.77, 50.24) * mm, "end": v(54.98, 50.66) * mm});
            skLineSegment(sketch, "E2389", {"start": v(54.98, 50.66) * mm, "end": v(55.05, 51.12) * mm});
            skLineSegment(sketch, "E2390", {"start": v(55.05, 51.12) * mm, "end": v(54.98, 51.59) * mm});
            skLineSegment(sketch, "E2391", {"start": v(54.98, 51.59) * mm, "end": v(54.77, 52) * mm});
            skLineSegment(sketch, "E2392", {"start": v(54.77, 52) * mm, "end": v(54.44, 52.34) * mm});
            skLineSegment(sketch, "E2393", {"start": v(54.44, 52.34) * mm, "end": v(54.02, 52.55) * mm});
            skLineSegment(sketch, "E2394", {"start": v(54.02, 52.55) * mm, "end": v(53.55, 52.62) * mm});
            skLineSegment(sketch, "E2395", {"start": v(53.55, 52.62) * mm, "end": v(53.1, 52.55) * mm});
            skLineSegment(sketch, "E2396", {"start": v(160.2, 52.55) * mm, "end": v(159.78, 52.34) * mm});
            skLineSegment(sketch, "E2397", {"start": v(159.78, 52.34) * mm, "end": v(159.45, 52) * mm});
            skLineSegment(sketch, "E2398", {"start": v(159.45, 52) * mm, "end": v(159.24, 51.59) * mm});
            skLineSegment(sketch, "E2399", {"start": v(159.24, 51.59) * mm, "end": v(159.16, 51.12) * mm});
            skLineSegment(sketch, "E2400", {"start": v(159.16, 51.12) * mm, "end": v(159.24, 50.66) * mm});
            skLineSegment(sketch, "E2401", {"start": v(159.24, 50.66) * mm, "end": v(159.45, 50.24) * mm});
            skLineSegment(sketch, "E2402", {"start": v(159.45, 50.24) * mm, "end": v(159.78, 49.91) * mm});
            skLineSegment(sketch, "E2403", {"start": v(159.78, 49.91) * mm, "end": v(160.2, 49.7) * mm});
            skLineSegment(sketch, "E2404", {"start": v(160.2, 49.7) * mm, "end": v(160.66, 49.62) * mm});
            skLineSegment(sketch, "E2405", {"start": v(160.66, 49.62) * mm, "end": v(161.13, 49.7) * mm});
            skLineSegment(sketch, "E2406", {"start": v(161.13, 49.7) * mm, "end": v(161.54, 49.91) * mm});
            skLineSegment(sketch, "E2407", {"start": v(161.54, 49.91) * mm, "end": v(161.88, 50.24) * mm});
            skLineSegment(sketch, "E2408", {"start": v(161.88, 50.24) * mm, "end": v(162.09, 50.66) * mm});
            skLineSegment(sketch, "E2409", {"start": v(162.09, 50.66) * mm, "end": v(162.16, 51.12) * mm});
            skLineSegment(sketch, "E2410", {"start": v(162.16, 51.12) * mm, "end": v(162.09, 51.59) * mm});
            skLineSegment(sketch, "E2411", {"start": v(162.09, 51.59) * mm, "end": v(161.88, 52) * mm});
            skLineSegment(sketch, "E2412", {"start": v(161.88, 52) * mm, "end": v(161.54, 52.34) * mm});
            skLineSegment(sketch, "E2413", {"start": v(161.54, 52.34) * mm, "end": v(161.13, 52.55) * mm});
            skLineSegment(sketch, "E2414", {"start": v(161.13, 52.55) * mm, "end": v(160.66, 52.62) * mm});
            skLineSegment(sketch, "E2415", {"start": v(160.66, 52.62) * mm, "end": v(160.2, 52.55) * mm});
            skLineSegment(sketch, "E2416", {"start": v(-161.13, 52.55) * mm, "end": v(-161.54, 52.34) * mm});
            skLineSegment(sketch, "E2417", {"start": v(-161.54, 52.34) * mm, "end": v(-161.88, 52) * mm});
            skLineSegment(sketch, "E2418", {"start": v(-161.88, 52) * mm, "end": v(-162.1, 51.59) * mm});
            skLineSegment(sketch, "E2419", {"start": v(-162.1, 51.59) * mm, "end": v(-162.16, 51.12) * mm});
            skLineSegment(sketch, "E2420", {"start": v(-162.16, 51.12) * mm, "end": v(-162.1, 50.66) * mm});
            skLineSegment(sketch, "E2421", {"start": v(-162.1, 50.66) * mm, "end": v(-161.88, 50.24) * mm});
            skLineSegment(sketch, "E2422", {"start": v(-161.88, 50.24) * mm, "end": v(-161.54, 49.91) * mm});
            skLineSegment(sketch, "E2423", {"start": v(-161.54, 49.91) * mm, "end": v(-161.13, 49.7) * mm});
            skLineSegment(sketch, "E2424", {"start": v(-161.13, 49.7) * mm, "end": v(-160.66, 49.62) * mm});
            skLineSegment(sketch, "E2425", {"start": v(-160.66, 49.62) * mm, "end": v(-160.2, 49.7) * mm});
            skLineSegment(sketch, "E2426", {"start": v(-160.2, 49.7) * mm, "end": v(-159.78, 49.91) * mm});
            skLineSegment(sketch, "E2427", {"start": v(-159.78, 49.91) * mm, "end": v(-159.45, 50.24) * mm});
            skLineSegment(sketch, "E2428", {"start": v(-159.45, 50.24) * mm, "end": v(-159.24, 50.66) * mm});
            skLineSegment(sketch, "E2429", {"start": v(-159.24, 50.66) * mm, "end": v(-159.16, 51.12) * mm});
            skLineSegment(sketch, "E2430", {"start": v(-159.16, 51.12) * mm, "end": v(-159.24, 51.59) * mm});
            skLineSegment(sketch, "E2431", {"start": v(-159.24, 51.59) * mm, "end": v(-159.45, 52) * mm});
            skLineSegment(sketch, "E2432", {"start": v(-159.45, 52) * mm, "end": v(-159.78, 52.34) * mm});
            skLineSegment(sketch, "E2433", {"start": v(-159.78, 52.34) * mm, "end": v(-160.2, 52.55) * mm});
            skLineSegment(sketch, "E2434", {"start": v(-160.2, 52.55) * mm, "end": v(-160.66, 52.62) * mm});
            skLineSegment(sketch, "E2435", {"start": v(-160.66, 52.62) * mm, "end": v(-161.13, 52.55) * mm});
            skSolve(sketch);
        }
        {
            var Q0;
            Q0 = qSketchRegion(id + "F7", true);
            extrude(context, id + "F8", {"entities" : qUnion([Q0]), "depth" : (getVariable(context, 'Thickness')) * mm, "offsetDistance" : 25 * mm});
        }
        {
            var Q0;
            Q0=makeQuery(id+"F8.opExtrude","CAP_FACE",FACE,{"disambiguationData":[OSD([sQuery(id+"F7.wireOp",EDGE,"E744"),sQuery(id+"F7.wireOp",EDGE,"E745"),sQuery(id+"F7.wireOp",EDGE,"E746"),sQuery(id+"F7.wireOp",EDGE,"E747"),sQuery(id+"F7.wireOp",EDGE,"E748"),sQuery(id+"F7.wireOp",EDGE,"E749"),sQuery(id+"F7.wireOp",EDGE,"E750"),sQuery(id+"F7.wireOp",EDGE,"E751"),sQuery(id+"F7.wireOp",EDGE,"E752"),sQuery(id+"F7.wireOp",EDGE,"E753"),sQuery(id+"F7.wireOp",EDGE,"E754"),sQuery(id+"F7.wireOp",EDGE,"E755"),sQuery(id+"F7.wireOp",EDGE,"E756"),sQuery(id+"F7.wireOp",EDGE,"E757"),sQuery(id+"F7.wireOp",EDGE,"E758"),sQuery(id+"F7.wireOp",EDGE,"E759"),sQuery(id+"F7.wireOp",EDGE,"E760"),sQuery(id+"F7.wireOp",EDGE,"E761"),sQuery(id+"F7.wireOp",EDGE,"E762"),sQuery(id+"F7.wireOp",EDGE,"E763"),sQuery(id+"F7.wireOp",EDGE,"E764"),sQuery(id+"F7.wireOp",EDGE,"E765"),sQuery(id+"F7.wireOp",EDGE,"E766"),sQuery(id+"F7.wireOp",EDGE,"E767"),sQuery(id+"F7.wireOp",EDGE,"E768"),sQuery(id+"F7.wireOp",EDGE,"E769"),sQuery(id+"F7.wireOp",EDGE,"E770"),sQuery(id+"F7.wireOp",EDGE,"E771"),sQuery(id+"F7.wireOp",EDGE,"E772"),sQuery(id+"F7.wireOp",EDGE,"E773"),sQuery(id+"F7.wireOp",EDGE,"E774"),sQuery(id+"F7.wireOp",EDGE,"E775"),sQuery(id+"F7.wireOp",EDGE,"E776"),sQuery(id+"F7.wireOp",EDGE,"E777"),sQuery(id+"F7.wireOp",EDGE,"E778"),sQuery(id+"F7.wireOp",EDGE,"E779"),sQuery(id+"F7.wireOp",EDGE,"E780"),sQuery(id+"F7.wireOp",EDGE,"E781"),sQuery(id+"F7.wireOp",EDGE,"E782"),sQuery(id+"F7.wireOp",EDGE,"E783"),sQuery(id+"F7.wireOp",EDGE,"E784"),sQuery(id+"F7.wireOp",EDGE,"E785"),sQuery(id+"F7.wireOp",EDGE,"E786"),sQuery(id+"F7.wireOp",EDGE,"E787"),sQuery(id+"F7.wireOp",EDGE,"E788"),sQuery(id+"F7.wireOp",EDGE,"E789"),sQuery(id+"F7.wireOp",EDGE,"E790"),sQuery(id+"F7.wireOp",EDGE,"E791"),sQuery(id+"F7.wireOp",EDGE,"E792"),sQuery(id+"F7.wireOp",EDGE,"E793"),sQuery(id+"F7.wireOp",EDGE,"E794"),sQuery(id+"F7.wireOp",EDGE,"E795"),sQuery(id+"F7.wireOp",EDGE,"E796"),sQuery(id+"F7.wireOp",EDGE,"E797"),sQuery(id+"F7.wireOp",EDGE,"E798"),sQuery(id+"F7.wireOp",EDGE,"E799"),sQuery(id+"F7.wireOp",EDGE,"E800"),sQuery(id+"F7.wireOp",EDGE,"E801"),sQuery(id+"F7.wireOp",EDGE,"E802"),sQuery(id+"F7.wireOp",EDGE,"E803"),sQuery(id+"F7.wireOp",EDGE,"E804"),sQuery(id+"F7.wireOp",EDGE,"E805"),sQuery(id+"F7.wireOp",EDGE,"E806"),sQuery(id+"F7.wireOp",EDGE,"E807"),sQuery(id+"F7.wireOp",EDGE,"E808"),sQuery(id+"F7.wireOp",EDGE,"E809"),sQuery(id+"F7.wireOp",EDGE,"E810"),sQuery(id+"F7.wireOp",EDGE,"E811"),sQuery(id+"F7.wireOp",EDGE,"E812"),sQuery(id+"F7.wireOp",EDGE,"E813"),sQuery(id+"F7.wireOp",EDGE,"E814"),sQuery(id+"F7.wireOp",EDGE,"E815"),sQuery(id+"F7.wireOp",EDGE,"E816"),sQuery(id+"F7.wireOp",EDGE,"E817"),sQuery(id+"F7.wireOp",EDGE,"E818"),sQuery(id+"F7.wireOp",EDGE,"E819"),sQuery(id+"F7.wireOp",EDGE,"E820"),sQuery(id+"F7.wireOp",EDGE,"E821"),sQuery(id+"F7.wireOp",EDGE,"E822"),sQuery(id+"F7.wireOp",EDGE,"E823"),sQuery(id+"F7.wireOp",EDGE,"E824"),sQuery(id+"F7.wireOp",EDGE,"E825"),sQuery(id+"F7.wireOp",EDGE,"E826"),sQuery(id+"F7.wireOp",EDGE,"E827"),sQuery(id+"F7.wireOp",EDGE,"E828"),sQuery(id+"F7.wireOp",EDGE,"E829"),sQuery(id+"F7.wireOp",EDGE,"E830"),sQuery(id+"F7.wireOp",EDGE,"E831"),sQuery(id+"F7.wireOp",EDGE,"E832"),sQuery(id+"F7.wireOp",EDGE,"E833"),sQuery(id+"F7.wireOp",EDGE,"E834"),sQuery(id+"F7.wireOp",EDGE,"E835"),sQuery(id+"F7.wireOp",EDGE,"E836"),sQuery(id+"F7.wireOp",EDGE,"E837"),sQuery(id+"F7.wireOp",EDGE,"E838"),sQuery(id+"F7.wireOp",EDGE,"E839"),sQuery(id+"F7.wireOp",EDGE,"E840"),sQuery(id+"F7.wireOp",EDGE,"E841"),sQuery(id+"F7.wireOp",EDGE,"E842"),sQuery(id+"F7.wireOp",EDGE,"E843"),sQuery(id+"F7.wireOp",EDGE,"E844"),sQuery(id+"F7.wireOp",EDGE,"E845"),sQuery(id+"F7.wireOp",EDGE,"E846"),sQuery(id+"F7.wireOp",EDGE,"E847"),sQuery(id+"F7.wireOp",EDGE,"E848"),sQuery(id+"F7.wireOp",EDGE,"E849"),sQuery(id+"F7.wireOp",EDGE,"E850"),sQuery(id+"F7.wireOp",EDGE,"E851"),sQuery(id+"F7.wireOp",EDGE,"E852"),sQuery(id+"F7.wireOp",EDGE,"E853"),sQuery(id+"F7.wireOp",EDGE,"E854"),sQuery(id+"F7.wireOp",EDGE,"E855"),sQuery(id+"F7.wireOp",EDGE,"E856"),sQuery(id+"F7.wireOp",EDGE,"E857"),sQuery(id+"F7.wireOp",EDGE,"E858"),sQuery(id+"F7.wireOp",EDGE,"E859"),sQuery(id+"F7.wireOp",EDGE,"E860"),sQuery(id+"F7.wireOp",EDGE,"E861"),sQuery(id+"F7.wireOp",EDGE,"E862"),sQuery(id+"F7.wireOp",EDGE,"E863"),sQuery(id+"F7.wireOp",EDGE,"E864"),sQuery(id+"F7.wireOp",EDGE,"E865"),sQuery(id+"F7.wireOp",EDGE,"E866"),sQuery(id+"F7.wireOp",EDGE,"E867"),sQuery(id+"F7.wireOp",EDGE,"E868"),sQuery(id+"F7.wireOp",EDGE,"E869"),sQuery(id+"F7.wireOp",EDGE,"E870"),sQuery(id+"F7.wireOp",EDGE,"E871"),sQuery(id+"F7.wireOp",EDGE,"E872"),sQuery(id+"F7.wireOp",EDGE,"E873"),sQuery(id+"F7.wireOp",EDGE,"E874"),sQuery(id+"F7.wireOp",EDGE,"E875"),sQuery(id+"F7.wireOp",EDGE,"E876"),sQuery(id+"F7.wireOp",EDGE,"E877"),sQuery(id+"F7.wireOp",EDGE,"E878"),sQuery(id+"F7.wireOp",EDGE,"E879"),sQuery(id+"F7.wireOp",EDGE,"E880"),sQuery(id+"F7.wireOp",EDGE,"E881"),sQuery(id+"F7.wireOp",EDGE,"E882"),sQuery(id+"F7.wireOp",EDGE,"E883"),sQuery(id+"F7.wireOp",EDGE,"E884"),sQuery(id+"F7.wireOp",EDGE,"E885"),sQuery(id+"F7.wireOp",EDGE,"E886"),sQuery(id+"F7.wireOp",EDGE,"E887"),sQuery(id+"F7.wireOp",EDGE,"E888"),sQuery(id+"F7.wireOp",EDGE,"E889"),sQuery(id+"F7.wireOp",EDGE,"E890"),sQuery(id+"F7.wireOp",EDGE,"E891"),sQuery(id+"F7.wireOp",EDGE,"E892"),sQuery(id+"F7.wireOp",EDGE,"E893"),sQuery(id+"F7.wireOp",EDGE,"E894"),sQuery(id+"F7.wireOp",EDGE,"E895"),sQuery(id+"F7.wireOp",EDGE,"E896"),sQuery(id+"F7.wireOp",EDGE,"E897"),sQuery(id+"F7.wireOp",EDGE,"E898"),sQuery(id+"F7.wireOp",EDGE,"E899"),sQuery(id+"F7.wireOp",EDGE,"E900"),sQuery(id+"F7.wireOp",EDGE,"E901"),sQuery(id+"F7.wireOp",EDGE,"E902"),sQuery(id+"F7.wireOp",EDGE,"E903"),sQuery(id+"F7.wireOp",EDGE,"E904"),sQuery(id+"F7.wireOp",EDGE,"E905"),sQuery(id+"F7.wireOp",EDGE,"E906"),sQuery(id+"F7.wireOp",EDGE,"E907"),sQuery(id+"F7.wireOp",EDGE,"E908"),sQuery(id+"F7.wireOp",EDGE,"E909"),sQuery(id+"F7.wireOp",EDGE,"E910"),sQuery(id+"F7.wireOp",EDGE,"E911"),sQuery(id+"F7.wireOp",EDGE,"E912"),sQuery(id+"F7.wireOp",EDGE,"E913"),sQuery(id+"F7.wireOp",EDGE,"E914"),sQuery(id+"F7.wireOp",EDGE,"E915"),sQuery(id+"F7.wireOp",EDGE,"E916"),sQuery(id+"F7.wireOp",EDGE,"E917"),sQuery(id+"F7.wireOp",EDGE,"E918"),sQuery(id+"F7.wireOp",EDGE,"E919"),sQuery(id+"F7.wireOp",EDGE,"E920"),sQuery(id+"F7.wireOp",EDGE,"E921"),sQuery(id+"F7.wireOp",EDGE,"E922"),sQuery(id+"F7.wireOp",EDGE,"E923"),sQuery(id+"F7.wireOp",EDGE,"E924"),sQuery(id+"F7.wireOp",EDGE,"E925"),sQuery(id+"F7.wireOp",EDGE,"E926"),sQuery(id+"F7.wireOp",EDGE,"E927"),sQuery(id+"F7.wireOp",EDGE,"E928"),sQuery(id+"F7.wireOp",EDGE,"E929"),sQuery(id+"F7.wireOp",EDGE,"E930"),sQuery(id+"F7.wireOp",EDGE,"E931"),sQuery(id+"F7.wireOp",EDGE,"E932"),sQuery(id+"F7.wireOp",EDGE,"E933"),sQuery(id+"F7.wireOp",EDGE,"E934"),sQuery(id+"F7.wireOp",EDGE,"E935"),sQuery(id+"F7.wireOp",EDGE,"E936"),sQuery(id+"F7.wireOp",EDGE,"E937"),sQuery(id+"F7.wireOp",EDGE,"E938"),sQuery(id+"F7.wireOp",EDGE,"E939"),sQuery(id+"F7.wireOp",EDGE,"E940"),sQuery(id+"F7.wireOp",EDGE,"E941"),sQuery(id+"F7.wireOp",EDGE,"E942"),sQuery(id+"F7.wireOp",EDGE,"E943"),sQuery(id+"F7.wireOp",EDGE,"E944"),sQuery(id+"F7.wireOp",EDGE,"E945"),sQuery(id+"F7.wireOp",EDGE,"E946"),sQuery(id+"F7.wireOp",EDGE,"E947"),sQuery(id+"F7.wireOp",EDGE,"E948"),sQuery(id+"F7.wireOp",EDGE,"E949"),sQuery(id+"F7.wireOp",EDGE,"E950"),sQuery(id+"F7.wireOp",EDGE,"E951"),sQuery(id+"F7.wireOp",EDGE,"E952"),sQuery(id+"F7.wireOp",EDGE,"E953"),sQuery(id+"F7.wireOp",EDGE,"E954"),sQuery(id+"F7.wireOp",EDGE,"E955"),sQuery(id+"F7.wireOp",EDGE,"E956"),sQuery(id+"F7.wireOp",EDGE,"E957"),sQuery(id+"F7.wireOp",EDGE,"E958"),sQuery(id+"F7.wireOp",EDGE,"E959"),sQuery(id+"F7.wireOp",EDGE,"E960"),sQuery(id+"F7.wireOp",EDGE,"E961"),sQuery(id+"F7.wireOp",EDGE,"E962"),sQuery(id+"F7.wireOp",EDGE,"E963"),sQuery(id+"F7.wireOp",EDGE,"E964"),sQuery(id+"F7.wireOp",EDGE,"E965"),sQuery(id+"F7.wireOp",EDGE,"E966"),sQuery(id+"F7.wireOp",EDGE,"E967"),sQuery(id+"F7.wireOp",EDGE,"E968"),sQuery(id+"F7.wireOp",EDGE,"E969"),sQuery(id+"F7.wireOp",EDGE,"E970"),sQuery(id+"F7.wireOp",EDGE,"E971"),sQuery(id+"F7.wireOp",EDGE,"E972"),sQuery(id+"F7.wireOp",EDGE,"E973"),sQuery(id+"F7.wireOp",EDGE,"E974"),sQuery(id+"F7.wireOp",EDGE,"E975"),sQuery(id+"F7.wireOp",EDGE,"E976"),sQuery(id+"F7.wireOp",EDGE,"E977"),sQuery(id+"F7.wireOp",EDGE,"E978"),sQuery(id+"F7.wireOp",EDGE,"E979"),sQuery(id+"F7.wireOp",EDGE,"E980"),sQuery(id+"F7.wireOp",EDGE,"E981"),sQuery(id+"F7.wireOp",EDGE,"E982"),sQuery(id+"F7.wireOp",EDGE,"E983"),sQuery(id+"F7.wireOp",EDGE,"E984"),sQuery(id+"F7.wireOp",EDGE,"E985"),sQuery(id+"F7.wireOp",EDGE,"E986"),sQuery(id+"F7.wireOp",EDGE,"E987"),sQuery(id+"F7.wireOp",EDGE,"E988"),sQuery(id+"F7.wireOp",EDGE,"E989"),sQuery(id+"F7.wireOp",EDGE,"E990"),sQuery(id+"F7.wireOp",EDGE,"E991"),sQuery(id+"F7.wireOp",EDGE,"E992"),sQuery(id+"F7.wireOp",EDGE,"E993"),sQuery(id+"F7.wireOp",EDGE,"E994"),sQuery(id+"F7.wireOp",EDGE,"E995"),sQuery(id+"F7.wireOp",EDGE,"E996"),sQuery(id+"F7.wireOp",EDGE,"E997"),sQuery(id+"F7.wireOp",EDGE,"E998"),sQuery(id+"F7.wireOp",EDGE,"E999"),sQuery(id+"F7.wireOp",EDGE,"E1000"),sQuery(id+"F7.wireOp",EDGE,"E1001"),sQuery(id+"F7.wireOp",EDGE,"E1002"),sQuery(id+"F7.wireOp",EDGE,"E1003"),sQuery(id+"F7.wireOp",EDGE,"E1004"),sQuery(id+"F7.wireOp",EDGE,"E1005"),sQuery(id+"F7.wireOp",EDGE,"E1006"),sQuery(id+"F7.wireOp",EDGE,"E1007"),sQuery(id+"F7.wireOp",EDGE,"E1008"),sQuery(id+"F7.wireOp",EDGE,"E1009"),sQuery(id+"F7.wireOp",EDGE,"E1010"),sQuery(id+"F7.wireOp",EDGE,"E1011"),sQuery(id+"F7.wireOp",EDGE,"E1012"),sQuery(id+"F7.wireOp",EDGE,"E1013"),sQuery(id+"F7.wireOp",EDGE,"E1014"),sQuery(id+"F7.wireOp",EDGE,"E1015"),sQuery(id+"F7.wireOp",EDGE,"E1016"),sQuery(id+"F7.wireOp",EDGE,"E1017"),sQuery(id+"F7.wireOp",EDGE,"E1018"),sQuery(id+"F7.wireOp",EDGE,"E1019"),sQuery(id+"F7.wireOp",EDGE,"E1020"),sQuery(id+"F7.wireOp",EDGE,"E1021"),sQuery(id+"F7.wireOp",EDGE,"E1022"),sQuery(id+"F7.wireOp",EDGE,"E1023"),sQuery(id+"F7.wireOp",EDGE,"E1024"),sQuery(id+"F7.wireOp",EDGE,"E1025"),sQuery(id+"F7.wireOp",EDGE,"E1026"),sQuery(id+"F7.wireOp",EDGE,"E1027"),sQuery(id+"F7.wireOp",EDGE,"E1028"),sQuery(id+"F7.wireOp",EDGE,"E1029"),sQuery(id+"F7.wireOp",EDGE,"E1030"),sQuery(id+"F7.wireOp",EDGE,"E1031"),sQuery(id+"F7.wireOp",EDGE,"E1032"),sQuery(id+"F7.wireOp",EDGE,"E1033"),sQuery(id+"F7.wireOp",EDGE,"E1034"),sQuery(id+"F7.wireOp",EDGE,"E1035"),sQuery(id+"F7.wireOp",EDGE,"E1036"),sQuery(id+"F7.wireOp",EDGE,"E1037"),sQuery(id+"F7.wireOp",EDGE,"E1038"),sQuery(id+"F7.wireOp",EDGE,"E1039"),sQuery(id+"F7.wireOp",EDGE,"E1040"),sQuery(id+"F7.wireOp",EDGE,"E1041"),sQuery(id+"F7.wireOp",EDGE,"E1042"),sQuery(id+"F7.wireOp",EDGE,"E1043"),sQuery(id+"F7.wireOp",EDGE,"E1044"),sQuery(id+"F7.wireOp",EDGE,"E1045"),sQuery(id+"F7.wireOp",EDGE,"E1046"),sQuery(id+"F7.wireOp",EDGE,"E1047"),sQuery(id+"F7.wireOp",EDGE,"E1048"),sQuery(id+"F7.wireOp",EDGE,"E1049"),sQuery(id+"F7.wireOp",EDGE,"E1050"),sQuery(id+"F7.wireOp",EDGE,"E1051"),sQuery(id+"F7.wireOp",EDGE,"E1052"),sQuery(id+"F7.wireOp",EDGE,"E1053"),sQuery(id+"F7.wireOp",EDGE,"E1054"),sQuery(id+"F7.wireOp",EDGE,"E1055"),sQuery(id+"F7.wireOp",EDGE,"E1056"),sQuery(id+"F7.wireOp",EDGE,"E1057"),sQuery(id+"F7.wireOp",EDGE,"E1058"),sQuery(id+"F7.wireOp",EDGE,"E1059"),sQuery(id+"F7.wireOp",EDGE,"E1060"),sQuery(id+"F7.wireOp",EDGE,"E1061"),sQuery(id+"F7.wireOp",EDGE,"E1062"),sQuery(id+"F7.wireOp",EDGE,"E1063"),sQuery(id+"F7.wireOp",EDGE,"E1064"),sQuery(id+"F7.wireOp",EDGE,"E1065"),sQuery(id+"F7.wireOp",EDGE,"E1066"),sQuery(id+"F7.wireOp",EDGE,"E1067"),sQuery(id+"F7.wireOp",EDGE,"E1068"),sQuery(id+"F7.wireOp",EDGE,"E1069"),sQuery(id+"F7.wireOp",EDGE,"E1070"),sQuery(id+"F7.wireOp",EDGE,"E1071"),sQuery(id+"F7.wireOp",EDGE,"E1072"),sQuery(id+"F7.wireOp",EDGE,"E1073"),sQuery(id+"F7.wireOp",EDGE,"E1074"),sQuery(id+"F7.wireOp",EDGE,"E1075"),sQuery(id+"F7.wireOp",EDGE,"E1076"),sQuery(id+"F7.wireOp",EDGE,"E1077"),sQuery(id+"F7.wireOp",EDGE,"E1078"),sQuery(id+"F7.wireOp",EDGE,"E1079"),sQuery(id+"F7.wireOp",EDGE,"E1080"),sQuery(id+"F7.wireOp",EDGE,"E1081"),sQuery(id+"F7.wireOp",EDGE,"E1082"),sQuery(id+"F7.wireOp",EDGE,"E1083"),sQuery(id+"F7.wireOp",EDGE,"E1084"),sQuery(id+"F7.wireOp",EDGE,"E1085"),sQuery(id+"F7.wireOp",EDGE,"E1086"),sQuery(id+"F7.wireOp",EDGE,"E1087"),sQuery(id+"F7.wireOp",EDGE,"E1088"),sQuery(id+"F7.wireOp",EDGE,"E1089"),sQuery(id+"F7.wireOp",EDGE,"E1090"),sQuery(id+"F7.wireOp",EDGE,"E1091"),sQuery(id+"F7.wireOp",EDGE,"E1092"),sQuery(id+"F7.wireOp",EDGE,"E1093"),sQuery(id+"F7.wireOp",EDGE,"E1094"),sQuery(id+"F7.wireOp",EDGE,"E1095"),sQuery(id+"F7.wireOp",EDGE,"E1096"),sQuery(id+"F7.wireOp",EDGE,"E1097"),sQuery(id+"F7.wireOp",EDGE,"E1098"),sQuery(id+"F7.wireOp",EDGE,"E1099"),sQuery(id+"F7.wireOp",EDGE,"E1100"),sQuery(id+"F7.wireOp",EDGE,"E1101"),sQuery(id+"F7.wireOp",EDGE,"E1102"),sQuery(id+"F7.wireOp",EDGE,"E1103"),sQuery(id+"F7.wireOp",EDGE,"E1104"),sQuery(id+"F7.wireOp",EDGE,"E1105"),sQuery(id+"F7.wireOp",EDGE,"E1106"),sQuery(id+"F7.wireOp",EDGE,"E1107"),sQuery(id+"F7.wireOp",EDGE,"E1108"),sQuery(id+"F7.wireOp",EDGE,"E1109"),sQuery(id+"F7.wireOp",EDGE,"E1110"),sQuery(id+"F7.wireOp",EDGE,"E1111"),sQuery(id+"F7.wireOp",EDGE,"E1112"),sQuery(id+"F7.wireOp",EDGE,"E1113"),sQuery(id+"F7.wireOp",EDGE,"E1114"),sQuery(id+"F7.wireOp",EDGE,"E1115"),sQuery(id+"F7.wireOp",EDGE,"E1116"),sQuery(id+"F7.wireOp",EDGE,"E1117"),sQuery(id+"F7.wireOp",EDGE,"E1118"),sQuery(id+"F7.wireOp",EDGE,"E1119"),sQuery(id+"F7.wireOp",EDGE,"E1120"),sQuery(id+"F7.wireOp",EDGE,"E1121"),sQuery(id+"F7.wireOp",EDGE,"E1122"),sQuery(id+"F7.wireOp",EDGE,"E1123"),sQuery(id+"F7.wireOp",EDGE,"E1124"),sQuery(id+"F7.wireOp",EDGE,"E1125"),sQuery(id+"F7.wireOp",EDGE,"E1126"),sQuery(id+"F7.wireOp",EDGE,"E1127"),sQuery(id+"F7.wireOp",EDGE,"E1128"),sQuery(id+"F7.wireOp",EDGE,"E1129"),sQuery(id+"F7.wireOp",EDGE,"E1130"),sQuery(id+"F7.wireOp",EDGE,"E1131"),sQuery(id+"F7.wireOp",EDGE,"E1132"),sQuery(id+"F7.wireOp",EDGE,"E1133"),sQuery(id+"F7.wireOp",EDGE,"E1134"),sQuery(id+"F7.wireOp",EDGE,"E1135"),sQuery(id+"F7.wireOp",EDGE,"E1136"),sQuery(id+"F7.wireOp",EDGE,"E1137"),sQuery(id+"F7.wireOp",EDGE,"E1138"),sQuery(id+"F7.wireOp",EDGE,"E1139"),sQuery(id+"F7.wireOp",EDGE,"E1140"),sQuery(id+"F7.wireOp",EDGE,"E1141"),sQuery(id+"F7.wireOp",EDGE,"E1142"),sQuery(id+"F7.wireOp",EDGE,"E1143"),sQuery(id+"F7.wireOp",EDGE,"E1144"),sQuery(id+"F7.wireOp",EDGE,"E1145"),sQuery(id+"F7.wireOp",EDGE,"E1146"),sQuery(id+"F7.wireOp",EDGE,"E1147"),sQuery(id+"F7.wireOp",EDGE,"E1148"),sQuery(id+"F7.wireOp",EDGE,"E1149"),sQuery(id+"F7.wireOp",EDGE,"E1150"),sQuery(id+"F7.wireOp",EDGE,"E1151"),sQuery(id+"F7.wireOp",EDGE,"E1152"),sQuery(id+"F7.wireOp",EDGE,"E1153"),sQuery(id+"F7.wireOp",EDGE,"E1154"),sQuery(id+"F7.wireOp",EDGE,"E1155"),sQuery(id+"F7.wireOp",EDGE,"E1156"),sQuery(id+"F7.wireOp",EDGE,"E1157"),sQuery(id+"F7.wireOp",EDGE,"E1158"),sQuery(id+"F7.wireOp",EDGE,"E1159"),sQuery(id+"F7.wireOp",EDGE,"E1160"),sQuery(id+"F7.wireOp",EDGE,"E1161"),sQuery(id+"F7.wireOp",EDGE,"E1162"),sQuery(id+"F7.wireOp",EDGE,"E1163"),sQuery(id+"F7.wireOp",EDGE,"E1164"),sQuery(id+"F7.wireOp",EDGE,"E1165"),sQuery(id+"F7.wireOp",EDGE,"E1166"),sQuery(id+"F7.wireOp",EDGE,"E1167"),sQuery(id+"F7.wireOp",EDGE,"E1168"),sQuery(id+"F7.wireOp",EDGE,"E1169"),sQuery(id+"F7.wireOp",EDGE,"E1170"),sQuery(id+"F7.wireOp",EDGE,"E1171"),sQuery(id+"F7.wireOp",EDGE,"E1172"),sQuery(id+"F7.wireOp",EDGE,"E1173"),sQuery(id+"F7.wireOp",EDGE,"E1174"),sQuery(id+"F7.wireOp",EDGE,"E1175"),sQuery(id+"F7.wireOp",EDGE,"E1176"),sQuery(id+"F7.wireOp",EDGE,"E1177"),sQuery(id+"F7.wireOp",EDGE,"E1178"),sQuery(id+"F7.wireOp",EDGE,"E1179"),sQuery(id+"F7.wireOp",EDGE,"E1180"),sQuery(id+"F7.wireOp",EDGE,"E1181"),sQuery(id+"F7.wireOp",EDGE,"E1182"),sQuery(id+"F7.wireOp",EDGE,"E1183"),sQuery(id+"F7.wireOp",EDGE,"E1184"),sQuery(id+"F7.wireOp",EDGE,"E1185"),sQuery(id+"F7.wireOp",EDGE,"E1186"),sQuery(id+"F7.wireOp",EDGE,"E1187"),sQuery(id+"F7.wireOp",EDGE,"E1188"),sQuery(id+"F7.wireOp",EDGE,"E1189"),sQuery(id+"F7.wireOp",EDGE,"E1190"),sQuery(id+"F7.wireOp",EDGE,"E1191"),sQuery(id+"F7.wireOp",EDGE,"E1192"),sQuery(id+"F7.wireOp",EDGE,"E1193"),sQuery(id+"F7.wireOp",EDGE,"E1194"),sQuery(id+"F7.wireOp",EDGE,"E1195"),sQuery(id+"F7.wireOp",EDGE,"E1196"),sQuery(id+"F7.wireOp",EDGE,"E1197"),sQuery(id+"F7.wireOp",EDGE,"E1198"),sQuery(id+"F7.wireOp",EDGE,"E1199"),sQuery(id+"F7.wireOp",EDGE,"E1200"),sQuery(id+"F7.wireOp",EDGE,"E1201"),sQuery(id+"F7.wireOp",EDGE,"E1202"),sQuery(id+"F7.wireOp",EDGE,"E1203"),sQuery(id+"F7.wireOp",EDGE,"E1204"),sQuery(id+"F7.wireOp",EDGE,"E1205"),sQuery(id+"F7.wireOp",EDGE,"E1206"),sQuery(id+"F7.wireOp",EDGE,"E1207"),sQuery(id+"F7.wireOp",EDGE,"E1208"),sQuery(id+"F7.wireOp",EDGE,"E1209"),sQuery(id+"F7.wireOp",EDGE,"E1210"),sQuery(id+"F7.wireOp",EDGE,"E1211"),sQuery(id+"F7.wireOp",EDGE,"E1212"),sQuery(id+"F7.wireOp",EDGE,"E1213"),sQuery(id+"F7.wireOp",EDGE,"E1214"),sQuery(id+"F7.wireOp",EDGE,"E1215"),sQuery(id+"F7.wireOp",EDGE,"E1216"),sQuery(id+"F7.wireOp",EDGE,"E1217"),sQuery(id+"F7.wireOp",EDGE,"E1218"),sQuery(id+"F7.wireOp",EDGE,"E1219"),sQuery(id+"F7.wireOp",EDGE,"E1220"),sQuery(id+"F7.wireOp",EDGE,"E1221"),sQuery(id+"F7.wireOp",EDGE,"E1222"),sQuery(id+"F7.wireOp",EDGE,"E1223"),sQuery(id+"F7.wireOp",EDGE,"E1224"),sQuery(id+"F7.wireOp",EDGE,"E1225"),sQuery(id+"F7.wireOp",EDGE,"E1226"),sQuery(id+"F7.wireOp",EDGE,"E1227"),sQuery(id+"F7.wireOp",EDGE,"E1228"),sQuery(id+"F7.wireOp",EDGE,"E1229"),sQuery(id+"F7.wireOp",EDGE,"E1230"),sQuery(id+"F7.wireOp",EDGE,"E1231"),sQuery(id+"F7.wireOp",EDGE,"E1232"),sQuery(id+"F7.wireOp",EDGE,"E1233"),sQuery(id+"F7.wireOp",EDGE,"E1234"),sQuery(id+"F7.wireOp",EDGE,"E1235"),sQuery(id+"F7.wireOp",EDGE,"E1236"),sQuery(id+"F7.wireOp",EDGE,"E1237"),sQuery(id+"F7.wireOp",EDGE,"E1238"),sQuery(id+"F7.wireOp",EDGE,"E1239"),sQuery(id+"F7.wireOp",EDGE,"E1240"),sQuery(id+"F7.wireOp",EDGE,"E1241"),sQuery(id+"F7.wireOp",EDGE,"E1242"),sQuery(id+"F7.wireOp",EDGE,"E1243"),sQuery(id+"F7.wireOp",EDGE,"E1244"),sQuery(id+"F7.wireOp",EDGE,"E1245"),sQuery(id+"F7.wireOp",EDGE,"E1246"),sQuery(id+"F7.wireOp",EDGE,"E1247"),sQuery(id+"F7.wireOp",EDGE,"E1248"),sQuery(id+"F7.wireOp",EDGE,"E1249"),sQuery(id+"F7.wireOp",EDGE,"E1250"),sQuery(id+"F7.wireOp",EDGE,"E1251"),sQuery(id+"F7.wireOp",EDGE,"E1252"),sQuery(id+"F7.wireOp",EDGE,"E1253"),sQuery(id+"F7.wireOp",EDGE,"E1254"),sQuery(id+"F7.wireOp",EDGE,"E1255"),sQuery(id+"F7.wireOp",EDGE,"E1256"),sQuery(id+"F7.wireOp",EDGE,"E1257"),sQuery(id+"F7.wireOp",EDGE,"E1258"),sQuery(id+"F7.wireOp",EDGE,"E1259"),sQuery(id+"F7.wireOp",EDGE,"E1260"),sQuery(id+"F7.wireOp",EDGE,"E1261"),sQuery(id+"F7.wireOp",EDGE,"E1262"),sQuery(id+"F7.wireOp",EDGE,"E1263"),sQuery(id+"F7.wireOp",EDGE,"E1264"),sQuery(id+"F7.wireOp",EDGE,"E1265"),sQuery(id+"F7.wireOp",EDGE,"E1266"),sQuery(id+"F7.wireOp",EDGE,"E1267"),sQuery(id+"F7.wireOp",EDGE,"E1268"),sQuery(id+"F7.wireOp",EDGE,"E1269"),sQuery(id+"F7.wireOp",EDGE,"E1270"),sQuery(id+"F7.wireOp",EDGE,"E1271"),sQuery(id+"F7.wireOp",EDGE,"E1272"),sQuery(id+"F7.wireOp",EDGE,"E1273"),sQuery(id+"F7.wireOp",EDGE,"E1274"),sQuery(id+"F7.wireOp",EDGE,"E1275"),sQuery(id+"F7.wireOp",EDGE,"E1276"),sQuery(id+"F7.wireOp",EDGE,"E1277"),sQuery(id+"F7.wireOp",EDGE,"E1278"),sQuery(id+"F7.wireOp",EDGE,"E1279"),sQuery(id+"F7.wireOp",EDGE,"E1280"),sQuery(id+"F7.wireOp",EDGE,"E1281"),sQuery(id+"F7.wireOp",EDGE,"E1282"),sQuery(id+"F7.wireOp",EDGE,"E1283"),sQuery(id+"F7.wireOp",EDGE,"E1284"),sQuery(id+"F7.wireOp",EDGE,"E1285"),sQuery(id+"F7.wireOp",EDGE,"E1286"),sQuery(id+"F7.wireOp",EDGE,"E1287"),sQuery(id+"F7.wireOp",EDGE,"E1288"),sQuery(id+"F7.wireOp",EDGE,"E1289"),sQuery(id+"F7.wireOp",EDGE,"E1290"),sQuery(id+"F7.wireOp",EDGE,"E1291"),sQuery(id+"F7.wireOp",EDGE,"E1292"),sQuery(id+"F7.wireOp",EDGE,"E1293"),sQuery(id+"F7.wireOp",EDGE,"E1294"),sQuery(id+"F7.wireOp",EDGE,"E1295"),sQuery(id+"F7.wireOp",EDGE,"E1296"),sQuery(id+"F7.wireOp",EDGE,"E1297"),sQuery(id+"F7.wireOp",EDGE,"E1298"),sQuery(id+"F7.wireOp",EDGE,"E1299"),sQuery(id+"F7.wireOp",EDGE,"E1300"),sQuery(id+"F7.wireOp",EDGE,"E1301"),sQuery(id+"F7.wireOp",EDGE,"E1302"),sQuery(id+"F7.wireOp",EDGE,"E1303"),sQuery(id+"F7.wireOp",EDGE,"E1304"),sQuery(id+"F7.wireOp",EDGE,"E1305"),sQuery(id+"F7.wireOp",EDGE,"E1306"),sQuery(id+"F7.wireOp",EDGE,"E1307"),sQuery(id+"F7.wireOp",EDGE,"E1308"),sQuery(id+"F7.wireOp",EDGE,"E1309"),sQuery(id+"F7.wireOp",EDGE,"E1310"),sQuery(id+"F7.wireOp",EDGE,"E1311"),sQuery(id+"F7.wireOp",EDGE,"E1312"),sQuery(id+"F7.wireOp",EDGE,"E1313"),sQuery(id+"F7.wireOp",EDGE,"E1314"),sQuery(id+"F7.wireOp",EDGE,"E1315"),sQuery(id+"F7.wireOp",EDGE,"E1316"),sQuery(id+"F7.wireOp",EDGE,"E1317"),sQuery(id+"F7.wireOp",EDGE,"E1318"),sQuery(id+"F7.wireOp",EDGE,"E1319"),sQuery(id+"F7.wireOp",EDGE,"E1320"),sQuery(id+"F7.wireOp",EDGE,"E1321"),sQuery(id+"F7.wireOp",EDGE,"E1322"),sQuery(id+"F7.wireOp",EDGE,"E1323"),sQuery(id+"F7.wireOp",EDGE,"E1324"),sQuery(id+"F7.wireOp",EDGE,"E1325"),sQuery(id+"F7.wireOp",EDGE,"E1326"),sQuery(id+"F7.wireOp",EDGE,"E1327"),sQuery(id+"F7.wireOp",EDGE,"E1328"),sQuery(id+"F7.wireOp",EDGE,"E1329"),sQuery(id+"F7.wireOp",EDGE,"E1330"),sQuery(id+"F7.wireOp",EDGE,"E1331"),sQuery(id+"F7.wireOp",EDGE,"E1332"),sQuery(id+"F7.wireOp",EDGE,"E1333"),sQuery(id+"F7.wireOp",EDGE,"E1334"),sQuery(id+"F7.wireOp",EDGE,"E1335"),sQuery(id+"F7.wireOp",EDGE,"E1336"),sQuery(id+"F7.wireOp",EDGE,"E1337"),sQuery(id+"F7.wireOp",EDGE,"E1338"),sQuery(id+"F7.wireOp",EDGE,"E1339"),sQuery(id+"F7.wireOp",EDGE,"E1340"),sQuery(id+"F7.wireOp",EDGE,"E1341"),sQuery(id+"F7.wireOp",EDGE,"E1342"),sQuery(id+"F7.wireOp",EDGE,"E1343"),sQuery(id+"F7.wireOp",EDGE,"E1344"),sQuery(id+"F7.wireOp",EDGE,"E1345"),sQuery(id+"F7.wireOp",EDGE,"E1346"),sQuery(id+"F7.wireOp",EDGE,"E1347"),sQuery(id+"F7.wireOp",EDGE,"E1348"),sQuery(id+"F7.wireOp",EDGE,"E1349"),sQuery(id+"F7.wireOp",EDGE,"E1350"),sQuery(id+"F7.wireOp",EDGE,"E1351"),sQuery(id+"F7.wireOp",EDGE,"E1352"),sQuery(id+"F7.wireOp",EDGE,"E1353"),sQuery(id+"F7.wireOp",EDGE,"E1354"),sQuery(id+"F7.wireOp",EDGE,"E1355"),sQuery(id+"F7.wireOp",EDGE,"E1356"),sQuery(id+"F7.wireOp",EDGE,"E1357"),sQuery(id+"F7.wireOp",EDGE,"E1358"),sQuery(id+"F7.wireOp",EDGE,"E1359"),sQuery(id+"F7.wireOp",EDGE,"E1360"),sQuery(id+"F7.wireOp",EDGE,"E1361"),sQuery(id+"F7.wireOp",EDGE,"E1362"),sQuery(id+"F7.wireOp",EDGE,"E1363"),sQuery(id+"F7.wireOp",EDGE,"E1364"),sQuery(id+"F7.wireOp",EDGE,"E1365"),sQuery(id+"F7.wireOp",EDGE,"E1366"),sQuery(id+"F7.wireOp",EDGE,"E1367"),sQuery(id+"F7.wireOp",EDGE,"E1368"),sQuery(id+"F7.wireOp",EDGE,"E1369"),sQuery(id+"F7.wireOp",EDGE,"E1370"),sQuery(id+"F7.wireOp",EDGE,"E1371"),sQuery(id+"F7.wireOp",EDGE,"E1372"),sQuery(id+"F7.wireOp",EDGE,"E1373"),sQuery(id+"F7.wireOp",EDGE,"E1374"),sQuery(id+"F7.wireOp",EDGE,"E1375"),sQuery(id+"F7.wireOp",EDGE,"E1376"),sQuery(id+"F7.wireOp",EDGE,"E1377"),sQuery(id+"F7.wireOp",EDGE,"E1378"),sQuery(id+"F7.wireOp",EDGE,"E1379"),sQuery(id+"F7.wireOp",EDGE,"E1380"),sQuery(id+"F7.wireOp",EDGE,"E1381"),sQuery(id+"F7.wireOp",EDGE,"E1382"),sQuery(id+"F7.wireOp",EDGE,"E1383"),sQuery(id+"F7.wireOp",EDGE,"E1384"),sQuery(id+"F7.wireOp",EDGE,"E1385"),sQuery(id+"F7.wireOp",EDGE,"E1386"),sQuery(id+"F7.wireOp",EDGE,"E1387"),sQuery(id+"F7.wireOp",EDGE,"E1388"),sQuery(id+"F7.wireOp",EDGE,"E1389"),sQuery(id+"F7.wireOp",EDGE,"E1390"),sQuery(id+"F7.wireOp",EDGE,"E1391"),sQuery(id+"F7.wireOp",EDGE,"E1392"),sQuery(id+"F7.wireOp",EDGE,"E1393"),sQuery(id+"F7.wireOp",EDGE,"E1394"),sQuery(id+"F7.wireOp",EDGE,"E1395"),sQuery(id+"F7.wireOp",EDGE,"E1396"),sQuery(id+"F7.wireOp",EDGE,"E1397"),sQuery(id+"F7.wireOp",EDGE,"E1398"),sQuery(id+"F7.wireOp",EDGE,"E1399"),sQuery(id+"F7.wireOp",EDGE,"E1400"),sQuery(id+"F7.wireOp",EDGE,"E1401"),sQuery(id+"F7.wireOp",EDGE,"E1402"),sQuery(id+"F7.wireOp",EDGE,"E1403"),sQuery(id+"F7.wireOp",EDGE,"E1404"),sQuery(id+"F7.wireOp",EDGE,"E1405"),sQuery(id+"F7.wireOp",EDGE,"E1406"),sQuery(id+"F7.wireOp",EDGE,"E1407"),sQuery(id+"F7.wireOp",EDGE,"E1408"),sQuery(id+"F7.wireOp",EDGE,"E1409"),sQuery(id+"F7.wireOp",EDGE,"E1410"),sQuery(id+"F7.wireOp",EDGE,"E1411"),sQuery(id+"F7.wireOp",EDGE,"E1412"),sQuery(id+"F7.wireOp",EDGE,"E1413"),sQuery(id+"F7.wireOp",EDGE,"E1414"),sQuery(id+"F7.wireOp",EDGE,"E1415"),sQuery(id+"F7.wireOp",EDGE,"E1416"),sQuery(id+"F7.wireOp",EDGE,"E1417"),sQuery(id+"F7.wireOp",EDGE,"E1418"),sQuery(id+"F7.wireOp",EDGE,"E1419"),sQuery(id+"F7.wireOp",EDGE,"E1420"),sQuery(id+"F7.wireOp",EDGE,"E1421"),sQuery(id+"F7.wireOp",EDGE,"E1422"),sQuery(id+"F7.wireOp",EDGE,"E1423"),sQuery(id+"F7.wireOp",EDGE,"E1424"),sQuery(id+"F7.wireOp",EDGE,"E1425"),sQuery(id+"F7.wireOp",EDGE,"E1426"),sQuery(id+"F7.wireOp",EDGE,"E1427"),sQuery(id+"F7.wireOp",EDGE,"E1428"),sQuery(id+"F7.wireOp",EDGE,"E1429"),sQuery(id+"F7.wireOp",EDGE,"E1430"),sQuery(id+"F7.wireOp",EDGE,"E1431"),sQuery(id+"F7.wireOp",EDGE,"E1432"),sQuery(id+"F7.wireOp",EDGE,"E1433"),sQuery(id+"F7.wireOp",EDGE,"E1434"),sQuery(id+"F7.wireOp",EDGE,"E1435"),sQuery(id+"F7.wireOp",EDGE,"E1436"),sQuery(id+"F7.wireOp",EDGE,"E1437"),sQuery(id+"F7.wireOp",EDGE,"E1438"),sQuery(id+"F7.wireOp",EDGE,"E1439"),sQuery(id+"F7.wireOp",EDGE,"E1440"),sQuery(id+"F7.wireOp",EDGE,"E1441"),sQuery(id+"F7.wireOp",EDGE,"E1442"),sQuery(id+"F7.wireOp",EDGE,"E1443"),sQuery(id+"F7.wireOp",EDGE,"E1444"),sQuery(id+"F7.wireOp",EDGE,"E1445"),sQuery(id+"F7.wireOp",EDGE,"E1446"),sQuery(id+"F7.wireOp",EDGE,"E1447"),sQuery(id+"F7.wireOp",EDGE,"E1448"),sQuery(id+"F7.wireOp",EDGE,"E1449"),sQuery(id+"F7.wireOp",EDGE,"E1450"),sQuery(id+"F7.wireOp",EDGE,"E1451"),sQuery(id+"F7.wireOp",EDGE,"E1452"),sQuery(id+"F7.wireOp",EDGE,"E1453"),sQuery(id+"F7.wireOp",EDGE,"E1454"),sQuery(id+"F7.wireOp",EDGE,"E1455"),sQuery(id+"F7.wireOp",EDGE,"E1456"),sQuery(id+"F7.wireOp",EDGE,"E1457"),sQuery(id+"F7.wireOp",EDGE,"E1458"),sQuery(id+"F7.wireOp",EDGE,"E1459"),sQuery(id+"F7.wireOp",EDGE,"E1460"),sQuery(id+"F7.wireOp",EDGE,"E1461"),sQuery(id+"F7.wireOp",EDGE,"E1462"),sQuery(id+"F7.wireOp",EDGE,"E1463"),sQuery(id+"F7.wireOp",EDGE,"E1464"),sQuery(id+"F7.wireOp",EDGE,"E1465"),sQuery(id+"F7.wireOp",EDGE,"E1466"),sQuery(id+"F7.wireOp",EDGE,"E1467"),sQuery(id+"F7.wireOp",EDGE,"E1468"),sQuery(id+"F7.wireOp",EDGE,"E1469"),sQuery(id+"F7.wireOp",EDGE,"E1470"),sQuery(id+"F7.wireOp",EDGE,"E1471"),sQuery(id+"F7.wireOp",EDGE,"E1472"),sQuery(id+"F7.wireOp",EDGE,"E1473"),sQuery(id+"F7.wireOp",EDGE,"E1474"),sQuery(id+"F7.wireOp",EDGE,"E1475"),sQuery(id+"F7.wireOp",EDGE,"E1476"),sQuery(id+"F7.wireOp",EDGE,"E1477"),sQuery(id+"F7.wireOp",EDGE,"E1478"),sQuery(id+"F7.wireOp",EDGE,"E1479"),sQuery(id+"F7.wireOp",EDGE,"E1480"),sQuery(id+"F7.wireOp",EDGE,"E1481"),sQuery(id+"F7.wireOp",EDGE,"E1482"),sQuery(id+"F7.wireOp",EDGE,"E1483"),sQuery(id+"F7.wireOp",EDGE,"E1484"),sQuery(id+"F7.wireOp",EDGE,"E1485"),sQuery(id+"F7.wireOp",EDGE,"E1486"),sQuery(id+"F7.wireOp",EDGE,"E1487"),sQuery(id+"F7.wireOp",EDGE,"E1488"),sQuery(id+"F7.wireOp",EDGE,"E1489"),sQuery(id+"F7.wireOp",EDGE,"E1490"),sQuery(id+"F7.wireOp",EDGE,"E1491"),sQuery(id+"F7.wireOp",EDGE,"E1492"),sQuery(id+"F7.wireOp",EDGE,"E1493"),sQuery(id+"F7.wireOp",EDGE,"E1494"),sQuery(id+"F7.wireOp",EDGE,"E1495"),sQuery(id+"F7.wireOp",EDGE,"E1496"),sQuery(id+"F7.wireOp",EDGE,"E1497"),sQuery(id+"F7.wireOp",EDGE,"E1498"),sQuery(id+"F7.wireOp",EDGE,"E1499"),sQuery(id+"F7.wireOp",EDGE,"E1500"),sQuery(id+"F7.wireOp",EDGE,"E1501"),sQuery(id+"F7.wireOp",EDGE,"E1502"),sQuery(id+"F7.wireOp",EDGE,"E1503"),sQuery(id+"F7.wireOp",EDGE,"E1504"),sQuery(id+"F7.wireOp",EDGE,"E1505"),sQuery(id+"F7.wireOp",EDGE,"E1506"),sQuery(id+"F7.wireOp",EDGE,"E1507"),sQuery(id+"F7.wireOp",EDGE,"E1508"),sQuery(id+"F7.wireOp",EDGE,"E1509"),sQuery(id+"F7.wireOp",EDGE,"E1510"),sQuery(id+"F7.wireOp",EDGE,"E1511"),sQuery(id+"F7.wireOp",EDGE,"E1512"),sQuery(id+"F7.wireOp",EDGE,"E1513"),sQuery(id+"F7.wireOp",EDGE,"E1514"),sQuery(id+"F7.wireOp",EDGE,"E1515"),sQuery(id+"F7.wireOp",EDGE,"E1516"),sQuery(id+"F7.wireOp",EDGE,"E1517"),sQuery(id+"F7.wireOp",EDGE,"E1518"),sQuery(id+"F7.wireOp",EDGE,"E1519"),sQuery(id+"F7.wireOp",EDGE,"E1520"),sQuery(id+"F7.wireOp",EDGE,"E1521"),sQuery(id+"F7.wireOp",EDGE,"E1522"),sQuery(id+"F7.wireOp",EDGE,"E1523"),sQuery(id+"F7.wireOp",EDGE,"E1524"),sQuery(id+"F7.wireOp",EDGE,"E1525"),sQuery(id+"F7.wireOp",EDGE,"E1526"),sQuery(id+"F7.wireOp",EDGE,"E1527"),sQuery(id+"F7.wireOp",EDGE,"E1528"),sQuery(id+"F7.wireOp",EDGE,"E1529"),sQuery(id+"F7.wireOp",EDGE,"E1530"),sQuery(id+"F7.wireOp",EDGE,"E1531"),sQuery(id+"F7.wireOp",EDGE,"E1532"),sQuery(id+"F7.wireOp",EDGE,"E1533"),sQuery(id+"F7.wireOp",EDGE,"E1534"),sQuery(id+"F7.wireOp",EDGE,"E1535"),sQuery(id+"F7.wireOp",EDGE,"E1536"),sQuery(id+"F7.wireOp",EDGE,"E1537"),sQuery(id+"F7.wireOp",EDGE,"E1538"),sQuery(id+"F7.wireOp",EDGE,"E1539"),sQuery(id+"F7.wireOp",EDGE,"E1540"),sQuery(id+"F7.wireOp",EDGE,"E1541"),sQuery(id+"F7.wireOp",EDGE,"E1542"),sQuery(id+"F7.wireOp",EDGE,"E1543"),sQuery(id+"F7.wireOp",EDGE,"E1544"),sQuery(id+"F7.wireOp",EDGE,"E1545"),sQuery(id+"F7.wireOp",EDGE,"E1546"),sQuery(id+"F7.wireOp",EDGE,"E1547"),sQuery(id+"F7.wireOp",EDGE,"E1548"),sQuery(id+"F7.wireOp",EDGE,"E1549"),sQuery(id+"F7.wireOp",EDGE,"E1550"),sQuery(id+"F7.wireOp",EDGE,"E1551"),sQuery(id+"F7.wireOp",EDGE,"E1552"),sQuery(id+"F7.wireOp",EDGE,"E1553"),sQuery(id+"F7.wireOp",EDGE,"E1554"),sQuery(id+"F7.wireOp",EDGE,"E1555"),sQuery(id+"F7.wireOp",EDGE,"E1556"),sQuery(id+"F7.wireOp",EDGE,"E1557"),sQuery(id+"F7.wireOp",EDGE,"E1558"),sQuery(id+"F7.wireOp",EDGE,"E1559"),sQuery(id+"F7.wireOp",EDGE,"E1560"),sQuery(id+"F7.wireOp",EDGE,"E1561"),sQuery(id+"F7.wireOp",EDGE,"E1562"),sQuery(id+"F7.wireOp",EDGE,"E1563"),sQuery(id+"F7.wireOp",EDGE,"E1564"),sQuery(id+"F7.wireOp",EDGE,"E1565"),sQuery(id+"F7.wireOp",EDGE,"E1566"),sQuery(id+"F7.wireOp",EDGE,"E1567"),sQuery(id+"F7.wireOp",EDGE,"E1568"),sQuery(id+"F7.wireOp",EDGE,"E1569"),sQuery(id+"F7.wireOp",EDGE,"E1570"),sQuery(id+"F7.wireOp",EDGE,"E1571"),sQuery(id+"F7.wireOp",EDGE,"E1572"),sQuery(id+"F7.wireOp",EDGE,"E1573"),sQuery(id+"F7.wireOp",EDGE,"E1574"),sQuery(id+"F7.wireOp",EDGE,"E1575"),sQuery(id+"F7.wireOp",EDGE,"E1576"),sQuery(id+"F7.wireOp",EDGE,"E1577"),sQuery(id+"F7.wireOp",EDGE,"E1578"),sQuery(id+"F7.wireOp",EDGE,"E1579"),sQuery(id+"F7.wireOp",EDGE,"E1580"),sQuery(id+"F7.wireOp",EDGE,"E1581"),sQuery(id+"F7.wireOp",EDGE,"E1582"),sQuery(id+"F7.wireOp",EDGE,"E1583"),sQuery(id+"F7.wireOp",EDGE,"E1584"),sQuery(id+"F7.wireOp",EDGE,"E1585"),sQuery(id+"F7.wireOp",EDGE,"E1586"),sQuery(id+"F7.wireOp",EDGE,"E1587"),sQuery(id+"F7.wireOp",EDGE,"E1588"),sQuery(id+"F7.wireOp",EDGE,"E1589"),sQuery(id+"F7.wireOp",EDGE,"E1590"),sQuery(id+"F7.wireOp",EDGE,"E1591"),sQuery(id+"F7.wireOp",EDGE,"E1592"),sQuery(id+"F7.wireOp",EDGE,"E1593"),sQuery(id+"F7.wireOp",EDGE,"E1594"),sQuery(id+"F7.wireOp",EDGE,"E1595"),sQuery(id+"F7.wireOp",EDGE,"E1596"),sQuery(id+"F7.wireOp",EDGE,"E1597"),sQuery(id+"F7.wireOp",EDGE,"E1598"),sQuery(id+"F7.wireOp",EDGE,"E1599"),sQuery(id+"F7.wireOp",EDGE,"E1600"),sQuery(id+"F7.wireOp",EDGE,"E1601"),sQuery(id+"F7.wireOp",EDGE,"E1602"),sQuery(id+"F7.wireOp",EDGE,"E1603"),sQuery(id+"F7.wireOp",EDGE,"E1604"),sQuery(id+"F7.wireOp",EDGE,"E1605"),sQuery(id+"F7.wireOp",EDGE,"E1606"),sQuery(id+"F7.wireOp",EDGE,"E1607"),sQuery(id+"F7.wireOp",EDGE,"E1608"),sQuery(id+"F7.wireOp",EDGE,"E1609"),sQuery(id+"F7.wireOp",EDGE,"E1610"),sQuery(id+"F7.wireOp",EDGE,"E1611"),sQuery(id+"F7.wireOp",EDGE,"E1612"),sQuery(id+"F7.wireOp",EDGE,"E1613"),sQuery(id+"F7.wireOp",EDGE,"E1614"),sQuery(id+"F7.wireOp",EDGE,"E1615"),sQuery(id+"F7.wireOp",EDGE,"E1616"),sQuery(id+"F7.wireOp",EDGE,"E1617"),sQuery(id+"F7.wireOp",EDGE,"E1618"),sQuery(id+"F7.wireOp",EDGE,"E1619"),sQuery(id+"F7.wireOp",EDGE,"E1620"),sQuery(id+"F7.wireOp",EDGE,"E1621"),sQuery(id+"F7.wireOp",EDGE,"E1622"),sQuery(id+"F7.wireOp",EDGE,"E1623"),sQuery(id+"F7.wireOp",EDGE,"E1624"),sQuery(id+"F7.wireOp",EDGE,"E1625"),sQuery(id+"F7.wireOp",EDGE,"E1626"),sQuery(id+"F7.wireOp",EDGE,"E1627"),sQuery(id+"F7.wireOp",EDGE,"E1628"),sQuery(id+"F7.wireOp",EDGE,"E1629"),sQuery(id+"F7.wireOp",EDGE,"E1630"),sQuery(id+"F7.wireOp",EDGE,"E1631"),sQuery(id+"F7.wireOp",EDGE,"E1632"),sQuery(id+"F7.wireOp",EDGE,"E1633"),sQuery(id+"F7.wireOp",EDGE,"E1634"),sQuery(id+"F7.wireOp",EDGE,"E1635"),sQuery(id+"F7.wireOp",EDGE,"E1636"),sQuery(id+"F7.wireOp",EDGE,"E1637"),sQuery(id+"F7.wireOp",EDGE,"E1638"),sQuery(id+"F7.wireOp",EDGE,"E1639"),sQuery(id+"F7.wireOp",EDGE,"E1640"),sQuery(id+"F7.wireOp",EDGE,"E1641"),sQuery(id+"F7.wireOp",EDGE,"E1642"),sQuery(id+"F7.wireOp",EDGE,"E1643"),sQuery(id+"F7.wireOp",EDGE,"E1644"),sQuery(id+"F7.wireOp",EDGE,"E1645"),sQuery(id+"F7.wireOp",EDGE,"E1646"),sQuery(id+"F7.wireOp",EDGE,"E1647"),sQuery(id+"F7.wireOp",EDGE,"E1648"),sQuery(id+"F7.wireOp",EDGE,"E1649"),sQuery(id+"F7.wireOp",EDGE,"E1650"),sQuery(id+"F7.wireOp",EDGE,"E1651"),sQuery(id+"F7.wireOp",EDGE,"E1652"),sQuery(id+"F7.wireOp",EDGE,"E1653"),sQuery(id+"F7.wireOp",EDGE,"E1654"),sQuery(id+"F7.wireOp",EDGE,"E1655"),sQuery(id+"F7.wireOp",EDGE,"E1656"),sQuery(id+"F7.wireOp",EDGE,"E1657"),sQuery(id+"F7.wireOp",EDGE,"E1658"),sQuery(id+"F7.wireOp",EDGE,"E1659"),sQuery(id+"F7.wireOp",EDGE,"E1660"),sQuery(id+"F7.wireOp",EDGE,"E1661"),sQuery(id+"F7.wireOp",EDGE,"E1662"),sQuery(id+"F7.wireOp",EDGE,"E1663"),sQuery(id+"F7.wireOp",EDGE,"E1664"),sQuery(id+"F7.wireOp",EDGE,"E1665"),sQuery(id+"F7.wireOp",EDGE,"E1666"),sQuery(id+"F7.wireOp",EDGE,"E1667"),sQuery(id+"F7.wireOp",EDGE,"E1668"),sQuery(id+"F7.wireOp",EDGE,"E1669"),sQuery(id+"F7.wireOp",EDGE,"E1670"),sQuery(id+"F7.wireOp",EDGE,"E1671"),sQuery(id+"F7.wireOp",EDGE,"E1672"),sQuery(id+"F7.wireOp",EDGE,"E1673"),sQuery(id+"F7.wireOp",EDGE,"E1674"),sQuery(id+"F7.wireOp",EDGE,"E1675"),sQuery(id+"F7.wireOp",EDGE,"E1676"),sQuery(id+"F7.wireOp",EDGE,"E1677"),sQuery(id+"F7.wireOp",EDGE,"E1678"),sQuery(id+"F7.wireOp",EDGE,"E1679"),sQuery(id+"F7.wireOp",EDGE,"E1680"),sQuery(id+"F7.wireOp",EDGE,"E1681"),sQuery(id+"F7.wireOp",EDGE,"E1682"),sQuery(id+"F7.wireOp",EDGE,"E1683"),sQuery(id+"F7.wireOp",EDGE,"E1684"),sQuery(id+"F7.wireOp",EDGE,"E1685"),sQuery(id+"F7.wireOp",EDGE,"E1686"),sQuery(id+"F7.wireOp",EDGE,"E1687"),sQuery(id+"F7.wireOp",EDGE,"E1688"),sQuery(id+"F7.wireOp",EDGE,"E1689"),sQuery(id+"F7.wireOp",EDGE,"E1690"),sQuery(id+"F7.wireOp",EDGE,"E1691"),sQuery(id+"F7.wireOp",EDGE,"E1692"),sQuery(id+"F7.wireOp",EDGE,"E1693"),sQuery(id+"F7.wireOp",EDGE,"E1694"),sQuery(id+"F7.wireOp",EDGE,"E1695"),sQuery(id+"F7.wireOp",EDGE,"E1696"),sQuery(id+"F7.wireOp",EDGE,"E1697"),sQuery(id+"F7.wireOp",EDGE,"E1698"),sQuery(id+"F7.wireOp",EDGE,"E1699"),sQuery(id+"F7.wireOp",EDGE,"E1700"),sQuery(id+"F7.wireOp",EDGE,"E1701"),sQuery(id+"F7.wireOp",EDGE,"E1702"),sQuery(id+"F7.wireOp",EDGE,"E1703"),sQuery(id+"F7.wireOp",EDGE,"E1704"),sQuery(id+"F7.wireOp",EDGE,"E1705"),sQuery(id+"F7.wireOp",EDGE,"E1706"),sQuery(id+"F7.wireOp",EDGE,"E1707"),sQuery(id+"F7.wireOp",EDGE,"E1708"),sQuery(id+"F7.wireOp",EDGE,"E1709"),sQuery(id+"F7.wireOp",EDGE,"E1710"),sQuery(id+"F7.wireOp",EDGE,"E1711"),sQuery(id+"F7.wireOp",EDGE,"E1712"),sQuery(id+"F7.wireOp",EDGE,"E1713"),sQuery(id+"F7.wireOp",EDGE,"E1714"),sQuery(id+"F7.wireOp",EDGE,"E1715"),sQuery(id+"F7.wireOp",EDGE,"E1716"),sQuery(id+"F7.wireOp",EDGE,"E1717"),sQuery(id+"F7.wireOp",EDGE,"E1718"),sQuery(id+"F7.wireOp",EDGE,"E1719"),sQuery(id+"F7.wireOp",EDGE,"E1720"),sQuery(id+"F7.wireOp",EDGE,"E1721"),sQuery(id+"F7.wireOp",EDGE,"E1722"),sQuery(id+"F7.wireOp",EDGE,"E1723"),sQuery(id+"F7.wireOp",EDGE,"E1724"),sQuery(id+"F7.wireOp",EDGE,"E1725"),sQuery(id+"F7.wireOp",EDGE,"E1726"),sQuery(id+"F7.wireOp",EDGE,"E1727"),sQuery(id+"F7.wireOp",EDGE,"E1728"),sQuery(id+"F7.wireOp",EDGE,"E1729"),sQuery(id+"F7.wireOp",EDGE,"E1730"),sQuery(id+"F7.wireOp",EDGE,"E1731"),sQuery(id+"F7.wireOp",EDGE,"E1732"),sQuery(id+"F7.wireOp",EDGE,"E1733"),sQuery(id+"F7.wireOp",EDGE,"E1734"),sQuery(id+"F7.wireOp",EDGE,"E1735"),sQuery(id+"F7.wireOp",EDGE,"E1736"),sQuery(id+"F7.wireOp",EDGE,"E1737"),sQuery(id+"F7.wireOp",EDGE,"E1738"),sQuery(id+"F7.wireOp",EDGE,"E1739"),sQuery(id+"F7.wireOp",EDGE,"E1740"),sQuery(id+"F7.wireOp",EDGE,"E1741"),sQuery(id+"F7.wireOp",EDGE,"E1742"),sQuery(id+"F7.wireOp",EDGE,"E1743"),sQuery(id+"F7.wireOp",EDGE,"E1744"),sQuery(id+"F7.wireOp",EDGE,"E1745"),sQuery(id+"F7.wireOp",EDGE,"E1746"),sQuery(id+"F7.wireOp",EDGE,"E1747"),sQuery(id+"F7.wireOp",EDGE,"E1748"),sQuery(id+"F7.wireOp",EDGE,"E1749"),sQuery(id+"F7.wireOp",EDGE,"E1750"),sQuery(id+"F7.wireOp",EDGE,"E1751"),sQuery(id+"F7.wireOp",EDGE,"E1752"),sQuery(id+"F7.wireOp",EDGE,"E1753"),sQuery(id+"F7.wireOp",EDGE,"E1754"),sQuery(id+"F7.wireOp",EDGE,"E1755"),sQuery(id+"F7.wireOp",EDGE,"E1756"),sQuery(id+"F7.wireOp",EDGE,"E1757"),sQuery(id+"F7.wireOp",EDGE,"E1758"),sQuery(id+"F7.wireOp",EDGE,"E1759"),sQuery(id+"F7.wireOp",EDGE,"E1760"),sQuery(id+"F7.wireOp",EDGE,"E1761"),sQuery(id+"F7.wireOp",EDGE,"E1762"),sQuery(id+"F7.wireOp",EDGE,"E1763"),sQuery(id+"F7.wireOp",EDGE,"E1764"),sQuery(id+"F7.wireOp",EDGE,"E1765"),sQuery(id+"F7.wireOp",EDGE,"E1766"),sQuery(id+"F7.wireOp",EDGE,"E1767"),sQuery(id+"F7.wireOp",EDGE,"E1768"),sQuery(id+"F7.wireOp",EDGE,"E1769"),sQuery(id+"F7.wireOp",EDGE,"E1770"),sQuery(id+"F7.wireOp",EDGE,"E1771"),sQuery(id+"F7.wireOp",EDGE,"E1772"),sQuery(id+"F7.wireOp",EDGE,"E1773"),sQuery(id+"F7.wireOp",EDGE,"E1774"),sQuery(id+"F7.wireOp",EDGE,"E1775"),sQuery(id+"F7.wireOp",EDGE,"E1776"),sQuery(id+"F7.wireOp",EDGE,"E1777"),sQuery(id+"F7.wireOp",EDGE,"E1778"),sQuery(id+"F7.wireOp",EDGE,"E1779"),sQuery(id+"F7.wireOp",EDGE,"E1780"),sQuery(id+"F7.wireOp",EDGE,"E1781"),sQuery(id+"F7.wireOp",EDGE,"E1782"),sQuery(id+"F7.wireOp",EDGE,"E1783"),sQuery(id+"F7.wireOp",EDGE,"E1784"),sQuery(id+"F7.wireOp",EDGE,"E1785"),sQuery(id+"F7.wireOp",EDGE,"E1786"),sQuery(id+"F7.wireOp",EDGE,"E1787"),sQuery(id+"F7.wireOp",EDGE,"E1788"),sQuery(id+"F7.wireOp",EDGE,"E1789"),sQuery(id+"F7.wireOp",EDGE,"E1790"),sQuery(id+"F7.wireOp",EDGE,"E1791"),sQuery(id+"F7.wireOp",EDGE,"E1792"),sQuery(id+"F7.wireOp",EDGE,"E1793"),sQuery(id+"F7.wireOp",EDGE,"E1794"),sQuery(id+"F7.wireOp",EDGE,"E1795"),sQuery(id+"F7.wireOp",EDGE,"E1796"),sQuery(id+"F7.wireOp",EDGE,"E1797"),sQuery(id+"F7.wireOp",EDGE,"E1798"),sQuery(id+"F7.wireOp",EDGE,"E1799"),sQuery(id+"F7.wireOp",EDGE,"E1800"),sQuery(id+"F7.wireOp",EDGE,"E1801"),sQuery(id+"F7.wireOp",EDGE,"E1802"),sQuery(id+"F7.wireOp",EDGE,"E1803"),sQuery(id+"F7.wireOp",EDGE,"E1804"),sQuery(id+"F7.wireOp",EDGE,"E1805"),sQuery(id+"F7.wireOp",EDGE,"E1806"),sQuery(id+"F7.wireOp",EDGE,"E1807"),sQuery(id+"F7.wireOp",EDGE,"E1808"),sQuery(id+"F7.wireOp",EDGE,"E1809"),sQuery(id+"F7.wireOp",EDGE,"E1810"),sQuery(id+"F7.wireOp",EDGE,"E1811"),sQuery(id+"F7.wireOp",EDGE,"E1812"),sQuery(id+"F7.wireOp",EDGE,"E1813"),sQuery(id+"F7.wireOp",EDGE,"E1814"),sQuery(id+"F7.wireOp",EDGE,"E1815"),sQuery(id+"F7.wireOp",EDGE,"E1816"),sQuery(id+"F7.wireOp",EDGE,"E1817"),sQuery(id+"F7.wireOp",EDGE,"E1818"),sQuery(id+"F7.wireOp",EDGE,"E1819"),sQuery(id+"F7.wireOp",EDGE,"E1820"),sQuery(id+"F7.wireOp",EDGE,"E1821"),sQuery(id+"F7.wireOp",EDGE,"E1822"),sQuery(id+"F7.wireOp",EDGE,"E1823"),sQuery(id+"F7.wireOp",EDGE,"E1824"),sQuery(id+"F7.wireOp",EDGE,"E1825"),sQuery(id+"F7.wireOp",EDGE,"E1826"),sQuery(id+"F7.wireOp",EDGE,"E1827"),sQuery(id+"F7.wireOp",EDGE,"E1828"),sQuery(id+"F7.wireOp",EDGE,"E1829"),sQuery(id+"F7.wireOp",EDGE,"E1830"),sQuery(id+"F7.wireOp",EDGE,"E1831"),sQuery(id+"F7.wireOp",EDGE,"E1832"),sQuery(id+"F7.wireOp",EDGE,"E1833"),sQuery(id+"F7.wireOp",EDGE,"E1834"),sQuery(id+"F7.wireOp",EDGE,"E1835"),sQuery(id+"F7.wireOp",EDGE,"E1836"),sQuery(id+"F7.wireOp",EDGE,"E1837"),sQuery(id+"F7.wireOp",EDGE,"E1838"),sQuery(id+"F7.wireOp",EDGE,"E1839"),sQuery(id+"F7.wireOp",EDGE,"E1840"),sQuery(id+"F7.wireOp",EDGE,"E1841"),sQuery(id+"F7.wireOp",EDGE,"E1842"),sQuery(id+"F7.wireOp",EDGE,"E1843"),sQuery(id+"F7.wireOp",EDGE,"E1844"),sQuery(id+"F7.wireOp",EDGE,"E1845"),sQuery(id+"F7.wireOp",EDGE,"E1846"),sQuery(id+"F7.wireOp",EDGE,"E1847"),sQuery(id+"F7.wireOp",EDGE,"E1848"),sQuery(id+"F7.wireOp",EDGE,"E1849"),sQuery(id+"F7.wireOp",EDGE,"E1850"),sQuery(id+"F7.wireOp",EDGE,"E1851"),sQuery(id+"F7.wireOp",EDGE,"E1852"),sQuery(id+"F7.wireOp",EDGE,"E1853"),sQuery(id+"F7.wireOp",EDGE,"E1854"),sQuery(id+"F7.wireOp",EDGE,"E1855"),sQuery(id+"F7.wireOp",EDGE,"E1856"),sQuery(id+"F7.wireOp",EDGE,"E1857"),sQuery(id+"F7.wireOp",EDGE,"E1858"),sQuery(id+"F7.wireOp",EDGE,"E1859"),sQuery(id+"F7.wireOp",EDGE,"E1860"),sQuery(id+"F7.wireOp",EDGE,"E1861"),sQuery(id+"F7.wireOp",EDGE,"E1862"),sQuery(id+"F7.wireOp",EDGE,"E1863"),sQuery(id+"F7.wireOp",EDGE,"E1864"),sQuery(id+"F7.wireOp",EDGE,"E1865"),sQuery(id+"F7.wireOp",EDGE,"E1866"),sQuery(id+"F7.wireOp",EDGE,"E1867"),sQuery(id+"F7.wireOp",EDGE,"E1868"),sQuery(id+"F7.wireOp",EDGE,"E1869"),sQuery(id+"F7.wireOp",EDGE,"E1870"),sQuery(id+"F7.wireOp",EDGE,"E1871"),sQuery(id+"F7.wireOp",EDGE,"E1872"),sQuery(id+"F7.wireOp",EDGE,"E1873"),sQuery(id+"F7.wireOp",EDGE,"E1874"),sQuery(id+"F7.wireOp",EDGE,"E1875"),sQuery(id+"F7.wireOp",EDGE,"E1876"),sQuery(id+"F7.wireOp",EDGE,"E1877"),sQuery(id+"F7.wireOp",EDGE,"E1878"),sQuery(id+"F7.wireOp",EDGE,"E1879"),sQuery(id+"F7.wireOp",EDGE,"E1880"),sQuery(id+"F7.wireOp",EDGE,"E1881"),sQuery(id+"F7.wireOp",EDGE,"E1882"),sQuery(id+"F7.wireOp",EDGE,"E1883"),sQuery(id+"F7.wireOp",EDGE,"E1884"),sQuery(id+"F7.wireOp",EDGE,"E1885"),sQuery(id+"F7.wireOp",EDGE,"E1886"),sQuery(id+"F7.wireOp",EDGE,"E1887"),sQuery(id+"F7.wireOp",EDGE,"E1888"),sQuery(id+"F7.wireOp",EDGE,"E1889"),sQuery(id+"F7.wireOp",EDGE,"E1890"),sQuery(id+"F7.wireOp",EDGE,"E1891"),sQuery(id+"F7.wireOp",EDGE,"E1892"),sQuery(id+"F7.wireOp",EDGE,"E1893"),sQuery(id+"F7.wireOp",EDGE,"E1894"),sQuery(id+"F7.wireOp",EDGE,"E1895"),sQuery(id+"F7.wireOp",EDGE,"E1896"),sQuery(id+"F7.wireOp",EDGE,"E1897"),sQuery(id+"F7.wireOp",EDGE,"E1898"),sQuery(id+"F7.wireOp",EDGE,"E1899"),sQuery(id+"F7.wireOp",EDGE,"E1900"),sQuery(id+"F7.wireOp",EDGE,"E1901"),sQuery(id+"F7.wireOp",EDGE,"E1902"),sQuery(id+"F7.wireOp",EDGE,"E1903"),sQuery(id+"F7.wireOp",EDGE,"E1904"),sQuery(id+"F7.wireOp",EDGE,"E1905"),sQuery(id+"F7.wireOp",EDGE,"E1906"),sQuery(id+"F7.wireOp",EDGE,"E1907"),sQuery(id+"F7.wireOp",EDGE,"E1908"),sQuery(id+"F7.wireOp",EDGE,"E1909"),sQuery(id+"F7.wireOp",EDGE,"E1910"),sQuery(id+"F7.wireOp",EDGE,"E1911"),sQuery(id+"F7.wireOp",EDGE,"E1912"),sQuery(id+"F7.wireOp",EDGE,"E1913"),sQuery(id+"F7.wireOp",EDGE,"E1914"),sQuery(id+"F7.wireOp",EDGE,"E1915"),sQuery(id+"F7.wireOp",EDGE,"E1916"),sQuery(id+"F7.wireOp",EDGE,"E1917"),sQuery(id+"F7.wireOp",EDGE,"E1918"),sQuery(id+"F7.wireOp",EDGE,"E1919"),sQuery(id+"F7.wireOp",EDGE,"E1920"),sQuery(id+"F7.wireOp",EDGE,"E1921"),sQuery(id+"F7.wireOp",EDGE,"E1922"),sQuery(id+"F7.wireOp",EDGE,"E1923"),sQuery(id+"F7.wireOp",EDGE,"E1924"),sQuery(id+"F7.wireOp",EDGE,"E1925"),sQuery(id+"F7.wireOp",EDGE,"E1926"),sQuery(id+"F7.wireOp",EDGE,"E1927"),sQuery(id+"F7.wireOp",EDGE,"E1928"),sQuery(id+"F7.wireOp",EDGE,"E1929"),sQuery(id+"F7.wireOp",EDGE,"E1930"),sQuery(id+"F7.wireOp",EDGE,"E1931"),sQuery(id+"F7.wireOp",EDGE,"E1932"),sQuery(id+"F7.wireOp",EDGE,"E1933"),sQuery(id+"F7.wireOp",EDGE,"E1934"),sQuery(id+"F7.wireOp",EDGE,"E1935"),sQuery(id+"F7.wireOp",EDGE,"E1936"),sQuery(id+"F7.wireOp",EDGE,"E1937"),sQuery(id+"F7.wireOp",EDGE,"E1938"),sQuery(id+"F7.wireOp",EDGE,"E1939"),sQuery(id+"F7.wireOp",EDGE,"E1940"),sQuery(id+"F7.wireOp",EDGE,"E1941"),sQuery(id+"F7.wireOp",EDGE,"E1942"),sQuery(id+"F7.wireOp",EDGE,"E1943"),sQuery(id+"F7.wireOp",EDGE,"E1944"),sQuery(id+"F7.wireOp",EDGE,"E1945"),sQuery(id+"F7.wireOp",EDGE,"E1946"),sQuery(id+"F7.wireOp",EDGE,"E1947"),sQuery(id+"F7.wireOp",EDGE,"E1948"),sQuery(id+"F7.wireOp",EDGE,"E1949"),sQuery(id+"F7.wireOp",EDGE,"E1950"),sQuery(id+"F7.wireOp",EDGE,"E1951"),sQuery(id+"F7.wireOp",EDGE,"E1952"),sQuery(id+"F7.wireOp",EDGE,"E1953"),sQuery(id+"F7.wireOp",EDGE,"E1954"),sQuery(id+"F7.wireOp",EDGE,"E1955"),sQuery(id+"F7.wireOp",EDGE,"E1956"),sQuery(id+"F7.wireOp",EDGE,"E1957"),sQuery(id+"F7.wireOp",EDGE,"E1958"),sQuery(id+"F7.wireOp",EDGE,"E1959"),sQuery(id+"F7.wireOp",EDGE,"E1960"),sQuery(id+"F7.wireOp",EDGE,"E1961"),sQuery(id+"F7.wireOp",EDGE,"E1962"),sQuery(id+"F7.wireOp",EDGE,"E1963"),sQuery(id+"F7.wireOp",EDGE,"E1964"),sQuery(id+"F7.wireOp",EDGE,"E1965"),sQuery(id+"F7.wireOp",EDGE,"E1966"),sQuery(id+"F7.wireOp",EDGE,"E1967"),sQuery(id+"F7.wireOp",EDGE,"E1968"),sQuery(id+"F7.wireOp",EDGE,"E1969"),sQuery(id+"F7.wireOp",EDGE,"E1970"),sQuery(id+"F7.wireOp",EDGE,"E1971"),sQuery(id+"F7.wireOp",EDGE,"E1972"),sQuery(id+"F7.wireOp",EDGE,"E1973"),sQuery(id+"F7.wireOp",EDGE,"E1974"),sQuery(id+"F7.wireOp",EDGE,"E1975"),sQuery(id+"F7.wireOp",EDGE,"E1976"),sQuery(id+"F7.wireOp",EDGE,"E1977"),sQuery(id+"F7.wireOp",EDGE,"E1978"),sQuery(id+"F7.wireOp",EDGE,"E1979"),sQuery(id+"F7.wireOp",EDGE,"E1980"),sQuery(id+"F7.wireOp",EDGE,"E1981"),sQuery(id+"F7.wireOp",EDGE,"E1982"),sQuery(id+"F7.wireOp",EDGE,"E1983"),sQuery(id+"F7.wireOp",EDGE,"E1984"),sQuery(id+"F7.wireOp",EDGE,"E1985"),sQuery(id+"F7.wireOp",EDGE,"E1986"),sQuery(id+"F7.wireOp",EDGE,"E1987"),sQuery(id+"F7.wireOp",EDGE,"E1988"),sQuery(id+"F7.wireOp",EDGE,"E1989"),sQuery(id+"F7.wireOp",EDGE,"E1990"),sQuery(id+"F7.wireOp",EDGE,"E1991"),sQuery(id+"F7.wireOp",EDGE,"E1992"),sQuery(id+"F7.wireOp",EDGE,"E1993"),sQuery(id+"F7.wireOp",EDGE,"E1994"),sQuery(id+"F7.wireOp",EDGE,"E1995"),sQuery(id+"F7.wireOp",EDGE,"E1996"),sQuery(id+"F7.wireOp",EDGE,"E1997"),sQuery(id+"F7.wireOp",EDGE,"E1998"),sQuery(id+"F7.wireOp",EDGE,"E1999"),sQuery(id+"F7.wireOp",EDGE,"E2000"),sQuery(id+"F7.wireOp",EDGE,"E2001"),sQuery(id+"F7.wireOp",EDGE,"E2002"),sQuery(id+"F7.wireOp",EDGE,"E2003"),sQuery(id+"F7.wireOp",EDGE,"E2004"),sQuery(id+"F7.wireOp",EDGE,"E2005"),sQuery(id+"F7.wireOp",EDGE,"E2006"),sQuery(id+"F7.wireOp",EDGE,"E2007"),sQuery(id+"F7.wireOp",EDGE,"E2008"),sQuery(id+"F7.wireOp",EDGE,"E2009"),sQuery(id+"F7.wireOp",EDGE,"E2010"),sQuery(id+"F7.wireOp",EDGE,"E2011"),sQuery(id+"F7.wireOp",EDGE,"E2012"),sQuery(id+"F7.wireOp",EDGE,"E2013"),sQuery(id+"F7.wireOp",EDGE,"E2014"),sQuery(id+"F7.wireOp",EDGE,"E2015"),sQuery(id+"F7.wireOp",EDGE,"E2016"),sQuery(id+"F7.wireOp",EDGE,"E2017"),sQuery(id+"F7.wireOp",EDGE,"E2018"),sQuery(id+"F7.wireOp",EDGE,"E2019"),sQuery(id+"F7.wireOp",EDGE,"E2020"),sQuery(id+"F7.wireOp",EDGE,"E2021"),sQuery(id+"F7.wireOp",EDGE,"E2022"),sQuery(id+"F7.wireOp",EDGE,"E2023"),sQuery(id+"F7.wireOp",EDGE,"E2024"),sQuery(id+"F7.wireOp",EDGE,"E2025"),sQuery(id+"F7.wireOp",EDGE,"E2026"),sQuery(id+"F7.wireOp",EDGE,"E2027"),sQuery(id+"F7.wireOp",EDGE,"E2028"),sQuery(id+"F7.wireOp",EDGE,"E2029"),sQuery(id+"F7.wireOp",EDGE,"E2030"),sQuery(id+"F7.wireOp",EDGE,"E2031"),sQuery(id+"F7.wireOp",EDGE,"E2032"),sQuery(id+"F7.wireOp",EDGE,"E2033"),sQuery(id+"F7.wireOp",EDGE,"E2034"),sQuery(id+"F7.wireOp",EDGE,"E2035"),sQuery(id+"F7.wireOp",EDGE,"E2036"),sQuery(id+"F7.wireOp",EDGE,"E2037"),sQuery(id+"F7.wireOp",EDGE,"E2038"),sQuery(id+"F7.wireOp",EDGE,"E2039"),sQuery(id+"F7.wireOp",EDGE,"E2040"),sQuery(id+"F7.wireOp",EDGE,"E2041"),sQuery(id+"F7.wireOp",EDGE,"E2042"),sQuery(id+"F7.wireOp",EDGE,"E2043"),sQuery(id+"F7.wireOp",EDGE,"E2044"),sQuery(id+"F7.wireOp",EDGE,"E2045"),sQuery(id+"F7.wireOp",EDGE,"E2046"),sQuery(id+"F7.wireOp",EDGE,"E2047"),sQuery(id+"F7.wireOp",EDGE,"E2048"),sQuery(id+"F7.wireOp",EDGE,"E2049"),sQuery(id+"F7.wireOp",EDGE,"E2050"),sQuery(id+"F7.wireOp",EDGE,"E2051"),sQuery(id+"F7.wireOp",EDGE,"E2052"),sQuery(id+"F7.wireOp",EDGE,"E2053"),sQuery(id+"F7.wireOp",EDGE,"E2054"),sQuery(id+"F7.wireOp",EDGE,"E2055"),sQuery(id+"F7.wireOp",EDGE,"E2056"),sQuery(id+"F7.wireOp",EDGE,"E2057"),sQuery(id+"F7.wireOp",EDGE,"E2058"),sQuery(id+"F7.wireOp",EDGE,"E2059"),sQuery(id+"F7.wireOp",EDGE,"E2060"),sQuery(id+"F7.wireOp",EDGE,"E2061"),sQuery(id+"F7.wireOp",EDGE,"E2062"),sQuery(id+"F7.wireOp",EDGE,"E2063"),sQuery(id+"F7.wireOp",EDGE,"E2064"),sQuery(id+"F7.wireOp",EDGE,"E2065"),sQuery(id+"F7.wireOp",EDGE,"E2066"),sQuery(id+"F7.wireOp",EDGE,"E2067"),sQuery(id+"F7.wireOp",EDGE,"E2068"),sQuery(id+"F7.wireOp",EDGE,"E2069"),sQuery(id+"F7.wireOp",EDGE,"E2070"),sQuery(id+"F7.wireOp",EDGE,"E2071"),sQuery(id+"F7.wireOp",EDGE,"E2072"),sQuery(id+"F7.wireOp",EDGE,"E2073"),sQuery(id+"F7.wireOp",EDGE,"E2074"),sQuery(id+"F7.wireOp",EDGE,"E2075"),sQuery(id+"F7.wireOp",EDGE,"E2076"),sQuery(id+"F7.wireOp",EDGE,"E2077"),sQuery(id+"F7.wireOp",EDGE,"E2078"),sQuery(id+"F7.wireOp",EDGE,"E2079"),sQuery(id+"F7.wireOp",EDGE,"E2080"),sQuery(id+"F7.wireOp",EDGE,"E2081"),sQuery(id+"F7.wireOp",EDGE,"E2082"),sQuery(id+"F7.wireOp",EDGE,"E2083"),sQuery(id+"F7.wireOp",EDGE,"E2084"),sQuery(id+"F7.wireOp",EDGE,"E2085"),sQuery(id+"F7.wireOp",EDGE,"E2086"),sQuery(id+"F7.wireOp",EDGE,"E2087"),sQuery(id+"F7.wireOp",EDGE,"E2088"),sQuery(id+"F7.wireOp",EDGE,"E2089"),sQuery(id+"F7.wireOp",EDGE,"E2090"),sQuery(id+"F7.wireOp",EDGE,"E2091"),sQuery(id+"F7.wireOp",EDGE,"E2092"),sQuery(id+"F7.wireOp",EDGE,"E2093"),sQuery(id+"F7.wireOp",EDGE,"E2094"),sQuery(id+"F7.wireOp",EDGE,"E2095"),sQuery(id+"F7.wireOp",EDGE,"E2096"),sQuery(id+"F7.wireOp",EDGE,"E2097"),sQuery(id+"F7.wireOp",EDGE,"E2098"),sQuery(id+"F7.wireOp",EDGE,"E2099"),sQuery(id+"F7.wireOp",EDGE,"E2100"),sQuery(id+"F7.wireOp",EDGE,"E2101"),sQuery(id+"F7.wireOp",EDGE,"E2102"),sQuery(id+"F7.wireOp",EDGE,"E2103"),sQuery(id+"F7.wireOp",EDGE,"E2104"),sQuery(id+"F7.wireOp",EDGE,"E2105"),sQuery(id+"F7.wireOp",EDGE,"E2106"),sQuery(id+"F7.wireOp",EDGE,"E2107"),sQuery(id+"F7.wireOp",EDGE,"E2108"),sQuery(id+"F7.wireOp",EDGE,"E2109"),sQuery(id+"F7.wireOp",EDGE,"E2110"),sQuery(id+"F7.wireOp",EDGE,"E2111"),sQuery(id+"F7.wireOp",EDGE,"E2112"),sQuery(id+"F7.wireOp",EDGE,"E2113"),sQuery(id+"F7.wireOp",EDGE,"E2114"),sQuery(id+"F7.wireOp",EDGE,"E2115"),sQuery(id+"F7.wireOp",EDGE,"E2116"),sQuery(id+"F7.wireOp",EDGE,"E2117"),sQuery(id+"F7.wireOp",EDGE,"E2118"),sQuery(id+"F7.wireOp",EDGE,"E2119"),sQuery(id+"F7.wireOp",EDGE,"E2120"),sQuery(id+"F7.wireOp",EDGE,"E2121"),sQuery(id+"F7.wireOp",EDGE,"E2122"),sQuery(id+"F7.wireOp",EDGE,"E2123"),sQuery(id+"F7.wireOp",EDGE,"E2124"),sQuery(id+"F7.wireOp",EDGE,"E2125"),sQuery(id+"F7.wireOp",EDGE,"E2126"),sQuery(id+"F7.wireOp",EDGE,"E2127"),sQuery(id+"F7.wireOp",EDGE,"E2128"),sQuery(id+"F7.wireOp",EDGE,"E2129"),sQuery(id+"F7.wireOp",EDGE,"E2130"),sQuery(id+"F7.wireOp",EDGE,"E2131"),sQuery(id+"F7.wireOp",EDGE,"E2132"),sQuery(id+"F7.wireOp",EDGE,"E2133"),sQuery(id+"F7.wireOp",EDGE,"E2134"),sQuery(id+"F7.wireOp",EDGE,"E2135"),sQuery(id+"F7.wireOp",EDGE,"E2136"),sQuery(id+"F7.wireOp",EDGE,"E2137"),sQuery(id+"F7.wireOp",EDGE,"E2138"),sQuery(id+"F7.wireOp",EDGE,"E2139"),sQuery(id+"F7.wireOp",EDGE,"E2140"),sQuery(id+"F7.wireOp",EDGE,"E2141"),sQuery(id+"F7.wireOp",EDGE,"E2142"),sQuery(id+"F7.wireOp",EDGE,"E2143"),sQuery(id+"F7.wireOp",EDGE,"E2144"),sQuery(id+"F7.wireOp",EDGE,"E2145"),sQuery(id+"F7.wireOp",EDGE,"E2146"),sQuery(id+"F7.wireOp",EDGE,"E2147"),sQuery(id+"F7.wireOp",EDGE,"E2148"),sQuery(id+"F7.wireOp",EDGE,"E2149"),sQuery(id+"F7.wireOp",EDGE,"E2150"),sQuery(id+"F7.wireOp",EDGE,"E2151"),sQuery(id+"F7.wireOp",EDGE,"E2152"),sQuery(id+"F7.wireOp",EDGE,"E2153"),sQuery(id+"F7.wireOp",EDGE,"E2154"),sQuery(id+"F7.wireOp",EDGE,"E2155"),sQuery(id+"F7.wireOp",EDGE,"E2156"),sQuery(id+"F7.wireOp",EDGE,"E2157"),sQuery(id+"F7.wireOp",EDGE,"E2158"),sQuery(id+"F7.wireOp",EDGE,"E2159"),sQuery(id+"F7.wireOp",EDGE,"E2160"),sQuery(id+"F7.wireOp",EDGE,"E2161"),sQuery(id+"F7.wireOp",EDGE,"E2162"),sQuery(id+"F7.wireOp",EDGE,"E2163"),sQuery(id+"F7.wireOp",EDGE,"E2164"),sQuery(id+"F7.wireOp",EDGE,"E2165"),sQuery(id+"F7.wireOp",EDGE,"E2166"),sQuery(id+"F7.wireOp",EDGE,"E2167"),sQuery(id+"F7.wireOp",EDGE,"E2168"),sQuery(id+"F7.wireOp",EDGE,"E2169"),sQuery(id+"F7.wireOp",EDGE,"E2170"),sQuery(id+"F7.wireOp",EDGE,"E2171"),sQuery(id+"F7.wireOp",EDGE,"E2172"),sQuery(id+"F7.wireOp",EDGE,"E2173"),sQuery(id+"F7.wireOp",EDGE,"E2174"),sQuery(id+"F7.wireOp",EDGE,"E2175"),sQuery(id+"F7.wireOp",EDGE,"E2176"),sQuery(id+"F7.wireOp",EDGE,"E2177"),sQuery(id+"F7.wireOp",EDGE,"E2178"),sQuery(id+"F7.wireOp",EDGE,"E2179"),sQuery(id+"F7.wireOp",EDGE,"E2180"),sQuery(id+"F7.wireOp",EDGE,"E2181"),sQuery(id+"F7.wireOp",EDGE,"E2182"),sQuery(id+"F7.wireOp",EDGE,"E2183"),sQuery(id+"F7.wireOp",EDGE,"E2184"),sQuery(id+"F7.wireOp",EDGE,"E2185"),sQuery(id+"F7.wireOp",EDGE,"E2186"),sQuery(id+"F7.wireOp",EDGE,"E2187"),sQuery(id+"F7.wireOp",EDGE,"E2188"),sQuery(id+"F7.wireOp",EDGE,"E2189"),sQuery(id+"F7.wireOp",EDGE,"E2190"),sQuery(id+"F7.wireOp",EDGE,"E2191"),sQuery(id+"F7.wireOp",EDGE,"E2192"),sQuery(id+"F7.wireOp",EDGE,"E2193"),sQuery(id+"F7.wireOp",EDGE,"E2194"),sQuery(id+"F7.wireOp",EDGE,"E2195"),sQuery(id+"F7.wireOp",EDGE,"E2196"),sQuery(id+"F7.wireOp",EDGE,"E2197"),sQuery(id+"F7.wireOp",EDGE,"E2198"),sQuery(id+"F7.wireOp",EDGE,"E2199"),sQuery(id+"F7.wireOp",EDGE,"E2200"),sQuery(id+"F7.wireOp",EDGE,"E2201"),sQuery(id+"F7.wireOp",EDGE,"E2202"),sQuery(id+"F7.wireOp",EDGE,"E2203"),sQuery(id+"F7.wireOp",EDGE,"E2204"),sQuery(id+"F7.wireOp",EDGE,"E2205"),sQuery(id+"F7.wireOp",EDGE,"E2206"),sQuery(id+"F7.wireOp",EDGE,"E2207"),sQuery(id+"F7.wireOp",EDGE,"E2208"),sQuery(id+"F7.wireOp",EDGE,"E2209"),sQuery(id+"F7.wireOp",EDGE,"E2210"),sQuery(id+"F7.wireOp",EDGE,"E2211"),sQuery(id+"F7.wireOp",EDGE,"E2212"),sQuery(id+"F7.wireOp",EDGE,"E2213"),sQuery(id+"F7.wireOp",EDGE,"E2214"),sQuery(id+"F7.wireOp",EDGE,"E2215"),sQuery(id+"F7.wireOp",EDGE,"E2216"),sQuery(id+"F7.wireOp",EDGE,"E2217"),sQuery(id+"F7.wireOp",EDGE,"E2218"),sQuery(id+"F7.wireOp",EDGE,"E2219"),sQuery(id+"F7.wireOp",EDGE,"E2220"),sQuery(id+"F7.wireOp",EDGE,"E2221"),sQuery(id+"F7.wireOp",EDGE,"E2222"),sQuery(id+"F7.wireOp",EDGE,"E2223"),sQuery(id+"F7.wireOp",EDGE,"E2224"),sQuery(id+"F7.wireOp",EDGE,"E2225"),sQuery(id+"F7.wireOp",EDGE,"E2226"),sQuery(id+"F7.wireOp",EDGE,"E2227"),sQuery(id+"F7.wireOp",EDGE,"E2228"),sQuery(id+"F7.wireOp",EDGE,"E2229"),sQuery(id+"F7.wireOp",EDGE,"E2230"),sQuery(id+"F7.wireOp",EDGE,"E2231"),sQuery(id+"F7.wireOp",EDGE,"E2232"),sQuery(id+"F7.wireOp",EDGE,"E2233"),sQuery(id+"F7.wireOp",EDGE,"E2234"),sQuery(id+"F7.wireOp",EDGE,"E2235"),sQuery(id+"F7.wireOp",EDGE,"E2236"),sQuery(id+"F7.wireOp",EDGE,"E2237"),sQuery(id+"F7.wireOp",EDGE,"E2238"),sQuery(id+"F7.wireOp",EDGE,"E2239"),sQuery(id+"F7.wireOp",EDGE,"E2240"),sQuery(id+"F7.wireOp",EDGE,"E2241"),sQuery(id+"F7.wireOp",EDGE,"E2242"),sQuery(id+"F7.wireOp",EDGE,"E2243"),sQuery(id+"F7.wireOp",EDGE,"E2244"),sQuery(id+"F7.wireOp",EDGE,"E2245"),sQuery(id+"F7.wireOp",EDGE,"E2246"),sQuery(id+"F7.wireOp",EDGE,"E2247"),sQuery(id+"F7.wireOp",EDGE,"E2248"),sQuery(id+"F7.wireOp",EDGE,"E2249"),sQuery(id+"F7.wireOp",EDGE,"E2250"),sQuery(id+"F7.wireOp",EDGE,"E2251"),sQuery(id+"F7.wireOp",EDGE,"E2252"),sQuery(id+"F7.wireOp",EDGE,"E2253"),sQuery(id+"F7.wireOp",EDGE,"E2254"),sQuery(id+"F7.wireOp",EDGE,"E2255"),sQuery(id+"F7.wireOp",EDGE,"E2256"),sQuery(id+"F7.wireOp",EDGE,"E2257"),sQuery(id+"F7.wireOp",EDGE,"E2258"),sQuery(id+"F7.wireOp",EDGE,"E2259"),sQuery(id+"F7.wireOp",EDGE,"E2260"),sQuery(id+"F7.wireOp",EDGE,"E2261"),sQuery(id+"F7.wireOp",EDGE,"E2262"),sQuery(id+"F7.wireOp",EDGE,"E2263"),sQuery(id+"F7.wireOp",EDGE,"E2264"),sQuery(id+"F7.wireOp",EDGE,"E2265"),sQuery(id+"F7.wireOp",EDGE,"E2266"),sQuery(id+"F7.wireOp",EDGE,"E2267"),sQuery(id+"F7.wireOp",EDGE,"E2268"),sQuery(id+"F7.wireOp",EDGE,"E2269"),sQuery(id+"F7.wireOp",EDGE,"E2270"),sQuery(id+"F7.wireOp",EDGE,"E2271"),sQuery(id+"F7.wireOp",EDGE,"E2272"),sQuery(id+"F7.wireOp",EDGE,"E2273"),sQuery(id+"F7.wireOp",EDGE,"E2274"),sQuery(id+"F7.wireOp",EDGE,"E2275"),sQuery(id+"F7.wireOp",EDGE,"E2276"),sQuery(id+"F7.wireOp",EDGE,"E2277"),sQuery(id+"F7.wireOp",EDGE,"E2278"),sQuery(id+"F7.wireOp",EDGE,"E2279"),sQuery(id+"F7.wireOp",EDGE,"E2280"),sQuery(id+"F7.wireOp",EDGE,"E2281"),sQuery(id+"F7.wireOp",EDGE,"E2282"),sQuery(id+"F7.wireOp",EDGE,"E2283"),sQuery(id+"F7.wireOp",EDGE,"E2284"),sQuery(id+"F7.wireOp",EDGE,"E2285"),sQuery(id+"F7.wireOp",EDGE,"E2286"),sQuery(id+"F7.wireOp",EDGE,"E2287"),sQuery(id+"F7.wireOp",EDGE,"E2288"),sQuery(id+"F7.wireOp",EDGE,"E2289"),sQuery(id+"F7.wireOp",EDGE,"E2290"),sQuery(id+"F7.wireOp",EDGE,"E2291"),sQuery(id+"F7.wireOp",EDGE,"E2292"),sQuery(id+"F7.wireOp",EDGE,"E2293"),sQuery(id+"F7.wireOp",EDGE,"E2294"),sQuery(id+"F7.wireOp",EDGE,"E2295"),sQuery(id+"F7.wireOp",EDGE,"E2296"),sQuery(id+"F7.wireOp",EDGE,"E2297"),sQuery(id+"F7.wireOp",EDGE,"E2298"),sQuery(id+"F7.wireOp",EDGE,"E2299"),sQuery(id+"F7.wireOp",EDGE,"E2300"),sQuery(id+"F7.wireOp",EDGE,"E2301"),sQuery(id+"F7.wireOp",EDGE,"E2302"),sQuery(id+"F7.wireOp",EDGE,"E2303"),sQuery(id+"F7.wireOp",EDGE,"E2304"),sQuery(id+"F7.wireOp",EDGE,"E2305"),sQuery(id+"F7.wireOp",EDGE,"E2306"),sQuery(id+"F7.wireOp",EDGE,"E2307"),sQuery(id+"F7.wireOp",EDGE,"E2308"),sQuery(id+"F7.wireOp",EDGE,"E2309"),sQuery(id+"F7.wireOp",EDGE,"E2310"),sQuery(id+"F7.wireOp",EDGE,"E2311"),sQuery(id+"F7.wireOp",EDGE,"E2312"),sQuery(id+"F7.wireOp",EDGE,"E2313"),sQuery(id+"F7.wireOp",EDGE,"E2314"),sQuery(id+"F7.wireOp",EDGE,"E2315"),sQuery(id+"F7.wireOp",EDGE,"E2316"),sQuery(id+"F7.wireOp",EDGE,"E2317"),sQuery(id+"F7.wireOp",EDGE,"E2318"),sQuery(id+"F7.wireOp",EDGE,"E2319"),sQuery(id+"F7.wireOp",EDGE,"E2320"),sQuery(id+"F7.wireOp",EDGE,"E2321"),sQuery(id+"F7.wireOp",EDGE,"E2322"),sQuery(id+"F7.wireOp",EDGE,"E2323"),sQuery(id+"F7.wireOp",EDGE,"E2324"),sQuery(id+"F7.wireOp",EDGE,"E2325"),sQuery(id+"F7.wireOp",EDGE,"E2326"),sQuery(id+"F7.wireOp",EDGE,"E2327"),sQuery(id+"F7.wireOp",EDGE,"E2328"),sQuery(id+"F7.wireOp",EDGE,"E2329"),sQuery(id+"F7.wireOp",EDGE,"E2330"),sQuery(id+"F7.wireOp",EDGE,"E2331"),sQuery(id+"F7.wireOp",EDGE,"E2332"),sQuery(id+"F7.wireOp",EDGE,"E2333"),sQuery(id+"F7.wireOp",EDGE,"E2334"),sQuery(id+"F7.wireOp",EDGE,"E2335"),sQuery(id+"F7.wireOp",EDGE,"E2336"),sQuery(id+"F7.wireOp",EDGE,"E2337"),sQuery(id+"F7.wireOp",EDGE,"E2338"),sQuery(id+"F7.wireOp",EDGE,"E2339"),sQuery(id+"F7.wireOp",EDGE,"E2340"),sQuery(id+"F7.wireOp",EDGE,"E2341"),sQuery(id+"F7.wireOp",EDGE,"E2342"),sQuery(id+"F7.wireOp",EDGE,"E2343"),sQuery(id+"F7.wireOp",EDGE,"E2344"),sQuery(id+"F7.wireOp",EDGE,"E2345"),sQuery(id+"F7.wireOp",EDGE,"E2346"),sQuery(id+"F7.wireOp",EDGE,"E2347"),sQuery(id+"F7.wireOp",EDGE,"E2348"),sQuery(id+"F7.wireOp",EDGE,"E2349"),sQuery(id+"F7.wireOp",EDGE,"E2350"),sQuery(id+"F7.wireOp",EDGE,"E2351"),sQuery(id+"F7.wireOp",EDGE,"E2352"),sQuery(id+"F7.wireOp",EDGE,"E2353"),sQuery(id+"F7.wireOp",EDGE,"E2354"),sQuery(id+"F7.wireOp",EDGE,"E2355"),sQuery(id+"F7.wireOp",EDGE,"E2356"),sQuery(id+"F7.wireOp",EDGE,"E2357"),sQuery(id+"F7.wireOp",EDGE,"E2358"),sQuery(id+"F7.wireOp",EDGE,"E2359"),sQuery(id+"F7.wireOp",EDGE,"E2360"),sQuery(id+"F7.wireOp",EDGE,"E2361"),sQuery(id+"F7.wireOp",EDGE,"E2362"),sQuery(id+"F7.wireOp",EDGE,"E2363"),sQuery(id+"F7.wireOp",EDGE,"E2364"),sQuery(id+"F7.wireOp",EDGE,"E2365"),sQuery(id+"F7.wireOp",EDGE,"E2366"),sQuery(id+"F7.wireOp",EDGE,"E2367"),sQuery(id+"F7.wireOp",EDGE,"E2368"),sQuery(id+"F7.wireOp",EDGE,"E2369"),sQuery(id+"F7.wireOp",EDGE,"E2370"),sQuery(id+"F7.wireOp",EDGE,"E2371"),sQuery(id+"F7.wireOp",EDGE,"E2372"),sQuery(id+"F7.wireOp",EDGE,"E2373"),sQuery(id+"F7.wireOp",EDGE,"E2374"),sQuery(id+"F7.wireOp",EDGE,"E2375"),sQuery(id+"F7.wireOp",EDGE,"E2376"),sQuery(id+"F7.wireOp",EDGE,"E2377"),sQuery(id+"F7.wireOp",EDGE,"E2378"),sQuery(id+"F7.wireOp",EDGE,"E2379"),sQuery(id+"F7.wireOp",EDGE,"E2380"),sQuery(id+"F7.wireOp",EDGE,"E2381"),sQuery(id+"F7.wireOp",EDGE,"E2382"),sQuery(id+"F7.wireOp",EDGE,"E2383"),sQuery(id+"F7.wireOp",EDGE,"E2384"),sQuery(id+"F7.wireOp",EDGE,"E2385"),sQuery(id+"F7.wireOp",EDGE,"E2386"),sQuery(id+"F7.wireOp",EDGE,"E2387"),sQuery(id+"F7.wireOp",EDGE,"E2388"),sQuery(id+"F7.wireOp",EDGE,"E2389"),sQuery(id+"F7.wireOp",EDGE,"E2390"),sQuery(id+"F7.wireOp",EDGE,"E2391"),sQuery(id+"F7.wireOp",EDGE,"E2392"),sQuery(id+"F7.wireOp",EDGE,"E2393"),sQuery(id+"F7.wireOp",EDGE,"E2394"),sQuery(id+"F7.wireOp",EDGE,"E2395"),sQuery(id+"F7.wireOp",EDGE,"E2396"),sQuery(id+"F7.wireOp",EDGE,"E2397"),sQuery(id+"F7.wireOp",EDGE,"E2398"),sQuery(id+"F7.wireOp",EDGE,"E2399"),sQuery(id+"F7.wireOp",EDGE,"E2400"),sQuery(id+"F7.wireOp",EDGE,"E2401"),sQuery(id+"F7.wireOp",EDGE,"E2402"),sQuery(id+"F7.wireOp",EDGE,"E2403"),sQuery(id+"F7.wireOp",EDGE,"E2404"),sQuery(id+"F7.wireOp",EDGE,"E2405"),sQuery(id+"F7.wireOp",EDGE,"E2406"),sQuery(id+"F7.wireOp",EDGE,"E2407"),sQuery(id+"F7.wireOp",EDGE,"E2408"),sQuery(id+"F7.wireOp",EDGE,"E2409"),sQuery(id+"F7.wireOp",EDGE,"E2410"),sQuery(id+"F7.wireOp",EDGE,"E2411"),sQuery(id+"F7.wireOp",EDGE,"E2412"),sQuery(id+"F7.wireOp",EDGE,"E2413"),sQuery(id+"F7.wireOp",EDGE,"E2414"),sQuery(id+"F7.wireOp",EDGE,"E2415"),sQuery(id+"F7.wireOp",EDGE,"E2416"),sQuery(id+"F7.wireOp",EDGE,"E2417"),sQuery(id+"F7.wireOp",EDGE,"E2418"),sQuery(id+"F7.wireOp",EDGE,"E2419"),sQuery(id+"F7.wireOp",EDGE,"E2420"),sQuery(id+"F7.wireOp",EDGE,"E2421"),sQuery(id+"F7.wireOp",EDGE,"E2422"),sQuery(id+"F7.wireOp",EDGE,"E2423"),sQuery(id+"F7.wireOp",EDGE,"E2424"),sQuery(id+"F7.wireOp",EDGE,"E2425"),sQuery(id+"F7.wireOp",EDGE,"E2426"),sQuery(id+"F7.wireOp",EDGE,"E2427"),sQuery(id+"F7.wireOp",EDGE,"E2428"),sQuery(id+"F7.wireOp",EDGE,"E2429"),sQuery(id+"F7.wireOp",EDGE,"E2430"),sQuery(id+"F7.wireOp",EDGE,"E2431"),sQuery(id+"F7.wireOp",EDGE,"E2432"),sQuery(id+"F7.wireOp",EDGE,"E2433"),sQuery(id+"F7.wireOp",EDGE,"E2434"),sQuery(id+"F7.wireOp",EDGE,"E2435")])],"isStart":false});
            var sketch = newSketch(context, id + "F9", { "sketchPlane" : qUnion([Q0])});
            skLineSegment(sketch, "E2436", {"start": v(161.16, 53.62) * mm, "end": v(161.32, 53.62) * mm});
            skLineSegment(sketch, "E2437", {"start": v(161.32, 53.62) * mm, "end": v(161.48, 53.6) * mm});
            skLineSegment(sketch, "E2438", {"start": v(161.48, 53.6) * mm, "end": v(161.63, 53.57) * mm});
            skLineSegment(sketch, "E2439", {"start": v(161.63, 53.57) * mm, "end": v(161.78, 53.53) * mm});
            skLineSegment(sketch, "E2440", {"start": v(161.78, 53.53) * mm, "end": v(161.93, 53.47) * mm});
            skLineSegment(sketch, "E2441", {"start": v(161.93, 53.47) * mm, "end": v(162.07, 53.4) * mm});
            skLineSegment(sketch, "E2442", {"start": v(162.07, 53.4) * mm, "end": v(162.2, 53.33) * mm});
            skLineSegment(sketch, "E2443", {"start": v(162.2, 53.33) * mm, "end": v(162.34, 53.24) * mm});
            skLineSegment(sketch, "E2444", {"start": v(162.34, 53.24) * mm, "end": v(162.46, 53.15) * mm});
            skLineSegment(sketch, "E2445", {"start": v(162.46, 53.15) * mm, "end": v(162.58, 53.04) * mm});
            skLineSegment(sketch, "E2446", {"start": v(162.58, 53.04) * mm, "end": v(162.68, 52.92) * mm});
            skLineSegment(sketch, "E2447", {"start": v(162.68, 52.92) * mm, "end": v(162.78, 52.8) * mm});
            skLineSegment(sketch, "E2448", {"start": v(162.78, 52.8) * mm, "end": v(162.87, 52.67) * mm});
            skLineSegment(sketch, "E2449", {"start": v(162.87, 52.67) * mm, "end": v(162.94, 52.53) * mm});
            skLineSegment(sketch, "E2450", {"start": v(162.94, 52.53) * mm, "end": v(163, 52.4) * mm});
            skLineSegment(sketch, "E2451", {"start": v(163, 52.4) * mm, "end": v(163.06, 52.24) * mm});
            skLineSegment(sketch, "E2452", {"start": v(163.06, 52.24) * mm, "end": v(163.1, 52.1) * mm});
            skLineSegment(sketch, "E2453", {"start": v(163.1, 52.1) * mm, "end": v(163.14, 51.94) * mm});
            skLineSegment(sketch, "E2454", {"start": v(163.14, 51.94) * mm, "end": v(163.16, 51.78) * mm});
            skLineSegment(sketch, "E2455", {"start": v(163.16, 51.78) * mm, "end": v(163.16, 51.62) * mm});
            skLineSegment(sketch, "E2456", {"start": v(163.16, 51.62) * mm, "end": v(163.16, -51.62) * mm});
            skLineSegment(sketch, "E2457", {"start": v(163.16, -51.62) * mm, "end": v(163.16, -51.78) * mm});
            skLineSegment(sketch, "E2458", {"start": v(163.16, -51.78) * mm, "end": v(163.14, -51.94) * mm});
            skLineSegment(sketch, "E2459", {"start": v(163.14, -51.94) * mm, "end": v(163.1, -52.1) * mm});
            skLineSegment(sketch, "E2460", {"start": v(163.1, -52.1) * mm, "end": v(163.06, -52.25) * mm});
            skLineSegment(sketch, "E2461", {"start": v(163.06, -52.25) * mm, "end": v(163, -52.4) * mm});
            skLineSegment(sketch, "E2462", {"start": v(163, -52.4) * mm, "end": v(162.94, -52.53) * mm});
            skLineSegment(sketch, "E2463", {"start": v(162.94, -52.53) * mm, "end": v(162.87, -52.67) * mm});
            skLineSegment(sketch, "E2464", {"start": v(162.87, -52.67) * mm, "end": v(162.78, -52.8) * mm});
            skLineSegment(sketch, "E2465", {"start": v(162.78, -52.8) * mm, "end": v(162.68, -52.92) * mm});
            skLineSegment(sketch, "E2466", {"start": v(162.68, -52.92) * mm, "end": v(162.58, -53.04) * mm});
            skLineSegment(sketch, "E2467", {"start": v(162.58, -53.04) * mm, "end": v(162.46, -53.15) * mm});
            skLineSegment(sketch, "E2468", {"start": v(162.46, -53.15) * mm, "end": v(162.34, -53.24) * mm});
            skLineSegment(sketch, "E2469", {"start": v(162.34, -53.24) * mm, "end": v(162.2, -53.33) * mm});
            skLineSegment(sketch, "E2470", {"start": v(162.2, -53.33) * mm, "end": v(162.07, -53.4) * mm});
            skLineSegment(sketch, "E2471", {"start": v(162.07, -53.4) * mm, "end": v(161.93, -53.47) * mm});
            skLineSegment(sketch, "E2472", {"start": v(161.93, -53.47) * mm, "end": v(161.78, -53.53) * mm});
            skLineSegment(sketch, "E2473", {"start": v(161.78, -53.53) * mm, "end": v(161.63, -53.57) * mm});
            skLineSegment(sketch, "E2474", {"start": v(161.63, -53.57) * mm, "end": v(161.48, -53.6) * mm});
            skLineSegment(sketch, "E2475", {"start": v(161.48, -53.6) * mm, "end": v(161.32, -53.62) * mm});
            skLineSegment(sketch, "E2476", {"start": v(161.32, -53.62) * mm, "end": v(161.16, -53.63) * mm});
            skLineSegment(sketch, "E2477", {"start": v(161.16, -53.63) * mm, "end": v(-161.16, -53.63) * mm});
            skLineSegment(sketch, "E2478", {"start": v(-161.16, -53.63) * mm, "end": v(-161.32, -53.62) * mm});
            skLineSegment(sketch, "E2479", {"start": v(-161.32, -53.62) * mm, "end": v(-161.48, -53.6) * mm});
            skLineSegment(sketch, "E2480", {"start": v(-161.48, -53.6) * mm, "end": v(-161.63, -53.57) * mm});
            skLineSegment(sketch, "E2481", {"start": v(-161.63, -53.57) * mm, "end": v(-161.78, -53.53) * mm});
            skLineSegment(sketch, "E2482", {"start": v(-161.78, -53.53) * mm, "end": v(-161.93, -53.47) * mm});
            skLineSegment(sketch, "E2483", {"start": v(-161.93, -53.47) * mm, "end": v(-162.07, -53.4) * mm});
            skLineSegment(sketch, "E2484", {"start": v(-162.07, -53.4) * mm, "end": v(-162.2, -53.33) * mm});
            skLineSegment(sketch, "E2485", {"start": v(-162.2, -53.33) * mm, "end": v(-162.34, -53.24) * mm});
            skLineSegment(sketch, "E2486", {"start": v(-162.34, -53.24) * mm, "end": v(-162.46, -53.15) * mm});
            skLineSegment(sketch, "E2487", {"start": v(-162.46, -53.15) * mm, "end": v(-162.58, -53.04) * mm});
            skLineSegment(sketch, "E2488", {"start": v(-162.58, -53.04) * mm, "end": v(-162.68, -52.92) * mm});
            skLineSegment(sketch, "E2489", {"start": v(-162.68, -52.92) * mm, "end": v(-162.78, -52.8) * mm});
            skLineSegment(sketch, "E2490", {"start": v(-162.78, -52.8) * mm, "end": v(-162.87, -52.67) * mm});
            skLineSegment(sketch, "E2491", {"start": v(-162.87, -52.67) * mm, "end": v(-162.95, -52.53) * mm});
            skLineSegment(sketch, "E2492", {"start": v(-162.95, -52.53) * mm, "end": v(-163.01, -52.4) * mm});
            skLineSegment(sketch, "E2493", {"start": v(-163.01, -52.4) * mm, "end": v(-163.07, -52.25) * mm});
            skLineSegment(sketch, "E2494", {"start": v(-163.07, -52.25) * mm, "end": v(-163.1, -52.1) * mm});
            skLineSegment(sketch, "E2495", {"start": v(-163.1, -52.1) * mm, "end": v(-163.14, -51.94) * mm});
            skLineSegment(sketch, "E2496", {"start": v(-163.14, -51.94) * mm, "end": v(-163.16, -51.78) * mm});
            skLineSegment(sketch, "E2497", {"start": v(-163.16, -51.78) * mm, "end": v(-163.16, -51.63) * mm});
            skLineSegment(sketch, "E2498", {"start": v(-163.16, -51.63) * mm, "end": v(-163.16, 51.62) * mm});
            skLineSegment(sketch, "E2499", {"start": v(-163.16, 51.62) * mm, "end": v(-163.16, 51.78) * mm});
            skLineSegment(sketch, "E2500", {"start": v(-163.16, 51.78) * mm, "end": v(-163.14, 51.94) * mm});
            skLineSegment(sketch, "E2501", {"start": v(-163.14, 51.94) * mm, "end": v(-163.1, 52.1) * mm});
            skLineSegment(sketch, "E2502", {"start": v(-163.1, 52.1) * mm, "end": v(-163.07, 52.24) * mm});
            skLineSegment(sketch, "E2503", {"start": v(-163.07, 52.24) * mm, "end": v(-163.01, 52.4) * mm});
            skLineSegment(sketch, "E2504", {"start": v(-163.01, 52.4) * mm, "end": v(-162.95, 52.53) * mm});
            skLineSegment(sketch, "E2505", {"start": v(-162.95, 52.53) * mm, "end": v(-162.87, 52.67) * mm});
            skLineSegment(sketch, "E2506", {"start": v(-162.87, 52.67) * mm, "end": v(-162.78, 52.8) * mm});
            skLineSegment(sketch, "E2507", {"start": v(-162.78, 52.8) * mm, "end": v(-162.68, 52.92) * mm});
            skLineSegment(sketch, "E2508", {"start": v(-162.68, 52.92) * mm, "end": v(-162.58, 53.04) * mm});
            skLineSegment(sketch, "E2509", {"start": v(-162.58, 53.04) * mm, "end": v(-162.46, 53.15) * mm});
            skLineSegment(sketch, "E2510", {"start": v(-162.46, 53.15) * mm, "end": v(-162.34, 53.24) * mm});
            skLineSegment(sketch, "E2511", {"start": v(-162.34, 53.24) * mm, "end": v(-162.2, 53.33) * mm});
            skLineSegment(sketch, "E2512", {"start": v(-162.2, 53.33) * mm, "end": v(-162.07, 53.4) * mm});
            skLineSegment(sketch, "E2513", {"start": v(-162.07, 53.4) * mm, "end": v(-161.93, 53.47) * mm});
            skLineSegment(sketch, "E2514", {"start": v(-161.93, 53.47) * mm, "end": v(-161.78, 53.53) * mm});
            skLineSegment(sketch, "E2515", {"start": v(-161.78, 53.53) * mm, "end": v(-161.63, 53.57) * mm});
            skLineSegment(sketch, "E2516", {"start": v(-161.63, 53.57) * mm, "end": v(-161.48, 53.6) * mm});
            skLineSegment(sketch, "E2517", {"start": v(-161.48, 53.6) * mm, "end": v(-161.32, 53.62) * mm});
            skLineSegment(sketch, "E2518", {"start": v(-161.32, 53.62) * mm, "end": v(-161.16, 53.63) * mm});
            skLineSegment(sketch, "E2519", {"start": v(-161.16, 53.63) * mm, "end": v(161.16, 53.62) * mm});
            skLineSegment(sketch, "E2520", {"start": v(160.2, -49.7) * mm, "end": v(159.78, -49.91) * mm});
            skLineSegment(sketch, "E2521", {"start": v(159.78, -49.91) * mm, "end": v(159.45, -50.24) * mm});
            skLineSegment(sketch, "E2522", {"start": v(159.45, -50.24) * mm, "end": v(159.24, -50.66) * mm});
            skLineSegment(sketch, "E2523", {"start": v(159.24, -50.66) * mm, "end": v(159.16, -51.13) * mm});
            skLineSegment(sketch, "E2524", {"start": v(159.16, -51.13) * mm, "end": v(159.24, -51.59) * mm});
            skLineSegment(sketch, "E2525", {"start": v(159.24, -51.59) * mm, "end": v(159.45, -52) * mm});
            skLineSegment(sketch, "E2526", {"start": v(159.45, -52) * mm, "end": v(159.78, -52.34) * mm});
            skLineSegment(sketch, "E2527", {"start": v(159.78, -52.34) * mm, "end": v(160.2, -52.55) * mm});
            skLineSegment(sketch, "E2528", {"start": v(160.2, -52.55) * mm, "end": v(160.66, -52.63) * mm});
            skLineSegment(sketch, "E2529", {"start": v(160.66, -52.63) * mm, "end": v(161.13, -52.55) * mm});
            skLineSegment(sketch, "E2530", {"start": v(161.13, -52.55) * mm, "end": v(161.54, -52.34) * mm});
            skLineSegment(sketch, "E2531", {"start": v(161.54, -52.34) * mm, "end": v(161.88, -52) * mm});
            skLineSegment(sketch, "E2532", {"start": v(161.88, -52) * mm, "end": v(162.09, -51.59) * mm});
            skLineSegment(sketch, "E2533", {"start": v(162.09, -51.59) * mm, "end": v(162.16, -51.13) * mm});
            skLineSegment(sketch, "E2534", {"start": v(162.16, -51.13) * mm, "end": v(162.09, -50.66) * mm});
            skLineSegment(sketch, "E2535", {"start": v(162.09, -50.66) * mm, "end": v(161.88, -50.24) * mm});
            skLineSegment(sketch, "E2536", {"start": v(161.88, -50.24) * mm, "end": v(161.54, -49.91) * mm});
            skLineSegment(sketch, "E2537", {"start": v(161.54, -49.91) * mm, "end": v(161.13, -49.7) * mm});
            skLineSegment(sketch, "E2538", {"start": v(161.13, -49.7) * mm, "end": v(160.66, -49.63) * mm});
            skLineSegment(sketch, "E2539", {"start": v(160.66, -49.63) * mm, "end": v(160.2, -49.7) * mm});
            skLineSegment(sketch, "E2540", {"start": v(53.1, -49.7) * mm, "end": v(52.67, -49.91) * mm});
            skLineSegment(sketch, "E2541", {"start": v(52.67, -49.91) * mm, "end": v(52.34, -50.24) * mm});
            skLineSegment(sketch, "E2542", {"start": v(52.34, -50.24) * mm, "end": v(52.13, -50.66) * mm});
            skLineSegment(sketch, "E2543", {"start": v(52.13, -50.66) * mm, "end": v(52.05, -51.13) * mm});
            skLineSegment(sketch, "E2544", {"start": v(52.05, -51.13) * mm, "end": v(52.13, -51.59) * mm});
            skLineSegment(sketch, "E2545", {"start": v(52.13, -51.59) * mm, "end": v(52.34, -52) * mm});
            skLineSegment(sketch, "E2546", {"start": v(52.34, -52) * mm, "end": v(52.67, -52.34) * mm});
            skLineSegment(sketch, "E2547", {"start": v(52.67, -52.34) * mm, "end": v(53.1, -52.55) * mm});
            skLineSegment(sketch, "E2548", {"start": v(53.1, -52.55) * mm, "end": v(53.55, -52.63) * mm});
            skLineSegment(sketch, "E2549", {"start": v(53.55, -52.63) * mm, "end": v(54.02, -52.55) * mm});
            skLineSegment(sketch, "E2550", {"start": v(54.02, -52.55) * mm, "end": v(54.44, -52.34) * mm});
            skLineSegment(sketch, "E2551", {"start": v(54.44, -52.34) * mm, "end": v(54.77, -52) * mm});
            skLineSegment(sketch, "E2552", {"start": v(54.77, -52) * mm, "end": v(54.98, -51.59) * mm});
            skLineSegment(sketch, "E2553", {"start": v(54.98, -51.59) * mm, "end": v(55.05, -51.13) * mm});
            skLineSegment(sketch, "E2554", {"start": v(55.05, -51.13) * mm, "end": v(54.98, -50.66) * mm});
            skLineSegment(sketch, "E2555", {"start": v(54.98, -50.66) * mm, "end": v(54.77, -50.24) * mm});
            skLineSegment(sketch, "E2556", {"start": v(54.77, -50.24) * mm, "end": v(54.44, -49.91) * mm});
            skLineSegment(sketch, "E2557", {"start": v(54.44, -49.91) * mm, "end": v(54.02, -49.7) * mm});
            skLineSegment(sketch, "E2558", {"start": v(54.02, -49.7) * mm, "end": v(53.55, -49.63) * mm});
            skLineSegment(sketch, "E2559", {"start": v(53.55, -49.63) * mm, "end": v(53.1, -49.7) * mm});
            skLineSegment(sketch, "E2560", {"start": v(-54.02, -49.7) * mm, "end": v(-54.44, -49.91) * mm});
            skLineSegment(sketch, "E2561", {"start": v(-54.44, -49.91) * mm, "end": v(-54.77, -50.24) * mm});
            skLineSegment(sketch, "E2562", {"start": v(-54.77, -50.24) * mm, "end": v(-54.98, -50.66) * mm});
            skLineSegment(sketch, "E2563", {"start": v(-54.98, -50.66) * mm, "end": v(-55.06, -51.13) * mm});
            skLineSegment(sketch, "E2564", {"start": v(-55.06, -51.13) * mm, "end": v(-54.98, -51.59) * mm});
            skLineSegment(sketch, "E2565", {"start": v(-54.98, -51.59) * mm, "end": v(-54.77, -52) * mm});
            skLineSegment(sketch, "E2566", {"start": v(-54.77, -52) * mm, "end": v(-54.44, -52.34) * mm});
            skLineSegment(sketch, "E2567", {"start": v(-54.44, -52.34) * mm, "end": v(-54.02, -52.55) * mm});
            skLineSegment(sketch, "E2568", {"start": v(-54.02, -52.55) * mm, "end": v(-53.55, -52.63) * mm});
            skLineSegment(sketch, "E2569", {"start": v(-53.55, -52.63) * mm, "end": v(-53.1, -52.55) * mm});
            skLineSegment(sketch, "E2570", {"start": v(-53.1, -52.55) * mm, "end": v(-52.67, -52.34) * mm});
            skLineSegment(sketch, "E2571", {"start": v(-52.67, -52.34) * mm, "end": v(-52.34, -52) * mm});
            skLineSegment(sketch, "E2572", {"start": v(-52.34, -52) * mm, "end": v(-52.13, -51.59) * mm});
            skLineSegment(sketch, "E2573", {"start": v(-52.13, -51.59) * mm, "end": v(-52.06, -51.13) * mm});
            skLineSegment(sketch, "E2574", {"start": v(-52.06, -51.13) * mm, "end": v(-52.13, -50.66) * mm});
            skLineSegment(sketch, "E2575", {"start": v(-52.13, -50.66) * mm, "end": v(-52.34, -50.24) * mm});
            skLineSegment(sketch, "E2576", {"start": v(-52.34, -50.24) * mm, "end": v(-52.67, -49.91) * mm});
            skLineSegment(sketch, "E2577", {"start": v(-52.67, -49.91) * mm, "end": v(-53.1, -49.7) * mm});
            skLineSegment(sketch, "E2578", {"start": v(-53.1, -49.7) * mm, "end": v(-53.55, -49.63) * mm});
            skLineSegment(sketch, "E2579", {"start": v(-53.55, -49.63) * mm, "end": v(-54.02, -49.7) * mm});
            skLineSegment(sketch, "E2580", {"start": v(-161.13, -49.7) * mm, "end": v(-161.54, -49.91) * mm});
            skLineSegment(sketch, "E2581", {"start": v(-161.54, -49.91) * mm, "end": v(-161.88, -50.24) * mm});
            skLineSegment(sketch, "E2582", {"start": v(-161.88, -50.24) * mm, "end": v(-162.1, -50.66) * mm});
            skLineSegment(sketch, "E2583", {"start": v(-162.1, -50.66) * mm, "end": v(-162.16, -51.13) * mm});
            skLineSegment(sketch, "E2584", {"start": v(-162.16, -51.13) * mm, "end": v(-162.1, -51.59) * mm});
            skLineSegment(sketch, "E2585", {"start": v(-162.1, -51.59) * mm, "end": v(-161.88, -52) * mm});
            skLineSegment(sketch, "E2586", {"start": v(-161.88, -52) * mm, "end": v(-161.54, -52.34) * mm});
            skLineSegment(sketch, "E2587", {"start": v(-161.54, -52.34) * mm, "end": v(-161.13, -52.55) * mm});
            skLineSegment(sketch, "E2588", {"start": v(-161.13, -52.55) * mm, "end": v(-160.66, -52.63) * mm});
            skLineSegment(sketch, "E2589", {"start": v(-160.66, -52.63) * mm, "end": v(-160.2, -52.55) * mm});
            skLineSegment(sketch, "E2590", {"start": v(-160.2, -52.55) * mm, "end": v(-159.78, -52.34) * mm});
            skLineSegment(sketch, "E2591", {"start": v(-159.78, -52.34) * mm, "end": v(-159.45, -52) * mm});
            skLineSegment(sketch, "E2592", {"start": v(-159.45, -52) * mm, "end": v(-159.24, -51.59) * mm});
            skLineSegment(sketch, "E2593", {"start": v(-159.24, -51.59) * mm, "end": v(-159.16, -51.13) * mm});
            skLineSegment(sketch, "E2594", {"start": v(-159.16, -51.13) * mm, "end": v(-159.24, -50.66) * mm});
            skLineSegment(sketch, "E2595", {"start": v(-159.24, -50.66) * mm, "end": v(-159.45, -50.24) * mm});
            skLineSegment(sketch, "E2596", {"start": v(-159.45, -50.24) * mm, "end": v(-159.78, -49.91) * mm});
            skLineSegment(sketch, "E2597", {"start": v(-159.78, -49.91) * mm, "end": v(-160.2, -49.7) * mm});
            skLineSegment(sketch, "E2598", {"start": v(-160.2, -49.7) * mm, "end": v(-160.66, -49.63) * mm});
            skLineSegment(sketch, "E2599", {"start": v(-160.66, -49.63) * mm, "end": v(-161.13, -49.7) * mm});
            skLineSegment(sketch, "E2600", {"start": v(-157.17, 47.63) * mm, "end": v(-157.17, 28.57) * mm});
            skLineSegment(sketch, "E2601", {"start": v(-157.17, 28.57) * mm, "end": v(-157.16, 28.57) * mm});
            skLineSegment(sketch, "E2602", {"start": v(-157.16, 28.57) * mm, "end": v(-157.16, 9.53) * mm});
            skLineSegment(sketch, "E2603", {"start": v(-157.16, 9.53) * mm, "end": v(-157.17, 9.53) * mm});
            skLineSegment(sketch, "E2604", {"start": v(-157.17, 9.53) * mm, "end": v(-157.17, -9.53) * mm});
            skLineSegment(sketch, "E2605", {"start": v(-157.17, -9.53) * mm, "end": v(-157.16, -9.53) * mm});
            skLineSegment(sketch, "E2606", {"start": v(-157.16, -9.53) * mm, "end": v(-157.16, -28.57) * mm});
            skLineSegment(sketch, "E2607", {"start": v(-157.16, -28.57) * mm, "end": v(-157.17, -28.57) * mm});
            skLineSegment(sketch, "E2608", {"start": v(-157.17, -28.57) * mm, "end": v(-157.17, -47.63) * mm});
            skLineSegment(sketch, "E2609", {"start": v(-157.17, -47.63) * mm, "end": v(76.2, -47.63) * mm});
            skLineSegment(sketch, "E2610", {"start": v(76.2, -47.63) * mm, "end": v(76.2, -28.58) * mm});
            skLineSegment(sketch, "E2611", {"start": v(76.2, -28.58) * mm, "end": v(100.01, -28.58) * mm});
            skLineSegment(sketch, "E2612", {"start": v(100.01, -28.58) * mm, "end": v(100.01, -47.63) * mm});
            skLineSegment(sketch, "E2613", {"start": v(100.01, -47.63) * mm, "end": v(157.16, -47.63) * mm});
            skLineSegment(sketch, "E2614", {"start": v(157.16, -47.63) * mm, "end": v(157.16, -28.57) * mm});
            skLineSegment(sketch, "E2615", {"start": v(157.16, -28.57) * mm, "end": v(138.11, -28.57) * mm});
            skLineSegment(sketch, "E2616", {"start": v(138.11, -28.57) * mm, "end": v(138.11, -9.52) * mm});
            skLineSegment(sketch, "E2617", {"start": v(138.11, -9.52) * mm, "end": v(128.59, -9.52) * mm});
            skLineSegment(sketch, "E2618", {"start": v(128.59, -9.52) * mm, "end": v(128.59, 47.63) * mm});
            skLineSegment(sketch, "E2619", {"start": v(128.59, 47.63) * mm, "end": v(-157.17, 47.63) * mm});
            skLineSegment(sketch, "E2620", {"start": v(138.11, 47.63) * mm, "end": v(157.16, 47.63) * mm});
            skLineSegment(sketch, "E2621", {"start": v(157.16, 47.63) * mm, "end": v(157.16, 9.52) * mm});
            skLineSegment(sketch, "E2622", {"start": v(157.16, 9.52) * mm, "end": v(138.11, 9.52) * mm});
            skLineSegment(sketch, "E2623", {"start": v(138.11, 9.52) * mm, "end": v(138.11, 47.63) * mm});
            skLineSegment(sketch, "E2624", {"start": v(-54.02, 52.55) * mm, "end": v(-54.44, 52.34) * mm});
            skLineSegment(sketch, "E2625", {"start": v(-54.44, 52.34) * mm, "end": v(-54.77, 52) * mm});
            skLineSegment(sketch, "E2626", {"start": v(-54.77, 52) * mm, "end": v(-54.98, 51.59) * mm});
            skLineSegment(sketch, "E2627", {"start": v(-54.98, 51.59) * mm, "end": v(-55.06, 51.12) * mm});
            skLineSegment(sketch, "E2628", {"start": v(-55.06, 51.12) * mm, "end": v(-54.98, 50.66) * mm});
            skLineSegment(sketch, "E2629", {"start": v(-54.98, 50.66) * mm, "end": v(-54.77, 50.24) * mm});
            skLineSegment(sketch, "E2630", {"start": v(-54.77, 50.24) * mm, "end": v(-54.44, 49.91) * mm});
            skLineSegment(sketch, "E2631", {"start": v(-54.44, 49.91) * mm, "end": v(-54.02, 49.7) * mm});
            skLineSegment(sketch, "E2632", {"start": v(-54.02, 49.7) * mm, "end": v(-53.55, 49.62) * mm});
            skLineSegment(sketch, "E2633", {"start": v(-53.55, 49.62) * mm, "end": v(-53.1, 49.7) * mm});
            skLineSegment(sketch, "E2634", {"start": v(-53.1, 49.7) * mm, "end": v(-52.67, 49.91) * mm});
            skLineSegment(sketch, "E2635", {"start": v(-52.67, 49.91) * mm, "end": v(-52.34, 50.24) * mm});
            skLineSegment(sketch, "E2636", {"start": v(-52.34, 50.24) * mm, "end": v(-52.13, 50.66) * mm});
            skLineSegment(sketch, "E2637", {"start": v(-52.13, 50.66) * mm, "end": v(-52.06, 51.12) * mm});
            skLineSegment(sketch, "E2638", {"start": v(-52.06, 51.12) * mm, "end": v(-52.13, 51.59) * mm});
            skLineSegment(sketch, "E2639", {"start": v(-52.13, 51.59) * mm, "end": v(-52.34, 52) * mm});
            skLineSegment(sketch, "E2640", {"start": v(-52.34, 52) * mm, "end": v(-52.67, 52.34) * mm});
            skLineSegment(sketch, "E2641", {"start": v(-52.67, 52.34) * mm, "end": v(-53.1, 52.55) * mm});
            skLineSegment(sketch, "E2642", {"start": v(-53.1, 52.55) * mm, "end": v(-53.55, 52.62) * mm});
            skLineSegment(sketch, "E2643", {"start": v(-53.55, 52.62) * mm, "end": v(-54.02, 52.55) * mm});
            skLineSegment(sketch, "E2644", {"start": v(53.1, 52.55) * mm, "end": v(52.67, 52.34) * mm});
            skLineSegment(sketch, "E2645", {"start": v(52.67, 52.34) * mm, "end": v(52.34, 52) * mm});
            skLineSegment(sketch, "E2646", {"start": v(52.34, 52) * mm, "end": v(52.13, 51.59) * mm});
            skLineSegment(sketch, "E2647", {"start": v(52.13, 51.59) * mm, "end": v(52.05, 51.12) * mm});
            skLineSegment(sketch, "E2648", {"start": v(52.05, 51.12) * mm, "end": v(52.13, 50.66) * mm});
            skLineSegment(sketch, "E2649", {"start": v(52.13, 50.66) * mm, "end": v(52.34, 50.24) * mm});
            skLineSegment(sketch, "E2650", {"start": v(52.34, 50.24) * mm, "end": v(52.67, 49.91) * mm});
            skLineSegment(sketch, "E2651", {"start": v(52.67, 49.91) * mm, "end": v(53.1, 49.7) * mm});
            skLineSegment(sketch, "E2652", {"start": v(53.1, 49.7) * mm, "end": v(53.55, 49.62) * mm});
            skLineSegment(sketch, "E2653", {"start": v(53.55, 49.62) * mm, "end": v(54.02, 49.7) * mm});
            skLineSegment(sketch, "E2654", {"start": v(54.02, 49.7) * mm, "end": v(54.44, 49.91) * mm});
            skLineSegment(sketch, "E2655", {"start": v(54.44, 49.91) * mm, "end": v(54.77, 50.24) * mm});
            skLineSegment(sketch, "E2656", {"start": v(54.77, 50.24) * mm, "end": v(54.98, 50.66) * mm});
            skLineSegment(sketch, "E2657", {"start": v(54.98, 50.66) * mm, "end": v(55.05, 51.12) * mm});
            skLineSegment(sketch, "E2658", {"start": v(55.05, 51.12) * mm, "end": v(54.98, 51.59) * mm});
            skLineSegment(sketch, "E2659", {"start": v(54.98, 51.59) * mm, "end": v(54.77, 52) * mm});
            skLineSegment(sketch, "E2660", {"start": v(54.77, 52) * mm, "end": v(54.44, 52.34) * mm});
            skLineSegment(sketch, "E2661", {"start": v(54.44, 52.34) * mm, "end": v(54.02, 52.55) * mm});
            skLineSegment(sketch, "E2662", {"start": v(54.02, 52.55) * mm, "end": v(53.55, 52.62) * mm});
            skLineSegment(sketch, "E2663", {"start": v(53.55, 52.62) * mm, "end": v(53.1, 52.55) * mm});
            skLineSegment(sketch, "E2664", {"start": v(160.2, 52.55) * mm, "end": v(159.78, 52.34) * mm});
            skLineSegment(sketch, "E2665", {"start": v(159.78, 52.34) * mm, "end": v(159.45, 52) * mm});
            skLineSegment(sketch, "E2666", {"start": v(159.45, 52) * mm, "end": v(159.24, 51.59) * mm});
            skLineSegment(sketch, "E2667", {"start": v(159.24, 51.59) * mm, "end": v(159.16, 51.12) * mm});
            skLineSegment(sketch, "E2668", {"start": v(159.16, 51.12) * mm, "end": v(159.24, 50.66) * mm});
            skLineSegment(sketch, "E2669", {"start": v(159.24, 50.66) * mm, "end": v(159.45, 50.24) * mm});
            skLineSegment(sketch, "E2670", {"start": v(159.45, 50.24) * mm, "end": v(159.78, 49.91) * mm});
            skLineSegment(sketch, "E2671", {"start": v(159.78, 49.91) * mm, "end": v(160.2, 49.7) * mm});
            skLineSegment(sketch, "E2672", {"start": v(160.2, 49.7) * mm, "end": v(160.66, 49.62) * mm});
            skLineSegment(sketch, "E2673", {"start": v(160.66, 49.62) * mm, "end": v(161.13, 49.7) * mm});
            skLineSegment(sketch, "E2674", {"start": v(161.13, 49.7) * mm, "end": v(161.54, 49.91) * mm});
            skLineSegment(sketch, "E2675", {"start": v(161.54, 49.91) * mm, "end": v(161.88, 50.24) * mm});
            skLineSegment(sketch, "E2676", {"start": v(161.88, 50.24) * mm, "end": v(162.09, 50.66) * mm});
            skLineSegment(sketch, "E2677", {"start": v(162.09, 50.66) * mm, "end": v(162.16, 51.12) * mm});
            skLineSegment(sketch, "E2678", {"start": v(162.16, 51.12) * mm, "end": v(162.09, 51.59) * mm});
            skLineSegment(sketch, "E2679", {"start": v(162.09, 51.59) * mm, "end": v(161.88, 52) * mm});
            skLineSegment(sketch, "E2680", {"start": v(161.88, 52) * mm, "end": v(161.54, 52.34) * mm});
            skLineSegment(sketch, "E2681", {"start": v(161.54, 52.34) * mm, "end": v(161.13, 52.55) * mm});
            skLineSegment(sketch, "E2682", {"start": v(161.13, 52.55) * mm, "end": v(160.66, 52.62) * mm});
            skLineSegment(sketch, "E2683", {"start": v(160.66, 52.62) * mm, "end": v(160.2, 52.55) * mm});
            skLineSegment(sketch, "E2684", {"start": v(-161.13, 52.55) * mm, "end": v(-161.54, 52.34) * mm});
            skLineSegment(sketch, "E2685", {"start": v(-161.54, 52.34) * mm, "end": v(-161.88, 52) * mm});
            skLineSegment(sketch, "E2686", {"start": v(-161.88, 52) * mm, "end": v(-162.1, 51.59) * mm});
            skLineSegment(sketch, "E2687", {"start": v(-162.1, 51.59) * mm, "end": v(-162.16, 51.12) * mm});
            skLineSegment(sketch, "E2688", {"start": v(-162.16, 51.12) * mm, "end": v(-162.1, 50.66) * mm});
            skLineSegment(sketch, "E2689", {"start": v(-162.1, 50.66) * mm, "end": v(-161.88, 50.24) * mm});
            skLineSegment(sketch, "E2690", {"start": v(-161.88, 50.24) * mm, "end": v(-161.54, 49.91) * mm});
            skLineSegment(sketch, "E2691", {"start": v(-161.54, 49.91) * mm, "end": v(-161.13, 49.7) * mm});
            skLineSegment(sketch, "E2692", {"start": v(-161.13, 49.7) * mm, "end": v(-160.66, 49.62) * mm});
            skLineSegment(sketch, "E2693", {"start": v(-160.66, 49.62) * mm, "end": v(-160.2, 49.7) * mm});
            skLineSegment(sketch, "E2694", {"start": v(-160.2, 49.7) * mm, "end": v(-159.78, 49.91) * mm});
            skLineSegment(sketch, "E2695", {"start": v(-159.78, 49.91) * mm, "end": v(-159.45, 50.24) * mm});
            skLineSegment(sketch, "E2696", {"start": v(-159.45, 50.24) * mm, "end": v(-159.24, 50.66) * mm});
            skLineSegment(sketch, "E2697", {"start": v(-159.24, 50.66) * mm, "end": v(-159.16, 51.12) * mm});
            skLineSegment(sketch, "E2698", {"start": v(-159.16, 51.12) * mm, "end": v(-159.24, 51.59) * mm});
            skLineSegment(sketch, "E2699", {"start": v(-159.24, 51.59) * mm, "end": v(-159.45, 52) * mm});
            skLineSegment(sketch, "E2700", {"start": v(-159.45, 52) * mm, "end": v(-159.78, 52.34) * mm});
            skLineSegment(sketch, "E2701", {"start": v(-159.78, 52.34) * mm, "end": v(-160.2, 52.55) * mm});
            skLineSegment(sketch, "E2702", {"start": v(-160.2, 52.55) * mm, "end": v(-160.66, 52.62) * mm});
            skLineSegment(sketch, "E2703", {"start": v(-160.66, 52.62) * mm, "end": v(-161.13, 52.55) * mm});
            skSolve(sketch);
        }
        {
            var Q0;
            Q0 = qSketchRegion(id + "F9", true);
            extrude(context, id + "F10", {"entities" : qUnion([Q0]), "depth" : (getVariable(context, 'Thickness')) * mm, "offsetDistance" : 25 * mm});
        }
        {
            var Q0;
            Q0=makeQuery(id+"F10.opExtrude","CAP_FACE",FACE,{"disambiguationData":[OSD([sQuery(id+"F9.wireOp",EDGE,"E2436"),sQuery(id+"F9.wireOp",EDGE,"E2437"),sQuery(id+"F9.wireOp",EDGE,"E2438"),sQuery(id+"F9.wireOp",EDGE,"E2439"),sQuery(id+"F9.wireOp",EDGE,"E2440"),sQuery(id+"F9.wireOp",EDGE,"E2441"),sQuery(id+"F9.wireOp",EDGE,"E2442"),sQuery(id+"F9.wireOp",EDGE,"E2443"),sQuery(id+"F9.wireOp",EDGE,"E2444"),sQuery(id+"F9.wireOp",EDGE,"E2445"),sQuery(id+"F9.wireOp",EDGE,"E2446"),sQuery(id+"F9.wireOp",EDGE,"E2447"),sQuery(id+"F9.wireOp",EDGE,"E2448"),sQuery(id+"F9.wireOp",EDGE,"E2449"),sQuery(id+"F9.wireOp",EDGE,"E2450"),sQuery(id+"F9.wireOp",EDGE,"E2451"),sQuery(id+"F9.wireOp",EDGE,"E2452"),sQuery(id+"F9.wireOp",EDGE,"E2453"),sQuery(id+"F9.wireOp",EDGE,"E2454"),sQuery(id+"F9.wireOp",EDGE,"E2455"),sQuery(id+"F9.wireOp",EDGE,"E2456"),sQuery(id+"F9.wireOp",EDGE,"E2457"),sQuery(id+"F9.wireOp",EDGE,"E2458"),sQuery(id+"F9.wireOp",EDGE,"E2459"),sQuery(id+"F9.wireOp",EDGE,"E2460"),sQuery(id+"F9.wireOp",EDGE,"E2461"),sQuery(id+"F9.wireOp",EDGE,"E2462"),sQuery(id+"F9.wireOp",EDGE,"E2463"),sQuery(id+"F9.wireOp",EDGE,"E2464"),sQuery(id+"F9.wireOp",EDGE,"E2465"),sQuery(id+"F9.wireOp",EDGE,"E2466"),sQuery(id+"F9.wireOp",EDGE,"E2467"),sQuery(id+"F9.wireOp",EDGE,"E2468"),sQuery(id+"F9.wireOp",EDGE,"E2469"),sQuery(id+"F9.wireOp",EDGE,"E2470"),sQuery(id+"F9.wireOp",EDGE,"E2471"),sQuery(id+"F9.wireOp",EDGE,"E2472"),sQuery(id+"F9.wireOp",EDGE,"E2473"),sQuery(id+"F9.wireOp",EDGE,"E2474"),sQuery(id+"F9.wireOp",EDGE,"E2475"),sQuery(id+"F9.wireOp",EDGE,"E2476"),sQuery(id+"F9.wireOp",EDGE,"E2477"),sQuery(id+"F9.wireOp",EDGE,"E2478"),sQuery(id+"F9.wireOp",EDGE,"E2479"),sQuery(id+"F9.wireOp",EDGE,"E2480"),sQuery(id+"F9.wireOp",EDGE,"E2481"),sQuery(id+"F9.wireOp",EDGE,"E2482"),sQuery(id+"F9.wireOp",EDGE,"E2483"),sQuery(id+"F9.wireOp",EDGE,"E2484"),sQuery(id+"F9.wireOp",EDGE,"E2485"),sQuery(id+"F9.wireOp",EDGE,"E2486"),sQuery(id+"F9.wireOp",EDGE,"E2487"),sQuery(id+"F9.wireOp",EDGE,"E2488"),sQuery(id+"F9.wireOp",EDGE,"E2489"),sQuery(id+"F9.wireOp",EDGE,"E2490"),sQuery(id+"F9.wireOp",EDGE,"E2491"),sQuery(id+"F9.wireOp",EDGE,"E2492"),sQuery(id+"F9.wireOp",EDGE,"E2493"),sQuery(id+"F9.wireOp",EDGE,"E2494"),sQuery(id+"F9.wireOp",EDGE,"E2495"),sQuery(id+"F9.wireOp",EDGE,"E2496"),sQuery(id+"F9.wireOp",EDGE,"E2497"),sQuery(id+"F9.wireOp",EDGE,"E2498"),sQuery(id+"F9.wireOp",EDGE,"E2499"),sQuery(id+"F9.wireOp",EDGE,"E2500"),sQuery(id+"F9.wireOp",EDGE,"E2501"),sQuery(id+"F9.wireOp",EDGE,"E2502"),sQuery(id+"F9.wireOp",EDGE,"E2503"),sQuery(id+"F9.wireOp",EDGE,"E2504"),sQuery(id+"F9.wireOp",EDGE,"E2505"),sQuery(id+"F9.wireOp",EDGE,"E2506"),sQuery(id+"F9.wireOp",EDGE,"E2507"),sQuery(id+"F9.wireOp",EDGE,"E2508"),sQuery(id+"F9.wireOp",EDGE,"E2509"),sQuery(id+"F9.wireOp",EDGE,"E2510"),sQuery(id+"F9.wireOp",EDGE,"E2511"),sQuery(id+"F9.wireOp",EDGE,"E2512"),sQuery(id+"F9.wireOp",EDGE,"E2513"),sQuery(id+"F9.wireOp",EDGE,"E2514"),sQuery(id+"F9.wireOp",EDGE,"E2515"),sQuery(id+"F9.wireOp",EDGE,"E2516"),sQuery(id+"F9.wireOp",EDGE,"E2517"),sQuery(id+"F9.wireOp",EDGE,"E2518"),sQuery(id+"F9.wireOp",EDGE,"E2519"),sQuery(id+"F9.wireOp",EDGE,"E2520"),sQuery(id+"F9.wireOp",EDGE,"E2521"),sQuery(id+"F9.wireOp",EDGE,"E2522"),sQuery(id+"F9.wireOp",EDGE,"E2523"),sQuery(id+"F9.wireOp",EDGE,"E2524"),sQuery(id+"F9.wireOp",EDGE,"E2525"),sQuery(id+"F9.wireOp",EDGE,"E2526"),sQuery(id+"F9.wireOp",EDGE,"E2527"),sQuery(id+"F9.wireOp",EDGE,"E2528"),sQuery(id+"F9.wireOp",EDGE,"E2529"),sQuery(id+"F9.wireOp",EDGE,"E2530"),sQuery(id+"F9.wireOp",EDGE,"E2531"),sQuery(id+"F9.wireOp",EDGE,"E2532"),sQuery(id+"F9.wireOp",EDGE,"E2533"),sQuery(id+"F9.wireOp",EDGE,"E2534"),sQuery(id+"F9.wireOp",EDGE,"E2535"),sQuery(id+"F9.wireOp",EDGE,"E2536"),sQuery(id+"F9.wireOp",EDGE,"E2537"),sQuery(id+"F9.wireOp",EDGE,"E2538"),sQuery(id+"F9.wireOp",EDGE,"E2539"),sQuery(id+"F9.wireOp",EDGE,"E2540"),sQuery(id+"F9.wireOp",EDGE,"E2541"),sQuery(id+"F9.wireOp",EDGE,"E2542"),sQuery(id+"F9.wireOp",EDGE,"E2543"),sQuery(id+"F9.wireOp",EDGE,"E2544"),sQuery(id+"F9.wireOp",EDGE,"E2545"),sQuery(id+"F9.wireOp",EDGE,"E2546"),sQuery(id+"F9.wireOp",EDGE,"E2547"),sQuery(id+"F9.wireOp",EDGE,"E2548"),sQuery(id+"F9.wireOp",EDGE,"E2549"),sQuery(id+"F9.wireOp",EDGE,"E2550"),sQuery(id+"F9.wireOp",EDGE,"E2551"),sQuery(id+"F9.wireOp",EDGE,"E2552"),sQuery(id+"F9.wireOp",EDGE,"E2553"),sQuery(id+"F9.wireOp",EDGE,"E2554"),sQuery(id+"F9.wireOp",EDGE,"E2555"),sQuery(id+"F9.wireOp",EDGE,"E2556"),sQuery(id+"F9.wireOp",EDGE,"E2557"),sQuery(id+"F9.wireOp",EDGE,"E2558"),sQuery(id+"F9.wireOp",EDGE,"E2559"),sQuery(id+"F9.wireOp",EDGE,"E2560"),sQuery(id+"F9.wireOp",EDGE,"E2561"),sQuery(id+"F9.wireOp",EDGE,"E2562"),sQuery(id+"F9.wireOp",EDGE,"E2563"),sQuery(id+"F9.wireOp",EDGE,"E2564"),sQuery(id+"F9.wireOp",EDGE,"E2565"),sQuery(id+"F9.wireOp",EDGE,"E2566"),sQuery(id+"F9.wireOp",EDGE,"E2567"),sQuery(id+"F9.wireOp",EDGE,"E2568"),sQuery(id+"F9.wireOp",EDGE,"E2569"),sQuery(id+"F9.wireOp",EDGE,"E2570"),sQuery(id+"F9.wireOp",EDGE,"E2571"),sQuery(id+"F9.wireOp",EDGE,"E2572"),sQuery(id+"F9.wireOp",EDGE,"E2573"),sQuery(id+"F9.wireOp",EDGE,"E2574"),sQuery(id+"F9.wireOp",EDGE,"E2575"),sQuery(id+"F9.wireOp",EDGE,"E2576"),sQuery(id+"F9.wireOp",EDGE,"E2577"),sQuery(id+"F9.wireOp",EDGE,"E2578"),sQuery(id+"F9.wireOp",EDGE,"E2579"),sQuery(id+"F9.wireOp",EDGE,"E2580"),sQuery(id+"F9.wireOp",EDGE,"E2581"),sQuery(id+"F9.wireOp",EDGE,"E2582"),sQuery(id+"F9.wireOp",EDGE,"E2583"),sQuery(id+"F9.wireOp",EDGE,"E2584"),sQuery(id+"F9.wireOp",EDGE,"E2585"),sQuery(id+"F9.wireOp",EDGE,"E2586"),sQuery(id+"F9.wireOp",EDGE,"E2587"),sQuery(id+"F9.wireOp",EDGE,"E2588"),sQuery(id+"F9.wireOp",EDGE,"E2589"),sQuery(id+"F9.wireOp",EDGE,"E2590"),sQuery(id+"F9.wireOp",EDGE,"E2591"),sQuery(id+"F9.wireOp",EDGE,"E2592"),sQuery(id+"F9.wireOp",EDGE,"E2593"),sQuery(id+"F9.wireOp",EDGE,"E2594"),sQuery(id+"F9.wireOp",EDGE,"E2595"),sQuery(id+"F9.wireOp",EDGE,"E2596"),sQuery(id+"F9.wireOp",EDGE,"E2597"),sQuery(id+"F9.wireOp",EDGE,"E2598"),sQuery(id+"F9.wireOp",EDGE,"E2599"),sQuery(id+"F9.wireOp",EDGE,"E2600"),sQuery(id+"F9.wireOp",EDGE,"E2601"),sQuery(id+"F9.wireOp",EDGE,"E2602"),sQuery(id+"F9.wireOp",EDGE,"E2603"),sQuery(id+"F9.wireOp",EDGE,"E2604"),sQuery(id+"F9.wireOp",EDGE,"E2605"),sQuery(id+"F9.wireOp",EDGE,"E2606"),sQuery(id+"F9.wireOp",EDGE,"E2607"),sQuery(id+"F9.wireOp",EDGE,"E2608"),sQuery(id+"F9.wireOp",EDGE,"E2609"),sQuery(id+"F9.wireOp",EDGE,"E2610"),sQuery(id+"F9.wireOp",EDGE,"E2611"),sQuery(id+"F9.wireOp",EDGE,"E2612"),sQuery(id+"F9.wireOp",EDGE,"E2613"),sQuery(id+"F9.wireOp",EDGE,"E2614"),sQuery(id+"F9.wireOp",EDGE,"E2615"),sQuery(id+"F9.wireOp",EDGE,"E2616"),sQuery(id+"F9.wireOp",EDGE,"E2617"),sQuery(id+"F9.wireOp",EDGE,"E2618"),sQuery(id+"F9.wireOp",EDGE,"E2619"),sQuery(id+"F9.wireOp",EDGE,"E2620"),sQuery(id+"F9.wireOp",EDGE,"E2621"),sQuery(id+"F9.wireOp",EDGE,"E2622"),sQuery(id+"F9.wireOp",EDGE,"E2623"),sQuery(id+"F9.wireOp",EDGE,"E2624"),sQuery(id+"F9.wireOp",EDGE,"E2625"),sQuery(id+"F9.wireOp",EDGE,"E2626"),sQuery(id+"F9.wireOp",EDGE,"E2627"),sQuery(id+"F9.wireOp",EDGE,"E2628"),sQuery(id+"F9.wireOp",EDGE,"E2629"),sQuery(id+"F9.wireOp",EDGE,"E2630"),sQuery(id+"F9.wireOp",EDGE,"E2631"),sQuery(id+"F9.wireOp",EDGE,"E2632"),sQuery(id+"F9.wireOp",EDGE,"E2633"),sQuery(id+"F9.wireOp",EDGE,"E2634"),sQuery(id+"F9.wireOp",EDGE,"E2635"),sQuery(id+"F9.wireOp",EDGE,"E2636"),sQuery(id+"F9.wireOp",EDGE,"E2637"),sQuery(id+"F9.wireOp",EDGE,"E2638"),sQuery(id+"F9.wireOp",EDGE,"E2639"),sQuery(id+"F9.wireOp",EDGE,"E2640"),sQuery(id+"F9.wireOp",EDGE,"E2641"),sQuery(id+"F9.wireOp",EDGE,"E2642"),sQuery(id+"F9.wireOp",EDGE,"E2643"),sQuery(id+"F9.wireOp",EDGE,"E2644"),sQuery(id+"F9.wireOp",EDGE,"E2645"),sQuery(id+"F9.wireOp",EDGE,"E2646"),sQuery(id+"F9.wireOp",EDGE,"E2647"),sQuery(id+"F9.wireOp",EDGE,"E2648"),sQuery(id+"F9.wireOp",EDGE,"E2649"),sQuery(id+"F9.wireOp",EDGE,"E2650"),sQuery(id+"F9.wireOp",EDGE,"E2651"),sQuery(id+"F9.wireOp",EDGE,"E2652"),sQuery(id+"F9.wireOp",EDGE,"E2653"),sQuery(id+"F9.wireOp",EDGE,"E2654"),sQuery(id+"F9.wireOp",EDGE,"E2655"),sQuery(id+"F9.wireOp",EDGE,"E2656"),sQuery(id+"F9.wireOp",EDGE,"E2657"),sQuery(id+"F9.wireOp",EDGE,"E2658"),sQuery(id+"F9.wireOp",EDGE,"E2659"),sQuery(id+"F9.wireOp",EDGE,"E2660"),sQuery(id+"F9.wireOp",EDGE,"E2661"),sQuery(id+"F9.wireOp",EDGE,"E2662"),sQuery(id+"F9.wireOp",EDGE,"E2663"),sQuery(id+"F9.wireOp",EDGE,"E2664"),sQuery(id+"F9.wireOp",EDGE,"E2665"),sQuery(id+"F9.wireOp",EDGE,"E2666"),sQuery(id+"F9.wireOp",EDGE,"E2667"),sQuery(id+"F9.wireOp",EDGE,"E2668"),sQuery(id+"F9.wireOp",EDGE,"E2669"),sQuery(id+"F9.wireOp",EDGE,"E2670"),sQuery(id+"F9.wireOp",EDGE,"E2671"),sQuery(id+"F9.wireOp",EDGE,"E2672"),sQuery(id+"F9.wireOp",EDGE,"E2673"),sQuery(id+"F9.wireOp",EDGE,"E2674"),sQuery(id+"F9.wireOp",EDGE,"E2675"),sQuery(id+"F9.wireOp",EDGE,"E2676"),sQuery(id+"F9.wireOp",EDGE,"E2677"),sQuery(id+"F9.wireOp",EDGE,"E2678"),sQuery(id+"F9.wireOp",EDGE,"E2679"),sQuery(id+"F9.wireOp",EDGE,"E2680"),sQuery(id+"F9.wireOp",EDGE,"E2681"),sQuery(id+"F9.wireOp",EDGE,"E2682"),sQuery(id+"F9.wireOp",EDGE,"E2683"),sQuery(id+"F9.wireOp",EDGE,"E2684"),sQuery(id+"F9.wireOp",EDGE,"E2685"),sQuery(id+"F9.wireOp",EDGE,"E2686"),sQuery(id+"F9.wireOp",EDGE,"E2687"),sQuery(id+"F9.wireOp",EDGE,"E2688"),sQuery(id+"F9.wireOp",EDGE,"E2689"),sQuery(id+"F9.wireOp",EDGE,"E2690"),sQuery(id+"F9.wireOp",EDGE,"E2691"),sQuery(id+"F9.wireOp",EDGE,"E2692"),sQuery(id+"F9.wireOp",EDGE,"E2693"),sQuery(id+"F9.wireOp",EDGE,"E2694"),sQuery(id+"F9.wireOp",EDGE,"E2695"),sQuery(id+"F9.wireOp",EDGE,"E2696"),sQuery(id+"F9.wireOp",EDGE,"E2697"),sQuery(id+"F9.wireOp",EDGE,"E2698"),sQuery(id+"F9.wireOp",EDGE,"E2699"),sQuery(id+"F9.wireOp",EDGE,"E2700"),sQuery(id+"F9.wireOp",EDGE,"E2701"),sQuery(id+"F9.wireOp",EDGE,"E2702"),sQuery(id+"F9.wireOp",EDGE,"E2703")])],"isStart":false});
            var sketch = newSketch(context, id + "F11", { "sketchPlane" : qUnion([Q0])});
            skLineSegment(sketch, "E2704", {"start": v(80.77, -41.63) * mm, "end": v(82.15, -41.63) * mm});
            skLineSegment(sketch, "E2705", {"start": v(82.15, -41.63) * mm, "end": v(85.62, -47.63) * mm});
            skLineSegment(sketch, "E2706", {"start": v(85.62, -47.63) * mm, "end": v(78.7, -47.63) * mm});
            skLineSegment(sketch, "E2707", {"start": v(78.7, -47.63) * mm, "end": v(80.6, -44.33) * mm});
            skLineSegment(sketch, "E2708", {"start": v(80.6, -44.33) * mm, "end": v(81.98, -44.33) * mm});
            skLineSegment(sketch, "E2709", {"start": v(81.98, -44.33) * mm, "end": v(80.77, -46.43) * mm});
            skLineSegment(sketch, "E2710", {"start": v(80.77, -46.43) * mm, "end": v(83.54, -46.43) * mm});
            skLineSegment(sketch, "E2711", {"start": v(83.54, -46.43) * mm, "end": v(80.77, -41.63) * mm});
            skLineSegment(sketch, "E2712", {"start": v(82.45, -41.63) * mm, "end": v(85.92, -47.63) * mm});
            skLineSegment(sketch, "E2713", {"start": v(85.92, -47.63) * mm, "end": v(87.81, -47.63) * mm});
            skLineSegment(sketch, "E2714", {"start": v(87.81, -47.63) * mm, "end": v(87.81, -43.13) * mm});
            skLineSegment(sketch, "E2715", {"start": v(87.81, -43.13) * mm, "end": v(86.61, -43.13) * mm});
            skLineSegment(sketch, "E2716", {"start": v(86.61, -43.13) * mm, "end": v(86.61, -46.43) * mm});
            skLineSegment(sketch, "E2717", {"start": v(87.81, -41.63) * mm, "end": v(82.45, -41.63) * mm});
            skLineSegment(sketch, "E2718", {"start": v(86.61, -46.43) * mm, "end": v(84.53, -42.83) * mm});
            skLineSegment(sketch, "E2719", {"start": v(84.53, -42.83) * mm, "end": v(87.81, -42.83) * mm});
            skLineSegment(sketch, "E2720", {"start": v(87.81, -42.83) * mm, "end": v(87.81, -41.63) * mm});
            skLineSegment(sketch, "E2721", {"start": v(88.11, -41.63) * mm, "end": v(88.11, -47.63) * mm});
            skLineSegment(sketch, "E2722", {"start": v(88.11, -47.63) * mm, "end": v(89.31, -47.63) * mm});
            skLineSegment(sketch, "E2723", {"start": v(89.61, -44.33) * mm, "end": v(91.17, -47.63) * mm});
            skLineSegment(sketch, "E2724", {"start": v(91.17, -47.63) * mm, "end": v(92.56, -47.63) * mm});
            skLineSegment(sketch, "E2725", {"start": v(92.56, -47.63) * mm, "end": v(91, -44.33) * mm});
            skLineSegment(sketch, "E2726", {"start": v(91, -44.33) * mm, "end": v(92.56, -41.63) * mm});
            skLineSegment(sketch, "E2727", {"start": v(92.56, -41.63) * mm, "end": v(91.17, -41.63) * mm});
            skLineSegment(sketch, "E2728", {"start": v(91.17, -41.63) * mm, "end": v(89.61, -44.33) * mm});
            skLineSegment(sketch, "E2729", {"start": v(89.31, -41.63) * mm, "end": v(88.11, -41.63) * mm});
            skLineSegment(sketch, "E2730", {"start": v(92.86, -41.63) * mm, "end": v(92.86, -47.63) * mm});
            skLineSegment(sketch, "E2731", {"start": v(92.86, -47.63) * mm, "end": v(97.52, -47.63) * mm});
            skLineSegment(sketch, "E2732", {"start": v(97.52, -47.63) * mm, "end": v(94.06, -41.63) * mm});
            skLineSegment(sketch, "E2733", {"start": v(94.06, -41.63) * mm, "end": v(92.86, -41.63) * mm});
            skLineSegment(sketch, "E2734", {"start": v(94.06, -44.03) * mm, "end": v(94.06, -44.93) * mm});
            skLineSegment(sketch, "E2735", {"start": v(94.06, -44.93) * mm, "end": v(94.58, -44.93) * mm});
            skLineSegment(sketch, "E2736", {"start": v(94.58, -44.93) * mm, "end": v(94.06, -44.03) * mm});
            skLineSegment(sketch, "E2737", {"start": v(94.06, -45.23) * mm, "end": v(94.06, -46.43) * mm});
            skLineSegment(sketch, "E2738", {"start": v(94.06, -46.43) * mm, "end": v(95.44, -46.43) * mm});
            skLineSegment(sketch, "E2739", {"start": v(95.44, -46.43) * mm, "end": v(94.75, -45.23) * mm});
            skLineSegment(sketch, "E2740", {"start": v(94.75, -45.23) * mm, "end": v(94.06, -45.23) * mm});
            skPoint(sketch, "E2741.0", {"position": v(76.2, -47.63) * mm});
            skPoint(sketch, "E2742.0", {"position": v(100.01, -47.63) * mm});
            skLineSegment(sketch, "E2743", {"start": v(76.2, -47.63) * mm, "end": v(78.7, -47.63) * mm, "construction": true});
            skLineSegment(sketch, "E2744", {"start": v(97.52, -47.63) * mm, "end": v(100.01, -47.63) * mm, "construction": true});
            skLineSegment(sketch, "E2745", {"start": v(89.31, -41.63) * mm, "end": v(89.31, -47.63) * mm});
            skSolve(sketch);
        }
        {
            var Q0;
            Q0 = qSketchRegion(id + "F11", true);
            extrude(context, id + "F12", {"entities" : qUnion([Q0]), "operationType" : NewBodyOperationType.REMOVE, "oppositeDirection" : true, "depth" : 0.2 * mm, "offsetDistance" : 25 * mm});
        }
    });
